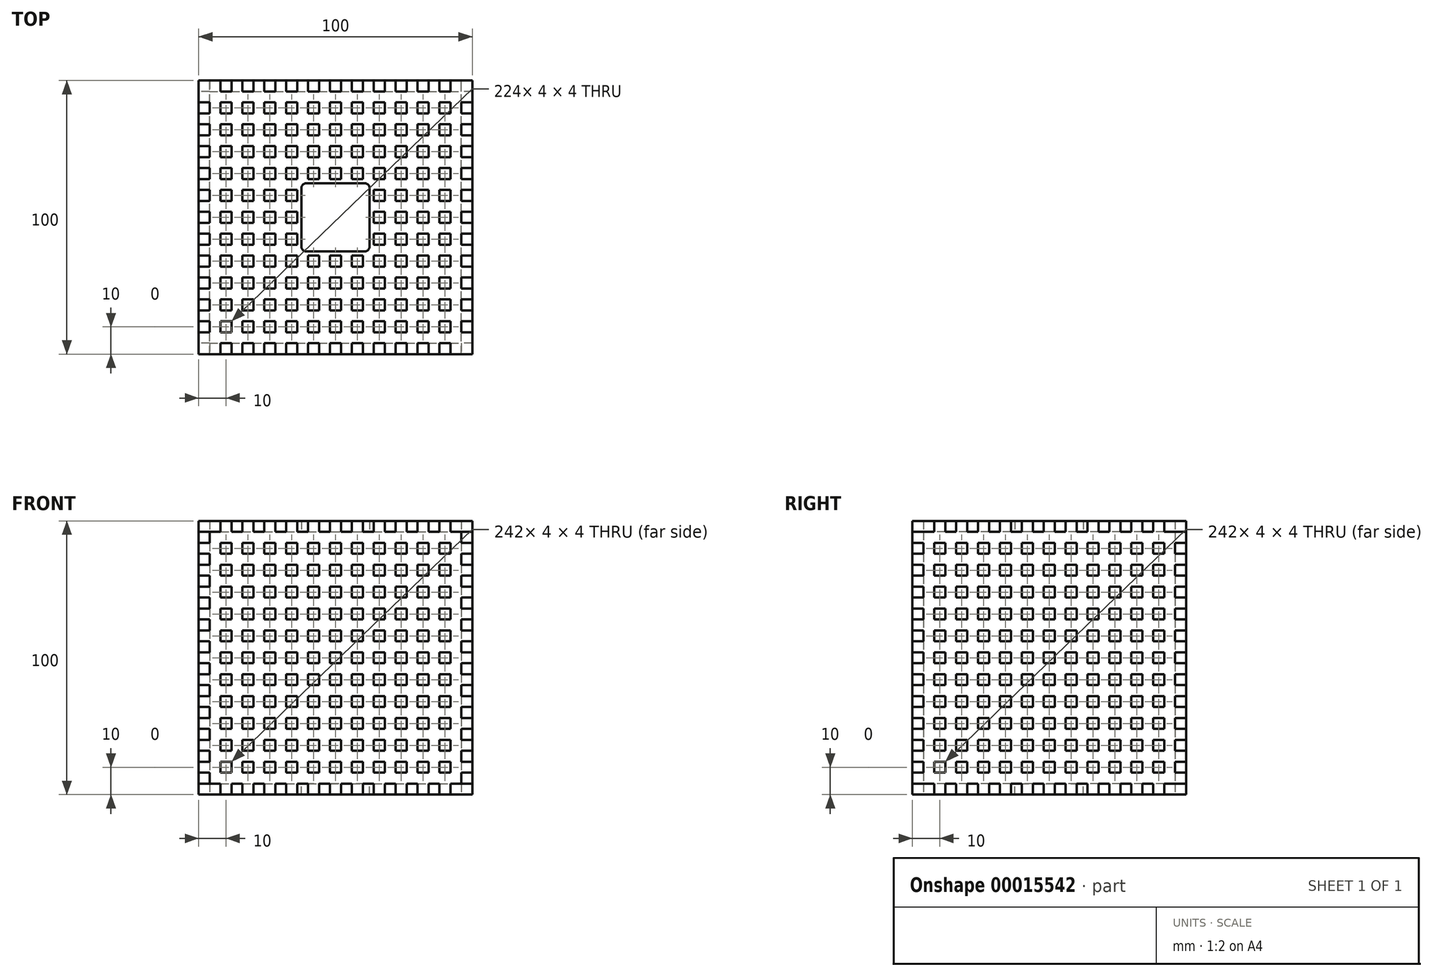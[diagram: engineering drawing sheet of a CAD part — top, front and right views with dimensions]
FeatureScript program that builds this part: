
annotation { "Feature Type Name" : "Feature", "Feature Type Description" : "" }
export const myFeature = defineFeature(function(context is Context, id is Id, definition is map)
    precondition{}
    {
        {
            var Q0;
            Q0=qCreatedBy(makeId("Top.planeOp"),FACE);
            var sketch = newSketch(context, id + "F0", { "sketchPlane" : qUnion([Q0])});
            skLineSegment(sketch, "E0.bottom", {"start": v(-50, 50) * mm, "end": v(-46, 50) * mm});
            skLineSegment(sketch, "E0.top", {"start": v(-50, 46) * mm, "end": v(-46, 46) * mm});
            skLineSegment(sketch, "E0.left", {"start": v(-50, 50) * mm, "end": v(-50, 46) * mm});
            skLineSegment(sketch, "E0.right", {"start": v(-46, 50) * mm, "end": v(-46, 46) * mm});
            skLineSegment(sketch, "E1.0.1.4", {"start": v(-46, 42) * mm, "end": v(-46, 38) * mm});
            skLineSegment(sketch, "E1.0.1.6", {"start": v(-50, 42) * mm, "end": v(-50, 38) * mm});
            skLineSegment(sketch, "E1.0.1.8", {"start": v(-50, 38) * mm, "end": v(-46, 38) * mm});
            skLineSegment(sketch, "E1.0.1.10", {"start": v(-50, 42) * mm, "end": v(-46, 42) * mm});
            skLineSegment(sketch, "E1.0.2.4", {"start": v(-46, 34) * mm, "end": v(-46, 30) * mm});
            skLineSegment(sketch, "E1.0.2.6", {"start": v(-50, 34) * mm, "end": v(-50, 30) * mm});
            skLineSegment(sketch, "E1.0.2.8", {"start": v(-50, 30) * mm, "end": v(-46, 30) * mm});
            skLineSegment(sketch, "E1.0.2.10", {"start": v(-50, 34) * mm, "end": v(-46, 34) * mm});
            skLineSegment(sketch, "E1.0.3.4", {"start": v(-46, 26) * mm, "end": v(-46, 22) * mm});
            skLineSegment(sketch, "E1.0.3.6", {"start": v(-50, 26) * mm, "end": v(-50, 22) * mm});
            skLineSegment(sketch, "E1.0.3.8", {"start": v(-50, 22) * mm, "end": v(-46, 22) * mm});
            skLineSegment(sketch, "E1.0.3.10", {"start": v(-50, 26) * mm, "end": v(-46, 26) * mm});
            skLineSegment(sketch, "E1.0.4.4", {"start": v(-46, 18) * mm, "end": v(-46, 14) * mm});
            skLineSegment(sketch, "E1.0.4.6", {"start": v(-50, 18) * mm, "end": v(-50, 14) * mm});
            skLineSegment(sketch, "E1.0.4.8", {"start": v(-50, 14) * mm, "end": v(-46, 14) * mm});
            skLineSegment(sketch, "E1.0.4.10", {"start": v(-50, 18) * mm, "end": v(-46, 18) * mm});
            skLineSegment(sketch, "E1.0.5.4", {"start": v(-46, 10) * mm, "end": v(-46, 6) * mm});
            skLineSegment(sketch, "E1.0.5.6", {"start": v(-50, 10) * mm, "end": v(-50, 6) * mm});
            skLineSegment(sketch, "E1.0.5.8", {"start": v(-50, 6) * mm, "end": v(-46, 6) * mm});
            skLineSegment(sketch, "E1.0.5.10", {"start": v(-50, 10) * mm, "end": v(-46, 10) * mm});
            skLineSegment(sketch, "E1.0.6.4", {"start": v(-46, 2) * mm, "end": v(-46, -2) * mm});
            skLineSegment(sketch, "E1.0.6.6", {"start": v(-50, 2) * mm, "end": v(-50, -2) * mm});
            skLineSegment(sketch, "E1.0.6.8", {"start": v(-50, -2) * mm, "end": v(-46, -2) * mm});
            skLineSegment(sketch, "E1.0.6.10", {"start": v(-50, 2) * mm, "end": v(-46, 2) * mm});
            skLineSegment(sketch, "E1.0.7.4", {"start": v(-46, -6) * mm, "end": v(-46, -10) * mm});
            skLineSegment(sketch, "E1.0.7.6", {"start": v(-50, -6) * mm, "end": v(-50, -10) * mm});
            skLineSegment(sketch, "E1.0.7.8", {"start": v(-50, -10) * mm, "end": v(-46, -10) * mm});
            skLineSegment(sketch, "E1.0.7.10", {"start": v(-50, -6) * mm, "end": v(-46, -6) * mm});
            skLineSegment(sketch, "E1.0.8.4", {"start": v(-46, -14) * mm, "end": v(-46, -18) * mm});
            skLineSegment(sketch, "E1.0.8.6", {"start": v(-50, -14) * mm, "end": v(-50, -18) * mm});
            skLineSegment(sketch, "E1.0.8.8", {"start": v(-50, -18) * mm, "end": v(-46, -18) * mm});
            skLineSegment(sketch, "E1.0.8.10", {"start": v(-50, -14) * mm, "end": v(-46, -14) * mm});
            skLineSegment(sketch, "E1.0.9.4", {"start": v(-46, -22) * mm, "end": v(-46, -26) * mm});
            skLineSegment(sketch, "E1.0.9.6", {"start": v(-50, -22) * mm, "end": v(-50, -26) * mm});
            skLineSegment(sketch, "E1.0.9.8", {"start": v(-50, -26) * mm, "end": v(-46, -26) * mm});
            skLineSegment(sketch, "E1.0.9.10", {"start": v(-50, -22) * mm, "end": v(-46, -22) * mm});
            skLineSegment(sketch, "E1.0.10.4", {"start": v(-46, -30) * mm, "end": v(-46, -34) * mm});
            skLineSegment(sketch, "E1.0.10.6", {"start": v(-50, -30) * mm, "end": v(-50, -34) * mm});
            skLineSegment(sketch, "E1.0.10.8", {"start": v(-50, -34) * mm, "end": v(-46, -34) * mm});
            skLineSegment(sketch, "E1.0.10.10", {"start": v(-50, -30) * mm, "end": v(-46, -30) * mm});
            skLineSegment(sketch, "E1.0.11.4", {"start": v(-46, -38) * mm, "end": v(-46, -42) * mm});
            skLineSegment(sketch, "E1.0.11.6", {"start": v(-50, -38) * mm, "end": v(-50, -42) * mm});
            skLineSegment(sketch, "E1.0.11.8", {"start": v(-50, -42) * mm, "end": v(-46, -42) * mm});
            skLineSegment(sketch, "E1.0.11.10", {"start": v(-50, -38) * mm, "end": v(-46, -38) * mm});
            skLineSegment(sketch, "E1.0.12.4", {"start": v(-46, -46) * mm, "end": v(-46, -50) * mm});
            skLineSegment(sketch, "E1.0.12.6", {"start": v(-50, -46) * mm, "end": v(-50, -50) * mm});
            skLineSegment(sketch, "E1.0.12.8", {"start": v(-50, -50) * mm, "end": v(-46, -50) * mm});
            skLineSegment(sketch, "E1.0.12.10", {"start": v(-50, -46) * mm, "end": v(-46, -46) * mm});
            skLineSegment(sketch, "E1.1.0.4", {"start": v(-38, 50) * mm, "end": v(-38, 46) * mm});
            skLineSegment(sketch, "E1.1.0.6", {"start": v(-42, 50) * mm, "end": v(-42, 46) * mm});
            skLineSegment(sketch, "E1.1.0.8", {"start": v(-42, 46) * mm, "end": v(-38, 46) * mm});
            skLineSegment(sketch, "E1.1.0.10", {"start": v(-42, 50) * mm, "end": v(-38, 50) * mm});
            skLineSegment(sketch, "E1.1.1.4", {"start": v(-38, 42) * mm, "end": v(-38, 38) * mm});
            skLineSegment(sketch, "E1.1.1.6", {"start": v(-42, 42) * mm, "end": v(-42, 38) * mm});
            skLineSegment(sketch, "E1.1.1.8", {"start": v(-42, 38) * mm, "end": v(-38, 38) * mm});
            skLineSegment(sketch, "E1.1.1.10", {"start": v(-42, 42) * mm, "end": v(-38, 42) * mm});
            skLineSegment(sketch, "E1.1.2.4", {"start": v(-38, 34) * mm, "end": v(-38, 30) * mm});
            skLineSegment(sketch, "E1.1.2.6", {"start": v(-42, 34) * mm, "end": v(-42, 30) * mm});
            skLineSegment(sketch, "E1.1.2.8", {"start": v(-42, 30) * mm, "end": v(-38, 30) * mm});
            skLineSegment(sketch, "E1.1.2.10", {"start": v(-42, 34) * mm, "end": v(-38, 34) * mm});
            skLineSegment(sketch, "E1.1.3.4", {"start": v(-38, 26) * mm, "end": v(-38, 22) * mm});
            skLineSegment(sketch, "E1.1.3.6", {"start": v(-42, 26) * mm, "end": v(-42, 22) * mm});
            skLineSegment(sketch, "E1.1.3.8", {"start": v(-42, 22) * mm, "end": v(-38, 22) * mm});
            skLineSegment(sketch, "E1.1.3.10", {"start": v(-42, 26) * mm, "end": v(-38, 26) * mm});
            skLineSegment(sketch, "E1.1.4.4", {"start": v(-38, 18) * mm, "end": v(-38, 14) * mm});
            skLineSegment(sketch, "E1.1.4.6", {"start": v(-42, 18) * mm, "end": v(-42, 14) * mm});
            skLineSegment(sketch, "E1.1.4.8", {"start": v(-42, 14) * mm, "end": v(-38, 14) * mm});
            skLineSegment(sketch, "E1.1.4.10", {"start": v(-42, 18) * mm, "end": v(-38, 18) * mm});
            skLineSegment(sketch, "E1.1.5.4", {"start": v(-38, 10) * mm, "end": v(-38, 6) * mm});
            skLineSegment(sketch, "E1.1.5.6", {"start": v(-42, 10) * mm, "end": v(-42, 6) * mm});
            skLineSegment(sketch, "E1.1.5.8", {"start": v(-42, 6) * mm, "end": v(-38, 6) * mm});
            skLineSegment(sketch, "E1.1.5.10", {"start": v(-42, 10) * mm, "end": v(-38, 10) * mm});
            skLineSegment(sketch, "E1.1.6.4", {"start": v(-38, 2) * mm, "end": v(-38, -2) * mm});
            skLineSegment(sketch, "E1.1.6.6", {"start": v(-42, 2) * mm, "end": v(-42, -2) * mm});
            skLineSegment(sketch, "E1.1.6.8", {"start": v(-42, -2) * mm, "end": v(-38, -2) * mm});
            skLineSegment(sketch, "E1.1.6.10", {"start": v(-42, 2) * mm, "end": v(-38, 2) * mm});
            skLineSegment(sketch, "E1.1.7.4", {"start": v(-38, -6) * mm, "end": v(-38, -10) * mm});
            skLineSegment(sketch, "E1.1.7.6", {"start": v(-42, -6) * mm, "end": v(-42, -10) * mm});
            skLineSegment(sketch, "E1.1.7.8", {"start": v(-42, -10) * mm, "end": v(-38, -10) * mm});
            skLineSegment(sketch, "E1.1.7.10", {"start": v(-42, -6) * mm, "end": v(-38, -6) * mm});
            skLineSegment(sketch, "E1.1.8.4", {"start": v(-38, -14) * mm, "end": v(-38, -18) * mm});
            skLineSegment(sketch, "E1.1.8.6", {"start": v(-42, -14) * mm, "end": v(-42, -18) * mm});
            skLineSegment(sketch, "E1.1.8.8", {"start": v(-42, -18) * mm, "end": v(-38, -18) * mm});
            skLineSegment(sketch, "E1.1.8.10", {"start": v(-42, -14) * mm, "end": v(-38, -14) * mm});
            skLineSegment(sketch, "E1.1.9.4", {"start": v(-38, -22) * mm, "end": v(-38, -26) * mm});
            skLineSegment(sketch, "E1.1.9.6", {"start": v(-42, -22) * mm, "end": v(-42, -26) * mm});
            skLineSegment(sketch, "E1.1.9.8", {"start": v(-42, -26) * mm, "end": v(-38, -26) * mm});
            skLineSegment(sketch, "E1.1.9.10", {"start": v(-42, -22) * mm, "end": v(-38, -22) * mm});
            skLineSegment(sketch, "E1.1.10.4", {"start": v(-38, -30) * mm, "end": v(-38, -34) * mm});
            skLineSegment(sketch, "E1.1.10.6", {"start": v(-42, -30) * mm, "end": v(-42, -34) * mm});
            skLineSegment(sketch, "E1.1.10.8", {"start": v(-42, -34) * mm, "end": v(-38, -34) * mm});
            skLineSegment(sketch, "E1.1.10.10", {"start": v(-42, -30) * mm, "end": v(-38, -30) * mm});
            skLineSegment(sketch, "E1.1.11.4", {"start": v(-38, -38) * mm, "end": v(-38, -42) * mm});
            skLineSegment(sketch, "E1.1.11.6", {"start": v(-42, -38) * mm, "end": v(-42, -42) * mm});
            skLineSegment(sketch, "E1.1.11.8", {"start": v(-42, -42) * mm, "end": v(-38, -42) * mm});
            skLineSegment(sketch, "E1.1.11.10", {"start": v(-42, -38) * mm, "end": v(-38, -38) * mm});
            skLineSegment(sketch, "E1.1.12.4", {"start": v(-38, -46) * mm, "end": v(-38, -50) * mm});
            skLineSegment(sketch, "E1.1.12.6", {"start": v(-42, -46) * mm, "end": v(-42, -50) * mm});
            skLineSegment(sketch, "E1.1.12.8", {"start": v(-42, -50) * mm, "end": v(-38, -50) * mm});
            skLineSegment(sketch, "E1.1.12.10", {"start": v(-42, -46) * mm, "end": v(-38, -46) * mm});
            skLineSegment(sketch, "E1.2.0.4", {"start": v(-30, 50) * mm, "end": v(-30, 46) * mm});
            skLineSegment(sketch, "E1.2.0.6", {"start": v(-34, 50) * mm, "end": v(-34, 46) * mm});
            skLineSegment(sketch, "E1.2.0.8", {"start": v(-34, 46) * mm, "end": v(-30, 46) * mm});
            skLineSegment(sketch, "E1.2.0.10", {"start": v(-34, 50) * mm, "end": v(-30, 50) * mm});
            skLineSegment(sketch, "E1.2.1.4", {"start": v(-30, 42) * mm, "end": v(-30, 38) * mm});
            skLineSegment(sketch, "E1.2.1.6", {"start": v(-34, 42) * mm, "end": v(-34, 38) * mm});
            skLineSegment(sketch, "E1.2.1.8", {"start": v(-34, 38) * mm, "end": v(-30, 38) * mm});
            skLineSegment(sketch, "E1.2.1.10", {"start": v(-34, 42) * mm, "end": v(-30, 42) * mm});
            skLineSegment(sketch, "E1.2.2.4", {"start": v(-30, 34) * mm, "end": v(-30, 30) * mm});
            skLineSegment(sketch, "E1.2.2.6", {"start": v(-34, 34) * mm, "end": v(-34, 30) * mm});
            skLineSegment(sketch, "E1.2.2.8", {"start": v(-34, 30) * mm, "end": v(-30, 30) * mm});
            skLineSegment(sketch, "E1.2.2.10", {"start": v(-34, 34) * mm, "end": v(-30, 34) * mm});
            skLineSegment(sketch, "E1.2.3.4", {"start": v(-30, 26) * mm, "end": v(-30, 22) * mm});
            skLineSegment(sketch, "E1.2.3.6", {"start": v(-34, 26) * mm, "end": v(-34, 22) * mm});
            skLineSegment(sketch, "E1.2.3.8", {"start": v(-34, 22) * mm, "end": v(-30, 22) * mm});
            skLineSegment(sketch, "E1.2.3.10", {"start": v(-34, 26) * mm, "end": v(-30, 26) * mm});
            skLineSegment(sketch, "E1.2.4.4", {"start": v(-30, 18) * mm, "end": v(-30, 14) * mm});
            skLineSegment(sketch, "E1.2.4.6", {"start": v(-34, 18) * mm, "end": v(-34, 14) * mm});
            skLineSegment(sketch, "E1.2.4.8", {"start": v(-34, 14) * mm, "end": v(-30, 14) * mm});
            skLineSegment(sketch, "E1.2.4.10", {"start": v(-34, 18) * mm, "end": v(-30, 18) * mm});
            skLineSegment(sketch, "E1.2.5.4", {"start": v(-30, 10) * mm, "end": v(-30, 6) * mm});
            skLineSegment(sketch, "E1.2.5.6", {"start": v(-34, 10) * mm, "end": v(-34, 6) * mm});
            skLineSegment(sketch, "E1.2.5.8", {"start": v(-34, 6) * mm, "end": v(-30, 6) * mm});
            skLineSegment(sketch, "E1.2.5.10", {"start": v(-34, 10) * mm, "end": v(-30, 10) * mm});
            skLineSegment(sketch, "E1.2.6.4", {"start": v(-30, 2) * mm, "end": v(-30, -2) * mm});
            skLineSegment(sketch, "E1.2.6.6", {"start": v(-34, 2) * mm, "end": v(-34, -2) * mm});
            skLineSegment(sketch, "E1.2.6.8", {"start": v(-34, -2) * mm, "end": v(-30, -2) * mm});
            skLineSegment(sketch, "E1.2.6.10", {"start": v(-34, 2) * mm, "end": v(-30, 2) * mm});
            skLineSegment(sketch, "E1.2.7.4", {"start": v(-30, -6) * mm, "end": v(-30, -10) * mm});
            skLineSegment(sketch, "E1.2.7.6", {"start": v(-34, -6) * mm, "end": v(-34, -10) * mm});
            skLineSegment(sketch, "E1.2.7.8", {"start": v(-34, -10) * mm, "end": v(-30, -10) * mm});
            skLineSegment(sketch, "E1.2.7.10", {"start": v(-34, -6) * mm, "end": v(-30, -6) * mm});
            skLineSegment(sketch, "E1.2.8.4", {"start": v(-30, -14) * mm, "end": v(-30, -18) * mm});
            skLineSegment(sketch, "E1.2.8.6", {"start": v(-34, -14) * mm, "end": v(-34, -18) * mm});
            skLineSegment(sketch, "E1.2.8.8", {"start": v(-34, -18) * mm, "end": v(-30, -18) * mm});
            skLineSegment(sketch, "E1.2.8.10", {"start": v(-34, -14) * mm, "end": v(-30, -14) * mm});
            skLineSegment(sketch, "E1.2.9.4", {"start": v(-30, -22) * mm, "end": v(-30, -26) * mm});
            skLineSegment(sketch, "E1.2.9.6", {"start": v(-34, -22) * mm, "end": v(-34, -26) * mm});
            skLineSegment(sketch, "E1.2.9.8", {"start": v(-34, -26) * mm, "end": v(-30, -26) * mm});
            skLineSegment(sketch, "E1.2.9.10", {"start": v(-34, -22) * mm, "end": v(-30, -22) * mm});
            skLineSegment(sketch, "E1.2.10.4", {"start": v(-30, -30) * mm, "end": v(-30, -34) * mm});
            skLineSegment(sketch, "E1.2.10.6", {"start": v(-34, -30) * mm, "end": v(-34, -34) * mm});
            skLineSegment(sketch, "E1.2.10.8", {"start": v(-34, -34) * mm, "end": v(-30, -34) * mm});
            skLineSegment(sketch, "E1.2.10.10", {"start": v(-34, -30) * mm, "end": v(-30, -30) * mm});
            skLineSegment(sketch, "E1.2.11.4", {"start": v(-30, -38) * mm, "end": v(-30, -42) * mm});
            skLineSegment(sketch, "E1.2.11.6", {"start": v(-34, -38) * mm, "end": v(-34, -42) * mm});
            skLineSegment(sketch, "E1.2.11.8", {"start": v(-34, -42) * mm, "end": v(-30, -42) * mm});
            skLineSegment(sketch, "E1.2.11.10", {"start": v(-34, -38) * mm, "end": v(-30, -38) * mm});
            skLineSegment(sketch, "E1.2.12.4", {"start": v(-30, -46) * mm, "end": v(-30, -50) * mm});
            skLineSegment(sketch, "E1.2.12.6", {"start": v(-34, -46) * mm, "end": v(-34, -50) * mm});
            skLineSegment(sketch, "E1.2.12.8", {"start": v(-34, -50) * mm, "end": v(-30, -50) * mm});
            skLineSegment(sketch, "E1.2.12.10", {"start": v(-34, -46) * mm, "end": v(-30, -46) * mm});
            skLineSegment(sketch, "E1.3.0.4", {"start": v(-22, 50) * mm, "end": v(-22, 46) * mm});
            skLineSegment(sketch, "E1.3.0.6", {"start": v(-26, 50) * mm, "end": v(-26, 46) * mm});
            skLineSegment(sketch, "E1.3.0.8", {"start": v(-26, 46) * mm, "end": v(-22, 46) * mm});
            skLineSegment(sketch, "E1.3.0.10", {"start": v(-26, 50) * mm, "end": v(-22, 50) * mm});
            skLineSegment(sketch, "E1.3.1.4", {"start": v(-22, 42) * mm, "end": v(-22, 38) * mm});
            skLineSegment(sketch, "E1.3.1.6", {"start": v(-26, 42) * mm, "end": v(-26, 38) * mm});
            skLineSegment(sketch, "E1.3.1.8", {"start": v(-26, 38) * mm, "end": v(-22, 38) * mm});
            skLineSegment(sketch, "E1.3.1.10", {"start": v(-26, 42) * mm, "end": v(-22, 42) * mm});
            skLineSegment(sketch, "E1.3.2.4", {"start": v(-22, 34) * mm, "end": v(-22, 30) * mm});
            skLineSegment(sketch, "E1.3.2.6", {"start": v(-26, 34) * mm, "end": v(-26, 30) * mm});
            skLineSegment(sketch, "E1.3.2.8", {"start": v(-26, 30) * mm, "end": v(-22, 30) * mm});
            skLineSegment(sketch, "E1.3.2.10", {"start": v(-26, 34) * mm, "end": v(-22, 34) * mm});
            skLineSegment(sketch, "E1.3.3.4", {"start": v(-22, 26) * mm, "end": v(-22, 22) * mm});
            skLineSegment(sketch, "E1.3.3.6", {"start": v(-26, 26) * mm, "end": v(-26, 22) * mm});
            skLineSegment(sketch, "E1.3.3.8", {"start": v(-26, 22) * mm, "end": v(-22, 22) * mm});
            skLineSegment(sketch, "E1.3.3.10", {"start": v(-26, 26) * mm, "end": v(-22, 26) * mm});
            skLineSegment(sketch, "E1.3.4.4", {"start": v(-22, 18) * mm, "end": v(-22, 14) * mm});
            skLineSegment(sketch, "E1.3.4.6", {"start": v(-26, 18) * mm, "end": v(-26, 14) * mm});
            skLineSegment(sketch, "E1.3.4.8", {"start": v(-26, 14) * mm, "end": v(-22, 14) * mm});
            skLineSegment(sketch, "E1.3.4.10", {"start": v(-26, 18) * mm, "end": v(-22, 18) * mm});
            skLineSegment(sketch, "E1.3.5.4", {"start": v(-22, 10) * mm, "end": v(-22, 6) * mm});
            skLineSegment(sketch, "E1.3.5.6", {"start": v(-26, 10) * mm, "end": v(-26, 6) * mm});
            skLineSegment(sketch, "E1.3.5.8", {"start": v(-26, 6) * mm, "end": v(-22, 6) * mm});
            skLineSegment(sketch, "E1.3.5.10", {"start": v(-26, 10) * mm, "end": v(-22, 10) * mm});
            skLineSegment(sketch, "E1.3.6.4", {"start": v(-22, 2) * mm, "end": v(-22, -2) * mm});
            skLineSegment(sketch, "E1.3.6.6", {"start": v(-26, 2) * mm, "end": v(-26, -2) * mm});
            skLineSegment(sketch, "E1.3.6.8", {"start": v(-26, -2) * mm, "end": v(-22, -2) * mm});
            skLineSegment(sketch, "E1.3.6.10", {"start": v(-26, 2) * mm, "end": v(-22, 2) * mm});
            skLineSegment(sketch, "E1.3.7.4", {"start": v(-22, -6) * mm, "end": v(-22, -10) * mm});
            skLineSegment(sketch, "E1.3.7.6", {"start": v(-26, -6) * mm, "end": v(-26, -10) * mm});
            skLineSegment(sketch, "E1.3.7.8", {"start": v(-26, -10) * mm, "end": v(-22, -10) * mm});
            skLineSegment(sketch, "E1.3.7.10", {"start": v(-26, -6) * mm, "end": v(-22, -6) * mm});
            skLineSegment(sketch, "E1.3.8.4", {"start": v(-22, -14) * mm, "end": v(-22, -18) * mm});
            skLineSegment(sketch, "E1.3.8.6", {"start": v(-26, -14) * mm, "end": v(-26, -18) * mm});
            skLineSegment(sketch, "E1.3.8.8", {"start": v(-26, -18) * mm, "end": v(-22, -18) * mm});
            skLineSegment(sketch, "E1.3.8.10", {"start": v(-26, -14) * mm, "end": v(-22, -14) * mm});
            skLineSegment(sketch, "E1.3.9.4", {"start": v(-22, -22) * mm, "end": v(-22, -26) * mm});
            skLineSegment(sketch, "E1.3.9.6", {"start": v(-26, -22) * mm, "end": v(-26, -26) * mm});
            skLineSegment(sketch, "E1.3.9.8", {"start": v(-26, -26) * mm, "end": v(-22, -26) * mm});
            skLineSegment(sketch, "E1.3.9.10", {"start": v(-26, -22) * mm, "end": v(-22, -22) * mm});
            skLineSegment(sketch, "E1.3.10.4", {"start": v(-22, -30) * mm, "end": v(-22, -34) * mm});
            skLineSegment(sketch, "E1.3.10.6", {"start": v(-26, -30) * mm, "end": v(-26, -34) * mm});
            skLineSegment(sketch, "E1.3.10.8", {"start": v(-26, -34) * mm, "end": v(-22, -34) * mm});
            skLineSegment(sketch, "E1.3.10.10", {"start": v(-26, -30) * mm, "end": v(-22, -30) * mm});
            skLineSegment(sketch, "E1.3.11.4", {"start": v(-22, -38) * mm, "end": v(-22, -42) * mm});
            skLineSegment(sketch, "E1.3.11.6", {"start": v(-26, -38) * mm, "end": v(-26, -42) * mm});
            skLineSegment(sketch, "E1.3.11.8", {"start": v(-26, -42) * mm, "end": v(-22, -42) * mm});
            skLineSegment(sketch, "E1.3.11.10", {"start": v(-26, -38) * mm, "end": v(-22, -38) * mm});
            skLineSegment(sketch, "E1.3.12.4", {"start": v(-22, -46) * mm, "end": v(-22, -50) * mm});
            skLineSegment(sketch, "E1.3.12.6", {"start": v(-26, -46) * mm, "end": v(-26, -50) * mm});
            skLineSegment(sketch, "E1.3.12.8", {"start": v(-26, -50) * mm, "end": v(-22, -50) * mm});
            skLineSegment(sketch, "E1.3.12.10", {"start": v(-26, -46) * mm, "end": v(-22, -46) * mm});
            skLineSegment(sketch, "E1.4.0.4", {"start": v(-14, 50) * mm, "end": v(-14, 46) * mm});
            skLineSegment(sketch, "E1.4.0.6", {"start": v(-18, 50) * mm, "end": v(-18, 46) * mm});
            skLineSegment(sketch, "E1.4.0.8", {"start": v(-18, 46) * mm, "end": v(-14, 46) * mm});
            skLineSegment(sketch, "E1.4.0.10", {"start": v(-18, 50) * mm, "end": v(-14, 50) * mm});
            skLineSegment(sketch, "E1.4.1.4", {"start": v(-14, 42) * mm, "end": v(-14, 38) * mm});
            skLineSegment(sketch, "E1.4.1.6", {"start": v(-18, 42) * mm, "end": v(-18, 38) * mm});
            skLineSegment(sketch, "E1.4.1.8", {"start": v(-18, 38) * mm, "end": v(-14, 38) * mm});
            skLineSegment(sketch, "E1.4.1.10", {"start": v(-18, 42) * mm, "end": v(-14, 42) * mm});
            skLineSegment(sketch, "E1.4.2.4", {"start": v(-14, 34) * mm, "end": v(-14, 30) * mm});
            skLineSegment(sketch, "E1.4.2.6", {"start": v(-18, 34) * mm, "end": v(-18, 30) * mm});
            skLineSegment(sketch, "E1.4.2.8", {"start": v(-18, 30) * mm, "end": v(-14, 30) * mm});
            skLineSegment(sketch, "E1.4.2.10", {"start": v(-18, 34) * mm, "end": v(-14, 34) * mm});
            skLineSegment(sketch, "E1.4.3.4", {"start": v(-14, 26) * mm, "end": v(-14, 22) * mm});
            skLineSegment(sketch, "E1.4.3.6", {"start": v(-18, 26) * mm, "end": v(-18, 22) * mm});
            skLineSegment(sketch, "E1.4.3.8", {"start": v(-18, 22) * mm, "end": v(-14, 22) * mm});
            skLineSegment(sketch, "E1.4.3.10", {"start": v(-18, 26) * mm, "end": v(-14, 26) * mm});
            skLineSegment(sketch, "E1.4.4.4", {"start": v(-14, 18) * mm, "end": v(-14, 14) * mm});
            skLineSegment(sketch, "E1.4.4.6", {"start": v(-18, 18) * mm, "end": v(-18, 14) * mm});
            skLineSegment(sketch, "E1.4.4.8", {"start": v(-18, 14) * mm, "end": v(-14, 14) * mm});
            skLineSegment(sketch, "E1.4.4.10", {"start": v(-18, 18) * mm, "end": v(-14, 18) * mm});
            skLineSegment(sketch, "E1.4.5.4", {"start": v(-14, 10) * mm, "end": v(-14, 6) * mm});
            skLineSegment(sketch, "E1.4.5.6", {"start": v(-18, 10) * mm, "end": v(-18, 6) * mm});
            skLineSegment(sketch, "E1.4.5.8", {"start": v(-18, 6) * mm, "end": v(-14, 6) * mm});
            skLineSegment(sketch, "E1.4.5.10", {"start": v(-18, 10) * mm, "end": v(-14, 10) * mm});
            skLineSegment(sketch, "E1.4.6.4", {"start": v(-14, 2) * mm, "end": v(-14, -2) * mm});
            skLineSegment(sketch, "E1.4.6.6", {"start": v(-18, 2) * mm, "end": v(-18, -2) * mm});
            skLineSegment(sketch, "E1.4.6.8", {"start": v(-18, -2) * mm, "end": v(-14, -2) * mm});
            skLineSegment(sketch, "E1.4.6.10", {"start": v(-18, 2) * mm, "end": v(-14, 2) * mm});
            skLineSegment(sketch, "E1.4.7.4", {"start": v(-14, -6) * mm, "end": v(-14, -10) * mm});
            skLineSegment(sketch, "E1.4.7.6", {"start": v(-18, -6) * mm, "end": v(-18, -10) * mm});
            skLineSegment(sketch, "E1.4.7.8", {"start": v(-18, -10) * mm, "end": v(-14, -10) * mm});
            skLineSegment(sketch, "E1.4.7.10", {"start": v(-18, -6) * mm, "end": v(-14, -6) * mm});
            skLineSegment(sketch, "E1.4.8.4", {"start": v(-14, -14) * mm, "end": v(-14, -18) * mm});
            skLineSegment(sketch, "E1.4.8.6", {"start": v(-18, -14) * mm, "end": v(-18, -18) * mm});
            skLineSegment(sketch, "E1.4.8.8", {"start": v(-18, -18) * mm, "end": v(-14, -18) * mm});
            skLineSegment(sketch, "E1.4.8.10", {"start": v(-18, -14) * mm, "end": v(-14, -14) * mm});
            skLineSegment(sketch, "E1.4.9.4", {"start": v(-14, -22) * mm, "end": v(-14, -26) * mm});
            skLineSegment(sketch, "E1.4.9.6", {"start": v(-18, -22) * mm, "end": v(-18, -26) * mm});
            skLineSegment(sketch, "E1.4.9.8", {"start": v(-18, -26) * mm, "end": v(-14, -26) * mm});
            skLineSegment(sketch, "E1.4.9.10", {"start": v(-18, -22) * mm, "end": v(-14, -22) * mm});
            skLineSegment(sketch, "E1.4.10.4", {"start": v(-14, -30) * mm, "end": v(-14, -34) * mm});
            skLineSegment(sketch, "E1.4.10.6", {"start": v(-18, -30) * mm, "end": v(-18, -34) * mm});
            skLineSegment(sketch, "E1.4.10.8", {"start": v(-18, -34) * mm, "end": v(-14, -34) * mm});
            skLineSegment(sketch, "E1.4.10.10", {"start": v(-18, -30) * mm, "end": v(-14, -30) * mm});
            skLineSegment(sketch, "E1.4.11.4", {"start": v(-14, -38) * mm, "end": v(-14, -42) * mm});
            skLineSegment(sketch, "E1.4.11.6", {"start": v(-18, -38) * mm, "end": v(-18, -42) * mm});
            skLineSegment(sketch, "E1.4.11.8", {"start": v(-18, -42) * mm, "end": v(-14, -42) * mm});
            skLineSegment(sketch, "E1.4.11.10", {"start": v(-18, -38) * mm, "end": v(-14, -38) * mm});
            skLineSegment(sketch, "E1.4.12.4", {"start": v(-14, -46) * mm, "end": v(-14, -50) * mm});
            skLineSegment(sketch, "E1.4.12.6", {"start": v(-18, -46) * mm, "end": v(-18, -50) * mm});
            skLineSegment(sketch, "E1.4.12.8", {"start": v(-18, -50) * mm, "end": v(-14, -50) * mm});
            skLineSegment(sketch, "E1.4.12.10", {"start": v(-18, -46) * mm, "end": v(-14, -46) * mm});
            skLineSegment(sketch, "E1.5.0.4", {"start": v(-6, 50) * mm, "end": v(-6, 46) * mm});
            skLineSegment(sketch, "E1.5.0.6", {"start": v(-10, 50) * mm, "end": v(-10, 46) * mm});
            skLineSegment(sketch, "E1.5.0.8", {"start": v(-10, 46) * mm, "end": v(-6, 46) * mm});
            skLineSegment(sketch, "E1.5.0.10", {"start": v(-10, 50) * mm, "end": v(-6, 50) * mm});
            skLineSegment(sketch, "E1.5.1.4", {"start": v(-6, 42) * mm, "end": v(-6, 38) * mm});
            skLineSegment(sketch, "E1.5.1.6", {"start": v(-10, 42) * mm, "end": v(-10, 38) * mm});
            skLineSegment(sketch, "E1.5.1.8", {"start": v(-10, 38) * mm, "end": v(-6, 38) * mm});
            skLineSegment(sketch, "E1.5.1.10", {"start": v(-10, 42) * mm, "end": v(-6, 42) * mm});
            skLineSegment(sketch, "E1.5.2.4", {"start": v(-6, 34) * mm, "end": v(-6, 30) * mm});
            skLineSegment(sketch, "E1.5.2.6", {"start": v(-10, 34) * mm, "end": v(-10, 30) * mm});
            skLineSegment(sketch, "E1.5.2.8", {"start": v(-10, 30) * mm, "end": v(-6, 30) * mm});
            skLineSegment(sketch, "E1.5.2.10", {"start": v(-10, 34) * mm, "end": v(-6, 34) * mm});
            skLineSegment(sketch, "E1.5.3.4", {"start": v(-6, 26) * mm, "end": v(-6, 22) * mm});
            skLineSegment(sketch, "E1.5.3.6", {"start": v(-10, 26) * mm, "end": v(-10, 22) * mm});
            skLineSegment(sketch, "E1.5.3.8", {"start": v(-10, 22) * mm, "end": v(-6, 22) * mm});
            skLineSegment(sketch, "E1.5.3.10", {"start": v(-10, 26) * mm, "end": v(-6, 26) * mm});
            skLineSegment(sketch, "E1.5.4.4", {"start": v(-6, 18) * mm, "end": v(-6, 14) * mm});
            skLineSegment(sketch, "E1.5.4.6", {"start": v(-10, 18) * mm, "end": v(-10, 14) * mm});
            skLineSegment(sketch, "E1.5.4.8", {"start": v(-10, 14) * mm, "end": v(-6, 14) * mm});
            skLineSegment(sketch, "E1.5.4.10", {"start": v(-10, 18) * mm, "end": v(-6, 18) * mm});
            skLineSegment(sketch, "E1.5.5.4", {"start": v(-6, 10) * mm, "end": v(-6, 6) * mm});
            skLineSegment(sketch, "E1.5.5.6", {"start": v(-10, 10) * mm, "end": v(-10, 6) * mm});
            skLineSegment(sketch, "E1.5.5.8", {"start": v(-10, 6) * mm, "end": v(-6, 6) * mm});
            skLineSegment(sketch, "E1.5.5.10", {"start": v(-10, 10) * mm, "end": v(-6, 10) * mm});
            skLineSegment(sketch, "E1.5.6.4", {"start": v(-6, 2) * mm, "end": v(-6, -2) * mm});
            skLineSegment(sketch, "E1.5.6.6", {"start": v(-10, 2) * mm, "end": v(-10, -2) * mm});
            skLineSegment(sketch, "E1.5.6.8", {"start": v(-10, -2) * mm, "end": v(-6, -2) * mm});
            skLineSegment(sketch, "E1.5.6.10", {"start": v(-10, 2) * mm, "end": v(-6, 2) * mm});
            skLineSegment(sketch, "E1.5.7.4", {"start": v(-6, -6) * mm, "end": v(-6, -10) * mm});
            skLineSegment(sketch, "E1.5.7.6", {"start": v(-10, -6) * mm, "end": v(-10, -10) * mm});
            skLineSegment(sketch, "E1.5.7.8", {"start": v(-10, -10) * mm, "end": v(-6, -10) * mm});
            skLineSegment(sketch, "E1.5.7.10", {"start": v(-10, -6) * mm, "end": v(-6, -6) * mm});
            skLineSegment(sketch, "E1.5.8.4", {"start": v(-6, -14) * mm, "end": v(-6, -18) * mm});
            skLineSegment(sketch, "E1.5.8.6", {"start": v(-10, -14) * mm, "end": v(-10, -18) * mm});
            skLineSegment(sketch, "E1.5.8.8", {"start": v(-10, -18) * mm, "end": v(-6, -18) * mm});
            skLineSegment(sketch, "E1.5.8.10", {"start": v(-10, -14) * mm, "end": v(-6, -14) * mm});
            skLineSegment(sketch, "E1.5.9.4", {"start": v(-6, -22) * mm, "end": v(-6, -26) * mm});
            skLineSegment(sketch, "E1.5.9.6", {"start": v(-10, -22) * mm, "end": v(-10, -26) * mm});
            skLineSegment(sketch, "E1.5.9.8", {"start": v(-10, -26) * mm, "end": v(-6, -26) * mm});
            skLineSegment(sketch, "E1.5.9.10", {"start": v(-10, -22) * mm, "end": v(-6, -22) * mm});
            skLineSegment(sketch, "E1.5.10.4", {"start": v(-6, -30) * mm, "end": v(-6, -34) * mm});
            skLineSegment(sketch, "E1.5.10.6", {"start": v(-10, -30) * mm, "end": v(-10, -34) * mm});
            skLineSegment(sketch, "E1.5.10.8", {"start": v(-10, -34) * mm, "end": v(-6, -34) * mm});
            skLineSegment(sketch, "E1.5.10.10", {"start": v(-10, -30) * mm, "end": v(-6, -30) * mm});
            skLineSegment(sketch, "E1.5.11.4", {"start": v(-6, -38) * mm, "end": v(-6, -42) * mm});
            skLineSegment(sketch, "E1.5.11.6", {"start": v(-10, -38) * mm, "end": v(-10, -42) * mm});
            skLineSegment(sketch, "E1.5.11.8", {"start": v(-10, -42) * mm, "end": v(-6, -42) * mm});
            skLineSegment(sketch, "E1.5.11.10", {"start": v(-10, -38) * mm, "end": v(-6, -38) * mm});
            skLineSegment(sketch, "E1.5.12.4", {"start": v(-6, -46) * mm, "end": v(-6, -50) * mm});
            skLineSegment(sketch, "E1.5.12.6", {"start": v(-10, -46) * mm, "end": v(-10, -50) * mm});
            skLineSegment(sketch, "E1.5.12.8", {"start": v(-10, -50) * mm, "end": v(-6, -50) * mm});
            skLineSegment(sketch, "E1.5.12.10", {"start": v(-10, -46) * mm, "end": v(-6, -46) * mm});
            skLineSegment(sketch, "E1.6.0.4", {"start": v(2, 50) * mm, "end": v(2, 46) * mm});
            skLineSegment(sketch, "E1.6.0.6", {"start": v(-2, 50) * mm, "end": v(-2, 46) * mm});
            skLineSegment(sketch, "E1.6.0.8", {"start": v(-2, 46) * mm, "end": v(2, 46) * mm});
            skLineSegment(sketch, "E1.6.0.10", {"start": v(-2, 50) * mm, "end": v(2, 50) * mm});
            skLineSegment(sketch, "E1.6.1.4", {"start": v(2, 42) * mm, "end": v(2, 38) * mm});
            skLineSegment(sketch, "E1.6.1.6", {"start": v(-2, 42) * mm, "end": v(-2, 38) * mm});
            skLineSegment(sketch, "E1.6.1.8", {"start": v(-2, 38) * mm, "end": v(2, 38) * mm});
            skLineSegment(sketch, "E1.6.1.10", {"start": v(-2, 42) * mm, "end": v(2, 42) * mm});
            skLineSegment(sketch, "E1.6.2.4", {"start": v(2, 34) * mm, "end": v(2, 30) * mm});
            skLineSegment(sketch, "E1.6.2.6", {"start": v(-2, 34) * mm, "end": v(-2, 30) * mm});
            skLineSegment(sketch, "E1.6.2.8", {"start": v(-2, 30) * mm, "end": v(2, 30) * mm});
            skLineSegment(sketch, "E1.6.2.10", {"start": v(-2, 34) * mm, "end": v(2, 34) * mm});
            skLineSegment(sketch, "E1.6.3.4", {"start": v(2, 26) * mm, "end": v(2, 22) * mm});
            skLineSegment(sketch, "E1.6.3.6", {"start": v(-2, 26) * mm, "end": v(-2, 22) * mm});
            skLineSegment(sketch, "E1.6.3.8", {"start": v(-2, 22) * mm, "end": v(2, 22) * mm});
            skLineSegment(sketch, "E1.6.3.10", {"start": v(-2, 26) * mm, "end": v(2, 26) * mm});
            skLineSegment(sketch, "E1.6.4.4", {"start": v(2, 18) * mm, "end": v(2, 14) * mm});
            skLineSegment(sketch, "E1.6.4.6", {"start": v(-2, 18) * mm, "end": v(-2, 14) * mm});
            skLineSegment(sketch, "E1.6.4.8", {"start": v(-2, 14) * mm, "end": v(2, 14) * mm});
            skLineSegment(sketch, "E1.6.4.10", {"start": v(-2, 18) * mm, "end": v(2, 18) * mm});
            skLineSegment(sketch, "E1.6.5.4", {"start": v(2, 10) * mm, "end": v(2, 6) * mm});
            skLineSegment(sketch, "E1.6.5.6", {"start": v(-2, 10) * mm, "end": v(-2, 6) * mm});
            skLineSegment(sketch, "E1.6.5.8", {"start": v(-2, 6) * mm, "end": v(2, 6) * mm});
            skLineSegment(sketch, "E1.6.5.10", {"start": v(-2, 10) * mm, "end": v(2, 10) * mm});
            skLineSegment(sketch, "E1.6.6.4", {"start": v(2, 2) * mm, "end": v(2, -2) * mm});
            skLineSegment(sketch, "E1.6.6.6", {"start": v(-2, 2) * mm, "end": v(-2, -2) * mm});
            skLineSegment(sketch, "E1.6.6.8", {"start": v(-2, -2) * mm, "end": v(2, -2) * mm});
            skLineSegment(sketch, "E1.6.6.10", {"start": v(-2, 2) * mm, "end": v(2, 2) * mm});
            skLineSegment(sketch, "E1.6.7.4", {"start": v(2, -6) * mm, "end": v(2, -10) * mm});
            skLineSegment(sketch, "E1.6.7.6", {"start": v(-2, -6) * mm, "end": v(-2, -10) * mm});
            skLineSegment(sketch, "E1.6.7.8", {"start": v(-2, -10) * mm, "end": v(2, -10) * mm});
            skLineSegment(sketch, "E1.6.7.10", {"start": v(-2, -6) * mm, "end": v(2, -6) * mm});
            skLineSegment(sketch, "E1.6.8.4", {"start": v(2, -14) * mm, "end": v(2, -18) * mm});
            skLineSegment(sketch, "E1.6.8.6", {"start": v(-2, -14) * mm, "end": v(-2, -18) * mm});
            skLineSegment(sketch, "E1.6.8.8", {"start": v(-2, -18) * mm, "end": v(2, -18) * mm});
            skLineSegment(sketch, "E1.6.8.10", {"start": v(-2, -14) * mm, "end": v(2, -14) * mm});
            skLineSegment(sketch, "E1.6.9.4", {"start": v(2, -22) * mm, "end": v(2, -26) * mm});
            skLineSegment(sketch, "E1.6.9.6", {"start": v(-2, -22) * mm, "end": v(-2, -26) * mm});
            skLineSegment(sketch, "E1.6.9.8", {"start": v(-2, -26) * mm, "end": v(2, -26) * mm});
            skLineSegment(sketch, "E1.6.9.10", {"start": v(-2, -22) * mm, "end": v(2, -22) * mm});
            skLineSegment(sketch, "E1.6.10.4", {"start": v(2, -30) * mm, "end": v(2, -34) * mm});
            skLineSegment(sketch, "E1.6.10.6", {"start": v(-2, -30) * mm, "end": v(-2, -34) * mm});
            skLineSegment(sketch, "E1.6.10.8", {"start": v(-2, -34) * mm, "end": v(2, -34) * mm});
            skLineSegment(sketch, "E1.6.10.10", {"start": v(-2, -30) * mm, "end": v(2, -30) * mm});
            skLineSegment(sketch, "E1.6.11.4", {"start": v(2, -38) * mm, "end": v(2, -42) * mm});
            skLineSegment(sketch, "E1.6.11.6", {"start": v(-2, -38) * mm, "end": v(-2, -42) * mm});
            skLineSegment(sketch, "E1.6.11.8", {"start": v(-2, -42) * mm, "end": v(2, -42) * mm});
            skLineSegment(sketch, "E1.6.11.10", {"start": v(-2, -38) * mm, "end": v(2, -38) * mm});
            skLineSegment(sketch, "E1.6.12.4", {"start": v(2, -46) * mm, "end": v(2, -50) * mm});
            skLineSegment(sketch, "E1.6.12.6", {"start": v(-2, -46) * mm, "end": v(-2, -50) * mm});
            skLineSegment(sketch, "E1.6.12.8", {"start": v(-2, -50) * mm, "end": v(2, -50) * mm});
            skLineSegment(sketch, "E1.6.12.10", {"start": v(-2, -46) * mm, "end": v(2, -46) * mm});
            skLineSegment(sketch, "E1.7.0.4", {"start": v(10, 50) * mm, "end": v(10, 46) * mm});
            skLineSegment(sketch, "E1.7.0.6", {"start": v(6, 50) * mm, "end": v(6, 46) * mm});
            skLineSegment(sketch, "E1.7.0.8", {"start": v(6, 46) * mm, "end": v(10, 46) * mm});
            skLineSegment(sketch, "E1.7.0.10", {"start": v(6, 50) * mm, "end": v(10, 50) * mm});
            skLineSegment(sketch, "E1.7.1.4", {"start": v(10, 42) * mm, "end": v(10, 38) * mm});
            skLineSegment(sketch, "E1.7.1.6", {"start": v(6, 42) * mm, "end": v(6, 38) * mm});
            skLineSegment(sketch, "E1.7.1.8", {"start": v(6, 38) * mm, "end": v(10, 38) * mm});
            skLineSegment(sketch, "E1.7.1.10", {"start": v(6, 42) * mm, "end": v(10, 42) * mm});
            skLineSegment(sketch, "E1.7.2.4", {"start": v(10, 34) * mm, "end": v(10, 30) * mm});
            skLineSegment(sketch, "E1.7.2.6", {"start": v(6, 34) * mm, "end": v(6, 30) * mm});
            skLineSegment(sketch, "E1.7.2.8", {"start": v(6, 30) * mm, "end": v(10, 30) * mm});
            skLineSegment(sketch, "E1.7.2.10", {"start": v(6, 34) * mm, "end": v(10, 34) * mm});
            skLineSegment(sketch, "E1.7.3.4", {"start": v(10, 26) * mm, "end": v(10, 22) * mm});
            skLineSegment(sketch, "E1.7.3.6", {"start": v(6, 26) * mm, "end": v(6, 22) * mm});
            skLineSegment(sketch, "E1.7.3.8", {"start": v(6, 22) * mm, "end": v(10, 22) * mm});
            skLineSegment(sketch, "E1.7.3.10", {"start": v(6, 26) * mm, "end": v(10, 26) * mm});
            skLineSegment(sketch, "E1.7.4.4", {"start": v(10, 18) * mm, "end": v(10, 14) * mm});
            skLineSegment(sketch, "E1.7.4.6", {"start": v(6, 18) * mm, "end": v(6, 14) * mm});
            skLineSegment(sketch, "E1.7.4.8", {"start": v(6, 14) * mm, "end": v(10, 14) * mm});
            skLineSegment(sketch, "E1.7.4.10", {"start": v(6, 18) * mm, "end": v(10, 18) * mm});
            skLineSegment(sketch, "E1.7.5.4", {"start": v(10, 10) * mm, "end": v(10, 6) * mm});
            skLineSegment(sketch, "E1.7.5.6", {"start": v(6, 10) * mm, "end": v(6, 6) * mm});
            skLineSegment(sketch, "E1.7.5.8", {"start": v(6, 6) * mm, "end": v(10, 6) * mm});
            skLineSegment(sketch, "E1.7.5.10", {"start": v(6, 10) * mm, "end": v(10, 10) * mm});
            skLineSegment(sketch, "E1.7.6.4", {"start": v(10, 2) * mm, "end": v(10, -2) * mm});
            skLineSegment(sketch, "E1.7.6.6", {"start": v(6, 2) * mm, "end": v(6, -2) * mm});
            skLineSegment(sketch, "E1.7.6.8", {"start": v(6, -2) * mm, "end": v(10, -2) * mm});
            skLineSegment(sketch, "E1.7.6.10", {"start": v(6, 2) * mm, "end": v(10, 2) * mm});
            skLineSegment(sketch, "E1.7.7.4", {"start": v(10, -6) * mm, "end": v(10, -10) * mm});
            skLineSegment(sketch, "E1.7.7.6", {"start": v(6, -6) * mm, "end": v(6, -10) * mm});
            skLineSegment(sketch, "E1.7.7.8", {"start": v(6, -10) * mm, "end": v(10, -10) * mm});
            skLineSegment(sketch, "E1.7.7.10", {"start": v(6, -6) * mm, "end": v(10, -6) * mm});
            skLineSegment(sketch, "E1.7.8.4", {"start": v(10, -14) * mm, "end": v(10, -18) * mm});
            skLineSegment(sketch, "E1.7.8.6", {"start": v(6, -14) * mm, "end": v(6, -18) * mm});
            skLineSegment(sketch, "E1.7.8.8", {"start": v(6, -18) * mm, "end": v(10, -18) * mm});
            skLineSegment(sketch, "E1.7.8.10", {"start": v(6, -14) * mm, "end": v(10, -14) * mm});
            skLineSegment(sketch, "E1.7.9.4", {"start": v(10, -22) * mm, "end": v(10, -26) * mm});
            skLineSegment(sketch, "E1.7.9.6", {"start": v(6, -22) * mm, "end": v(6, -26) * mm});
            skLineSegment(sketch, "E1.7.9.8", {"start": v(6, -26) * mm, "end": v(10, -26) * mm});
            skLineSegment(sketch, "E1.7.9.10", {"start": v(6, -22) * mm, "end": v(10, -22) * mm});
            skLineSegment(sketch, "E1.7.10.4", {"start": v(10, -30) * mm, "end": v(10, -34) * mm});
            skLineSegment(sketch, "E1.7.10.6", {"start": v(6, -30) * mm, "end": v(6, -34) * mm});
            skLineSegment(sketch, "E1.7.10.8", {"start": v(6, -34) * mm, "end": v(10, -34) * mm});
            skLineSegment(sketch, "E1.7.10.10", {"start": v(6, -30) * mm, "end": v(10, -30) * mm});
            skLineSegment(sketch, "E1.7.11.4", {"start": v(10, -38) * mm, "end": v(10, -42) * mm});
            skLineSegment(sketch, "E1.7.11.6", {"start": v(6, -38) * mm, "end": v(6, -42) * mm});
            skLineSegment(sketch, "E1.7.11.8", {"start": v(6, -42) * mm, "end": v(10, -42) * mm});
            skLineSegment(sketch, "E1.7.11.10", {"start": v(6, -38) * mm, "end": v(10, -38) * mm});
            skLineSegment(sketch, "E1.7.12.4", {"start": v(10, -46) * mm, "end": v(10, -50) * mm});
            skLineSegment(sketch, "E1.7.12.6", {"start": v(6, -46) * mm, "end": v(6, -50) * mm});
            skLineSegment(sketch, "E1.7.12.8", {"start": v(6, -50) * mm, "end": v(10, -50) * mm});
            skLineSegment(sketch, "E1.7.12.10", {"start": v(6, -46) * mm, "end": v(10, -46) * mm});
            skLineSegment(sketch, "E1.8.0.4", {"start": v(18, 50) * mm, "end": v(18, 46) * mm});
            skLineSegment(sketch, "E1.8.0.6", {"start": v(14, 50) * mm, "end": v(14, 46) * mm});
            skLineSegment(sketch, "E1.8.0.8", {"start": v(14, 46) * mm, "end": v(18, 46) * mm});
            skLineSegment(sketch, "E1.8.0.10", {"start": v(14, 50) * mm, "end": v(18, 50) * mm});
            skLineSegment(sketch, "E1.8.1.4", {"start": v(18, 42) * mm, "end": v(18, 38) * mm});
            skLineSegment(sketch, "E1.8.1.6", {"start": v(14, 42) * mm, "end": v(14, 38) * mm});
            skLineSegment(sketch, "E1.8.1.8", {"start": v(14, 38) * mm, "end": v(18, 38) * mm});
            skLineSegment(sketch, "E1.8.1.10", {"start": v(14, 42) * mm, "end": v(18, 42) * mm});
            skLineSegment(sketch, "E1.8.2.4", {"start": v(18, 34) * mm, "end": v(18, 30) * mm});
            skLineSegment(sketch, "E1.8.2.6", {"start": v(14, 34) * mm, "end": v(14, 30) * mm});
            skLineSegment(sketch, "E1.8.2.8", {"start": v(14, 30) * mm, "end": v(18, 30) * mm});
            skLineSegment(sketch, "E1.8.2.10", {"start": v(14, 34) * mm, "end": v(18, 34) * mm});
            skLineSegment(sketch, "E1.8.3.4", {"start": v(18, 26) * mm, "end": v(18, 22) * mm});
            skLineSegment(sketch, "E1.8.3.6", {"start": v(14, 26) * mm, "end": v(14, 22) * mm});
            skLineSegment(sketch, "E1.8.3.8", {"start": v(14, 22) * mm, "end": v(18, 22) * mm});
            skLineSegment(sketch, "E1.8.3.10", {"start": v(14, 26) * mm, "end": v(18, 26) * mm});
            skLineSegment(sketch, "E1.8.4.4", {"start": v(18, 18) * mm, "end": v(18, 14) * mm});
            skLineSegment(sketch, "E1.8.4.6", {"start": v(14, 18) * mm, "end": v(14, 14) * mm});
            skLineSegment(sketch, "E1.8.4.8", {"start": v(14, 14) * mm, "end": v(18, 14) * mm});
            skLineSegment(sketch, "E1.8.4.10", {"start": v(14, 18) * mm, "end": v(18, 18) * mm});
            skLineSegment(sketch, "E1.8.5.4", {"start": v(18, 10) * mm, "end": v(18, 6) * mm});
            skLineSegment(sketch, "E1.8.5.6", {"start": v(14, 10) * mm, "end": v(14, 6) * mm});
            skLineSegment(sketch, "E1.8.5.8", {"start": v(14, 6) * mm, "end": v(18, 6) * mm});
            skLineSegment(sketch, "E1.8.5.10", {"start": v(14, 10) * mm, "end": v(18, 10) * mm});
            skLineSegment(sketch, "E1.8.6.4", {"start": v(18, 2) * mm, "end": v(18, -2) * mm});
            skLineSegment(sketch, "E1.8.6.6", {"start": v(14, 2) * mm, "end": v(14, -2) * mm});
            skLineSegment(sketch, "E1.8.6.8", {"start": v(14, -2) * mm, "end": v(18, -2) * mm});
            skLineSegment(sketch, "E1.8.6.10", {"start": v(14, 2) * mm, "end": v(18, 2) * mm});
            skLineSegment(sketch, "E1.8.7.4", {"start": v(18, -6) * mm, "end": v(18, -10) * mm});
            skLineSegment(sketch, "E1.8.7.6", {"start": v(14, -6) * mm, "end": v(14, -10) * mm});
            skLineSegment(sketch, "E1.8.7.8", {"start": v(14, -10) * mm, "end": v(18, -10) * mm});
            skLineSegment(sketch, "E1.8.7.10", {"start": v(14, -6) * mm, "end": v(18, -6) * mm});
            skLineSegment(sketch, "E1.8.8.4", {"start": v(18, -14) * mm, "end": v(18, -18) * mm});
            skLineSegment(sketch, "E1.8.8.6", {"start": v(14, -14) * mm, "end": v(14, -18) * mm});
            skLineSegment(sketch, "E1.8.8.8", {"start": v(14, -18) * mm, "end": v(18, -18) * mm});
            skLineSegment(sketch, "E1.8.8.10", {"start": v(14, -14) * mm, "end": v(18, -14) * mm});
            skLineSegment(sketch, "E1.8.9.4", {"start": v(18, -22) * mm, "end": v(18, -26) * mm});
            skLineSegment(sketch, "E1.8.9.6", {"start": v(14, -22) * mm, "end": v(14, -26) * mm});
            skLineSegment(sketch, "E1.8.9.8", {"start": v(14, -26) * mm, "end": v(18, -26) * mm});
            skLineSegment(sketch, "E1.8.9.10", {"start": v(14, -22) * mm, "end": v(18, -22) * mm});
            skLineSegment(sketch, "E1.8.10.4", {"start": v(18, -30) * mm, "end": v(18, -34) * mm});
            skLineSegment(sketch, "E1.8.10.6", {"start": v(14, -30) * mm, "end": v(14, -34) * mm});
            skLineSegment(sketch, "E1.8.10.8", {"start": v(14, -34) * mm, "end": v(18, -34) * mm});
            skLineSegment(sketch, "E1.8.10.10", {"start": v(14, -30) * mm, "end": v(18, -30) * mm});
            skLineSegment(sketch, "E1.8.11.4", {"start": v(18, -38) * mm, "end": v(18, -42) * mm});
            skLineSegment(sketch, "E1.8.11.6", {"start": v(14, -38) * mm, "end": v(14, -42) * mm});
            skLineSegment(sketch, "E1.8.11.8", {"start": v(14, -42) * mm, "end": v(18, -42) * mm});
            skLineSegment(sketch, "E1.8.11.10", {"start": v(14, -38) * mm, "end": v(18, -38) * mm});
            skLineSegment(sketch, "E1.8.12.4", {"start": v(18, -46) * mm, "end": v(18, -50) * mm});
            skLineSegment(sketch, "E1.8.12.6", {"start": v(14, -46) * mm, "end": v(14, -50) * mm});
            skLineSegment(sketch, "E1.8.12.8", {"start": v(14, -50) * mm, "end": v(18, -50) * mm});
            skLineSegment(sketch, "E1.8.12.10", {"start": v(14, -46) * mm, "end": v(18, -46) * mm});
            skLineSegment(sketch, "E1.9.0.4", {"start": v(26, 50) * mm, "end": v(26, 46) * mm});
            skLineSegment(sketch, "E1.9.0.6", {"start": v(22, 50) * mm, "end": v(22, 46) * mm});
            skLineSegment(sketch, "E1.9.0.8", {"start": v(22, 46) * mm, "end": v(26, 46) * mm});
            skLineSegment(sketch, "E1.9.0.10", {"start": v(22, 50) * mm, "end": v(26, 50) * mm});
            skLineSegment(sketch, "E1.9.1.4", {"start": v(26, 42) * mm, "end": v(26, 38) * mm});
            skLineSegment(sketch, "E1.9.1.6", {"start": v(22, 42) * mm, "end": v(22, 38) * mm});
            skLineSegment(sketch, "E1.9.1.8", {"start": v(22, 38) * mm, "end": v(26, 38) * mm});
            skLineSegment(sketch, "E1.9.1.10", {"start": v(22, 42) * mm, "end": v(26, 42) * mm});
            skLineSegment(sketch, "E1.9.2.4", {"start": v(26, 34) * mm, "end": v(26, 30) * mm});
            skLineSegment(sketch, "E1.9.2.6", {"start": v(22, 34) * mm, "end": v(22, 30) * mm});
            skLineSegment(sketch, "E1.9.2.8", {"start": v(22, 30) * mm, "end": v(26, 30) * mm});
            skLineSegment(sketch, "E1.9.2.10", {"start": v(22, 34) * mm, "end": v(26, 34) * mm});
            skLineSegment(sketch, "E1.9.3.4", {"start": v(26, 26) * mm, "end": v(26, 22) * mm});
            skLineSegment(sketch, "E1.9.3.6", {"start": v(22, 26) * mm, "end": v(22, 22) * mm});
            skLineSegment(sketch, "E1.9.3.8", {"start": v(22, 22) * mm, "end": v(26, 22) * mm});
            skLineSegment(sketch, "E1.9.3.10", {"start": v(22, 26) * mm, "end": v(26, 26) * mm});
            skLineSegment(sketch, "E1.9.4.4", {"start": v(26, 18) * mm, "end": v(26, 14) * mm});
            skLineSegment(sketch, "E1.9.4.6", {"start": v(22, 18) * mm, "end": v(22, 14) * mm});
            skLineSegment(sketch, "E1.9.4.8", {"start": v(22, 14) * mm, "end": v(26, 14) * mm});
            skLineSegment(sketch, "E1.9.4.10", {"start": v(22, 18) * mm, "end": v(26, 18) * mm});
            skLineSegment(sketch, "E1.9.5.4", {"start": v(26, 10) * mm, "end": v(26, 6) * mm});
            skLineSegment(sketch, "E1.9.5.6", {"start": v(22, 10) * mm, "end": v(22, 6) * mm});
            skLineSegment(sketch, "E1.9.5.8", {"start": v(22, 6) * mm, "end": v(26, 6) * mm});
            skLineSegment(sketch, "E1.9.5.10", {"start": v(22, 10) * mm, "end": v(26, 10) * mm});
            skLineSegment(sketch, "E1.9.6.4", {"start": v(26, 2) * mm, "end": v(26, -2) * mm});
            skLineSegment(sketch, "E1.9.6.6", {"start": v(22, 2) * mm, "end": v(22, -2) * mm});
            skLineSegment(sketch, "E1.9.6.8", {"start": v(22, -2) * mm, "end": v(26, -2) * mm});
            skLineSegment(sketch, "E1.9.6.10", {"start": v(22, 2) * mm, "end": v(26, 2) * mm});
            skLineSegment(sketch, "E1.9.7.4", {"start": v(26, -6) * mm, "end": v(26, -10) * mm});
            skLineSegment(sketch, "E1.9.7.6", {"start": v(22, -6) * mm, "end": v(22, -10) * mm});
            skLineSegment(sketch, "E1.9.7.8", {"start": v(22, -10) * mm, "end": v(26, -10) * mm});
            skLineSegment(sketch, "E1.9.7.10", {"start": v(22, -6) * mm, "end": v(26, -6) * mm});
            skLineSegment(sketch, "E1.9.8.4", {"start": v(26, -14) * mm, "end": v(26, -18) * mm});
            skLineSegment(sketch, "E1.9.8.6", {"start": v(22, -14) * mm, "end": v(22, -18) * mm});
            skLineSegment(sketch, "E1.9.8.8", {"start": v(22, -18) * mm, "end": v(26, -18) * mm});
            skLineSegment(sketch, "E1.9.8.10", {"start": v(22, -14) * mm, "end": v(26, -14) * mm});
            skLineSegment(sketch, "E1.9.9.4", {"start": v(26, -22) * mm, "end": v(26, -26) * mm});
            skLineSegment(sketch, "E1.9.9.6", {"start": v(22, -22) * mm, "end": v(22, -26) * mm});
            skLineSegment(sketch, "E1.9.9.8", {"start": v(22, -26) * mm, "end": v(26, -26) * mm});
            skLineSegment(sketch, "E1.9.9.10", {"start": v(22, -22) * mm, "end": v(26, -22) * mm});
            skLineSegment(sketch, "E1.9.10.4", {"start": v(26, -30) * mm, "end": v(26, -34) * mm});
            skLineSegment(sketch, "E1.9.10.6", {"start": v(22, -30) * mm, "end": v(22, -34) * mm});
            skLineSegment(sketch, "E1.9.10.8", {"start": v(22, -34) * mm, "end": v(26, -34) * mm});
            skLineSegment(sketch, "E1.9.10.10", {"start": v(22, -30) * mm, "end": v(26, -30) * mm});
            skLineSegment(sketch, "E1.9.11.4", {"start": v(26, -38) * mm, "end": v(26, -42) * mm});
            skLineSegment(sketch, "E1.9.11.6", {"start": v(22, -38) * mm, "end": v(22, -42) * mm});
            skLineSegment(sketch, "E1.9.11.8", {"start": v(22, -42) * mm, "end": v(26, -42) * mm});
            skLineSegment(sketch, "E1.9.11.10", {"start": v(22, -38) * mm, "end": v(26, -38) * mm});
            skLineSegment(sketch, "E1.9.12.4", {"start": v(26, -46) * mm, "end": v(26, -50) * mm});
            skLineSegment(sketch, "E1.9.12.6", {"start": v(22, -46) * mm, "end": v(22, -50) * mm});
            skLineSegment(sketch, "E1.9.12.8", {"start": v(22, -50) * mm, "end": v(26, -50) * mm});
            skLineSegment(sketch, "E1.9.12.10", {"start": v(22, -46) * mm, "end": v(26, -46) * mm});
            skLineSegment(sketch, "E1.10.0.4", {"start": v(34, 50) * mm, "end": v(34, 46) * mm});
            skLineSegment(sketch, "E1.10.0.6", {"start": v(30, 50) * mm, "end": v(30, 46) * mm});
            skLineSegment(sketch, "E1.10.0.8", {"start": v(30, 46) * mm, "end": v(34, 46) * mm});
            skLineSegment(sketch, "E1.10.0.10", {"start": v(30, 50) * mm, "end": v(34, 50) * mm});
            skLineSegment(sketch, "E1.10.1.4", {"start": v(34, 42) * mm, "end": v(34, 38) * mm});
            skLineSegment(sketch, "E1.10.1.6", {"start": v(30, 42) * mm, "end": v(30, 38) * mm});
            skLineSegment(sketch, "E1.10.1.8", {"start": v(30, 38) * mm, "end": v(34, 38) * mm});
            skLineSegment(sketch, "E1.10.1.10", {"start": v(30, 42) * mm, "end": v(34, 42) * mm});
            skLineSegment(sketch, "E1.10.2.4", {"start": v(34, 34) * mm, "end": v(34, 30) * mm});
            skLineSegment(sketch, "E1.10.2.6", {"start": v(30, 34) * mm, "end": v(30, 30) * mm});
            skLineSegment(sketch, "E1.10.2.8", {"start": v(30, 30) * mm, "end": v(34, 30) * mm});
            skLineSegment(sketch, "E1.10.2.10", {"start": v(30, 34) * mm, "end": v(34, 34) * mm});
            skLineSegment(sketch, "E1.10.3.4", {"start": v(34, 26) * mm, "end": v(34, 22) * mm});
            skLineSegment(sketch, "E1.10.3.6", {"start": v(30, 26) * mm, "end": v(30, 22) * mm});
            skLineSegment(sketch, "E1.10.3.8", {"start": v(30, 22) * mm, "end": v(34, 22) * mm});
            skLineSegment(sketch, "E1.10.3.10", {"start": v(30, 26) * mm, "end": v(34, 26) * mm});
            skLineSegment(sketch, "E1.10.4.4", {"start": v(34, 18) * mm, "end": v(34, 14) * mm});
            skLineSegment(sketch, "E1.10.4.6", {"start": v(30, 18) * mm, "end": v(30, 14) * mm});
            skLineSegment(sketch, "E1.10.4.8", {"start": v(30, 14) * mm, "end": v(34, 14) * mm});
            skLineSegment(sketch, "E1.10.4.10", {"start": v(30, 18) * mm, "end": v(34, 18) * mm});
            skLineSegment(sketch, "E1.10.5.4", {"start": v(34, 10) * mm, "end": v(34, 6) * mm});
            skLineSegment(sketch, "E1.10.5.6", {"start": v(30, 10) * mm, "end": v(30, 6) * mm});
            skLineSegment(sketch, "E1.10.5.8", {"start": v(30, 6) * mm, "end": v(34, 6) * mm});
            skLineSegment(sketch, "E1.10.5.10", {"start": v(30, 10) * mm, "end": v(34, 10) * mm});
            skLineSegment(sketch, "E1.10.6.4", {"start": v(34, 2) * mm, "end": v(34, -2) * mm});
            skLineSegment(sketch, "E1.10.6.6", {"start": v(30, 2) * mm, "end": v(30, -2) * mm});
            skLineSegment(sketch, "E1.10.6.8", {"start": v(30, -2) * mm, "end": v(34, -2) * mm});
            skLineSegment(sketch, "E1.10.6.10", {"start": v(30, 2) * mm, "end": v(34, 2) * mm});
            skLineSegment(sketch, "E1.10.7.4", {"start": v(34, -6) * mm, "end": v(34, -10) * mm});
            skLineSegment(sketch, "E1.10.7.6", {"start": v(30, -6) * mm, "end": v(30, -10) * mm});
            skLineSegment(sketch, "E1.10.7.8", {"start": v(30, -10) * mm, "end": v(34, -10) * mm});
            skLineSegment(sketch, "E1.10.7.10", {"start": v(30, -6) * mm, "end": v(34, -6) * mm});
            skLineSegment(sketch, "E1.10.8.4", {"start": v(34, -14) * mm, "end": v(34, -18) * mm});
            skLineSegment(sketch, "E1.10.8.6", {"start": v(30, -14) * mm, "end": v(30, -18) * mm});
            skLineSegment(sketch, "E1.10.8.8", {"start": v(30, -18) * mm, "end": v(34, -18) * mm});
            skLineSegment(sketch, "E1.10.8.10", {"start": v(30, -14) * mm, "end": v(34, -14) * mm});
            skLineSegment(sketch, "E1.10.9.4", {"start": v(34, -22) * mm, "end": v(34, -26) * mm});
            skLineSegment(sketch, "E1.10.9.6", {"start": v(30, -22) * mm, "end": v(30, -26) * mm});
            skLineSegment(sketch, "E1.10.9.8", {"start": v(30, -26) * mm, "end": v(34, -26) * mm});
            skLineSegment(sketch, "E1.10.9.10", {"start": v(30, -22) * mm, "end": v(34, -22) * mm});
            skLineSegment(sketch, "E1.10.10.4", {"start": v(34, -30) * mm, "end": v(34, -34) * mm});
            skLineSegment(sketch, "E1.10.10.6", {"start": v(30, -30) * mm, "end": v(30, -34) * mm});
            skLineSegment(sketch, "E1.10.10.8", {"start": v(30, -34) * mm, "end": v(34, -34) * mm});
            skLineSegment(sketch, "E1.10.10.10", {"start": v(30, -30) * mm, "end": v(34, -30) * mm});
            skLineSegment(sketch, "E1.10.11.4", {"start": v(34, -38) * mm, "end": v(34, -42) * mm});
            skLineSegment(sketch, "E1.10.11.6", {"start": v(30, -38) * mm, "end": v(30, -42) * mm});
            skLineSegment(sketch, "E1.10.11.8", {"start": v(30, -42) * mm, "end": v(34, -42) * mm});
            skLineSegment(sketch, "E1.10.11.10", {"start": v(30, -38) * mm, "end": v(34, -38) * mm});
            skLineSegment(sketch, "E1.10.12.4", {"start": v(34, -46) * mm, "end": v(34, -50) * mm});
            skLineSegment(sketch, "E1.10.12.6", {"start": v(30, -46) * mm, "end": v(30, -50) * mm});
            skLineSegment(sketch, "E1.10.12.8", {"start": v(30, -50) * mm, "end": v(34, -50) * mm});
            skLineSegment(sketch, "E1.10.12.10", {"start": v(30, -46) * mm, "end": v(34, -46) * mm});
            skLineSegment(sketch, "E1.11.0.4", {"start": v(42, 50) * mm, "end": v(42, 46) * mm});
            skLineSegment(sketch, "E1.11.0.6", {"start": v(38, 50) * mm, "end": v(38, 46) * mm});
            skLineSegment(sketch, "E1.11.0.8", {"start": v(38, 46) * mm, "end": v(42, 46) * mm});
            skLineSegment(sketch, "E1.11.0.10", {"start": v(38, 50) * mm, "end": v(42, 50) * mm});
            skLineSegment(sketch, "E1.11.1.4", {"start": v(42, 42) * mm, "end": v(42, 38) * mm});
            skLineSegment(sketch, "E1.11.1.6", {"start": v(38, 42) * mm, "end": v(38, 38) * mm});
            skLineSegment(sketch, "E1.11.1.8", {"start": v(38, 38) * mm, "end": v(42, 38) * mm});
            skLineSegment(sketch, "E1.11.1.10", {"start": v(38, 42) * mm, "end": v(42, 42) * mm});
            skLineSegment(sketch, "E1.11.2.4", {"start": v(42, 34) * mm, "end": v(42, 30) * mm});
            skLineSegment(sketch, "E1.11.2.6", {"start": v(38, 34) * mm, "end": v(38, 30) * mm});
            skLineSegment(sketch, "E1.11.2.8", {"start": v(38, 30) * mm, "end": v(42, 30) * mm});
            skLineSegment(sketch, "E1.11.2.10", {"start": v(38, 34) * mm, "end": v(42, 34) * mm});
            skLineSegment(sketch, "E1.11.3.4", {"start": v(42, 26) * mm, "end": v(42, 22) * mm});
            skLineSegment(sketch, "E1.11.3.6", {"start": v(38, 26) * mm, "end": v(38, 22) * mm});
            skLineSegment(sketch, "E1.11.3.8", {"start": v(38, 22) * mm, "end": v(42, 22) * mm});
            skLineSegment(sketch, "E1.11.3.10", {"start": v(38, 26) * mm, "end": v(42, 26) * mm});
            skLineSegment(sketch, "E1.11.4.4", {"start": v(42, 18) * mm, "end": v(42, 14) * mm});
            skLineSegment(sketch, "E1.11.4.6", {"start": v(38, 18) * mm, "end": v(38, 14) * mm});
            skLineSegment(sketch, "E1.11.4.8", {"start": v(38, 14) * mm, "end": v(42, 14) * mm});
            skLineSegment(sketch, "E1.11.4.10", {"start": v(38, 18) * mm, "end": v(42, 18) * mm});
            skLineSegment(sketch, "E1.11.5.4", {"start": v(42, 10) * mm, "end": v(42, 6) * mm});
            skLineSegment(sketch, "E1.11.5.6", {"start": v(38, 10) * mm, "end": v(38, 6) * mm});
            skLineSegment(sketch, "E1.11.5.8", {"start": v(38, 6) * mm, "end": v(42, 6) * mm});
            skLineSegment(sketch, "E1.11.5.10", {"start": v(38, 10) * mm, "end": v(42, 10) * mm});
            skLineSegment(sketch, "E1.11.6.4", {"start": v(42, 2) * mm, "end": v(42, -2) * mm});
            skLineSegment(sketch, "E1.11.6.6", {"start": v(38, 2) * mm, "end": v(38, -2) * mm});
            skLineSegment(sketch, "E1.11.6.8", {"start": v(38, -2) * mm, "end": v(42, -2) * mm});
            skLineSegment(sketch, "E1.11.6.10", {"start": v(38, 2) * mm, "end": v(42, 2) * mm});
            skLineSegment(sketch, "E1.11.7.4", {"start": v(42, -6) * mm, "end": v(42, -10) * mm});
            skLineSegment(sketch, "E1.11.7.6", {"start": v(38, -6) * mm, "end": v(38, -10) * mm});
            skLineSegment(sketch, "E1.11.7.8", {"start": v(38, -10) * mm, "end": v(42, -10) * mm});
            skLineSegment(sketch, "E1.11.7.10", {"start": v(38, -6) * mm, "end": v(42, -6) * mm});
            skLineSegment(sketch, "E1.11.8.4", {"start": v(42, -14) * mm, "end": v(42, -18) * mm});
            skLineSegment(sketch, "E1.11.8.6", {"start": v(38, -14) * mm, "end": v(38, -18) * mm});
            skLineSegment(sketch, "E1.11.8.8", {"start": v(38, -18) * mm, "end": v(42, -18) * mm});
            skLineSegment(sketch, "E1.11.8.10", {"start": v(38, -14) * mm, "end": v(42, -14) * mm});
            skLineSegment(sketch, "E1.11.9.4", {"start": v(42, -22) * mm, "end": v(42, -26) * mm});
            skLineSegment(sketch, "E1.11.9.6", {"start": v(38, -22) * mm, "end": v(38, -26) * mm});
            skLineSegment(sketch, "E1.11.9.8", {"start": v(38, -26) * mm, "end": v(42, -26) * mm});
            skLineSegment(sketch, "E1.11.9.10", {"start": v(38, -22) * mm, "end": v(42, -22) * mm});
            skLineSegment(sketch, "E1.11.10.4", {"start": v(42, -30) * mm, "end": v(42, -34) * mm});
            skLineSegment(sketch, "E1.11.10.6", {"start": v(38, -30) * mm, "end": v(38, -34) * mm});
            skLineSegment(sketch, "E1.11.10.8", {"start": v(38, -34) * mm, "end": v(42, -34) * mm});
            skLineSegment(sketch, "E1.11.10.10", {"start": v(38, -30) * mm, "end": v(42, -30) * mm});
            skLineSegment(sketch, "E1.11.11.4", {"start": v(42, -38) * mm, "end": v(42, -42) * mm});
            skLineSegment(sketch, "E1.11.11.6", {"start": v(38, -38) * mm, "end": v(38, -42) * mm});
            skLineSegment(sketch, "E1.11.11.8", {"start": v(38, -42) * mm, "end": v(42, -42) * mm});
            skLineSegment(sketch, "E1.11.11.10", {"start": v(38, -38) * mm, "end": v(42, -38) * mm});
            skLineSegment(sketch, "E1.11.12.4", {"start": v(42, -46) * mm, "end": v(42, -50) * mm});
            skLineSegment(sketch, "E1.11.12.6", {"start": v(38, -46) * mm, "end": v(38, -50) * mm});
            skLineSegment(sketch, "E1.11.12.8", {"start": v(38, -50) * mm, "end": v(42, -50) * mm});
            skLineSegment(sketch, "E1.11.12.10", {"start": v(38, -46) * mm, "end": v(42, -46) * mm});
            skLineSegment(sketch, "E1.12.0.4", {"start": v(50, 50) * mm, "end": v(50, 46) * mm});
            skLineSegment(sketch, "E1.12.0.6", {"start": v(46, 50) * mm, "end": v(46, 46) * mm});
            skLineSegment(sketch, "E1.12.0.8", {"start": v(46, 46) * mm, "end": v(50, 46) * mm});
            skLineSegment(sketch, "E1.12.0.10", {"start": v(46, 50) * mm, "end": v(50, 50) * mm});
            skLineSegment(sketch, "E1.12.1.4", {"start": v(50, 42) * mm, "end": v(50, 38) * mm});
            skLineSegment(sketch, "E1.12.1.6", {"start": v(46, 42) * mm, "end": v(46, 38) * mm});
            skLineSegment(sketch, "E1.12.1.8", {"start": v(46, 38) * mm, "end": v(50, 38) * mm});
            skLineSegment(sketch, "E1.12.1.10", {"start": v(46, 42) * mm, "end": v(50, 42) * mm});
            skLineSegment(sketch, "E1.12.2.4", {"start": v(50, 34) * mm, "end": v(50, 30) * mm});
            skLineSegment(sketch, "E1.12.2.6", {"start": v(46, 34) * mm, "end": v(46, 30) * mm});
            skLineSegment(sketch, "E1.12.2.8", {"start": v(46, 30) * mm, "end": v(50, 30) * mm});
            skLineSegment(sketch, "E1.12.2.10", {"start": v(46, 34) * mm, "end": v(50, 34) * mm});
            skLineSegment(sketch, "E1.12.3.4", {"start": v(50, 26) * mm, "end": v(50, 22) * mm});
            skLineSegment(sketch, "E1.12.3.6", {"start": v(46, 26) * mm, "end": v(46, 22) * mm});
            skLineSegment(sketch, "E1.12.3.8", {"start": v(46, 22) * mm, "end": v(50, 22) * mm});
            skLineSegment(sketch, "E1.12.3.10", {"start": v(46, 26) * mm, "end": v(50, 26) * mm});
            skLineSegment(sketch, "E1.12.4.4", {"start": v(50, 18) * mm, "end": v(50, 14) * mm});
            skLineSegment(sketch, "E1.12.4.6", {"start": v(46, 18) * mm, "end": v(46, 14) * mm});
            skLineSegment(sketch, "E1.12.4.8", {"start": v(46, 14) * mm, "end": v(50, 14) * mm});
            skLineSegment(sketch, "E1.12.4.10", {"start": v(46, 18) * mm, "end": v(50, 18) * mm});
            skLineSegment(sketch, "E1.12.5.4", {"start": v(50, 10) * mm, "end": v(50, 6) * mm});
            skLineSegment(sketch, "E1.12.5.6", {"start": v(46, 10) * mm, "end": v(46, 6) * mm});
            skLineSegment(sketch, "E1.12.5.8", {"start": v(46, 6) * mm, "end": v(50, 6) * mm});
            skLineSegment(sketch, "E1.12.5.10", {"start": v(46, 10) * mm, "end": v(50, 10) * mm});
            skLineSegment(sketch, "E1.12.6.4", {"start": v(50, 2) * mm, "end": v(50, -2) * mm});
            skLineSegment(sketch, "E1.12.6.6", {"start": v(46, 2) * mm, "end": v(46, -2) * mm});
            skLineSegment(sketch, "E1.12.6.8", {"start": v(46, -2) * mm, "end": v(50, -2) * mm});
            skLineSegment(sketch, "E1.12.6.10", {"start": v(46, 2) * mm, "end": v(50, 2) * mm});
            skLineSegment(sketch, "E1.12.7.4", {"start": v(50, -6) * mm, "end": v(50, -10) * mm});
            skLineSegment(sketch, "E1.12.7.6", {"start": v(46, -6) * mm, "end": v(46, -10) * mm});
            skLineSegment(sketch, "E1.12.7.8", {"start": v(46, -10) * mm, "end": v(50, -10) * mm});
            skLineSegment(sketch, "E1.12.7.10", {"start": v(46, -6) * mm, "end": v(50, -6) * mm});
            skLineSegment(sketch, "E1.12.8.4", {"start": v(50, -14) * mm, "end": v(50, -18) * mm});
            skLineSegment(sketch, "E1.12.8.6", {"start": v(46, -14) * mm, "end": v(46, -18) * mm});
            skLineSegment(sketch, "E1.12.8.8", {"start": v(46, -18) * mm, "end": v(50, -18) * mm});
            skLineSegment(sketch, "E1.12.8.10", {"start": v(46, -14) * mm, "end": v(50, -14) * mm});
            skLineSegment(sketch, "E1.12.9.4", {"start": v(50, -22) * mm, "end": v(50, -26) * mm});
            skLineSegment(sketch, "E1.12.9.6", {"start": v(46, -22) * mm, "end": v(46, -26) * mm});
            skLineSegment(sketch, "E1.12.9.8", {"start": v(46, -26) * mm, "end": v(50, -26) * mm});
            skLineSegment(sketch, "E1.12.9.10", {"start": v(46, -22) * mm, "end": v(50, -22) * mm});
            skLineSegment(sketch, "E1.12.10.4", {"start": v(50, -30) * mm, "end": v(50, -34) * mm});
            skLineSegment(sketch, "E1.12.10.6", {"start": v(46, -30) * mm, "end": v(46, -34) * mm});
            skLineSegment(sketch, "E1.12.10.8", {"start": v(46, -34) * mm, "end": v(50, -34) * mm});
            skLineSegment(sketch, "E1.12.10.10", {"start": v(46, -30) * mm, "end": v(50, -30) * mm});
            skLineSegment(sketch, "E1.12.11.4", {"start": v(50, -38) * mm, "end": v(50, -42) * mm});
            skLineSegment(sketch, "E1.12.11.6", {"start": v(46, -38) * mm, "end": v(46, -42) * mm});
            skLineSegment(sketch, "E1.12.11.8", {"start": v(46, -42) * mm, "end": v(50, -42) * mm});
            skLineSegment(sketch, "E1.12.11.10", {"start": v(46, -38) * mm, "end": v(50, -38) * mm});
            skLineSegment(sketch, "E1.12.12.4", {"start": v(50, -46) * mm, "end": v(50, -50) * mm});
            skLineSegment(sketch, "E1.12.12.6", {"start": v(46, -46) * mm, "end": v(46, -50) * mm});
            skLineSegment(sketch, "E1.12.12.8", {"start": v(46, -50) * mm, "end": v(50, -50) * mm});
            skLineSegment(sketch, "E1.12.12.10", {"start": v(46, -46) * mm, "end": v(50, -46) * mm});
            skLineSegment(sketch, "E1.direction1", {"start": v(-46, 46) * mm, "end": v(-38, 46) * mm, "construction": true});
            skLineSegment(sketch, "E1.direction2", {"start": v(-46, 46) * mm, "end": v(-46, 38) * mm, "construction": true});
            skLineSegment(sketch, "E2.bottom", {"start": v(50, -50) * mm, "end": v(-50, -50) * mm});
            skLineSegment(sketch, "E2.top", {"start": v(50, 50) * mm, "end": v(-50, 50) * mm});
            skLineSegment(sketch, "E2.left", {"start": v(50, -50) * mm, "end": v(50, 50) * mm});
            skLineSegment(sketch, "E2.right", {"start": v(-50, -50) * mm, "end": v(-50, 50) * mm});
            skSolve(sketch);
        }
        {
            var Q0;
            {var subQ2=sQuery(id+"F0.wireOp",EDGE,"E0.top");Q0=makeQuery(id+"F0.imprint","IMPRINT",FACE,{"disambiguationData":[TD([[makeQuery(id+"F0.imprint","IMPRINT",EDGE,{"derivedFrom":subQ2}),-1.0]])]});}
            var Q1;
            {var subQ3=sQuery(id+"F0.wireOp",EDGE,"E0.top");Q1=makeQuery(id+"F0.imprint","IMPRINT",FACE,{"disambiguationData":[TD([[makeQuery(id+"F0.imprint","IMPRINT",EDGE,{"derivedFrom":subQ3}),1.0]])]});}
            var Q2;
            {var subQ4=sQuery(id+"F0.wireOp",EDGE,"E1.12.0.6");Q2=makeQuery(id+"F0.imprint","IMPRINT",FACE,{"disambiguationData":[TD([[makeQuery(id+"F0.imprint","IMPRINT",EDGE,{"derivedFrom":subQ4}),1.0]])]});}
            var Q3;
            {var subQ4=sQuery(id+"F0.wireOp",EDGE,"E1.12.12.6");Q3=makeQuery(id+"F0.imprint","IMPRINT",FACE,{"disambiguationData":[TD([[makeQuery(id+"F0.imprint","IMPRINT",EDGE,{"derivedFrom":subQ4}),1.0]])]});}
            var Q4;
            {var subQ4=sQuery(id+"F0.wireOp",EDGE,"E1.0.12.4");Q4=makeQuery(id+"F0.imprint","IMPRINT",FACE,{"disambiguationData":[TD([[makeQuery(id+"F0.imprint","IMPRINT",EDGE,{"derivedFrom":subQ4}),-1.0]])]});}
            extrude(context, id + "F1", {"entities" : qUnion([Q0, Q1, Q2, Q3, Q4]), "depth" : 4 * mm});
        }
        {
            var Q0;
            Q0=qCreatedBy(makeId("Front.planeOp"),FACE);
            var sketch = newSketch(context, id + "F2", { "sketchPlane" : qUnion([Q0])});
            skLineSegment(sketch, "E3.bottom", {"start": v(50, 100) * mm, "end": v(46, 100) * mm});
            skLineSegment(sketch, "E3.top", {"start": v(50, 96) * mm, "end": v(46, 96) * mm});
            skLineSegment(sketch, "E3.left", {"start": v(50, 100) * mm, "end": v(50, 96) * mm});
            skLineSegment(sketch, "E3.right", {"start": v(46, 100) * mm, "end": v(46, 96) * mm});
            skLineSegment(sketch, "E4.0.1.0", {"start": v(50, 92) * mm, "end": v(46, 92) * mm});
            skLineSegment(sketch, "E4.0.1.1", {"start": v(50, 88) * mm, "end": v(46, 88) * mm});
            skLineSegment(sketch, "E4.0.1.2", {"start": v(50, 92) * mm, "end": v(50, 88) * mm});
            skLineSegment(sketch, "E4.0.1.3", {"start": v(46, 92) * mm, "end": v(46, 88) * mm});
            skLineSegment(sketch, "E4.0.2.0", {"start": v(50, 84) * mm, "end": v(46, 84) * mm});
            skLineSegment(sketch, "E4.0.2.1", {"start": v(50, 80) * mm, "end": v(46, 80) * mm});
            skLineSegment(sketch, "E4.0.2.2", {"start": v(50, 84) * mm, "end": v(50, 80) * mm});
            skLineSegment(sketch, "E4.0.2.3", {"start": v(46, 84) * mm, "end": v(46, 80) * mm});
            skLineSegment(sketch, "E4.0.3.0", {"start": v(50, 76) * mm, "end": v(46, 76) * mm});
            skLineSegment(sketch, "E4.0.3.1", {"start": v(50, 72) * mm, "end": v(46, 72) * mm});
            skLineSegment(sketch, "E4.0.3.2", {"start": v(50, 76) * mm, "end": v(50, 72) * mm});
            skLineSegment(sketch, "E4.0.3.3", {"start": v(46, 76) * mm, "end": v(46, 72) * mm});
            skLineSegment(sketch, "E4.0.4.0", {"start": v(50, 68) * mm, "end": v(46, 68) * mm});
            skLineSegment(sketch, "E4.0.4.1", {"start": v(50, 64) * mm, "end": v(46, 64) * mm});
            skLineSegment(sketch, "E4.0.4.2", {"start": v(50, 68) * mm, "end": v(50, 64) * mm});
            skLineSegment(sketch, "E4.0.4.3", {"start": v(46, 68) * mm, "end": v(46, 64) * mm});
            skLineSegment(sketch, "E4.0.5.0", {"start": v(50, 60) * mm, "end": v(46, 60) * mm});
            skLineSegment(sketch, "E4.0.5.1", {"start": v(50, 56) * mm, "end": v(46, 56) * mm});
            skLineSegment(sketch, "E4.0.5.2", {"start": v(50, 60) * mm, "end": v(50, 56) * mm});
            skLineSegment(sketch, "E4.0.5.3", {"start": v(46, 60) * mm, "end": v(46, 56) * mm});
            skLineSegment(sketch, "E4.0.6.0", {"start": v(50, 52) * mm, "end": v(46, 52) * mm});
            skLineSegment(sketch, "E4.0.6.1", {"start": v(50, 48) * mm, "end": v(46, 48) * mm});
            skLineSegment(sketch, "E4.0.6.2", {"start": v(50, 52) * mm, "end": v(50, 48) * mm});
            skLineSegment(sketch, "E4.0.6.3", {"start": v(46, 52) * mm, "end": v(46, 48) * mm});
            skLineSegment(sketch, "E4.0.7.0", {"start": v(50, 44) * mm, "end": v(46, 44) * mm});
            skLineSegment(sketch, "E4.0.7.1", {"start": v(50, 40) * mm, "end": v(46, 40) * mm});
            skLineSegment(sketch, "E4.0.7.2", {"start": v(50, 44) * mm, "end": v(50, 40) * mm});
            skLineSegment(sketch, "E4.0.7.3", {"start": v(46, 44) * mm, "end": v(46, 40) * mm});
            skLineSegment(sketch, "E4.0.8.0", {"start": v(50, 36) * mm, "end": v(46, 36) * mm});
            skLineSegment(sketch, "E4.0.8.1", {"start": v(50, 32) * mm, "end": v(46, 32) * mm});
            skLineSegment(sketch, "E4.0.8.2", {"start": v(50, 36) * mm, "end": v(50, 32) * mm});
            skLineSegment(sketch, "E4.0.8.3", {"start": v(46, 36) * mm, "end": v(46, 32) * mm});
            skLineSegment(sketch, "E4.0.9.0", {"start": v(50, 28) * mm, "end": v(46, 28) * mm});
            skLineSegment(sketch, "E4.0.9.1", {"start": v(50, 24) * mm, "end": v(46, 24) * mm});
            skLineSegment(sketch, "E4.0.9.2", {"start": v(50, 28) * mm, "end": v(50, 24) * mm});
            skLineSegment(sketch, "E4.0.9.3", {"start": v(46, 28) * mm, "end": v(46, 24) * mm});
            skLineSegment(sketch, "E4.0.10.0", {"start": v(50, 20) * mm, "end": v(46, 20) * mm});
            skLineSegment(sketch, "E4.0.10.1", {"start": v(50, 16) * mm, "end": v(46, 16) * mm});
            skLineSegment(sketch, "E4.0.10.2", {"start": v(50, 20) * mm, "end": v(50, 16) * mm});
            skLineSegment(sketch, "E4.0.10.3", {"start": v(46, 20) * mm, "end": v(46, 16) * mm});
            skLineSegment(sketch, "E4.0.11.0", {"start": v(50, 12) * mm, "end": v(46, 12) * mm});
            skLineSegment(sketch, "E4.0.11.1", {"start": v(50, 8) * mm, "end": v(46, 8) * mm});
            skLineSegment(sketch, "E4.0.11.2", {"start": v(50, 12) * mm, "end": v(50, 8) * mm});
            skLineSegment(sketch, "E4.0.11.3", {"start": v(46, 12) * mm, "end": v(46, 8) * mm});
            skLineSegment(sketch, "E4.0.12.0", {"start": v(50, 4) * mm, "end": v(46, 4) * mm});
            skLineSegment(sketch, "E4.0.12.1", {"start": v(50, 0) * mm, "end": v(46, 0) * mm});
            skLineSegment(sketch, "E4.0.12.2", {"start": v(50, 4) * mm, "end": v(50, 0) * mm});
            skLineSegment(sketch, "E4.0.12.3", {"start": v(46, 4) * mm, "end": v(46, 0) * mm});
            skLineSegment(sketch, "E4.1.0.0", {"start": v(42, 100) * mm, "end": v(38, 100) * mm});
            skLineSegment(sketch, "E4.1.0.1", {"start": v(42, 96) * mm, "end": v(38, 96) * mm});
            skLineSegment(sketch, "E4.1.0.2", {"start": v(42, 100) * mm, "end": v(42, 96) * mm});
            skLineSegment(sketch, "E4.1.0.3", {"start": v(38, 100) * mm, "end": v(38, 96) * mm});
            skLineSegment(sketch, "E4.1.1.0", {"start": v(42, 92) * mm, "end": v(38, 92) * mm});
            skLineSegment(sketch, "E4.1.1.1", {"start": v(42, 88) * mm, "end": v(38, 88) * mm});
            skLineSegment(sketch, "E4.1.1.2", {"start": v(42, 92) * mm, "end": v(42, 88) * mm});
            skLineSegment(sketch, "E4.1.1.3", {"start": v(38, 92) * mm, "end": v(38, 88) * mm});
            skLineSegment(sketch, "E4.1.2.0", {"start": v(42, 84) * mm, "end": v(38, 84) * mm});
            skLineSegment(sketch, "E4.1.2.1", {"start": v(42, 80) * mm, "end": v(38, 80) * mm});
            skLineSegment(sketch, "E4.1.2.2", {"start": v(42, 84) * mm, "end": v(42, 80) * mm});
            skLineSegment(sketch, "E4.1.2.3", {"start": v(38, 84) * mm, "end": v(38, 80) * mm});
            skLineSegment(sketch, "E4.1.3.0", {"start": v(42, 76) * mm, "end": v(38, 76) * mm});
            skLineSegment(sketch, "E4.1.3.1", {"start": v(42, 72) * mm, "end": v(38, 72) * mm});
            skLineSegment(sketch, "E4.1.3.2", {"start": v(42, 76) * mm, "end": v(42, 72) * mm});
            skLineSegment(sketch, "E4.1.3.3", {"start": v(38, 76) * mm, "end": v(38, 72) * mm});
            skLineSegment(sketch, "E4.1.4.0", {"start": v(42, 68) * mm, "end": v(38, 68) * mm});
            skLineSegment(sketch, "E4.1.4.1", {"start": v(42, 64) * mm, "end": v(38, 64) * mm});
            skLineSegment(sketch, "E4.1.4.2", {"start": v(42, 68) * mm, "end": v(42, 64) * mm});
            skLineSegment(sketch, "E4.1.4.3", {"start": v(38, 68) * mm, "end": v(38, 64) * mm});
            skLineSegment(sketch, "E4.1.5.0", {"start": v(42, 60) * mm, "end": v(38, 60) * mm});
            skLineSegment(sketch, "E4.1.5.1", {"start": v(42, 56) * mm, "end": v(38, 56) * mm});
            skLineSegment(sketch, "E4.1.5.2", {"start": v(42, 60) * mm, "end": v(42, 56) * mm});
            skLineSegment(sketch, "E4.1.5.3", {"start": v(38, 60) * mm, "end": v(38, 56) * mm});
            skLineSegment(sketch, "E4.1.6.0", {"start": v(42, 52) * mm, "end": v(38, 52) * mm});
            skLineSegment(sketch, "E4.1.6.1", {"start": v(42, 48) * mm, "end": v(38, 48) * mm});
            skLineSegment(sketch, "E4.1.6.2", {"start": v(42, 52) * mm, "end": v(42, 48) * mm});
            skLineSegment(sketch, "E4.1.6.3", {"start": v(38, 52) * mm, "end": v(38, 48) * mm});
            skLineSegment(sketch, "E4.1.7.0", {"start": v(42, 44) * mm, "end": v(38, 44) * mm});
            skLineSegment(sketch, "E4.1.7.1", {"start": v(42, 40) * mm, "end": v(38, 40) * mm});
            skLineSegment(sketch, "E4.1.7.2", {"start": v(42, 44) * mm, "end": v(42, 40) * mm});
            skLineSegment(sketch, "E4.1.7.3", {"start": v(38, 44) * mm, "end": v(38, 40) * mm});
            skLineSegment(sketch, "E4.1.8.0", {"start": v(42, 36) * mm, "end": v(38, 36) * mm});
            skLineSegment(sketch, "E4.1.8.1", {"start": v(42, 32) * mm, "end": v(38, 32) * mm});
            skLineSegment(sketch, "E4.1.8.2", {"start": v(42, 36) * mm, "end": v(42, 32) * mm});
            skLineSegment(sketch, "E4.1.8.3", {"start": v(38, 36) * mm, "end": v(38, 32) * mm});
            skLineSegment(sketch, "E4.1.9.0", {"start": v(42, 28) * mm, "end": v(38, 28) * mm});
            skLineSegment(sketch, "E4.1.9.1", {"start": v(42, 24) * mm, "end": v(38, 24) * mm});
            skLineSegment(sketch, "E4.1.9.2", {"start": v(42, 28) * mm, "end": v(42, 24) * mm});
            skLineSegment(sketch, "E4.1.9.3", {"start": v(38, 28) * mm, "end": v(38, 24) * mm});
            skLineSegment(sketch, "E4.1.10.0", {"start": v(42, 20) * mm, "end": v(38, 20) * mm});
            skLineSegment(sketch, "E4.1.10.1", {"start": v(42, 16) * mm, "end": v(38, 16) * mm});
            skLineSegment(sketch, "E4.1.10.2", {"start": v(42, 20) * mm, "end": v(42, 16) * mm});
            skLineSegment(sketch, "E4.1.10.3", {"start": v(38, 20) * mm, "end": v(38, 16) * mm});
            skLineSegment(sketch, "E4.1.11.0", {"start": v(42, 12) * mm, "end": v(38, 12) * mm});
            skLineSegment(sketch, "E4.1.11.1", {"start": v(42, 8) * mm, "end": v(38, 8) * mm});
            skLineSegment(sketch, "E4.1.11.2", {"start": v(42, 12) * mm, "end": v(42, 8) * mm});
            skLineSegment(sketch, "E4.1.11.3", {"start": v(38, 12) * mm, "end": v(38, 8) * mm});
            skLineSegment(sketch, "E4.1.12.0", {"start": v(42, 4) * mm, "end": v(38, 4) * mm});
            skLineSegment(sketch, "E4.1.12.1", {"start": v(42, 0) * mm, "end": v(38, 0) * mm});
            skLineSegment(sketch, "E4.1.12.2", {"start": v(42, 4) * mm, "end": v(42, 0) * mm});
            skLineSegment(sketch, "E4.1.12.3", {"start": v(38, 4) * mm, "end": v(38, 0) * mm});
            skLineSegment(sketch, "E4.2.0.0", {"start": v(34, 100) * mm, "end": v(30, 100) * mm});
            skLineSegment(sketch, "E4.2.0.1", {"start": v(34, 96) * mm, "end": v(30, 96) * mm});
            skLineSegment(sketch, "E4.2.0.2", {"start": v(34, 100) * mm, "end": v(34, 96) * mm});
            skLineSegment(sketch, "E4.2.0.3", {"start": v(30, 100) * mm, "end": v(30, 96) * mm});
            skLineSegment(sketch, "E4.2.1.0", {"start": v(34, 92) * mm, "end": v(30, 92) * mm});
            skLineSegment(sketch, "E4.2.1.1", {"start": v(34, 88) * mm, "end": v(30, 88) * mm});
            skLineSegment(sketch, "E4.2.1.2", {"start": v(34, 92) * mm, "end": v(34, 88) * mm});
            skLineSegment(sketch, "E4.2.1.3", {"start": v(30, 92) * mm, "end": v(30, 88) * mm});
            skLineSegment(sketch, "E4.2.2.0", {"start": v(34, 84) * mm, "end": v(30, 84) * mm});
            skLineSegment(sketch, "E4.2.2.1", {"start": v(34, 80) * mm, "end": v(30, 80) * mm});
            skLineSegment(sketch, "E4.2.2.2", {"start": v(34, 84) * mm, "end": v(34, 80) * mm});
            skLineSegment(sketch, "E4.2.2.3", {"start": v(30, 84) * mm, "end": v(30, 80) * mm});
            skLineSegment(sketch, "E4.2.3.0", {"start": v(34, 76) * mm, "end": v(30, 76) * mm});
            skLineSegment(sketch, "E4.2.3.1", {"start": v(34, 72) * mm, "end": v(30, 72) * mm});
            skLineSegment(sketch, "E4.2.3.2", {"start": v(34, 76) * mm, "end": v(34, 72) * mm});
            skLineSegment(sketch, "E4.2.3.3", {"start": v(30, 76) * mm, "end": v(30, 72) * mm});
            skLineSegment(sketch, "E4.2.4.0", {"start": v(34, 68) * mm, "end": v(30, 68) * mm});
            skLineSegment(sketch, "E4.2.4.1", {"start": v(34, 64) * mm, "end": v(30, 64) * mm});
            skLineSegment(sketch, "E4.2.4.2", {"start": v(34, 68) * mm, "end": v(34, 64) * mm});
            skLineSegment(sketch, "E4.2.4.3", {"start": v(30, 68) * mm, "end": v(30, 64) * mm});
            skLineSegment(sketch, "E4.2.5.0", {"start": v(34, 60) * mm, "end": v(30, 60) * mm});
            skLineSegment(sketch, "E4.2.5.1", {"start": v(34, 56) * mm, "end": v(30, 56) * mm});
            skLineSegment(sketch, "E4.2.5.2", {"start": v(34, 60) * mm, "end": v(34, 56) * mm});
            skLineSegment(sketch, "E4.2.5.3", {"start": v(30, 60) * mm, "end": v(30, 56) * mm});
            skLineSegment(sketch, "E4.2.6.0", {"start": v(34, 52) * mm, "end": v(30, 52) * mm});
            skLineSegment(sketch, "E4.2.6.1", {"start": v(34, 48) * mm, "end": v(30, 48) * mm});
            skLineSegment(sketch, "E4.2.6.2", {"start": v(34, 52) * mm, "end": v(34, 48) * mm});
            skLineSegment(sketch, "E4.2.6.3", {"start": v(30, 52) * mm, "end": v(30, 48) * mm});
            skLineSegment(sketch, "E4.2.7.0", {"start": v(34, 44) * mm, "end": v(30, 44) * mm});
            skLineSegment(sketch, "E4.2.7.1", {"start": v(34, 40) * mm, "end": v(30, 40) * mm});
            skLineSegment(sketch, "E4.2.7.2", {"start": v(34, 44) * mm, "end": v(34, 40) * mm});
            skLineSegment(sketch, "E4.2.7.3", {"start": v(30, 44) * mm, "end": v(30, 40) * mm});
            skLineSegment(sketch, "E4.2.8.0", {"start": v(34, 36) * mm, "end": v(30, 36) * mm});
            skLineSegment(sketch, "E4.2.8.1", {"start": v(34, 32) * mm, "end": v(30, 32) * mm});
            skLineSegment(sketch, "E4.2.8.2", {"start": v(34, 36) * mm, "end": v(34, 32) * mm});
            skLineSegment(sketch, "E4.2.8.3", {"start": v(30, 36) * mm, "end": v(30, 32) * mm});
            skLineSegment(sketch, "E4.2.9.0", {"start": v(34, 28) * mm, "end": v(30, 28) * mm});
            skLineSegment(sketch, "E4.2.9.1", {"start": v(34, 24) * mm, "end": v(30, 24) * mm});
            skLineSegment(sketch, "E4.2.9.2", {"start": v(34, 28) * mm, "end": v(34, 24) * mm});
            skLineSegment(sketch, "E4.2.9.3", {"start": v(30, 28) * mm, "end": v(30, 24) * mm});
            skLineSegment(sketch, "E4.2.10.0", {"start": v(34, 20) * mm, "end": v(30, 20) * mm});
            skLineSegment(sketch, "E4.2.10.1", {"start": v(34, 16) * mm, "end": v(30, 16) * mm});
            skLineSegment(sketch, "E4.2.10.2", {"start": v(34, 20) * mm, "end": v(34, 16) * mm});
            skLineSegment(sketch, "E4.2.10.3", {"start": v(30, 20) * mm, "end": v(30, 16) * mm});
            skLineSegment(sketch, "E4.2.11.0", {"start": v(34, 12) * mm, "end": v(30, 12) * mm});
            skLineSegment(sketch, "E4.2.11.1", {"start": v(34, 8) * mm, "end": v(30, 8) * mm});
            skLineSegment(sketch, "E4.2.11.2", {"start": v(34, 12) * mm, "end": v(34, 8) * mm});
            skLineSegment(sketch, "E4.2.11.3", {"start": v(30, 12) * mm, "end": v(30, 8) * mm});
            skLineSegment(sketch, "E4.2.12.0", {"start": v(34, 4) * mm, "end": v(30, 4) * mm});
            skLineSegment(sketch, "E4.2.12.1", {"start": v(34, 0) * mm, "end": v(30, 0) * mm});
            skLineSegment(sketch, "E4.2.12.2", {"start": v(34, 4) * mm, "end": v(34, 0) * mm});
            skLineSegment(sketch, "E4.2.12.3", {"start": v(30, 4) * mm, "end": v(30, 0) * mm});
            skLineSegment(sketch, "E4.3.0.0", {"start": v(26, 100) * mm, "end": v(22, 100) * mm});
            skLineSegment(sketch, "E4.3.0.1", {"start": v(26, 96) * mm, "end": v(22, 96) * mm});
            skLineSegment(sketch, "E4.3.0.2", {"start": v(26, 100) * mm, "end": v(26, 96) * mm});
            skLineSegment(sketch, "E4.3.0.3", {"start": v(22, 100) * mm, "end": v(22, 96) * mm});
            skLineSegment(sketch, "E4.3.1.0", {"start": v(26, 92) * mm, "end": v(22, 92) * mm});
            skLineSegment(sketch, "E4.3.1.1", {"start": v(26, 88) * mm, "end": v(22, 88) * mm});
            skLineSegment(sketch, "E4.3.1.2", {"start": v(26, 92) * mm, "end": v(26, 88) * mm});
            skLineSegment(sketch, "E4.3.1.3", {"start": v(22, 92) * mm, "end": v(22, 88) * mm});
            skLineSegment(sketch, "E4.3.2.0", {"start": v(26, 84) * mm, "end": v(22, 84) * mm});
            skLineSegment(sketch, "E4.3.2.1", {"start": v(26, 80) * mm, "end": v(22, 80) * mm});
            skLineSegment(sketch, "E4.3.2.2", {"start": v(26, 84) * mm, "end": v(26, 80) * mm});
            skLineSegment(sketch, "E4.3.2.3", {"start": v(22, 84) * mm, "end": v(22, 80) * mm});
            skLineSegment(sketch, "E4.3.3.0", {"start": v(26, 76) * mm, "end": v(22, 76) * mm});
            skLineSegment(sketch, "E4.3.3.1", {"start": v(26, 72) * mm, "end": v(22, 72) * mm});
            skLineSegment(sketch, "E4.3.3.2", {"start": v(26, 76) * mm, "end": v(26, 72) * mm});
            skLineSegment(sketch, "E4.3.3.3", {"start": v(22, 76) * mm, "end": v(22, 72) * mm});
            skLineSegment(sketch, "E4.3.4.0", {"start": v(26, 68) * mm, "end": v(22, 68) * mm});
            skLineSegment(sketch, "E4.3.4.1", {"start": v(26, 64) * mm, "end": v(22, 64) * mm});
            skLineSegment(sketch, "E4.3.4.2", {"start": v(26, 68) * mm, "end": v(26, 64) * mm});
            skLineSegment(sketch, "E4.3.4.3", {"start": v(22, 68) * mm, "end": v(22, 64) * mm});
            skLineSegment(sketch, "E4.3.5.0", {"start": v(26, 60) * mm, "end": v(22, 60) * mm});
            skLineSegment(sketch, "E4.3.5.1", {"start": v(26, 56) * mm, "end": v(22, 56) * mm});
            skLineSegment(sketch, "E4.3.5.2", {"start": v(26, 60) * mm, "end": v(26, 56) * mm});
            skLineSegment(sketch, "E4.3.5.3", {"start": v(22, 60) * mm, "end": v(22, 56) * mm});
            skLineSegment(sketch, "E4.3.6.0", {"start": v(26, 52) * mm, "end": v(22, 52) * mm});
            skLineSegment(sketch, "E4.3.6.1", {"start": v(26, 48) * mm, "end": v(22, 48) * mm});
            skLineSegment(sketch, "E4.3.6.2", {"start": v(26, 52) * mm, "end": v(26, 48) * mm});
            skLineSegment(sketch, "E4.3.6.3", {"start": v(22, 52) * mm, "end": v(22, 48) * mm});
            skLineSegment(sketch, "E4.3.7.0", {"start": v(26, 44) * mm, "end": v(22, 44) * mm});
            skLineSegment(sketch, "E4.3.7.1", {"start": v(26, 40) * mm, "end": v(22, 40) * mm});
            skLineSegment(sketch, "E4.3.7.2", {"start": v(26, 44) * mm, "end": v(26, 40) * mm});
            skLineSegment(sketch, "E4.3.7.3", {"start": v(22, 44) * mm, "end": v(22, 40) * mm});
            skLineSegment(sketch, "E4.3.8.0", {"start": v(26, 36) * mm, "end": v(22, 36) * mm});
            skLineSegment(sketch, "E4.3.8.1", {"start": v(26, 32) * mm, "end": v(22, 32) * mm});
            skLineSegment(sketch, "E4.3.8.2", {"start": v(26, 36) * mm, "end": v(26, 32) * mm});
            skLineSegment(sketch, "E4.3.8.3", {"start": v(22, 36) * mm, "end": v(22, 32) * mm});
            skLineSegment(sketch, "E4.3.9.0", {"start": v(26, 28) * mm, "end": v(22, 28) * mm});
            skLineSegment(sketch, "E4.3.9.1", {"start": v(26, 24) * mm, "end": v(22, 24) * mm});
            skLineSegment(sketch, "E4.3.9.2", {"start": v(26, 28) * mm, "end": v(26, 24) * mm});
            skLineSegment(sketch, "E4.3.9.3", {"start": v(22, 28) * mm, "end": v(22, 24) * mm});
            skLineSegment(sketch, "E4.3.10.0", {"start": v(26, 20) * mm, "end": v(22, 20) * mm});
            skLineSegment(sketch, "E4.3.10.1", {"start": v(26, 16) * mm, "end": v(22, 16) * mm});
            skLineSegment(sketch, "E4.3.10.2", {"start": v(26, 20) * mm, "end": v(26, 16) * mm});
            skLineSegment(sketch, "E4.3.10.3", {"start": v(22, 20) * mm, "end": v(22, 16) * mm});
            skLineSegment(sketch, "E4.3.11.0", {"start": v(26, 12) * mm, "end": v(22, 12) * mm});
            skLineSegment(sketch, "E4.3.11.1", {"start": v(26, 8) * mm, "end": v(22, 8) * mm});
            skLineSegment(sketch, "E4.3.11.2", {"start": v(26, 12) * mm, "end": v(26, 8) * mm});
            skLineSegment(sketch, "E4.3.11.3", {"start": v(22, 12) * mm, "end": v(22, 8) * mm});
            skLineSegment(sketch, "E4.3.12.0", {"start": v(26, 4) * mm, "end": v(22, 4) * mm});
            skLineSegment(sketch, "E4.3.12.1", {"start": v(26, 0) * mm, "end": v(22, 0) * mm});
            skLineSegment(sketch, "E4.3.12.2", {"start": v(26, 4) * mm, "end": v(26, 0) * mm});
            skLineSegment(sketch, "E4.3.12.3", {"start": v(22, 4) * mm, "end": v(22, 0) * mm});
            skLineSegment(sketch, "E4.4.0.0", {"start": v(18, 100) * mm, "end": v(14, 100) * mm});
            skLineSegment(sketch, "E4.4.0.1", {"start": v(18, 96) * mm, "end": v(14, 96) * mm});
            skLineSegment(sketch, "E4.4.0.2", {"start": v(18, 100) * mm, "end": v(18, 96) * mm});
            skLineSegment(sketch, "E4.4.0.3", {"start": v(14, 100) * mm, "end": v(14, 96) * mm});
            skLineSegment(sketch, "E4.4.1.0", {"start": v(18, 92) * mm, "end": v(14, 92) * mm});
            skLineSegment(sketch, "E4.4.1.1", {"start": v(18, 88) * mm, "end": v(14, 88) * mm});
            skLineSegment(sketch, "E4.4.1.2", {"start": v(18, 92) * mm, "end": v(18, 88) * mm});
            skLineSegment(sketch, "E4.4.1.3", {"start": v(14, 92) * mm, "end": v(14, 88) * mm});
            skLineSegment(sketch, "E4.4.2.0", {"start": v(18, 84) * mm, "end": v(14, 84) * mm});
            skLineSegment(sketch, "E4.4.2.1", {"start": v(18, 80) * mm, "end": v(14, 80) * mm});
            skLineSegment(sketch, "E4.4.2.2", {"start": v(18, 84) * mm, "end": v(18, 80) * mm});
            skLineSegment(sketch, "E4.4.2.3", {"start": v(14, 84) * mm, "end": v(14, 80) * mm});
            skLineSegment(sketch, "E4.4.3.0", {"start": v(18, 76) * mm, "end": v(14, 76) * mm});
            skLineSegment(sketch, "E4.4.3.1", {"start": v(18, 72) * mm, "end": v(14, 72) * mm});
            skLineSegment(sketch, "E4.4.3.2", {"start": v(18, 76) * mm, "end": v(18, 72) * mm});
            skLineSegment(sketch, "E4.4.3.3", {"start": v(14, 76) * mm, "end": v(14, 72) * mm});
            skLineSegment(sketch, "E4.4.4.0", {"start": v(18, 68) * mm, "end": v(14, 68) * mm});
            skLineSegment(sketch, "E4.4.4.1", {"start": v(18, 64) * mm, "end": v(14, 64) * mm});
            skLineSegment(sketch, "E4.4.4.2", {"start": v(18, 68) * mm, "end": v(18, 64) * mm});
            skLineSegment(sketch, "E4.4.4.3", {"start": v(14, 68) * mm, "end": v(14, 64) * mm});
            skLineSegment(sketch, "E4.4.5.0", {"start": v(18, 60) * mm, "end": v(14, 60) * mm});
            skLineSegment(sketch, "E4.4.5.1", {"start": v(18, 56) * mm, "end": v(14, 56) * mm});
            skLineSegment(sketch, "E4.4.5.2", {"start": v(18, 60) * mm, "end": v(18, 56) * mm});
            skLineSegment(sketch, "E4.4.5.3", {"start": v(14, 60) * mm, "end": v(14, 56) * mm});
            skLineSegment(sketch, "E4.4.6.0", {"start": v(18, 52) * mm, "end": v(14, 52) * mm});
            skLineSegment(sketch, "E4.4.6.1", {"start": v(18, 48) * mm, "end": v(14, 48) * mm});
            skLineSegment(sketch, "E4.4.6.2", {"start": v(18, 52) * mm, "end": v(18, 48) * mm});
            skLineSegment(sketch, "E4.4.6.3", {"start": v(14, 52) * mm, "end": v(14, 48) * mm});
            skLineSegment(sketch, "E4.4.7.0", {"start": v(18, 44) * mm, "end": v(14, 44) * mm});
            skLineSegment(sketch, "E4.4.7.1", {"start": v(18, 40) * mm, "end": v(14, 40) * mm});
            skLineSegment(sketch, "E4.4.7.2", {"start": v(18, 44) * mm, "end": v(18, 40) * mm});
            skLineSegment(sketch, "E4.4.7.3", {"start": v(14, 44) * mm, "end": v(14, 40) * mm});
            skLineSegment(sketch, "E4.4.8.0", {"start": v(18, 36) * mm, "end": v(14, 36) * mm});
            skLineSegment(sketch, "E4.4.8.1", {"start": v(18, 32) * mm, "end": v(14, 32) * mm});
            skLineSegment(sketch, "E4.4.8.2", {"start": v(18, 36) * mm, "end": v(18, 32) * mm});
            skLineSegment(sketch, "E4.4.8.3", {"start": v(14, 36) * mm, "end": v(14, 32) * mm});
            skLineSegment(sketch, "E4.4.9.0", {"start": v(18, 28) * mm, "end": v(14, 28) * mm});
            skLineSegment(sketch, "E4.4.9.1", {"start": v(18, 24) * mm, "end": v(14, 24) * mm});
            skLineSegment(sketch, "E4.4.9.2", {"start": v(18, 28) * mm, "end": v(18, 24) * mm});
            skLineSegment(sketch, "E4.4.9.3", {"start": v(14, 28) * mm, "end": v(14, 24) * mm});
            skLineSegment(sketch, "E4.4.10.0", {"start": v(18, 20) * mm, "end": v(14, 20) * mm});
            skLineSegment(sketch, "E4.4.10.1", {"start": v(18, 16) * mm, "end": v(14, 16) * mm});
            skLineSegment(sketch, "E4.4.10.2", {"start": v(18, 20) * mm, "end": v(18, 16) * mm});
            skLineSegment(sketch, "E4.4.10.3", {"start": v(14, 20) * mm, "end": v(14, 16) * mm});
            skLineSegment(sketch, "E4.4.11.0", {"start": v(18, 12) * mm, "end": v(14, 12) * mm});
            skLineSegment(sketch, "E4.4.11.1", {"start": v(18, 8) * mm, "end": v(14, 8) * mm});
            skLineSegment(sketch, "E4.4.11.2", {"start": v(18, 12) * mm, "end": v(18, 8) * mm});
            skLineSegment(sketch, "E4.4.11.3", {"start": v(14, 12) * mm, "end": v(14, 8) * mm});
            skLineSegment(sketch, "E4.4.12.0", {"start": v(18, 4) * mm, "end": v(14, 4) * mm});
            skLineSegment(sketch, "E4.4.12.1", {"start": v(18, 0) * mm, "end": v(14, 0) * mm});
            skLineSegment(sketch, "E4.4.12.2", {"start": v(18, 4) * mm, "end": v(18, 0) * mm});
            skLineSegment(sketch, "E4.4.12.3", {"start": v(14, 4) * mm, "end": v(14, 0) * mm});
            skLineSegment(sketch, "E4.5.0.0", {"start": v(10, 100) * mm, "end": v(6, 100) * mm});
            skLineSegment(sketch, "E4.5.0.1", {"start": v(10, 96) * mm, "end": v(6, 96) * mm});
            skLineSegment(sketch, "E4.5.0.2", {"start": v(10, 100) * mm, "end": v(10, 96) * mm});
            skLineSegment(sketch, "E4.5.0.3", {"start": v(6, 100) * mm, "end": v(6, 96) * mm});
            skLineSegment(sketch, "E4.5.1.0", {"start": v(10, 92) * mm, "end": v(6, 92) * mm});
            skLineSegment(sketch, "E4.5.1.1", {"start": v(10, 88) * mm, "end": v(6, 88) * mm});
            skLineSegment(sketch, "E4.5.1.2", {"start": v(10, 92) * mm, "end": v(10, 88) * mm});
            skLineSegment(sketch, "E4.5.1.3", {"start": v(6, 92) * mm, "end": v(6, 88) * mm});
            skLineSegment(sketch, "E4.5.2.0", {"start": v(10, 84) * mm, "end": v(6, 84) * mm});
            skLineSegment(sketch, "E4.5.2.1", {"start": v(10, 80) * mm, "end": v(6, 80) * mm});
            skLineSegment(sketch, "E4.5.2.2", {"start": v(10, 84) * mm, "end": v(10, 80) * mm});
            skLineSegment(sketch, "E4.5.2.3", {"start": v(6, 84) * mm, "end": v(6, 80) * mm});
            skLineSegment(sketch, "E4.5.3.0", {"start": v(10, 76) * mm, "end": v(6, 76) * mm});
            skLineSegment(sketch, "E4.5.3.1", {"start": v(10, 72) * mm, "end": v(6, 72) * mm});
            skLineSegment(sketch, "E4.5.3.2", {"start": v(10, 76) * mm, "end": v(10, 72) * mm});
            skLineSegment(sketch, "E4.5.3.3", {"start": v(6, 76) * mm, "end": v(6, 72) * mm});
            skLineSegment(sketch, "E4.5.4.0", {"start": v(10, 68) * mm, "end": v(6, 68) * mm});
            skLineSegment(sketch, "E4.5.4.1", {"start": v(10, 64) * mm, "end": v(6, 64) * mm});
            skLineSegment(sketch, "E4.5.4.2", {"start": v(10, 68) * mm, "end": v(10, 64) * mm});
            skLineSegment(sketch, "E4.5.4.3", {"start": v(6, 68) * mm, "end": v(6, 64) * mm});
            skLineSegment(sketch, "E4.5.5.0", {"start": v(10, 60) * mm, "end": v(6, 60) * mm});
            skLineSegment(sketch, "E4.5.5.1", {"start": v(10, 56) * mm, "end": v(6, 56) * mm});
            skLineSegment(sketch, "E4.5.5.2", {"start": v(10, 60) * mm, "end": v(10, 56) * mm});
            skLineSegment(sketch, "E4.5.5.3", {"start": v(6, 60) * mm, "end": v(6, 56) * mm});
            skLineSegment(sketch, "E4.5.6.0", {"start": v(10, 52) * mm, "end": v(6, 52) * mm});
            skLineSegment(sketch, "E4.5.6.1", {"start": v(10, 48) * mm, "end": v(6, 48) * mm});
            skLineSegment(sketch, "E4.5.6.2", {"start": v(10, 52) * mm, "end": v(10, 48) * mm});
            skLineSegment(sketch, "E4.5.6.3", {"start": v(6, 52) * mm, "end": v(6, 48) * mm});
            skLineSegment(sketch, "E4.5.7.0", {"start": v(10, 44) * mm, "end": v(6, 44) * mm});
            skLineSegment(sketch, "E4.5.7.1", {"start": v(10, 40) * mm, "end": v(6, 40) * mm});
            skLineSegment(sketch, "E4.5.7.2", {"start": v(10, 44) * mm, "end": v(10, 40) * mm});
            skLineSegment(sketch, "E4.5.7.3", {"start": v(6, 44) * mm, "end": v(6, 40) * mm});
            skLineSegment(sketch, "E4.5.8.0", {"start": v(10, 36) * mm, "end": v(6, 36) * mm});
            skLineSegment(sketch, "E4.5.8.1", {"start": v(10, 32) * mm, "end": v(6, 32) * mm});
            skLineSegment(sketch, "E4.5.8.2", {"start": v(10, 36) * mm, "end": v(10, 32) * mm});
            skLineSegment(sketch, "E4.5.8.3", {"start": v(6, 36) * mm, "end": v(6, 32) * mm});
            skLineSegment(sketch, "E4.5.9.0", {"start": v(10, 28) * mm, "end": v(6, 28) * mm});
            skLineSegment(sketch, "E4.5.9.1", {"start": v(10, 24) * mm, "end": v(6, 24) * mm});
            skLineSegment(sketch, "E4.5.9.2", {"start": v(10, 28) * mm, "end": v(10, 24) * mm});
            skLineSegment(sketch, "E4.5.9.3", {"start": v(6, 28) * mm, "end": v(6, 24) * mm});
            skLineSegment(sketch, "E4.5.10.0", {"start": v(10, 20) * mm, "end": v(6, 20) * mm});
            skLineSegment(sketch, "E4.5.10.1", {"start": v(10, 16) * mm, "end": v(6, 16) * mm});
            skLineSegment(sketch, "E4.5.10.2", {"start": v(10, 20) * mm, "end": v(10, 16) * mm});
            skLineSegment(sketch, "E4.5.10.3", {"start": v(6, 20) * mm, "end": v(6, 16) * mm});
            skLineSegment(sketch, "E4.5.11.0", {"start": v(10, 12) * mm, "end": v(6, 12) * mm});
            skLineSegment(sketch, "E4.5.11.1", {"start": v(10, 8) * mm, "end": v(6, 8) * mm});
            skLineSegment(sketch, "E4.5.11.2", {"start": v(10, 12) * mm, "end": v(10, 8) * mm});
            skLineSegment(sketch, "E4.5.11.3", {"start": v(6, 12) * mm, "end": v(6, 8) * mm});
            skLineSegment(sketch, "E4.5.12.0", {"start": v(10, 4) * mm, "end": v(6, 4) * mm});
            skLineSegment(sketch, "E4.5.12.1", {"start": v(10, 0) * mm, "end": v(6, 0) * mm});
            skLineSegment(sketch, "E4.5.12.2", {"start": v(10, 4) * mm, "end": v(10, 0) * mm});
            skLineSegment(sketch, "E4.5.12.3", {"start": v(6, 4) * mm, "end": v(6, 0) * mm});
            skLineSegment(sketch, "E4.6.0.0", {"start": v(2, 100) * mm, "end": v(-2, 100) * mm});
            skLineSegment(sketch, "E4.6.0.1", {"start": v(2, 96) * mm, "end": v(-2, 96) * mm});
            skLineSegment(sketch, "E4.6.0.2", {"start": v(2, 100) * mm, "end": v(2, 96) * mm});
            skLineSegment(sketch, "E4.6.0.3", {"start": v(-2, 100) * mm, "end": v(-2, 96) * mm});
            skLineSegment(sketch, "E4.6.1.0", {"start": v(2, 92) * mm, "end": v(-2, 92) * mm});
            skLineSegment(sketch, "E4.6.1.1", {"start": v(2, 88) * mm, "end": v(-2, 88) * mm});
            skLineSegment(sketch, "E4.6.1.2", {"start": v(2, 92) * mm, "end": v(2, 88) * mm});
            skLineSegment(sketch, "E4.6.1.3", {"start": v(-2, 92) * mm, "end": v(-2, 88) * mm});
            skLineSegment(sketch, "E4.6.2.0", {"start": v(2, 84) * mm, "end": v(-2, 84) * mm});
            skLineSegment(sketch, "E4.6.2.1", {"start": v(2, 80) * mm, "end": v(-2, 80) * mm});
            skLineSegment(sketch, "E4.6.2.2", {"start": v(2, 84) * mm, "end": v(2, 80) * mm});
            skLineSegment(sketch, "E4.6.2.3", {"start": v(-2, 84) * mm, "end": v(-2, 80) * mm});
            skLineSegment(sketch, "E4.6.3.0", {"start": v(2, 76) * mm, "end": v(-2, 76) * mm});
            skLineSegment(sketch, "E4.6.3.1", {"start": v(2, 72) * mm, "end": v(-2, 72) * mm});
            skLineSegment(sketch, "E4.6.3.2", {"start": v(2, 76) * mm, "end": v(2, 72) * mm});
            skLineSegment(sketch, "E4.6.3.3", {"start": v(-2, 76) * mm, "end": v(-2, 72) * mm});
            skLineSegment(sketch, "E4.6.4.0", {"start": v(2, 68) * mm, "end": v(-2, 68) * mm});
            skLineSegment(sketch, "E4.6.4.1", {"start": v(2, 64) * mm, "end": v(-2, 64) * mm});
            skLineSegment(sketch, "E4.6.4.2", {"start": v(2, 68) * mm, "end": v(2, 64) * mm});
            skLineSegment(sketch, "E4.6.4.3", {"start": v(-2, 68) * mm, "end": v(-2, 64) * mm});
            skLineSegment(sketch, "E4.6.5.0", {"start": v(2, 60) * mm, "end": v(-2, 60) * mm});
            skLineSegment(sketch, "E4.6.5.1", {"start": v(2, 56) * mm, "end": v(-2, 56) * mm});
            skLineSegment(sketch, "E4.6.5.2", {"start": v(2, 60) * mm, "end": v(2, 56) * mm});
            skLineSegment(sketch, "E4.6.5.3", {"start": v(-2, 60) * mm, "end": v(-2, 56) * mm});
            skLineSegment(sketch, "E4.6.6.0", {"start": v(2, 52) * mm, "end": v(-2, 52) * mm});
            skLineSegment(sketch, "E4.6.6.1", {"start": v(2, 48) * mm, "end": v(-2, 48) * mm});
            skLineSegment(sketch, "E4.6.6.2", {"start": v(2, 52) * mm, "end": v(2, 48) * mm});
            skLineSegment(sketch, "E4.6.6.3", {"start": v(-2, 52) * mm, "end": v(-2, 48) * mm});
            skLineSegment(sketch, "E4.6.7.0", {"start": v(2, 44) * mm, "end": v(-2, 44) * mm});
            skLineSegment(sketch, "E4.6.7.1", {"start": v(2, 40) * mm, "end": v(-2, 40) * mm});
            skLineSegment(sketch, "E4.6.7.2", {"start": v(2, 44) * mm, "end": v(2, 40) * mm});
            skLineSegment(sketch, "E4.6.7.3", {"start": v(-2, 44) * mm, "end": v(-2, 40) * mm});
            skLineSegment(sketch, "E4.6.8.0", {"start": v(2, 36) * mm, "end": v(-2, 36) * mm});
            skLineSegment(sketch, "E4.6.8.1", {"start": v(2, 32) * mm, "end": v(-2, 32) * mm});
            skLineSegment(sketch, "E4.6.8.2", {"start": v(2, 36) * mm, "end": v(2, 32) * mm});
            skLineSegment(sketch, "E4.6.8.3", {"start": v(-2, 36) * mm, "end": v(-2, 32) * mm});
            skLineSegment(sketch, "E4.6.9.0", {"start": v(2, 28) * mm, "end": v(-2, 28) * mm});
            skLineSegment(sketch, "E4.6.9.1", {"start": v(2, 24) * mm, "end": v(-2, 24) * mm});
            skLineSegment(sketch, "E4.6.9.2", {"start": v(2, 28) * mm, "end": v(2, 24) * mm});
            skLineSegment(sketch, "E4.6.9.3", {"start": v(-2, 28) * mm, "end": v(-2, 24) * mm});
            skLineSegment(sketch, "E4.6.10.0", {"start": v(2, 20) * mm, "end": v(-2, 20) * mm});
            skLineSegment(sketch, "E4.6.10.1", {"start": v(2, 16) * mm, "end": v(-2, 16) * mm});
            skLineSegment(sketch, "E4.6.10.2", {"start": v(2, 20) * mm, "end": v(2, 16) * mm});
            skLineSegment(sketch, "E4.6.10.3", {"start": v(-2, 20) * mm, "end": v(-2, 16) * mm});
            skLineSegment(sketch, "E4.6.11.0", {"start": v(2, 12) * mm, "end": v(-2, 12) * mm});
            skLineSegment(sketch, "E4.6.11.1", {"start": v(2, 8) * mm, "end": v(-2, 8) * mm});
            skLineSegment(sketch, "E4.6.11.2", {"start": v(2, 12) * mm, "end": v(2, 8) * mm});
            skLineSegment(sketch, "E4.6.11.3", {"start": v(-2, 12) * mm, "end": v(-2, 8) * mm});
            skLineSegment(sketch, "E4.6.12.0", {"start": v(2, 4) * mm, "end": v(-2, 4) * mm});
            skLineSegment(sketch, "E4.6.12.1", {"start": v(2, 0) * mm, "end": v(-2, 0) * mm});
            skLineSegment(sketch, "E4.6.12.2", {"start": v(2, 4) * mm, "end": v(2, 0) * mm});
            skLineSegment(sketch, "E4.6.12.3", {"start": v(-2, 4) * mm, "end": v(-2, 0) * mm});
            skLineSegment(sketch, "E4.7.0.0", {"start": v(-6, 100) * mm, "end": v(-10, 100) * mm});
            skLineSegment(sketch, "E4.7.0.1", {"start": v(-6, 96) * mm, "end": v(-10, 96) * mm});
            skLineSegment(sketch, "E4.7.0.2", {"start": v(-6, 100) * mm, "end": v(-6, 96) * mm});
            skLineSegment(sketch, "E4.7.0.3", {"start": v(-10, 100) * mm, "end": v(-10, 96) * mm});
            skLineSegment(sketch, "E4.7.1.0", {"start": v(-6, 92) * mm, "end": v(-10, 92) * mm});
            skLineSegment(sketch, "E4.7.1.1", {"start": v(-6, 88) * mm, "end": v(-10, 88) * mm});
            skLineSegment(sketch, "E4.7.1.2", {"start": v(-6, 92) * mm, "end": v(-6, 88) * mm});
            skLineSegment(sketch, "E4.7.1.3", {"start": v(-10, 92) * mm, "end": v(-10, 88) * mm});
            skLineSegment(sketch, "E4.7.2.0", {"start": v(-6, 84) * mm, "end": v(-10, 84) * mm});
            skLineSegment(sketch, "E4.7.2.1", {"start": v(-6, 80) * mm, "end": v(-10, 80) * mm});
            skLineSegment(sketch, "E4.7.2.2", {"start": v(-6, 84) * mm, "end": v(-6, 80) * mm});
            skLineSegment(sketch, "E4.7.2.3", {"start": v(-10, 84) * mm, "end": v(-10, 80) * mm});
            skLineSegment(sketch, "E4.7.3.0", {"start": v(-6, 76) * mm, "end": v(-10, 76) * mm});
            skLineSegment(sketch, "E4.7.3.1", {"start": v(-6, 72) * mm, "end": v(-10, 72) * mm});
            skLineSegment(sketch, "E4.7.3.2", {"start": v(-6, 76) * mm, "end": v(-6, 72) * mm});
            skLineSegment(sketch, "E4.7.3.3", {"start": v(-10, 76) * mm, "end": v(-10, 72) * mm});
            skLineSegment(sketch, "E4.7.4.0", {"start": v(-6, 68) * mm, "end": v(-10, 68) * mm});
            skLineSegment(sketch, "E4.7.4.1", {"start": v(-6, 64) * mm, "end": v(-10, 64) * mm});
            skLineSegment(sketch, "E4.7.4.2", {"start": v(-6, 68) * mm, "end": v(-6, 64) * mm});
            skLineSegment(sketch, "E4.7.4.3", {"start": v(-10, 68) * mm, "end": v(-10, 64) * mm});
            skLineSegment(sketch, "E4.7.5.0", {"start": v(-6, 60) * mm, "end": v(-10, 60) * mm});
            skLineSegment(sketch, "E4.7.5.1", {"start": v(-6, 56) * mm, "end": v(-10, 56) * mm});
            skLineSegment(sketch, "E4.7.5.2", {"start": v(-6, 60) * mm, "end": v(-6, 56) * mm});
            skLineSegment(sketch, "E4.7.5.3", {"start": v(-10, 60) * mm, "end": v(-10, 56) * mm});
            skLineSegment(sketch, "E4.7.6.0", {"start": v(-6, 52) * mm, "end": v(-10, 52) * mm});
            skLineSegment(sketch, "E4.7.6.1", {"start": v(-6, 48) * mm, "end": v(-10, 48) * mm});
            skLineSegment(sketch, "E4.7.6.2", {"start": v(-6, 52) * mm, "end": v(-6, 48) * mm});
            skLineSegment(sketch, "E4.7.6.3", {"start": v(-10, 52) * mm, "end": v(-10, 48) * mm});
            skLineSegment(sketch, "E4.7.7.0", {"start": v(-6, 44) * mm, "end": v(-10, 44) * mm});
            skLineSegment(sketch, "E4.7.7.1", {"start": v(-6, 40) * mm, "end": v(-10, 40) * mm});
            skLineSegment(sketch, "E4.7.7.2", {"start": v(-6, 44) * mm, "end": v(-6, 40) * mm});
            skLineSegment(sketch, "E4.7.7.3", {"start": v(-10, 44) * mm, "end": v(-10, 40) * mm});
            skLineSegment(sketch, "E4.7.8.0", {"start": v(-6, 36) * mm, "end": v(-10, 36) * mm});
            skLineSegment(sketch, "E4.7.8.1", {"start": v(-6, 32) * mm, "end": v(-10, 32) * mm});
            skLineSegment(sketch, "E4.7.8.2", {"start": v(-6, 36) * mm, "end": v(-6, 32) * mm});
            skLineSegment(sketch, "E4.7.8.3", {"start": v(-10, 36) * mm, "end": v(-10, 32) * mm});
            skLineSegment(sketch, "E4.7.9.0", {"start": v(-6, 28) * mm, "end": v(-10, 28) * mm});
            skLineSegment(sketch, "E4.7.9.1", {"start": v(-6, 24) * mm, "end": v(-10, 24) * mm});
            skLineSegment(sketch, "E4.7.9.2", {"start": v(-6, 28) * mm, "end": v(-6, 24) * mm});
            skLineSegment(sketch, "E4.7.9.3", {"start": v(-10, 28) * mm, "end": v(-10, 24) * mm});
            skLineSegment(sketch, "E4.7.10.0", {"start": v(-6, 20) * mm, "end": v(-10, 20) * mm});
            skLineSegment(sketch, "E4.7.10.1", {"start": v(-6, 16) * mm, "end": v(-10, 16) * mm});
            skLineSegment(sketch, "E4.7.10.2", {"start": v(-6, 20) * mm, "end": v(-6, 16) * mm});
            skLineSegment(sketch, "E4.7.10.3", {"start": v(-10, 20) * mm, "end": v(-10, 16) * mm});
            skLineSegment(sketch, "E4.7.11.0", {"start": v(-6, 12) * mm, "end": v(-10, 12) * mm});
            skLineSegment(sketch, "E4.7.11.1", {"start": v(-6, 8) * mm, "end": v(-10, 8) * mm});
            skLineSegment(sketch, "E4.7.11.2", {"start": v(-6, 12) * mm, "end": v(-6, 8) * mm});
            skLineSegment(sketch, "E4.7.11.3", {"start": v(-10, 12) * mm, "end": v(-10, 8) * mm});
            skLineSegment(sketch, "E4.7.12.0", {"start": v(-6, 4) * mm, "end": v(-10, 4) * mm});
            skLineSegment(sketch, "E4.7.12.1", {"start": v(-6, 0) * mm, "end": v(-10, 0) * mm});
            skLineSegment(sketch, "E4.7.12.2", {"start": v(-6, 4) * mm, "end": v(-6, 0) * mm});
            skLineSegment(sketch, "E4.7.12.3", {"start": v(-10, 4) * mm, "end": v(-10, 0) * mm});
            skLineSegment(sketch, "E4.8.0.0", {"start": v(-14, 100) * mm, "end": v(-18, 100) * mm});
            skLineSegment(sketch, "E4.8.0.1", {"start": v(-14, 96) * mm, "end": v(-18, 96) * mm});
            skLineSegment(sketch, "E4.8.0.2", {"start": v(-14, 100) * mm, "end": v(-14, 96) * mm});
            skLineSegment(sketch, "E4.8.0.3", {"start": v(-18, 100) * mm, "end": v(-18, 96) * mm});
            skLineSegment(sketch, "E4.8.1.0", {"start": v(-14, 92) * mm, "end": v(-18, 92) * mm});
            skLineSegment(sketch, "E4.8.1.1", {"start": v(-14, 88) * mm, "end": v(-18, 88) * mm});
            skLineSegment(sketch, "E4.8.1.2", {"start": v(-14, 92) * mm, "end": v(-14, 88) * mm});
            skLineSegment(sketch, "E4.8.1.3", {"start": v(-18, 92) * mm, "end": v(-18, 88) * mm});
            skLineSegment(sketch, "E4.8.2.0", {"start": v(-14, 84) * mm, "end": v(-18, 84) * mm});
            skLineSegment(sketch, "E4.8.2.1", {"start": v(-14, 80) * mm, "end": v(-18, 80) * mm});
            skLineSegment(sketch, "E4.8.2.2", {"start": v(-14, 84) * mm, "end": v(-14, 80) * mm});
            skLineSegment(sketch, "E4.8.2.3", {"start": v(-18, 84) * mm, "end": v(-18, 80) * mm});
            skLineSegment(sketch, "E4.8.3.0", {"start": v(-14, 76) * mm, "end": v(-18, 76) * mm});
            skLineSegment(sketch, "E4.8.3.1", {"start": v(-14, 72) * mm, "end": v(-18, 72) * mm});
            skLineSegment(sketch, "E4.8.3.2", {"start": v(-14, 76) * mm, "end": v(-14, 72) * mm});
            skLineSegment(sketch, "E4.8.3.3", {"start": v(-18, 76) * mm, "end": v(-18, 72) * mm});
            skLineSegment(sketch, "E4.8.4.0", {"start": v(-14, 68) * mm, "end": v(-18, 68) * mm});
            skLineSegment(sketch, "E4.8.4.1", {"start": v(-14, 64) * mm, "end": v(-18, 64) * mm});
            skLineSegment(sketch, "E4.8.4.2", {"start": v(-14, 68) * mm, "end": v(-14, 64) * mm});
            skLineSegment(sketch, "E4.8.4.3", {"start": v(-18, 68) * mm, "end": v(-18, 64) * mm});
            skLineSegment(sketch, "E4.8.5.0", {"start": v(-14, 60) * mm, "end": v(-18, 60) * mm});
            skLineSegment(sketch, "E4.8.5.1", {"start": v(-14, 56) * mm, "end": v(-18, 56) * mm});
            skLineSegment(sketch, "E4.8.5.2", {"start": v(-14, 60) * mm, "end": v(-14, 56) * mm});
            skLineSegment(sketch, "E4.8.5.3", {"start": v(-18, 60) * mm, "end": v(-18, 56) * mm});
            skLineSegment(sketch, "E4.8.6.0", {"start": v(-14, 52) * mm, "end": v(-18, 52) * mm});
            skLineSegment(sketch, "E4.8.6.1", {"start": v(-14, 48) * mm, "end": v(-18, 48) * mm});
            skLineSegment(sketch, "E4.8.6.2", {"start": v(-14, 52) * mm, "end": v(-14, 48) * mm});
            skLineSegment(sketch, "E4.8.6.3", {"start": v(-18, 52) * mm, "end": v(-18, 48) * mm});
            skLineSegment(sketch, "E4.8.7.0", {"start": v(-14, 44) * mm, "end": v(-18, 44) * mm});
            skLineSegment(sketch, "E4.8.7.1", {"start": v(-14, 40) * mm, "end": v(-18, 40) * mm});
            skLineSegment(sketch, "E4.8.7.2", {"start": v(-14, 44) * mm, "end": v(-14, 40) * mm});
            skLineSegment(sketch, "E4.8.7.3", {"start": v(-18, 44) * mm, "end": v(-18, 40) * mm});
            skLineSegment(sketch, "E4.8.8.0", {"start": v(-14, 36) * mm, "end": v(-18, 36) * mm});
            skLineSegment(sketch, "E4.8.8.1", {"start": v(-14, 32) * mm, "end": v(-18, 32) * mm});
            skLineSegment(sketch, "E4.8.8.2", {"start": v(-14, 36) * mm, "end": v(-14, 32) * mm});
            skLineSegment(sketch, "E4.8.8.3", {"start": v(-18, 36) * mm, "end": v(-18, 32) * mm});
            skLineSegment(sketch, "E4.8.9.0", {"start": v(-14, 28) * mm, "end": v(-18, 28) * mm});
            skLineSegment(sketch, "E4.8.9.1", {"start": v(-14, 24) * mm, "end": v(-18, 24) * mm});
            skLineSegment(sketch, "E4.8.9.2", {"start": v(-14, 28) * mm, "end": v(-14, 24) * mm});
            skLineSegment(sketch, "E4.8.9.3", {"start": v(-18, 28) * mm, "end": v(-18, 24) * mm});
            skLineSegment(sketch, "E4.8.10.0", {"start": v(-14, 20) * mm, "end": v(-18, 20) * mm});
            skLineSegment(sketch, "E4.8.10.1", {"start": v(-14, 16) * mm, "end": v(-18, 16) * mm});
            skLineSegment(sketch, "E4.8.10.2", {"start": v(-14, 20) * mm, "end": v(-14, 16) * mm});
            skLineSegment(sketch, "E4.8.10.3", {"start": v(-18, 20) * mm, "end": v(-18, 16) * mm});
            skLineSegment(sketch, "E4.8.11.0", {"start": v(-14, 12) * mm, "end": v(-18, 12) * mm});
            skLineSegment(sketch, "E4.8.11.1", {"start": v(-14, 8) * mm, "end": v(-18, 8) * mm});
            skLineSegment(sketch, "E4.8.11.2", {"start": v(-14, 12) * mm, "end": v(-14, 8) * mm});
            skLineSegment(sketch, "E4.8.11.3", {"start": v(-18, 12) * mm, "end": v(-18, 8) * mm});
            skLineSegment(sketch, "E4.8.12.0", {"start": v(-14, 4) * mm, "end": v(-18, 4) * mm});
            skLineSegment(sketch, "E4.8.12.1", {"start": v(-14, 0) * mm, "end": v(-18, 0) * mm});
            skLineSegment(sketch, "E4.8.12.2", {"start": v(-14, 4) * mm, "end": v(-14, 0) * mm});
            skLineSegment(sketch, "E4.8.12.3", {"start": v(-18, 4) * mm, "end": v(-18, 0) * mm});
            skLineSegment(sketch, "E4.9.0.0", {"start": v(-22, 100) * mm, "end": v(-26, 100) * mm});
            skLineSegment(sketch, "E4.9.0.1", {"start": v(-22, 96) * mm, "end": v(-26, 96) * mm});
            skLineSegment(sketch, "E4.9.0.2", {"start": v(-22, 100) * mm, "end": v(-22, 96) * mm});
            skLineSegment(sketch, "E4.9.0.3", {"start": v(-26, 100) * mm, "end": v(-26, 96) * mm});
            skLineSegment(sketch, "E4.9.1.0", {"start": v(-22, 92) * mm, "end": v(-26, 92) * mm});
            skLineSegment(sketch, "E4.9.1.1", {"start": v(-22, 88) * mm, "end": v(-26, 88) * mm});
            skLineSegment(sketch, "E4.9.1.2", {"start": v(-22, 92) * mm, "end": v(-22, 88) * mm});
            skLineSegment(sketch, "E4.9.1.3", {"start": v(-26, 92) * mm, "end": v(-26, 88) * mm});
            skLineSegment(sketch, "E4.9.2.0", {"start": v(-22, 84) * mm, "end": v(-26, 84) * mm});
            skLineSegment(sketch, "E4.9.2.1", {"start": v(-22, 80) * mm, "end": v(-26, 80) * mm});
            skLineSegment(sketch, "E4.9.2.2", {"start": v(-22, 84) * mm, "end": v(-22, 80) * mm});
            skLineSegment(sketch, "E4.9.2.3", {"start": v(-26, 84) * mm, "end": v(-26, 80) * mm});
            skLineSegment(sketch, "E4.9.3.0", {"start": v(-22, 76) * mm, "end": v(-26, 76) * mm});
            skLineSegment(sketch, "E4.9.3.1", {"start": v(-22, 72) * mm, "end": v(-26, 72) * mm});
            skLineSegment(sketch, "E4.9.3.2", {"start": v(-22, 76) * mm, "end": v(-22, 72) * mm});
            skLineSegment(sketch, "E4.9.3.3", {"start": v(-26, 76) * mm, "end": v(-26, 72) * mm});
            skLineSegment(sketch, "E4.9.4.0", {"start": v(-22, 68) * mm, "end": v(-26, 68) * mm});
            skLineSegment(sketch, "E4.9.4.1", {"start": v(-22, 64) * mm, "end": v(-26, 64) * mm});
            skLineSegment(sketch, "E4.9.4.2", {"start": v(-22, 68) * mm, "end": v(-22, 64) * mm});
            skLineSegment(sketch, "E4.9.4.3", {"start": v(-26, 68) * mm, "end": v(-26, 64) * mm});
            skLineSegment(sketch, "E4.9.5.0", {"start": v(-22, 60) * mm, "end": v(-26, 60) * mm});
            skLineSegment(sketch, "E4.9.5.1", {"start": v(-22, 56) * mm, "end": v(-26, 56) * mm});
            skLineSegment(sketch, "E4.9.5.2", {"start": v(-22, 60) * mm, "end": v(-22, 56) * mm});
            skLineSegment(sketch, "E4.9.5.3", {"start": v(-26, 60) * mm, "end": v(-26, 56) * mm});
            skLineSegment(sketch, "E4.9.6.0", {"start": v(-22, 52) * mm, "end": v(-26, 52) * mm});
            skLineSegment(sketch, "E4.9.6.1", {"start": v(-22, 48) * mm, "end": v(-26, 48) * mm});
            skLineSegment(sketch, "E4.9.6.2", {"start": v(-22, 52) * mm, "end": v(-22, 48) * mm});
            skLineSegment(sketch, "E4.9.6.3", {"start": v(-26, 52) * mm, "end": v(-26, 48) * mm});
            skLineSegment(sketch, "E4.9.7.0", {"start": v(-22, 44) * mm, "end": v(-26, 44) * mm});
            skLineSegment(sketch, "E4.9.7.1", {"start": v(-22, 40) * mm, "end": v(-26, 40) * mm});
            skLineSegment(sketch, "E4.9.7.2", {"start": v(-22, 44) * mm, "end": v(-22, 40) * mm});
            skLineSegment(sketch, "E4.9.7.3", {"start": v(-26, 44) * mm, "end": v(-26, 40) * mm});
            skLineSegment(sketch, "E4.9.8.0", {"start": v(-22, 36) * mm, "end": v(-26, 36) * mm});
            skLineSegment(sketch, "E4.9.8.1", {"start": v(-22, 32) * mm, "end": v(-26, 32) * mm});
            skLineSegment(sketch, "E4.9.8.2", {"start": v(-22, 36) * mm, "end": v(-22, 32) * mm});
            skLineSegment(sketch, "E4.9.8.3", {"start": v(-26, 36) * mm, "end": v(-26, 32) * mm});
            skLineSegment(sketch, "E4.9.9.0", {"start": v(-22, 28) * mm, "end": v(-26, 28) * mm});
            skLineSegment(sketch, "E4.9.9.1", {"start": v(-22, 24) * mm, "end": v(-26, 24) * mm});
            skLineSegment(sketch, "E4.9.9.2", {"start": v(-22, 28) * mm, "end": v(-22, 24) * mm});
            skLineSegment(sketch, "E4.9.9.3", {"start": v(-26, 28) * mm, "end": v(-26, 24) * mm});
            skLineSegment(sketch, "E4.9.10.0", {"start": v(-22, 20) * mm, "end": v(-26, 20) * mm});
            skLineSegment(sketch, "E4.9.10.1", {"start": v(-22, 16) * mm, "end": v(-26, 16) * mm});
            skLineSegment(sketch, "E4.9.10.2", {"start": v(-22, 20) * mm, "end": v(-22, 16) * mm});
            skLineSegment(sketch, "E4.9.10.3", {"start": v(-26, 20) * mm, "end": v(-26, 16) * mm});
            skLineSegment(sketch, "E4.9.11.0", {"start": v(-22, 12) * mm, "end": v(-26, 12) * mm});
            skLineSegment(sketch, "E4.9.11.1", {"start": v(-22, 8) * mm, "end": v(-26, 8) * mm});
            skLineSegment(sketch, "E4.9.11.2", {"start": v(-22, 12) * mm, "end": v(-22, 8) * mm});
            skLineSegment(sketch, "E4.9.11.3", {"start": v(-26, 12) * mm, "end": v(-26, 8) * mm});
            skLineSegment(sketch, "E4.9.12.0", {"start": v(-22, 4) * mm, "end": v(-26, 4) * mm});
            skLineSegment(sketch, "E4.9.12.1", {"start": v(-22, 0) * mm, "end": v(-26, 0) * mm});
            skLineSegment(sketch, "E4.9.12.2", {"start": v(-22, 4) * mm, "end": v(-22, 0) * mm});
            skLineSegment(sketch, "E4.9.12.3", {"start": v(-26, 4) * mm, "end": v(-26, 0) * mm});
            skLineSegment(sketch, "E4.10.0.0", {"start": v(-30, 100) * mm, "end": v(-34, 100) * mm});
            skLineSegment(sketch, "E4.10.0.1", {"start": v(-30, 96) * mm, "end": v(-34, 96) * mm});
            skLineSegment(sketch, "E4.10.0.2", {"start": v(-30, 100) * mm, "end": v(-30, 96) * mm});
            skLineSegment(sketch, "E4.10.0.3", {"start": v(-34, 100) * mm, "end": v(-34, 96) * mm});
            skLineSegment(sketch, "E4.10.1.0", {"start": v(-30, 92) * mm, "end": v(-34, 92) * mm});
            skLineSegment(sketch, "E4.10.1.1", {"start": v(-30, 88) * mm, "end": v(-34, 88) * mm});
            skLineSegment(sketch, "E4.10.1.2", {"start": v(-30, 92) * mm, "end": v(-30, 88) * mm});
            skLineSegment(sketch, "E4.10.1.3", {"start": v(-34, 92) * mm, "end": v(-34, 88) * mm});
            skLineSegment(sketch, "E4.10.2.0", {"start": v(-30, 84) * mm, "end": v(-34, 84) * mm});
            skLineSegment(sketch, "E4.10.2.1", {"start": v(-30, 80) * mm, "end": v(-34, 80) * mm});
            skLineSegment(sketch, "E4.10.2.2", {"start": v(-30, 84) * mm, "end": v(-30, 80) * mm});
            skLineSegment(sketch, "E4.10.2.3", {"start": v(-34, 84) * mm, "end": v(-34, 80) * mm});
            skLineSegment(sketch, "E4.10.3.0", {"start": v(-30, 76) * mm, "end": v(-34, 76) * mm});
            skLineSegment(sketch, "E4.10.3.1", {"start": v(-30, 72) * mm, "end": v(-34, 72) * mm});
            skLineSegment(sketch, "E4.10.3.2", {"start": v(-30, 76) * mm, "end": v(-30, 72) * mm});
            skLineSegment(sketch, "E4.10.3.3", {"start": v(-34, 76) * mm, "end": v(-34, 72) * mm});
            skLineSegment(sketch, "E4.10.4.0", {"start": v(-30, 68) * mm, "end": v(-34, 68) * mm});
            skLineSegment(sketch, "E4.10.4.1", {"start": v(-30, 64) * mm, "end": v(-34, 64) * mm});
            skLineSegment(sketch, "E4.10.4.2", {"start": v(-30, 68) * mm, "end": v(-30, 64) * mm});
            skLineSegment(sketch, "E4.10.4.3", {"start": v(-34, 68) * mm, "end": v(-34, 64) * mm});
            skLineSegment(sketch, "E4.10.5.0", {"start": v(-30, 60) * mm, "end": v(-34, 60) * mm});
            skLineSegment(sketch, "E4.10.5.1", {"start": v(-30, 56) * mm, "end": v(-34, 56) * mm});
            skLineSegment(sketch, "E4.10.5.2", {"start": v(-30, 60) * mm, "end": v(-30, 56) * mm});
            skLineSegment(sketch, "E4.10.5.3", {"start": v(-34, 60) * mm, "end": v(-34, 56) * mm});
            skLineSegment(sketch, "E4.10.6.0", {"start": v(-30, 52) * mm, "end": v(-34, 52) * mm});
            skLineSegment(sketch, "E4.10.6.1", {"start": v(-30, 48) * mm, "end": v(-34, 48) * mm});
            skLineSegment(sketch, "E4.10.6.2", {"start": v(-30, 52) * mm, "end": v(-30, 48) * mm});
            skLineSegment(sketch, "E4.10.6.3", {"start": v(-34, 52) * mm, "end": v(-34, 48) * mm});
            skLineSegment(sketch, "E4.10.7.0", {"start": v(-30, 44) * mm, "end": v(-34, 44) * mm});
            skLineSegment(sketch, "E4.10.7.1", {"start": v(-30, 40) * mm, "end": v(-34, 40) * mm});
            skLineSegment(sketch, "E4.10.7.2", {"start": v(-30, 44) * mm, "end": v(-30, 40) * mm});
            skLineSegment(sketch, "E4.10.7.3", {"start": v(-34, 44) * mm, "end": v(-34, 40) * mm});
            skLineSegment(sketch, "E4.10.8.0", {"start": v(-30, 36) * mm, "end": v(-34, 36) * mm});
            skLineSegment(sketch, "E4.10.8.1", {"start": v(-30, 32) * mm, "end": v(-34, 32) * mm});
            skLineSegment(sketch, "E4.10.8.2", {"start": v(-30, 36) * mm, "end": v(-30, 32) * mm});
            skLineSegment(sketch, "E4.10.8.3", {"start": v(-34, 36) * mm, "end": v(-34, 32) * mm});
            skLineSegment(sketch, "E4.10.9.0", {"start": v(-30, 28) * mm, "end": v(-34, 28) * mm});
            skLineSegment(sketch, "E4.10.9.1", {"start": v(-30, 24) * mm, "end": v(-34, 24) * mm});
            skLineSegment(sketch, "E4.10.9.2", {"start": v(-30, 28) * mm, "end": v(-30, 24) * mm});
            skLineSegment(sketch, "E4.10.9.3", {"start": v(-34, 28) * mm, "end": v(-34, 24) * mm});
            skLineSegment(sketch, "E4.10.10.0", {"start": v(-30, 20) * mm, "end": v(-34, 20) * mm});
            skLineSegment(sketch, "E4.10.10.1", {"start": v(-30, 16) * mm, "end": v(-34, 16) * mm});
            skLineSegment(sketch, "E4.10.10.2", {"start": v(-30, 20) * mm, "end": v(-30, 16) * mm});
            skLineSegment(sketch, "E4.10.10.3", {"start": v(-34, 20) * mm, "end": v(-34, 16) * mm});
            skLineSegment(sketch, "E4.10.11.0", {"start": v(-30, 12) * mm, "end": v(-34, 12) * mm});
            skLineSegment(sketch, "E4.10.11.1", {"start": v(-30, 8) * mm, "end": v(-34, 8) * mm});
            skLineSegment(sketch, "E4.10.11.2", {"start": v(-30, 12) * mm, "end": v(-30, 8) * mm});
            skLineSegment(sketch, "E4.10.11.3", {"start": v(-34, 12) * mm, "end": v(-34, 8) * mm});
            skLineSegment(sketch, "E4.10.12.0", {"start": v(-30, 4) * mm, "end": v(-34, 4) * mm});
            skLineSegment(sketch, "E4.10.12.1", {"start": v(-30, 0) * mm, "end": v(-34, 0) * mm});
            skLineSegment(sketch, "E4.10.12.2", {"start": v(-30, 4) * mm, "end": v(-30, 0) * mm});
            skLineSegment(sketch, "E4.10.12.3", {"start": v(-34, 4) * mm, "end": v(-34, 0) * mm});
            skLineSegment(sketch, "E4.11.0.0", {"start": v(-38, 100) * mm, "end": v(-42, 100) * mm});
            skLineSegment(sketch, "E4.11.0.1", {"start": v(-38, 96) * mm, "end": v(-42, 96) * mm});
            skLineSegment(sketch, "E4.11.0.2", {"start": v(-38, 100) * mm, "end": v(-38, 96) * mm});
            skLineSegment(sketch, "E4.11.0.3", {"start": v(-42, 100) * mm, "end": v(-42, 96) * mm});
            skLineSegment(sketch, "E4.11.1.0", {"start": v(-38, 92) * mm, "end": v(-42, 92) * mm});
            skLineSegment(sketch, "E4.11.1.1", {"start": v(-38, 88) * mm, "end": v(-42, 88) * mm});
            skLineSegment(sketch, "E4.11.1.2", {"start": v(-38, 92) * mm, "end": v(-38, 88) * mm});
            skLineSegment(sketch, "E4.11.1.3", {"start": v(-42, 92) * mm, "end": v(-42, 88) * mm});
            skLineSegment(sketch, "E4.11.2.0", {"start": v(-38, 84) * mm, "end": v(-42, 84) * mm});
            skLineSegment(sketch, "E4.11.2.1", {"start": v(-38, 80) * mm, "end": v(-42, 80) * mm});
            skLineSegment(sketch, "E4.11.2.2", {"start": v(-38, 84) * mm, "end": v(-38, 80) * mm});
            skLineSegment(sketch, "E4.11.2.3", {"start": v(-42, 84) * mm, "end": v(-42, 80) * mm});
            skLineSegment(sketch, "E4.11.3.0", {"start": v(-38, 76) * mm, "end": v(-42, 76) * mm});
            skLineSegment(sketch, "E4.11.3.1", {"start": v(-38, 72) * mm, "end": v(-42, 72) * mm});
            skLineSegment(sketch, "E4.11.3.2", {"start": v(-38, 76) * mm, "end": v(-38, 72) * mm});
            skLineSegment(sketch, "E4.11.3.3", {"start": v(-42, 76) * mm, "end": v(-42, 72) * mm});
            skLineSegment(sketch, "E4.11.4.0", {"start": v(-38, 68) * mm, "end": v(-42, 68) * mm});
            skLineSegment(sketch, "E4.11.4.1", {"start": v(-38, 64) * mm, "end": v(-42, 64) * mm});
            skLineSegment(sketch, "E4.11.4.2", {"start": v(-38, 68) * mm, "end": v(-38, 64) * mm});
            skLineSegment(sketch, "E4.11.4.3", {"start": v(-42, 68) * mm, "end": v(-42, 64) * mm});
            skLineSegment(sketch, "E4.11.5.0", {"start": v(-38, 60) * mm, "end": v(-42, 60) * mm});
            skLineSegment(sketch, "E4.11.5.1", {"start": v(-38, 56) * mm, "end": v(-42, 56) * mm});
            skLineSegment(sketch, "E4.11.5.2", {"start": v(-38, 60) * mm, "end": v(-38, 56) * mm});
            skLineSegment(sketch, "E4.11.5.3", {"start": v(-42, 60) * mm, "end": v(-42, 56) * mm});
            skLineSegment(sketch, "E4.11.6.0", {"start": v(-38, 52) * mm, "end": v(-42, 52) * mm});
            skLineSegment(sketch, "E4.11.6.1", {"start": v(-38, 48) * mm, "end": v(-42, 48) * mm});
            skLineSegment(sketch, "E4.11.6.2", {"start": v(-38, 52) * mm, "end": v(-38, 48) * mm});
            skLineSegment(sketch, "E4.11.6.3", {"start": v(-42, 52) * mm, "end": v(-42, 48) * mm});
            skLineSegment(sketch, "E4.11.7.0", {"start": v(-38, 44) * mm, "end": v(-42, 44) * mm});
            skLineSegment(sketch, "E4.11.7.1", {"start": v(-38, 40) * mm, "end": v(-42, 40) * mm});
            skLineSegment(sketch, "E4.11.7.2", {"start": v(-38, 44) * mm, "end": v(-38, 40) * mm});
            skLineSegment(sketch, "E4.11.7.3", {"start": v(-42, 44) * mm, "end": v(-42, 40) * mm});
            skLineSegment(sketch, "E4.11.8.0", {"start": v(-38, 36) * mm, "end": v(-42, 36) * mm});
            skLineSegment(sketch, "E4.11.8.1", {"start": v(-38, 32) * mm, "end": v(-42, 32) * mm});
            skLineSegment(sketch, "E4.11.8.2", {"start": v(-38, 36) * mm, "end": v(-38, 32) * mm});
            skLineSegment(sketch, "E4.11.8.3", {"start": v(-42, 36) * mm, "end": v(-42, 32) * mm});
            skLineSegment(sketch, "E4.11.9.0", {"start": v(-38, 28) * mm, "end": v(-42, 28) * mm});
            skLineSegment(sketch, "E4.11.9.1", {"start": v(-38, 24) * mm, "end": v(-42, 24) * mm});
            skLineSegment(sketch, "E4.11.9.2", {"start": v(-38, 28) * mm, "end": v(-38, 24) * mm});
            skLineSegment(sketch, "E4.11.9.3", {"start": v(-42, 28) * mm, "end": v(-42, 24) * mm});
            skLineSegment(sketch, "E4.11.10.0", {"start": v(-38, 20) * mm, "end": v(-42, 20) * mm});
            skLineSegment(sketch, "E4.11.10.1", {"start": v(-38, 16) * mm, "end": v(-42, 16) * mm});
            skLineSegment(sketch, "E4.11.10.2", {"start": v(-38, 20) * mm, "end": v(-38, 16) * mm});
            skLineSegment(sketch, "E4.11.10.3", {"start": v(-42, 20) * mm, "end": v(-42, 16) * mm});
            skLineSegment(sketch, "E4.11.11.0", {"start": v(-38, 12) * mm, "end": v(-42, 12) * mm});
            skLineSegment(sketch, "E4.11.11.1", {"start": v(-38, 8) * mm, "end": v(-42, 8) * mm});
            skLineSegment(sketch, "E4.11.11.2", {"start": v(-38, 12) * mm, "end": v(-38, 8) * mm});
            skLineSegment(sketch, "E4.11.11.3", {"start": v(-42, 12) * mm, "end": v(-42, 8) * mm});
            skLineSegment(sketch, "E4.11.12.0", {"start": v(-38, 4) * mm, "end": v(-42, 4) * mm});
            skLineSegment(sketch, "E4.11.12.1", {"start": v(-38, 0) * mm, "end": v(-42, 0) * mm});
            skLineSegment(sketch, "E4.11.12.2", {"start": v(-38, 4) * mm, "end": v(-38, 0) * mm});
            skLineSegment(sketch, "E4.11.12.3", {"start": v(-42, 4) * mm, "end": v(-42, 0) * mm});
            skLineSegment(sketch, "E4.12.0.0", {"start": v(-46, 100) * mm, "end": v(-50, 100) * mm});
            skLineSegment(sketch, "E4.12.0.1", {"start": v(-46, 96) * mm, "end": v(-50, 96) * mm});
            skLineSegment(sketch, "E4.12.0.2", {"start": v(-46, 100) * mm, "end": v(-46, 96) * mm});
            skLineSegment(sketch, "E4.12.0.3", {"start": v(-50, 100) * mm, "end": v(-50, 96) * mm});
            skLineSegment(sketch, "E4.12.1.0", {"start": v(-46, 92) * mm, "end": v(-50, 92) * mm});
            skLineSegment(sketch, "E4.12.1.1", {"start": v(-46, 88) * mm, "end": v(-50, 88) * mm});
            skLineSegment(sketch, "E4.12.1.2", {"start": v(-46, 92) * mm, "end": v(-46, 88) * mm});
            skLineSegment(sketch, "E4.12.1.3", {"start": v(-50, 92) * mm, "end": v(-50, 88) * mm});
            skLineSegment(sketch, "E4.12.2.0", {"start": v(-46, 84) * mm, "end": v(-50, 84) * mm});
            skLineSegment(sketch, "E4.12.2.1", {"start": v(-46, 80) * mm, "end": v(-50, 80) * mm});
            skLineSegment(sketch, "E4.12.2.2", {"start": v(-46, 84) * mm, "end": v(-46, 80) * mm});
            skLineSegment(sketch, "E4.12.2.3", {"start": v(-50, 84) * mm, "end": v(-50, 80) * mm});
            skLineSegment(sketch, "E4.12.3.0", {"start": v(-46, 76) * mm, "end": v(-50, 76) * mm});
            skLineSegment(sketch, "E4.12.3.1", {"start": v(-46, 72) * mm, "end": v(-50, 72) * mm});
            skLineSegment(sketch, "E4.12.3.2", {"start": v(-46, 76) * mm, "end": v(-46, 72) * mm});
            skLineSegment(sketch, "E4.12.3.3", {"start": v(-50, 76) * mm, "end": v(-50, 72) * mm});
            skLineSegment(sketch, "E4.12.4.0", {"start": v(-46, 68) * mm, "end": v(-50, 68) * mm});
            skLineSegment(sketch, "E4.12.4.1", {"start": v(-46, 64) * mm, "end": v(-50, 64) * mm});
            skLineSegment(sketch, "E4.12.4.2", {"start": v(-46, 68) * mm, "end": v(-46, 64) * mm});
            skLineSegment(sketch, "E4.12.4.3", {"start": v(-50, 68) * mm, "end": v(-50, 64) * mm});
            skLineSegment(sketch, "E4.12.5.0", {"start": v(-46, 60) * mm, "end": v(-50, 60) * mm});
            skLineSegment(sketch, "E4.12.5.1", {"start": v(-46, 56) * mm, "end": v(-50, 56) * mm});
            skLineSegment(sketch, "E4.12.5.2", {"start": v(-46, 60) * mm, "end": v(-46, 56) * mm});
            skLineSegment(sketch, "E4.12.5.3", {"start": v(-50, 60) * mm, "end": v(-50, 56) * mm});
            skLineSegment(sketch, "E4.12.6.0", {"start": v(-46, 52) * mm, "end": v(-50, 52) * mm});
            skLineSegment(sketch, "E4.12.6.1", {"start": v(-46, 48) * mm, "end": v(-50, 48) * mm});
            skLineSegment(sketch, "E4.12.6.2", {"start": v(-46, 52) * mm, "end": v(-46, 48) * mm});
            skLineSegment(sketch, "E4.12.6.3", {"start": v(-50, 52) * mm, "end": v(-50, 48) * mm});
            skLineSegment(sketch, "E4.12.7.0", {"start": v(-46, 44) * mm, "end": v(-50, 44) * mm});
            skLineSegment(sketch, "E4.12.7.1", {"start": v(-46, 40) * mm, "end": v(-50, 40) * mm});
            skLineSegment(sketch, "E4.12.7.2", {"start": v(-46, 44) * mm, "end": v(-46, 40) * mm});
            skLineSegment(sketch, "E4.12.7.3", {"start": v(-50, 44) * mm, "end": v(-50, 40) * mm});
            skLineSegment(sketch, "E4.12.8.0", {"start": v(-46, 36) * mm, "end": v(-50, 36) * mm});
            skLineSegment(sketch, "E4.12.8.1", {"start": v(-46, 32) * mm, "end": v(-50, 32) * mm});
            skLineSegment(sketch, "E4.12.8.2", {"start": v(-46, 36) * mm, "end": v(-46, 32) * mm});
            skLineSegment(sketch, "E4.12.8.3", {"start": v(-50, 36) * mm, "end": v(-50, 32) * mm});
            skLineSegment(sketch, "E4.12.9.0", {"start": v(-46, 28) * mm, "end": v(-50, 28) * mm});
            skLineSegment(sketch, "E4.12.9.1", {"start": v(-46, 24) * mm, "end": v(-50, 24) * mm});
            skLineSegment(sketch, "E4.12.9.2", {"start": v(-46, 28) * mm, "end": v(-46, 24) * mm});
            skLineSegment(sketch, "E4.12.9.3", {"start": v(-50, 28) * mm, "end": v(-50, 24) * mm});
            skLineSegment(sketch, "E4.12.10.0", {"start": v(-46, 20) * mm, "end": v(-50, 20) * mm});
            skLineSegment(sketch, "E4.12.10.1", {"start": v(-46, 16) * mm, "end": v(-50, 16) * mm});
            skLineSegment(sketch, "E4.12.10.2", {"start": v(-46, 20) * mm, "end": v(-46, 16) * mm});
            skLineSegment(sketch, "E4.12.10.3", {"start": v(-50, 20) * mm, "end": v(-50, 16) * mm});
            skLineSegment(sketch, "E4.12.11.0", {"start": v(-46, 12) * mm, "end": v(-50, 12) * mm});
            skLineSegment(sketch, "E4.12.11.1", {"start": v(-46, 8) * mm, "end": v(-50, 8) * mm});
            skLineSegment(sketch, "E4.12.11.2", {"start": v(-46, 12) * mm, "end": v(-46, 8) * mm});
            skLineSegment(sketch, "E4.12.11.3", {"start": v(-50, 12) * mm, "end": v(-50, 8) * mm});
            skLineSegment(sketch, "E4.12.12.0", {"start": v(-46, 4) * mm, "end": v(-50, 4) * mm});
            skLineSegment(sketch, "E4.12.12.1", {"start": v(-46, 0) * mm, "end": v(-50, 0) * mm});
            skLineSegment(sketch, "E4.12.12.2", {"start": v(-46, 4) * mm, "end": v(-46, 0) * mm});
            skLineSegment(sketch, "E4.12.12.3", {"start": v(-50, 4) * mm, "end": v(-50, 0) * mm});
            skLineSegment(sketch, "E4.direction1", {"start": v(46, 100) * mm, "end": v(38, 100) * mm, "construction": true});
            skLineSegment(sketch, "E4.direction2", {"start": v(46, 100) * mm, "end": v(46, 92) * mm, "construction": true});
            skLineSegment(sketch, "E5.bottom", {"start": v(-50, 100) * mm, "end": v(50, 100) * mm});
            skLineSegment(sketch, "E5.top", {"start": v(-50, 0) * mm, "end": v(50, 0) * mm});
            skLineSegment(sketch, "E5.left", {"start": v(-50, 100) * mm, "end": v(-50, 0) * mm});
            skLineSegment(sketch, "E5.right", {"start": v(50, 100) * mm, "end": v(50, 0) * mm});
            skLineSegment(sketch, "E6.bottom", {"start": v(-46, 96) * mm, "end": v(46, 96) * mm});
            skLineSegment(sketch, "E6.top", {"start": v(-46, 4) * mm, "end": v(46, 4) * mm});
            skLineSegment(sketch, "E6.left", {"start": v(-46, 96) * mm, "end": v(-46, 4) * mm});
            skLineSegment(sketch, "E6.right", {"start": v(46, 96) * mm, "end": v(46, 4) * mm});
            skSolve(sketch);
        }
        {
            var Q0;
            Q0=makeQuery(id+"F2.imprint","IMPRINT",FACE,{"disambiguationData":[TD([[makeQuery(id+"F2.imprint","IMPRINT",EDGE,{"derivedFrom":sQuery(id+"F2.wireOp",EDGE,"E4.1.1.0")}),-1.0]])]});
            var Q1;
            {var subQ2=sQuery(id+"F2.wireOp",EDGE,"E4.11.0.2");Q1=makeQuery(id+"F2.imprint","IMPRINT",FACE,{"disambiguationData":[TD([[makeQuery(id+"F2.imprint","IMPRINT",EDGE,{"derivedFrom":subQ2}),-1.0]])]});}
            var Q2;
            {var subQ2=sQuery(id+"F2.wireOp",EDGE,"E4.10.0.2");Q2=makeQuery(id+"F2.imprint","IMPRINT",FACE,{"disambiguationData":[TD([[makeQuery(id+"F2.imprint","IMPRINT",EDGE,{"derivedFrom":subQ2}),-1.0]])]});}
            var Q3;
            {var subQ2=sQuery(id+"F2.wireOp",EDGE,"E4.9.0.2");Q3=makeQuery(id+"F2.imprint","IMPRINT",FACE,{"disambiguationData":[TD([[makeQuery(id+"F2.imprint","IMPRINT",EDGE,{"derivedFrom":subQ2}),-1.0]])]});}
            var Q4;
            {var subQ2=sQuery(id+"F2.wireOp",EDGE,"E4.8.0.2");Q4=makeQuery(id+"F2.imprint","IMPRINT",FACE,{"disambiguationData":[TD([[makeQuery(id+"F2.imprint","IMPRINT",EDGE,{"derivedFrom":subQ2}),-1.0]])]});}
            var Q5;
            {var subQ2=sQuery(id+"F2.wireOp",EDGE,"E4.7.0.2");Q5=makeQuery(id+"F2.imprint","IMPRINT",FACE,{"disambiguationData":[TD([[makeQuery(id+"F2.imprint","IMPRINT",EDGE,{"derivedFrom":subQ2}),-1.0]])]});}
            var Q6;
            {var subQ2=sQuery(id+"F2.wireOp",EDGE,"E4.6.0.2");Q6=makeQuery(id+"F2.imprint","IMPRINT",FACE,{"disambiguationData":[TD([[makeQuery(id+"F2.imprint","IMPRINT",EDGE,{"derivedFrom":subQ2}),-1.0]])]});}
            var Q7;
            {var subQ2=sQuery(id+"F2.wireOp",EDGE,"E4.5.0.2");Q7=makeQuery(id+"F2.imprint","IMPRINT",FACE,{"disambiguationData":[TD([[makeQuery(id+"F2.imprint","IMPRINT",EDGE,{"derivedFrom":subQ2}),-1.0]])]});}
            var Q8;
            {var subQ2=sQuery(id+"F2.wireOp",EDGE,"E4.4.0.2");Q8=makeQuery(id+"F2.imprint","IMPRINT",FACE,{"disambiguationData":[TD([[makeQuery(id+"F2.imprint","IMPRINT",EDGE,{"derivedFrom":subQ2}),-1.0]])]});}
            var Q9;
            {var subQ2=sQuery(id+"F2.wireOp",EDGE,"E4.3.0.2");Q9=makeQuery(id+"F2.imprint","IMPRINT",FACE,{"disambiguationData":[TD([[makeQuery(id+"F2.imprint","IMPRINT",EDGE,{"derivedFrom":subQ2}),-1.0]])]});}
            var Q10;
            {var subQ2=sQuery(id+"F2.wireOp",EDGE,"E4.2.0.2");Q10=makeQuery(id+"F2.imprint","IMPRINT",FACE,{"disambiguationData":[TD([[makeQuery(id+"F2.imprint","IMPRINT",EDGE,{"derivedFrom":subQ2}),-1.0]])]});}
            var Q11;
            {var subQ2=sQuery(id+"F2.wireOp",EDGE,"E4.1.0.2");Q11=makeQuery(id+"F2.imprint","IMPRINT",FACE,{"disambiguationData":[TD([[makeQuery(id+"F2.imprint","IMPRINT",EDGE,{"derivedFrom":subQ2}),-1.0]])]});}
            var Q12;
            {var subQ2=sQuery(id+"F2.wireOp",EDGE,"E4.0.1.0");Q12=makeQuery(id+"F2.imprint","IMPRINT",FACE,{"disambiguationData":[TD([[makeQuery(id+"F2.imprint","IMPRINT",EDGE,{"derivedFrom":subQ2}),1.0]])]});}
            var Q13;
            {var subQ2=sQuery(id+"F2.wireOp",EDGE,"E4.0.2.0");Q13=makeQuery(id+"F2.imprint","IMPRINT",FACE,{"disambiguationData":[TD([[makeQuery(id+"F2.imprint","IMPRINT",EDGE,{"derivedFrom":subQ2}),1.0]])]});}
            var Q14;
            {var subQ2=sQuery(id+"F2.wireOp",EDGE,"E4.0.3.0");Q14=makeQuery(id+"F2.imprint","IMPRINT",FACE,{"disambiguationData":[TD([[makeQuery(id+"F2.imprint","IMPRINT",EDGE,{"derivedFrom":subQ2}),1.0]])]});}
            var Q15;
            {var subQ2=sQuery(id+"F2.wireOp",EDGE,"E4.0.4.0");Q15=makeQuery(id+"F2.imprint","IMPRINT",FACE,{"disambiguationData":[TD([[makeQuery(id+"F2.imprint","IMPRINT",EDGE,{"derivedFrom":subQ2}),1.0]])]});}
            var Q16;
            {var subQ2=sQuery(id+"F2.wireOp",EDGE,"E4.0.5.0");Q16=makeQuery(id+"F2.imprint","IMPRINT",FACE,{"disambiguationData":[TD([[makeQuery(id+"F2.imprint","IMPRINT",EDGE,{"derivedFrom":subQ2}),1.0]])]});}
            var Q17;
            {var subQ2=sQuery(id+"F2.wireOp",EDGE,"E4.0.6.0");Q17=makeQuery(id+"F2.imprint","IMPRINT",FACE,{"disambiguationData":[TD([[makeQuery(id+"F2.imprint","IMPRINT",EDGE,{"derivedFrom":subQ2}),1.0]])]});}
            var Q18;
            {var subQ2=sQuery(id+"F2.wireOp",EDGE,"E4.0.7.0");Q18=makeQuery(id+"F2.imprint","IMPRINT",FACE,{"disambiguationData":[TD([[makeQuery(id+"F2.imprint","IMPRINT",EDGE,{"derivedFrom":subQ2}),1.0]])]});}
            var Q19;
            {var subQ2=sQuery(id+"F2.wireOp",EDGE,"E4.0.8.0");Q19=makeQuery(id+"F2.imprint","IMPRINT",FACE,{"disambiguationData":[TD([[makeQuery(id+"F2.imprint","IMPRINT",EDGE,{"derivedFrom":subQ2}),1.0]])]});}
            var Q20;
            {var subQ2=sQuery(id+"F2.wireOp",EDGE,"E4.0.9.0");Q20=makeQuery(id+"F2.imprint","IMPRINT",FACE,{"disambiguationData":[TD([[makeQuery(id+"F2.imprint","IMPRINT",EDGE,{"derivedFrom":subQ2}),1.0]])]});}
            var Q21;
            {var subQ2=sQuery(id+"F2.wireOp",EDGE,"E4.0.10.0");Q21=makeQuery(id+"F2.imprint","IMPRINT",FACE,{"disambiguationData":[TD([[makeQuery(id+"F2.imprint","IMPRINT",EDGE,{"derivedFrom":subQ2}),1.0]])]});}
            var Q22;
            {var subQ2=sQuery(id+"F2.wireOp",EDGE,"E4.0.11.0");Q22=makeQuery(id+"F2.imprint","IMPRINT",FACE,{"disambiguationData":[TD([[makeQuery(id+"F2.imprint","IMPRINT",EDGE,{"derivedFrom":subQ2}),1.0]])]});}
            var Q23;
            {var subQ2=sQuery(id+"F2.wireOp",EDGE,"E4.1.12.2");Q23=makeQuery(id+"F2.imprint","IMPRINT",FACE,{"disambiguationData":[TD([[makeQuery(id+"F2.imprint","IMPRINT",EDGE,{"derivedFrom":subQ2}),-1.0]])]});}
            var Q24;
            {var subQ2=sQuery(id+"F2.wireOp",EDGE,"E4.2.12.2");Q24=makeQuery(id+"F2.imprint","IMPRINT",FACE,{"disambiguationData":[TD([[makeQuery(id+"F2.imprint","IMPRINT",EDGE,{"derivedFrom":subQ2}),-1.0]])]});}
            var Q25;
            {var subQ2=sQuery(id+"F2.wireOp",EDGE,"E4.3.12.2");Q25=makeQuery(id+"F2.imprint","IMPRINT",FACE,{"disambiguationData":[TD([[makeQuery(id+"F2.imprint","IMPRINT",EDGE,{"derivedFrom":subQ2}),-1.0]])]});}
            var Q26;
            {var subQ2=sQuery(id+"F2.wireOp",EDGE,"E4.4.12.2");Q26=makeQuery(id+"F2.imprint","IMPRINT",FACE,{"disambiguationData":[TD([[makeQuery(id+"F2.imprint","IMPRINT",EDGE,{"derivedFrom":subQ2}),-1.0]])]});}
            var Q27;
            {var subQ2=sQuery(id+"F2.wireOp",EDGE,"E4.5.12.2");Q27=makeQuery(id+"F2.imprint","IMPRINT",FACE,{"disambiguationData":[TD([[makeQuery(id+"F2.imprint","IMPRINT",EDGE,{"derivedFrom":subQ2}),-1.0]])]});}
            var Q28;
            {var subQ2=sQuery(id+"F2.wireOp",EDGE,"E4.6.12.2");Q28=makeQuery(id+"F2.imprint","IMPRINT",FACE,{"disambiguationData":[TD([[makeQuery(id+"F2.imprint","IMPRINT",EDGE,{"derivedFrom":subQ2}),-1.0]])]});}
            var Q29;
            {var subQ2=sQuery(id+"F2.wireOp",EDGE,"E4.7.12.2");Q29=makeQuery(id+"F2.imprint","IMPRINT",FACE,{"disambiguationData":[TD([[makeQuery(id+"F2.imprint","IMPRINT",EDGE,{"derivedFrom":subQ2}),-1.0]])]});}
            var Q30;
            {var subQ2=sQuery(id+"F2.wireOp",EDGE,"E4.8.12.2");Q30=makeQuery(id+"F2.imprint","IMPRINT",FACE,{"disambiguationData":[TD([[makeQuery(id+"F2.imprint","IMPRINT",EDGE,{"derivedFrom":subQ2}),-1.0]])]});}
            var Q31;
            {var subQ2=sQuery(id+"F2.wireOp",EDGE,"E4.9.12.2");Q31=makeQuery(id+"F2.imprint","IMPRINT",FACE,{"disambiguationData":[TD([[makeQuery(id+"F2.imprint","IMPRINT",EDGE,{"derivedFrom":subQ2}),-1.0]])]});}
            var Q32;
            {var subQ2=sQuery(id+"F2.wireOp",EDGE,"E4.10.12.2");Q32=makeQuery(id+"F2.imprint","IMPRINT",FACE,{"disambiguationData":[TD([[makeQuery(id+"F2.imprint","IMPRINT",EDGE,{"derivedFrom":subQ2}),-1.0]])]});}
            var Q33;
            {var subQ2=sQuery(id+"F2.wireOp",EDGE,"E4.11.12.2");Q33=makeQuery(id+"F2.imprint","IMPRINT",FACE,{"disambiguationData":[TD([[makeQuery(id+"F2.imprint","IMPRINT",EDGE,{"derivedFrom":subQ2}),-1.0]])]});}
            var Q34;
            {var subQ2=sQuery(id+"F2.wireOp",EDGE,"E4.12.11.0");Q34=makeQuery(id+"F2.imprint","IMPRINT",FACE,{"disambiguationData":[TD([[makeQuery(id+"F2.imprint","IMPRINT",EDGE,{"derivedFrom":subQ2}),1.0]])]});}
            var Q35;
            {var subQ2=sQuery(id+"F2.wireOp",EDGE,"E4.12.10.0");Q35=makeQuery(id+"F2.imprint","IMPRINT",FACE,{"disambiguationData":[TD([[makeQuery(id+"F2.imprint","IMPRINT",EDGE,{"derivedFrom":subQ2}),1.0]])]});}
            var Q36;
            {var subQ2=sQuery(id+"F2.wireOp",EDGE,"E4.12.9.0");Q36=makeQuery(id+"F2.imprint","IMPRINT",FACE,{"disambiguationData":[TD([[makeQuery(id+"F2.imprint","IMPRINT",EDGE,{"derivedFrom":subQ2}),1.0]])]});}
            var Q37;
            {var subQ2=sQuery(id+"F2.wireOp",EDGE,"E4.12.8.0");Q37=makeQuery(id+"F2.imprint","IMPRINT",FACE,{"disambiguationData":[TD([[makeQuery(id+"F2.imprint","IMPRINT",EDGE,{"derivedFrom":subQ2}),1.0]])]});}
            var Q38;
            {var subQ2=sQuery(id+"F2.wireOp",EDGE,"E4.12.7.0");Q38=makeQuery(id+"F2.imprint","IMPRINT",FACE,{"disambiguationData":[TD([[makeQuery(id+"F2.imprint","IMPRINT",EDGE,{"derivedFrom":subQ2}),1.0]])]});}
            var Q39;
            {var subQ2=sQuery(id+"F2.wireOp",EDGE,"E4.12.6.0");Q39=makeQuery(id+"F2.imprint","IMPRINT",FACE,{"disambiguationData":[TD([[makeQuery(id+"F2.imprint","IMPRINT",EDGE,{"derivedFrom":subQ2}),1.0]])]});}
            var Q40;
            {var subQ2=sQuery(id+"F2.wireOp",EDGE,"E4.12.5.0");Q40=makeQuery(id+"F2.imprint","IMPRINT",FACE,{"disambiguationData":[TD([[makeQuery(id+"F2.imprint","IMPRINT",EDGE,{"derivedFrom":subQ2}),1.0]])]});}
            var Q41;
            {var subQ2=sQuery(id+"F2.wireOp",EDGE,"E4.12.4.0");Q41=makeQuery(id+"F2.imprint","IMPRINT",FACE,{"disambiguationData":[TD([[makeQuery(id+"F2.imprint","IMPRINT",EDGE,{"derivedFrom":subQ2}),1.0]])]});}
            var Q42;
            {var subQ2=sQuery(id+"F2.wireOp",EDGE,"E4.12.3.0");Q42=makeQuery(id+"F2.imprint","IMPRINT",FACE,{"disambiguationData":[TD([[makeQuery(id+"F2.imprint","IMPRINT",EDGE,{"derivedFrom":subQ2}),1.0]])]});}
            var Q43;
            {var subQ2=sQuery(id+"F2.wireOp",EDGE,"E4.12.2.0");Q43=makeQuery(id+"F2.imprint","IMPRINT",FACE,{"disambiguationData":[TD([[makeQuery(id+"F2.imprint","IMPRINT",EDGE,{"derivedFrom":subQ2}),1.0]])]});}
            var Q44;
            {var subQ2=sQuery(id+"F2.wireOp",EDGE,"E4.12.1.0");Q44=makeQuery(id+"F2.imprint","IMPRINT",FACE,{"disambiguationData":[TD([[makeQuery(id+"F2.imprint","IMPRINT",EDGE,{"derivedFrom":subQ2}),1.0]])]});}
            extrude(context, id + "F3", {"entities" : qUnion([Q0, Q1, Q2, Q3, Q4, Q5, Q6, Q7, Q8, Q9, Q10, Q11, Q12, Q13, Q14, Q15, Q16, Q17, Q18, Q19, Q20, Q21, Q22, Q23, Q24, Q25, Q26, Q27, Q28, Q29, Q30, Q31, Q32, Q33, Q34, Q35, Q36, Q37, Q38, Q39, Q40, Q41, Q42, Q43, Q44]), "depth" : 4 * mm});
        }
        {
            var Q0;
            Q0=qCreatedBy(makeId("Right.planeOp"),FACE);
            var sketch = newSketch(context, id + "F4", { "sketchPlane" : qUnion([Q0])});
            skLineSegment(sketch, "E7.bottom", {"start": v(50, 100) * mm, "end": v(46, 100) * mm});
            skLineSegment(sketch, "E7.top", {"start": v(50, 96) * mm, "end": v(46, 96) * mm});
            skLineSegment(sketch, "E7.left", {"start": v(50, 100) * mm, "end": v(50, 96) * mm});
            skLineSegment(sketch, "E7.right", {"start": v(46, 100) * mm, "end": v(46, 96) * mm});
            skLineSegment(sketch, "E8.0.1.0", {"start": v(50, 92) * mm, "end": v(46, 92) * mm});
            skLineSegment(sketch, "E8.0.1.1", {"start": v(50, 88) * mm, "end": v(46, 88) * mm});
            skLineSegment(sketch, "E8.0.1.2", {"start": v(50, 92) * mm, "end": v(50, 88) * mm});
            skLineSegment(sketch, "E8.0.1.3", {"start": v(46, 92) * mm, "end": v(46, 88) * mm});
            skLineSegment(sketch, "E8.0.2.0", {"start": v(50, 84) * mm, "end": v(46, 84) * mm});
            skLineSegment(sketch, "E8.0.2.1", {"start": v(50, 80) * mm, "end": v(46, 80) * mm});
            skLineSegment(sketch, "E8.0.2.2", {"start": v(50, 84) * mm, "end": v(50, 80) * mm});
            skLineSegment(sketch, "E8.0.2.3", {"start": v(46, 84) * mm, "end": v(46, 80) * mm});
            skLineSegment(sketch, "E8.0.3.0", {"start": v(50, 76) * mm, "end": v(46, 76) * mm});
            skLineSegment(sketch, "E8.0.3.1", {"start": v(50, 72) * mm, "end": v(46, 72) * mm});
            skLineSegment(sketch, "E8.0.3.2", {"start": v(50, 76) * mm, "end": v(50, 72) * mm});
            skLineSegment(sketch, "E8.0.3.3", {"start": v(46, 76) * mm, "end": v(46, 72) * mm});
            skLineSegment(sketch, "E8.0.4.0", {"start": v(50, 68) * mm, "end": v(46, 68) * mm});
            skLineSegment(sketch, "E8.0.4.1", {"start": v(50, 64) * mm, "end": v(46, 64) * mm});
            skLineSegment(sketch, "E8.0.4.2", {"start": v(50, 68) * mm, "end": v(50, 64) * mm});
            skLineSegment(sketch, "E8.0.4.3", {"start": v(46, 68) * mm, "end": v(46, 64) * mm});
            skLineSegment(sketch, "E8.0.5.0", {"start": v(50, 60) * mm, "end": v(46, 60) * mm});
            skLineSegment(sketch, "E8.0.5.1", {"start": v(50, 56) * mm, "end": v(46, 56) * mm});
            skLineSegment(sketch, "E8.0.5.2", {"start": v(50, 60) * mm, "end": v(50, 56) * mm});
            skLineSegment(sketch, "E8.0.5.3", {"start": v(46, 60) * mm, "end": v(46, 56) * mm});
            skLineSegment(sketch, "E8.0.6.0", {"start": v(50, 52) * mm, "end": v(46, 52) * mm});
            skLineSegment(sketch, "E8.0.6.1", {"start": v(50, 48) * mm, "end": v(46, 48) * mm});
            skLineSegment(sketch, "E8.0.6.2", {"start": v(50, 52) * mm, "end": v(50, 48) * mm});
            skLineSegment(sketch, "E8.0.6.3", {"start": v(46, 52) * mm, "end": v(46, 48) * mm});
            skLineSegment(sketch, "E8.0.7.0", {"start": v(50, 44) * mm, "end": v(46, 44) * mm});
            skLineSegment(sketch, "E8.0.7.1", {"start": v(50, 40) * mm, "end": v(46, 40) * mm});
            skLineSegment(sketch, "E8.0.7.2", {"start": v(50, 44) * mm, "end": v(50, 40) * mm});
            skLineSegment(sketch, "E8.0.7.3", {"start": v(46, 44) * mm, "end": v(46, 40) * mm});
            skLineSegment(sketch, "E8.0.8.0", {"start": v(50, 36) * mm, "end": v(46, 36) * mm});
            skLineSegment(sketch, "E8.0.8.1", {"start": v(50, 32) * mm, "end": v(46, 32) * mm});
            skLineSegment(sketch, "E8.0.8.2", {"start": v(50, 36) * mm, "end": v(50, 32) * mm});
            skLineSegment(sketch, "E8.0.8.3", {"start": v(46, 36) * mm, "end": v(46, 32) * mm});
            skLineSegment(sketch, "E8.0.9.0", {"start": v(50, 28) * mm, "end": v(46, 28) * mm});
            skLineSegment(sketch, "E8.0.9.1", {"start": v(50, 24) * mm, "end": v(46, 24) * mm});
            skLineSegment(sketch, "E8.0.9.2", {"start": v(50, 28) * mm, "end": v(50, 24) * mm});
            skLineSegment(sketch, "E8.0.9.3", {"start": v(46, 28) * mm, "end": v(46, 24) * mm});
            skLineSegment(sketch, "E8.0.10.0", {"start": v(50, 20) * mm, "end": v(46, 20) * mm});
            skLineSegment(sketch, "E8.0.10.1", {"start": v(50, 16) * mm, "end": v(46, 16) * mm});
            skLineSegment(sketch, "E8.0.10.2", {"start": v(50, 20) * mm, "end": v(50, 16) * mm});
            skLineSegment(sketch, "E8.0.10.3", {"start": v(46, 20) * mm, "end": v(46, 16) * mm});
            skLineSegment(sketch, "E8.0.11.0", {"start": v(50, 12) * mm, "end": v(46, 12) * mm});
            skLineSegment(sketch, "E8.0.11.1", {"start": v(50, 8) * mm, "end": v(46, 8) * mm});
            skLineSegment(sketch, "E8.0.11.2", {"start": v(50, 12) * mm, "end": v(50, 8) * mm});
            skLineSegment(sketch, "E8.0.11.3", {"start": v(46, 12) * mm, "end": v(46, 8) * mm});
            skLineSegment(sketch, "E8.0.12.0", {"start": v(50, 4) * mm, "end": v(46, 4) * mm});
            skLineSegment(sketch, "E8.0.12.1", {"start": v(50, 0) * mm, "end": v(46, 0) * mm});
            skLineSegment(sketch, "E8.0.12.2", {"start": v(50, 4) * mm, "end": v(50, 0) * mm});
            skLineSegment(sketch, "E8.0.12.3", {"start": v(46, 4) * mm, "end": v(46, 0) * mm});
            skLineSegment(sketch, "E8.1.0.0", {"start": v(42, 100) * mm, "end": v(38, 100) * mm});
            skLineSegment(sketch, "E8.1.0.1", {"start": v(42, 96) * mm, "end": v(38, 96) * mm});
            skLineSegment(sketch, "E8.1.0.2", {"start": v(42, 100) * mm, "end": v(42, 96) * mm});
            skLineSegment(sketch, "E8.1.0.3", {"start": v(38, 100) * mm, "end": v(38, 96) * mm});
            skLineSegment(sketch, "E8.1.1.0", {"start": v(42, 92) * mm, "end": v(38, 92) * mm});
            skLineSegment(sketch, "E8.1.1.1", {"start": v(42, 88) * mm, "end": v(38, 88) * mm});
            skLineSegment(sketch, "E8.1.1.2", {"start": v(42, 92) * mm, "end": v(42, 88) * mm});
            skLineSegment(sketch, "E8.1.1.3", {"start": v(38, 92) * mm, "end": v(38, 88) * mm});
            skLineSegment(sketch, "E8.1.2.0", {"start": v(42, 84) * mm, "end": v(38, 84) * mm});
            skLineSegment(sketch, "E8.1.2.1", {"start": v(42, 80) * mm, "end": v(38, 80) * mm});
            skLineSegment(sketch, "E8.1.2.2", {"start": v(42, 84) * mm, "end": v(42, 80) * mm});
            skLineSegment(sketch, "E8.1.2.3", {"start": v(38, 84) * mm, "end": v(38, 80) * mm});
            skLineSegment(sketch, "E8.1.3.0", {"start": v(42, 76) * mm, "end": v(38, 76) * mm});
            skLineSegment(sketch, "E8.1.3.1", {"start": v(42, 72) * mm, "end": v(38, 72) * mm});
            skLineSegment(sketch, "E8.1.3.2", {"start": v(42, 76) * mm, "end": v(42, 72) * mm});
            skLineSegment(sketch, "E8.1.3.3", {"start": v(38, 76) * mm, "end": v(38, 72) * mm});
            skLineSegment(sketch, "E8.1.4.0", {"start": v(42, 68) * mm, "end": v(38, 68) * mm});
            skLineSegment(sketch, "E8.1.4.1", {"start": v(42, 64) * mm, "end": v(38, 64) * mm});
            skLineSegment(sketch, "E8.1.4.2", {"start": v(42, 68) * mm, "end": v(42, 64) * mm});
            skLineSegment(sketch, "E8.1.4.3", {"start": v(38, 68) * mm, "end": v(38, 64) * mm});
            skLineSegment(sketch, "E8.1.5.0", {"start": v(42, 60) * mm, "end": v(38, 60) * mm});
            skLineSegment(sketch, "E8.1.5.1", {"start": v(42, 56) * mm, "end": v(38, 56) * mm});
            skLineSegment(sketch, "E8.1.5.2", {"start": v(42, 60) * mm, "end": v(42, 56) * mm});
            skLineSegment(sketch, "E8.1.5.3", {"start": v(38, 60) * mm, "end": v(38, 56) * mm});
            skLineSegment(sketch, "E8.1.6.0", {"start": v(42, 52) * mm, "end": v(38, 52) * mm});
            skLineSegment(sketch, "E8.1.6.1", {"start": v(42, 48) * mm, "end": v(38, 48) * mm});
            skLineSegment(sketch, "E8.1.6.2", {"start": v(42, 52) * mm, "end": v(42, 48) * mm});
            skLineSegment(sketch, "E8.1.6.3", {"start": v(38, 52) * mm, "end": v(38, 48) * mm});
            skLineSegment(sketch, "E8.1.7.0", {"start": v(42, 44) * mm, "end": v(38, 44) * mm});
            skLineSegment(sketch, "E8.1.7.1", {"start": v(42, 40) * mm, "end": v(38, 40) * mm});
            skLineSegment(sketch, "E8.1.7.2", {"start": v(42, 44) * mm, "end": v(42, 40) * mm});
            skLineSegment(sketch, "E8.1.7.3", {"start": v(38, 44) * mm, "end": v(38, 40) * mm});
            skLineSegment(sketch, "E8.1.8.0", {"start": v(42, 36) * mm, "end": v(38, 36) * mm});
            skLineSegment(sketch, "E8.1.8.1", {"start": v(42, 32) * mm, "end": v(38, 32) * mm});
            skLineSegment(sketch, "E8.1.8.2", {"start": v(42, 36) * mm, "end": v(42, 32) * mm});
            skLineSegment(sketch, "E8.1.8.3", {"start": v(38, 36) * mm, "end": v(38, 32) * mm});
            skLineSegment(sketch, "E8.1.9.0", {"start": v(42, 28) * mm, "end": v(38, 28) * mm});
            skLineSegment(sketch, "E8.1.9.1", {"start": v(42, 24) * mm, "end": v(38, 24) * mm});
            skLineSegment(sketch, "E8.1.9.2", {"start": v(42, 28) * mm, "end": v(42, 24) * mm});
            skLineSegment(sketch, "E8.1.9.3", {"start": v(38, 28) * mm, "end": v(38, 24) * mm});
            skLineSegment(sketch, "E8.1.10.0", {"start": v(42, 20) * mm, "end": v(38, 20) * mm});
            skLineSegment(sketch, "E8.1.10.1", {"start": v(42, 16) * mm, "end": v(38, 16) * mm});
            skLineSegment(sketch, "E8.1.10.2", {"start": v(42, 20) * mm, "end": v(42, 16) * mm});
            skLineSegment(sketch, "E8.1.10.3", {"start": v(38, 20) * mm, "end": v(38, 16) * mm});
            skLineSegment(sketch, "E8.1.11.0", {"start": v(42, 12) * mm, "end": v(38, 12) * mm});
            skLineSegment(sketch, "E8.1.11.1", {"start": v(42, 8) * mm, "end": v(38, 8) * mm});
            skLineSegment(sketch, "E8.1.11.2", {"start": v(42, 12) * mm, "end": v(42, 8) * mm});
            skLineSegment(sketch, "E8.1.11.3", {"start": v(38, 12) * mm, "end": v(38, 8) * mm});
            skLineSegment(sketch, "E8.1.12.0", {"start": v(42, 4) * mm, "end": v(38, 4) * mm});
            skLineSegment(sketch, "E8.1.12.1", {"start": v(42, 0) * mm, "end": v(38, 0) * mm});
            skLineSegment(sketch, "E8.1.12.2", {"start": v(42, 4) * mm, "end": v(42, 0) * mm});
            skLineSegment(sketch, "E8.1.12.3", {"start": v(38, 4) * mm, "end": v(38, 0) * mm});
            skLineSegment(sketch, "E8.2.0.0", {"start": v(34, 100) * mm, "end": v(30, 100) * mm});
            skLineSegment(sketch, "E8.2.0.1", {"start": v(34, 96) * mm, "end": v(30, 96) * mm});
            skLineSegment(sketch, "E8.2.0.2", {"start": v(34, 100) * mm, "end": v(34, 96) * mm});
            skLineSegment(sketch, "E8.2.0.3", {"start": v(30, 100) * mm, "end": v(30, 96) * mm});
            skLineSegment(sketch, "E8.2.1.0", {"start": v(34, 92) * mm, "end": v(30, 92) * mm});
            skLineSegment(sketch, "E8.2.1.1", {"start": v(34, 88) * mm, "end": v(30, 88) * mm});
            skLineSegment(sketch, "E8.2.1.2", {"start": v(34, 92) * mm, "end": v(34, 88) * mm});
            skLineSegment(sketch, "E8.2.1.3", {"start": v(30, 92) * mm, "end": v(30, 88) * mm});
            skLineSegment(sketch, "E8.2.2.0", {"start": v(34, 84) * mm, "end": v(30, 84) * mm});
            skLineSegment(sketch, "E8.2.2.1", {"start": v(34, 80) * mm, "end": v(30, 80) * mm});
            skLineSegment(sketch, "E8.2.2.2", {"start": v(34, 84) * mm, "end": v(34, 80) * mm});
            skLineSegment(sketch, "E8.2.2.3", {"start": v(30, 84) * mm, "end": v(30, 80) * mm});
            skLineSegment(sketch, "E8.2.3.0", {"start": v(34, 76) * mm, "end": v(30, 76) * mm});
            skLineSegment(sketch, "E8.2.3.1", {"start": v(34, 72) * mm, "end": v(30, 72) * mm});
            skLineSegment(sketch, "E8.2.3.2", {"start": v(34, 76) * mm, "end": v(34, 72) * mm});
            skLineSegment(sketch, "E8.2.3.3", {"start": v(30, 76) * mm, "end": v(30, 72) * mm});
            skLineSegment(sketch, "E8.2.4.0", {"start": v(34, 68) * mm, "end": v(30, 68) * mm});
            skLineSegment(sketch, "E8.2.4.1", {"start": v(34, 64) * mm, "end": v(30, 64) * mm});
            skLineSegment(sketch, "E8.2.4.2", {"start": v(34, 68) * mm, "end": v(34, 64) * mm});
            skLineSegment(sketch, "E8.2.4.3", {"start": v(30, 68) * mm, "end": v(30, 64) * mm});
            skLineSegment(sketch, "E8.2.5.0", {"start": v(34, 60) * mm, "end": v(30, 60) * mm});
            skLineSegment(sketch, "E8.2.5.1", {"start": v(34, 56) * mm, "end": v(30, 56) * mm});
            skLineSegment(sketch, "E8.2.5.2", {"start": v(34, 60) * mm, "end": v(34, 56) * mm});
            skLineSegment(sketch, "E8.2.5.3", {"start": v(30, 60) * mm, "end": v(30, 56) * mm});
            skLineSegment(sketch, "E8.2.6.0", {"start": v(34, 52) * mm, "end": v(30, 52) * mm});
            skLineSegment(sketch, "E8.2.6.1", {"start": v(34, 48) * mm, "end": v(30, 48) * mm});
            skLineSegment(sketch, "E8.2.6.2", {"start": v(34, 52) * mm, "end": v(34, 48) * mm});
            skLineSegment(sketch, "E8.2.6.3", {"start": v(30, 52) * mm, "end": v(30, 48) * mm});
            skLineSegment(sketch, "E8.2.7.0", {"start": v(34, 44) * mm, "end": v(30, 44) * mm});
            skLineSegment(sketch, "E8.2.7.1", {"start": v(34, 40) * mm, "end": v(30, 40) * mm});
            skLineSegment(sketch, "E8.2.7.2", {"start": v(34, 44) * mm, "end": v(34, 40) * mm});
            skLineSegment(sketch, "E8.2.7.3", {"start": v(30, 44) * mm, "end": v(30, 40) * mm});
            skLineSegment(sketch, "E8.2.8.0", {"start": v(34, 36) * mm, "end": v(30, 36) * mm});
            skLineSegment(sketch, "E8.2.8.1", {"start": v(34, 32) * mm, "end": v(30, 32) * mm});
            skLineSegment(sketch, "E8.2.8.2", {"start": v(34, 36) * mm, "end": v(34, 32) * mm});
            skLineSegment(sketch, "E8.2.8.3", {"start": v(30, 36) * mm, "end": v(30, 32) * mm});
            skLineSegment(sketch, "E8.2.9.0", {"start": v(34, 28) * mm, "end": v(30, 28) * mm});
            skLineSegment(sketch, "E8.2.9.1", {"start": v(34, 24) * mm, "end": v(30, 24) * mm});
            skLineSegment(sketch, "E8.2.9.2", {"start": v(34, 28) * mm, "end": v(34, 24) * mm});
            skLineSegment(sketch, "E8.2.9.3", {"start": v(30, 28) * mm, "end": v(30, 24) * mm});
            skLineSegment(sketch, "E8.2.10.0", {"start": v(34, 20) * mm, "end": v(30, 20) * mm});
            skLineSegment(sketch, "E8.2.10.1", {"start": v(34, 16) * mm, "end": v(30, 16) * mm});
            skLineSegment(sketch, "E8.2.10.2", {"start": v(34, 20) * mm, "end": v(34, 16) * mm});
            skLineSegment(sketch, "E8.2.10.3", {"start": v(30, 20) * mm, "end": v(30, 16) * mm});
            skLineSegment(sketch, "E8.2.11.0", {"start": v(34, 12) * mm, "end": v(30, 12) * mm});
            skLineSegment(sketch, "E8.2.11.1", {"start": v(34, 8) * mm, "end": v(30, 8) * mm});
            skLineSegment(sketch, "E8.2.11.2", {"start": v(34, 12) * mm, "end": v(34, 8) * mm});
            skLineSegment(sketch, "E8.2.11.3", {"start": v(30, 12) * mm, "end": v(30, 8) * mm});
            skLineSegment(sketch, "E8.2.12.0", {"start": v(34, 4) * mm, "end": v(30, 4) * mm});
            skLineSegment(sketch, "E8.2.12.1", {"start": v(34, 0) * mm, "end": v(30, 0) * mm});
            skLineSegment(sketch, "E8.2.12.2", {"start": v(34, 4) * mm, "end": v(34, 0) * mm});
            skLineSegment(sketch, "E8.2.12.3", {"start": v(30, 4) * mm, "end": v(30, 0) * mm});
            skLineSegment(sketch, "E8.3.0.0", {"start": v(26, 100) * mm, "end": v(22, 100) * mm});
            skLineSegment(sketch, "E8.3.0.1", {"start": v(26, 96) * mm, "end": v(22, 96) * mm});
            skLineSegment(sketch, "E8.3.0.2", {"start": v(26, 100) * mm, "end": v(26, 96) * mm});
            skLineSegment(sketch, "E8.3.0.3", {"start": v(22, 100) * mm, "end": v(22, 96) * mm});
            skLineSegment(sketch, "E8.3.1.0", {"start": v(26, 92) * mm, "end": v(22, 92) * mm});
            skLineSegment(sketch, "E8.3.1.1", {"start": v(26, 88) * mm, "end": v(22, 88) * mm});
            skLineSegment(sketch, "E8.3.1.2", {"start": v(26, 92) * mm, "end": v(26, 88) * mm});
            skLineSegment(sketch, "E8.3.1.3", {"start": v(22, 92) * mm, "end": v(22, 88) * mm});
            skLineSegment(sketch, "E8.3.2.0", {"start": v(26, 84) * mm, "end": v(22, 84) * mm});
            skLineSegment(sketch, "E8.3.2.1", {"start": v(26, 80) * mm, "end": v(22, 80) * mm});
            skLineSegment(sketch, "E8.3.2.2", {"start": v(26, 84) * mm, "end": v(26, 80) * mm});
            skLineSegment(sketch, "E8.3.2.3", {"start": v(22, 84) * mm, "end": v(22, 80) * mm});
            skLineSegment(sketch, "E8.3.3.0", {"start": v(26, 76) * mm, "end": v(22, 76) * mm});
            skLineSegment(sketch, "E8.3.3.1", {"start": v(26, 72) * mm, "end": v(22, 72) * mm});
            skLineSegment(sketch, "E8.3.3.2", {"start": v(26, 76) * mm, "end": v(26, 72) * mm});
            skLineSegment(sketch, "E8.3.3.3", {"start": v(22, 76) * mm, "end": v(22, 72) * mm});
            skLineSegment(sketch, "E8.3.4.0", {"start": v(26, 68) * mm, "end": v(22, 68) * mm});
            skLineSegment(sketch, "E8.3.4.1", {"start": v(26, 64) * mm, "end": v(22, 64) * mm});
            skLineSegment(sketch, "E8.3.4.2", {"start": v(26, 68) * mm, "end": v(26, 64) * mm});
            skLineSegment(sketch, "E8.3.4.3", {"start": v(22, 68) * mm, "end": v(22, 64) * mm});
            skLineSegment(sketch, "E8.3.5.0", {"start": v(26, 60) * mm, "end": v(22, 60) * mm});
            skLineSegment(sketch, "E8.3.5.1", {"start": v(26, 56) * mm, "end": v(22, 56) * mm});
            skLineSegment(sketch, "E8.3.5.2", {"start": v(26, 60) * mm, "end": v(26, 56) * mm});
            skLineSegment(sketch, "E8.3.5.3", {"start": v(22, 60) * mm, "end": v(22, 56) * mm});
            skLineSegment(sketch, "E8.3.6.0", {"start": v(26, 52) * mm, "end": v(22, 52) * mm});
            skLineSegment(sketch, "E8.3.6.1", {"start": v(26, 48) * mm, "end": v(22, 48) * mm});
            skLineSegment(sketch, "E8.3.6.2", {"start": v(26, 52) * mm, "end": v(26, 48) * mm});
            skLineSegment(sketch, "E8.3.6.3", {"start": v(22, 52) * mm, "end": v(22, 48) * mm});
            skLineSegment(sketch, "E8.3.7.0", {"start": v(26, 44) * mm, "end": v(22, 44) * mm});
            skLineSegment(sketch, "E8.3.7.1", {"start": v(26, 40) * mm, "end": v(22, 40) * mm});
            skLineSegment(sketch, "E8.3.7.2", {"start": v(26, 44) * mm, "end": v(26, 40) * mm});
            skLineSegment(sketch, "E8.3.7.3", {"start": v(22, 44) * mm, "end": v(22, 40) * mm});
            skLineSegment(sketch, "E8.3.8.0", {"start": v(26, 36) * mm, "end": v(22, 36) * mm});
            skLineSegment(sketch, "E8.3.8.1", {"start": v(26, 32) * mm, "end": v(22, 32) * mm});
            skLineSegment(sketch, "E8.3.8.2", {"start": v(26, 36) * mm, "end": v(26, 32) * mm});
            skLineSegment(sketch, "E8.3.8.3", {"start": v(22, 36) * mm, "end": v(22, 32) * mm});
            skLineSegment(sketch, "E8.3.9.0", {"start": v(26, 28) * mm, "end": v(22, 28) * mm});
            skLineSegment(sketch, "E8.3.9.1", {"start": v(26, 24) * mm, "end": v(22, 24) * mm});
            skLineSegment(sketch, "E8.3.9.2", {"start": v(26, 28) * mm, "end": v(26, 24) * mm});
            skLineSegment(sketch, "E8.3.9.3", {"start": v(22, 28) * mm, "end": v(22, 24) * mm});
            skLineSegment(sketch, "E8.3.10.0", {"start": v(26, 20) * mm, "end": v(22, 20) * mm});
            skLineSegment(sketch, "E8.3.10.1", {"start": v(26, 16) * mm, "end": v(22, 16) * mm});
            skLineSegment(sketch, "E8.3.10.2", {"start": v(26, 20) * mm, "end": v(26, 16) * mm});
            skLineSegment(sketch, "E8.3.10.3", {"start": v(22, 20) * mm, "end": v(22, 16) * mm});
            skLineSegment(sketch, "E8.3.11.0", {"start": v(26, 12) * mm, "end": v(22, 12) * mm});
            skLineSegment(sketch, "E8.3.11.1", {"start": v(26, 8) * mm, "end": v(22, 8) * mm});
            skLineSegment(sketch, "E8.3.11.2", {"start": v(26, 12) * mm, "end": v(26, 8) * mm});
            skLineSegment(sketch, "E8.3.11.3", {"start": v(22, 12) * mm, "end": v(22, 8) * mm});
            skLineSegment(sketch, "E8.3.12.0", {"start": v(26, 4) * mm, "end": v(22, 4) * mm});
            skLineSegment(sketch, "E8.3.12.1", {"start": v(26, 0) * mm, "end": v(22, 0) * mm});
            skLineSegment(sketch, "E8.3.12.2", {"start": v(26, 4) * mm, "end": v(26, 0) * mm});
            skLineSegment(sketch, "E8.3.12.3", {"start": v(22, 4) * mm, "end": v(22, 0) * mm});
            skLineSegment(sketch, "E8.4.0.0", {"start": v(18, 100) * mm, "end": v(14, 100) * mm});
            skLineSegment(sketch, "E8.4.0.1", {"start": v(18, 96) * mm, "end": v(14, 96) * mm});
            skLineSegment(sketch, "E8.4.0.2", {"start": v(18, 100) * mm, "end": v(18, 96) * mm});
            skLineSegment(sketch, "E8.4.0.3", {"start": v(14, 100) * mm, "end": v(14, 96) * mm});
            skLineSegment(sketch, "E8.4.1.0", {"start": v(18, 92) * mm, "end": v(14, 92) * mm});
            skLineSegment(sketch, "E8.4.1.1", {"start": v(18, 88) * mm, "end": v(14, 88) * mm});
            skLineSegment(sketch, "E8.4.1.2", {"start": v(18, 92) * mm, "end": v(18, 88) * mm});
            skLineSegment(sketch, "E8.4.1.3", {"start": v(14, 92) * mm, "end": v(14, 88) * mm});
            skLineSegment(sketch, "E8.4.2.0", {"start": v(18, 84) * mm, "end": v(14, 84) * mm});
            skLineSegment(sketch, "E8.4.2.1", {"start": v(18, 80) * mm, "end": v(14, 80) * mm});
            skLineSegment(sketch, "E8.4.2.2", {"start": v(18, 84) * mm, "end": v(18, 80) * mm});
            skLineSegment(sketch, "E8.4.2.3", {"start": v(14, 84) * mm, "end": v(14, 80) * mm});
            skLineSegment(sketch, "E8.4.3.0", {"start": v(18, 76) * mm, "end": v(14, 76) * mm});
            skLineSegment(sketch, "E8.4.3.1", {"start": v(18, 72) * mm, "end": v(14, 72) * mm});
            skLineSegment(sketch, "E8.4.3.2", {"start": v(18, 76) * mm, "end": v(18, 72) * mm});
            skLineSegment(sketch, "E8.4.3.3", {"start": v(14, 76) * mm, "end": v(14, 72) * mm});
            skLineSegment(sketch, "E8.4.4.0", {"start": v(18, 68) * mm, "end": v(14, 68) * mm});
            skLineSegment(sketch, "E8.4.4.1", {"start": v(18, 64) * mm, "end": v(14, 64) * mm});
            skLineSegment(sketch, "E8.4.4.2", {"start": v(18, 68) * mm, "end": v(18, 64) * mm});
            skLineSegment(sketch, "E8.4.4.3", {"start": v(14, 68) * mm, "end": v(14, 64) * mm});
            skLineSegment(sketch, "E8.4.5.0", {"start": v(18, 60) * mm, "end": v(14, 60) * mm});
            skLineSegment(sketch, "E8.4.5.1", {"start": v(18, 56) * mm, "end": v(14, 56) * mm});
            skLineSegment(sketch, "E8.4.5.2", {"start": v(18, 60) * mm, "end": v(18, 56) * mm});
            skLineSegment(sketch, "E8.4.5.3", {"start": v(14, 60) * mm, "end": v(14, 56) * mm});
            skLineSegment(sketch, "E8.4.6.0", {"start": v(18, 52) * mm, "end": v(14, 52) * mm});
            skLineSegment(sketch, "E8.4.6.1", {"start": v(18, 48) * mm, "end": v(14, 48) * mm});
            skLineSegment(sketch, "E8.4.6.2", {"start": v(18, 52) * mm, "end": v(18, 48) * mm});
            skLineSegment(sketch, "E8.4.6.3", {"start": v(14, 52) * mm, "end": v(14, 48) * mm});
            skLineSegment(sketch, "E8.4.7.0", {"start": v(18, 44) * mm, "end": v(14, 44) * mm});
            skLineSegment(sketch, "E8.4.7.1", {"start": v(18, 40) * mm, "end": v(14, 40) * mm});
            skLineSegment(sketch, "E8.4.7.2", {"start": v(18, 44) * mm, "end": v(18, 40) * mm});
            skLineSegment(sketch, "E8.4.7.3", {"start": v(14, 44) * mm, "end": v(14, 40) * mm});
            skLineSegment(sketch, "E8.4.8.0", {"start": v(18, 36) * mm, "end": v(14, 36) * mm});
            skLineSegment(sketch, "E8.4.8.1", {"start": v(18, 32) * mm, "end": v(14, 32) * mm});
            skLineSegment(sketch, "E8.4.8.2", {"start": v(18, 36) * mm, "end": v(18, 32) * mm});
            skLineSegment(sketch, "E8.4.8.3", {"start": v(14, 36) * mm, "end": v(14, 32) * mm});
            skLineSegment(sketch, "E8.4.9.0", {"start": v(18, 28) * mm, "end": v(14, 28) * mm});
            skLineSegment(sketch, "E8.4.9.1", {"start": v(18, 24) * mm, "end": v(14, 24) * mm});
            skLineSegment(sketch, "E8.4.9.2", {"start": v(18, 28) * mm, "end": v(18, 24) * mm});
            skLineSegment(sketch, "E8.4.9.3", {"start": v(14, 28) * mm, "end": v(14, 24) * mm});
            skLineSegment(sketch, "E8.4.10.0", {"start": v(18, 20) * mm, "end": v(14, 20) * mm});
            skLineSegment(sketch, "E8.4.10.1", {"start": v(18, 16) * mm, "end": v(14, 16) * mm});
            skLineSegment(sketch, "E8.4.10.2", {"start": v(18, 20) * mm, "end": v(18, 16) * mm});
            skLineSegment(sketch, "E8.4.10.3", {"start": v(14, 20) * mm, "end": v(14, 16) * mm});
            skLineSegment(sketch, "E8.4.11.0", {"start": v(18, 12) * mm, "end": v(14, 12) * mm});
            skLineSegment(sketch, "E8.4.11.1", {"start": v(18, 8) * mm, "end": v(14, 8) * mm});
            skLineSegment(sketch, "E8.4.11.2", {"start": v(18, 12) * mm, "end": v(18, 8) * mm});
            skLineSegment(sketch, "E8.4.11.3", {"start": v(14, 12) * mm, "end": v(14, 8) * mm});
            skLineSegment(sketch, "E8.4.12.0", {"start": v(18, 4) * mm, "end": v(14, 4) * mm});
            skLineSegment(sketch, "E8.4.12.1", {"start": v(18, 0) * mm, "end": v(14, 0) * mm});
            skLineSegment(sketch, "E8.4.12.2", {"start": v(18, 4) * mm, "end": v(18, 0) * mm});
            skLineSegment(sketch, "E8.4.12.3", {"start": v(14, 4) * mm, "end": v(14, 0) * mm});
            skLineSegment(sketch, "E8.5.0.0", {"start": v(10, 100) * mm, "end": v(6, 100) * mm});
            skLineSegment(sketch, "E8.5.0.1", {"start": v(10, 96) * mm, "end": v(6, 96) * mm});
            skLineSegment(sketch, "E8.5.0.2", {"start": v(10, 100) * mm, "end": v(10, 96) * mm});
            skLineSegment(sketch, "E8.5.0.3", {"start": v(6, 100) * mm, "end": v(6, 96) * mm});
            skLineSegment(sketch, "E8.5.1.0", {"start": v(10, 92) * mm, "end": v(6, 92) * mm});
            skLineSegment(sketch, "E8.5.1.1", {"start": v(10, 88) * mm, "end": v(6, 88) * mm});
            skLineSegment(sketch, "E8.5.1.2", {"start": v(10, 92) * mm, "end": v(10, 88) * mm});
            skLineSegment(sketch, "E8.5.1.3", {"start": v(6, 92) * mm, "end": v(6, 88) * mm});
            skLineSegment(sketch, "E8.5.2.0", {"start": v(10, 84) * mm, "end": v(6, 84) * mm});
            skLineSegment(sketch, "E8.5.2.1", {"start": v(10, 80) * mm, "end": v(6, 80) * mm});
            skLineSegment(sketch, "E8.5.2.2", {"start": v(10, 84) * mm, "end": v(10, 80) * mm});
            skLineSegment(sketch, "E8.5.2.3", {"start": v(6, 84) * mm, "end": v(6, 80) * mm});
            skLineSegment(sketch, "E8.5.3.0", {"start": v(10, 76) * mm, "end": v(6, 76) * mm});
            skLineSegment(sketch, "E8.5.3.1", {"start": v(10, 72) * mm, "end": v(6, 72) * mm});
            skLineSegment(sketch, "E8.5.3.2", {"start": v(10, 76) * mm, "end": v(10, 72) * mm});
            skLineSegment(sketch, "E8.5.3.3", {"start": v(6, 76) * mm, "end": v(6, 72) * mm});
            skLineSegment(sketch, "E8.5.4.0", {"start": v(10, 68) * mm, "end": v(6, 68) * mm});
            skLineSegment(sketch, "E8.5.4.1", {"start": v(10, 64) * mm, "end": v(6, 64) * mm});
            skLineSegment(sketch, "E8.5.4.2", {"start": v(10, 68) * mm, "end": v(10, 64) * mm});
            skLineSegment(sketch, "E8.5.4.3", {"start": v(6, 68) * mm, "end": v(6, 64) * mm});
            skLineSegment(sketch, "E8.5.5.0", {"start": v(10, 60) * mm, "end": v(6, 60) * mm});
            skLineSegment(sketch, "E8.5.5.1", {"start": v(10, 56) * mm, "end": v(6, 56) * mm});
            skLineSegment(sketch, "E8.5.5.2", {"start": v(10, 60) * mm, "end": v(10, 56) * mm});
            skLineSegment(sketch, "E8.5.5.3", {"start": v(6, 60) * mm, "end": v(6, 56) * mm});
            skLineSegment(sketch, "E8.5.6.0", {"start": v(10, 52) * mm, "end": v(6, 52) * mm});
            skLineSegment(sketch, "E8.5.6.1", {"start": v(10, 48) * mm, "end": v(6, 48) * mm});
            skLineSegment(sketch, "E8.5.6.2", {"start": v(10, 52) * mm, "end": v(10, 48) * mm});
            skLineSegment(sketch, "E8.5.6.3", {"start": v(6, 52) * mm, "end": v(6, 48) * mm});
            skLineSegment(sketch, "E8.5.7.0", {"start": v(10, 44) * mm, "end": v(6, 44) * mm});
            skLineSegment(sketch, "E8.5.7.1", {"start": v(10, 40) * mm, "end": v(6, 40) * mm});
            skLineSegment(sketch, "E8.5.7.2", {"start": v(10, 44) * mm, "end": v(10, 40) * mm});
            skLineSegment(sketch, "E8.5.7.3", {"start": v(6, 44) * mm, "end": v(6, 40) * mm});
            skLineSegment(sketch, "E8.5.8.0", {"start": v(10, 36) * mm, "end": v(6, 36) * mm});
            skLineSegment(sketch, "E8.5.8.1", {"start": v(10, 32) * mm, "end": v(6, 32) * mm});
            skLineSegment(sketch, "E8.5.8.2", {"start": v(10, 36) * mm, "end": v(10, 32) * mm});
            skLineSegment(sketch, "E8.5.8.3", {"start": v(6, 36) * mm, "end": v(6, 32) * mm});
            skLineSegment(sketch, "E8.5.9.0", {"start": v(10, 28) * mm, "end": v(6, 28) * mm});
            skLineSegment(sketch, "E8.5.9.1", {"start": v(10, 24) * mm, "end": v(6, 24) * mm});
            skLineSegment(sketch, "E8.5.9.2", {"start": v(10, 28) * mm, "end": v(10, 24) * mm});
            skLineSegment(sketch, "E8.5.9.3", {"start": v(6, 28) * mm, "end": v(6, 24) * mm});
            skLineSegment(sketch, "E8.5.10.0", {"start": v(10, 20) * mm, "end": v(6, 20) * mm});
            skLineSegment(sketch, "E8.5.10.1", {"start": v(10, 16) * mm, "end": v(6, 16) * mm});
            skLineSegment(sketch, "E8.5.10.2", {"start": v(10, 20) * mm, "end": v(10, 16) * mm});
            skLineSegment(sketch, "E8.5.10.3", {"start": v(6, 20) * mm, "end": v(6, 16) * mm});
            skLineSegment(sketch, "E8.5.11.0", {"start": v(10, 12) * mm, "end": v(6, 12) * mm});
            skLineSegment(sketch, "E8.5.11.1", {"start": v(10, 8) * mm, "end": v(6, 8) * mm});
            skLineSegment(sketch, "E8.5.11.2", {"start": v(10, 12) * mm, "end": v(10, 8) * mm});
            skLineSegment(sketch, "E8.5.11.3", {"start": v(6, 12) * mm, "end": v(6, 8) * mm});
            skLineSegment(sketch, "E8.5.12.0", {"start": v(10, 4) * mm, "end": v(6, 4) * mm});
            skLineSegment(sketch, "E8.5.12.1", {"start": v(10, 0) * mm, "end": v(6, 0) * mm});
            skLineSegment(sketch, "E8.5.12.2", {"start": v(10, 4) * mm, "end": v(10, 0) * mm});
            skLineSegment(sketch, "E8.5.12.3", {"start": v(6, 4) * mm, "end": v(6, 0) * mm});
            skLineSegment(sketch, "E8.6.0.0", {"start": v(2, 100) * mm, "end": v(-2, 100) * mm});
            skLineSegment(sketch, "E8.6.0.1", {"start": v(2, 96) * mm, "end": v(-2, 96) * mm});
            skLineSegment(sketch, "E8.6.0.2", {"start": v(2, 100) * mm, "end": v(2, 96) * mm});
            skLineSegment(sketch, "E8.6.0.3", {"start": v(-2, 100) * mm, "end": v(-2, 96) * mm});
            skLineSegment(sketch, "E8.6.1.0", {"start": v(2, 92) * mm, "end": v(-2, 92) * mm});
            skLineSegment(sketch, "E8.6.1.1", {"start": v(2, 88) * mm, "end": v(-2, 88) * mm});
            skLineSegment(sketch, "E8.6.1.2", {"start": v(2, 92) * mm, "end": v(2, 88) * mm});
            skLineSegment(sketch, "E8.6.1.3", {"start": v(-2, 92) * mm, "end": v(-2, 88) * mm});
            skLineSegment(sketch, "E8.6.2.0", {"start": v(2, 84) * mm, "end": v(-2, 84) * mm});
            skLineSegment(sketch, "E8.6.2.1", {"start": v(2, 80) * mm, "end": v(-2, 80) * mm});
            skLineSegment(sketch, "E8.6.2.2", {"start": v(2, 84) * mm, "end": v(2, 80) * mm});
            skLineSegment(sketch, "E8.6.2.3", {"start": v(-2, 84) * mm, "end": v(-2, 80) * mm});
            skLineSegment(sketch, "E8.6.3.0", {"start": v(2, 76) * mm, "end": v(-2, 76) * mm});
            skLineSegment(sketch, "E8.6.3.1", {"start": v(2, 72) * mm, "end": v(-2, 72) * mm});
            skLineSegment(sketch, "E8.6.3.2", {"start": v(2, 76) * mm, "end": v(2, 72) * mm});
            skLineSegment(sketch, "E8.6.3.3", {"start": v(-2, 76) * mm, "end": v(-2, 72) * mm});
            skLineSegment(sketch, "E8.6.4.0", {"start": v(2, 68) * mm, "end": v(-2, 68) * mm});
            skLineSegment(sketch, "E8.6.4.1", {"start": v(2, 64) * mm, "end": v(-2, 64) * mm});
            skLineSegment(sketch, "E8.6.4.2", {"start": v(2, 68) * mm, "end": v(2, 64) * mm});
            skLineSegment(sketch, "E8.6.4.3", {"start": v(-2, 68) * mm, "end": v(-2, 64) * mm});
            skLineSegment(sketch, "E8.6.5.0", {"start": v(2, 60) * mm, "end": v(-2, 60) * mm});
            skLineSegment(sketch, "E8.6.5.1", {"start": v(2, 56) * mm, "end": v(-2, 56) * mm});
            skLineSegment(sketch, "E8.6.5.2", {"start": v(2, 60) * mm, "end": v(2, 56) * mm});
            skLineSegment(sketch, "E8.6.5.3", {"start": v(-2, 60) * mm, "end": v(-2, 56) * mm});
            skLineSegment(sketch, "E8.6.6.0", {"start": v(2, 52) * mm, "end": v(-2, 52) * mm});
            skLineSegment(sketch, "E8.6.6.1", {"start": v(2, 48) * mm, "end": v(-2, 48) * mm});
            skLineSegment(sketch, "E8.6.6.2", {"start": v(2, 52) * mm, "end": v(2, 48) * mm});
            skLineSegment(sketch, "E8.6.6.3", {"start": v(-2, 52) * mm, "end": v(-2, 48) * mm});
            skLineSegment(sketch, "E8.6.7.0", {"start": v(2, 44) * mm, "end": v(-2, 44) * mm});
            skLineSegment(sketch, "E8.6.7.1", {"start": v(2, 40) * mm, "end": v(-2, 40) * mm});
            skLineSegment(sketch, "E8.6.7.2", {"start": v(2, 44) * mm, "end": v(2, 40) * mm});
            skLineSegment(sketch, "E8.6.7.3", {"start": v(-2, 44) * mm, "end": v(-2, 40) * mm});
            skLineSegment(sketch, "E8.6.8.0", {"start": v(2, 36) * mm, "end": v(-2, 36) * mm});
            skLineSegment(sketch, "E8.6.8.1", {"start": v(2, 32) * mm, "end": v(-2, 32) * mm});
            skLineSegment(sketch, "E8.6.8.2", {"start": v(2, 36) * mm, "end": v(2, 32) * mm});
            skLineSegment(sketch, "E8.6.8.3", {"start": v(-2, 36) * mm, "end": v(-2, 32) * mm});
            skLineSegment(sketch, "E8.6.9.0", {"start": v(2, 28) * mm, "end": v(-2, 28) * mm});
            skLineSegment(sketch, "E8.6.9.1", {"start": v(2, 24) * mm, "end": v(-2, 24) * mm});
            skLineSegment(sketch, "E8.6.9.2", {"start": v(2, 28) * mm, "end": v(2, 24) * mm});
            skLineSegment(sketch, "E8.6.9.3", {"start": v(-2, 28) * mm, "end": v(-2, 24) * mm});
            skLineSegment(sketch, "E8.6.10.0", {"start": v(2, 20) * mm, "end": v(-2, 20) * mm});
            skLineSegment(sketch, "E8.6.10.1", {"start": v(2, 16) * mm, "end": v(-2, 16) * mm});
            skLineSegment(sketch, "E8.6.10.2", {"start": v(2, 20) * mm, "end": v(2, 16) * mm});
            skLineSegment(sketch, "E8.6.10.3", {"start": v(-2, 20) * mm, "end": v(-2, 16) * mm});
            skLineSegment(sketch, "E8.6.11.0", {"start": v(2, 12) * mm, "end": v(-2, 12) * mm});
            skLineSegment(sketch, "E8.6.11.1", {"start": v(2, 8) * mm, "end": v(-2, 8) * mm});
            skLineSegment(sketch, "E8.6.11.2", {"start": v(2, 12) * mm, "end": v(2, 8) * mm});
            skLineSegment(sketch, "E8.6.11.3", {"start": v(-2, 12) * mm, "end": v(-2, 8) * mm});
            skLineSegment(sketch, "E8.6.12.0", {"start": v(2, 4) * mm, "end": v(-2, 4) * mm});
            skLineSegment(sketch, "E8.6.12.1", {"start": v(2, 0) * mm, "end": v(-2, 0) * mm});
            skLineSegment(sketch, "E8.6.12.2", {"start": v(2, 4) * mm, "end": v(2, 0) * mm});
            skLineSegment(sketch, "E8.6.12.3", {"start": v(-2, 4) * mm, "end": v(-2, 0) * mm});
            skLineSegment(sketch, "E8.7.0.0", {"start": v(-6, 100) * mm, "end": v(-10, 100) * mm});
            skLineSegment(sketch, "E8.7.0.1", {"start": v(-6, 96) * mm, "end": v(-10, 96) * mm});
            skLineSegment(sketch, "E8.7.0.2", {"start": v(-6, 100) * mm, "end": v(-6, 96) * mm});
            skLineSegment(sketch, "E8.7.0.3", {"start": v(-10, 100) * mm, "end": v(-10, 96) * mm});
            skLineSegment(sketch, "E8.7.1.0", {"start": v(-6, 92) * mm, "end": v(-10, 92) * mm});
            skLineSegment(sketch, "E8.7.1.1", {"start": v(-6, 88) * mm, "end": v(-10, 88) * mm});
            skLineSegment(sketch, "E8.7.1.2", {"start": v(-6, 92) * mm, "end": v(-6, 88) * mm});
            skLineSegment(sketch, "E8.7.1.3", {"start": v(-10, 92) * mm, "end": v(-10, 88) * mm});
            skLineSegment(sketch, "E8.7.2.0", {"start": v(-6, 84) * mm, "end": v(-10, 84) * mm});
            skLineSegment(sketch, "E8.7.2.1", {"start": v(-6, 80) * mm, "end": v(-10, 80) * mm});
            skLineSegment(sketch, "E8.7.2.2", {"start": v(-6, 84) * mm, "end": v(-6, 80) * mm});
            skLineSegment(sketch, "E8.7.2.3", {"start": v(-10, 84) * mm, "end": v(-10, 80) * mm});
            skLineSegment(sketch, "E8.7.3.0", {"start": v(-6, 76) * mm, "end": v(-10, 76) * mm});
            skLineSegment(sketch, "E8.7.3.1", {"start": v(-6, 72) * mm, "end": v(-10, 72) * mm});
            skLineSegment(sketch, "E8.7.3.2", {"start": v(-6, 76) * mm, "end": v(-6, 72) * mm});
            skLineSegment(sketch, "E8.7.3.3", {"start": v(-10, 76) * mm, "end": v(-10, 72) * mm});
            skLineSegment(sketch, "E8.7.4.0", {"start": v(-6, 68) * mm, "end": v(-10, 68) * mm});
            skLineSegment(sketch, "E8.7.4.1", {"start": v(-6, 64) * mm, "end": v(-10, 64) * mm});
            skLineSegment(sketch, "E8.7.4.2", {"start": v(-6, 68) * mm, "end": v(-6, 64) * mm});
            skLineSegment(sketch, "E8.7.4.3", {"start": v(-10, 68) * mm, "end": v(-10, 64) * mm});
            skLineSegment(sketch, "E8.7.5.0", {"start": v(-6, 60) * mm, "end": v(-10, 60) * mm});
            skLineSegment(sketch, "E8.7.5.1", {"start": v(-6, 56) * mm, "end": v(-10, 56) * mm});
            skLineSegment(sketch, "E8.7.5.2", {"start": v(-6, 60) * mm, "end": v(-6, 56) * mm});
            skLineSegment(sketch, "E8.7.5.3", {"start": v(-10, 60) * mm, "end": v(-10, 56) * mm});
            skLineSegment(sketch, "E8.7.6.0", {"start": v(-6, 52) * mm, "end": v(-10, 52) * mm});
            skLineSegment(sketch, "E8.7.6.1", {"start": v(-6, 48) * mm, "end": v(-10, 48) * mm});
            skLineSegment(sketch, "E8.7.6.2", {"start": v(-6, 52) * mm, "end": v(-6, 48) * mm});
            skLineSegment(sketch, "E8.7.6.3", {"start": v(-10, 52) * mm, "end": v(-10, 48) * mm});
            skLineSegment(sketch, "E8.7.7.0", {"start": v(-6, 44) * mm, "end": v(-10, 44) * mm});
            skLineSegment(sketch, "E8.7.7.1", {"start": v(-6, 40) * mm, "end": v(-10, 40) * mm});
            skLineSegment(sketch, "E8.7.7.2", {"start": v(-6, 44) * mm, "end": v(-6, 40) * mm});
            skLineSegment(sketch, "E8.7.7.3", {"start": v(-10, 44) * mm, "end": v(-10, 40) * mm});
            skLineSegment(sketch, "E8.7.8.0", {"start": v(-6, 36) * mm, "end": v(-10, 36) * mm});
            skLineSegment(sketch, "E8.7.8.1", {"start": v(-6, 32) * mm, "end": v(-10, 32) * mm});
            skLineSegment(sketch, "E8.7.8.2", {"start": v(-6, 36) * mm, "end": v(-6, 32) * mm});
            skLineSegment(sketch, "E8.7.8.3", {"start": v(-10, 36) * mm, "end": v(-10, 32) * mm});
            skLineSegment(sketch, "E8.7.9.0", {"start": v(-6, 28) * mm, "end": v(-10, 28) * mm});
            skLineSegment(sketch, "E8.7.9.1", {"start": v(-6, 24) * mm, "end": v(-10, 24) * mm});
            skLineSegment(sketch, "E8.7.9.2", {"start": v(-6, 28) * mm, "end": v(-6, 24) * mm});
            skLineSegment(sketch, "E8.7.9.3", {"start": v(-10, 28) * mm, "end": v(-10, 24) * mm});
            skLineSegment(sketch, "E8.7.10.0", {"start": v(-6, 20) * mm, "end": v(-10, 20) * mm});
            skLineSegment(sketch, "E8.7.10.1", {"start": v(-6, 16) * mm, "end": v(-10, 16) * mm});
            skLineSegment(sketch, "E8.7.10.2", {"start": v(-6, 20) * mm, "end": v(-6, 16) * mm});
            skLineSegment(sketch, "E8.7.10.3", {"start": v(-10, 20) * mm, "end": v(-10, 16) * mm});
            skLineSegment(sketch, "E8.7.11.0", {"start": v(-6, 12) * mm, "end": v(-10, 12) * mm});
            skLineSegment(sketch, "E8.7.11.1", {"start": v(-6, 8) * mm, "end": v(-10, 8) * mm});
            skLineSegment(sketch, "E8.7.11.2", {"start": v(-6, 12) * mm, "end": v(-6, 8) * mm});
            skLineSegment(sketch, "E8.7.11.3", {"start": v(-10, 12) * mm, "end": v(-10, 8) * mm});
            skLineSegment(sketch, "E8.7.12.0", {"start": v(-6, 4) * mm, "end": v(-10, 4) * mm});
            skLineSegment(sketch, "E8.7.12.1", {"start": v(-6, 0) * mm, "end": v(-10, 0) * mm});
            skLineSegment(sketch, "E8.7.12.2", {"start": v(-6, 4) * mm, "end": v(-6, 0) * mm});
            skLineSegment(sketch, "E8.7.12.3", {"start": v(-10, 4) * mm, "end": v(-10, 0) * mm});
            skLineSegment(sketch, "E8.8.0.0", {"start": v(-14, 100) * mm, "end": v(-18, 100) * mm});
            skLineSegment(sketch, "E8.8.0.1", {"start": v(-14, 96) * mm, "end": v(-18, 96) * mm});
            skLineSegment(sketch, "E8.8.0.2", {"start": v(-14, 100) * mm, "end": v(-14, 96) * mm});
            skLineSegment(sketch, "E8.8.0.3", {"start": v(-18, 100) * mm, "end": v(-18, 96) * mm});
            skLineSegment(sketch, "E8.8.1.0", {"start": v(-14, 92) * mm, "end": v(-18, 92) * mm});
            skLineSegment(sketch, "E8.8.1.1", {"start": v(-14, 88) * mm, "end": v(-18, 88) * mm});
            skLineSegment(sketch, "E8.8.1.2", {"start": v(-14, 92) * mm, "end": v(-14, 88) * mm});
            skLineSegment(sketch, "E8.8.1.3", {"start": v(-18, 92) * mm, "end": v(-18, 88) * mm});
            skLineSegment(sketch, "E8.8.2.0", {"start": v(-14, 84) * mm, "end": v(-18, 84) * mm});
            skLineSegment(sketch, "E8.8.2.1", {"start": v(-14, 80) * mm, "end": v(-18, 80) * mm});
            skLineSegment(sketch, "E8.8.2.2", {"start": v(-14, 84) * mm, "end": v(-14, 80) * mm});
            skLineSegment(sketch, "E8.8.2.3", {"start": v(-18, 84) * mm, "end": v(-18, 80) * mm});
            skLineSegment(sketch, "E8.8.3.0", {"start": v(-14, 76) * mm, "end": v(-18, 76) * mm});
            skLineSegment(sketch, "E8.8.3.1", {"start": v(-14, 72) * mm, "end": v(-18, 72) * mm});
            skLineSegment(sketch, "E8.8.3.2", {"start": v(-14, 76) * mm, "end": v(-14, 72) * mm});
            skLineSegment(sketch, "E8.8.3.3", {"start": v(-18, 76) * mm, "end": v(-18, 72) * mm});
            skLineSegment(sketch, "E8.8.4.0", {"start": v(-14, 68) * mm, "end": v(-18, 68) * mm});
            skLineSegment(sketch, "E8.8.4.1", {"start": v(-14, 64) * mm, "end": v(-18, 64) * mm});
            skLineSegment(sketch, "E8.8.4.2", {"start": v(-14, 68) * mm, "end": v(-14, 64) * mm});
            skLineSegment(sketch, "E8.8.4.3", {"start": v(-18, 68) * mm, "end": v(-18, 64) * mm});
            skLineSegment(sketch, "E8.8.5.0", {"start": v(-14, 60) * mm, "end": v(-18, 60) * mm});
            skLineSegment(sketch, "E8.8.5.1", {"start": v(-14, 56) * mm, "end": v(-18, 56) * mm});
            skLineSegment(sketch, "E8.8.5.2", {"start": v(-14, 60) * mm, "end": v(-14, 56) * mm});
            skLineSegment(sketch, "E8.8.5.3", {"start": v(-18, 60) * mm, "end": v(-18, 56) * mm});
            skLineSegment(sketch, "E8.8.6.0", {"start": v(-14, 52) * mm, "end": v(-18, 52) * mm});
            skLineSegment(sketch, "E8.8.6.1", {"start": v(-14, 48) * mm, "end": v(-18, 48) * mm});
            skLineSegment(sketch, "E8.8.6.2", {"start": v(-14, 52) * mm, "end": v(-14, 48) * mm});
            skLineSegment(sketch, "E8.8.6.3", {"start": v(-18, 52) * mm, "end": v(-18, 48) * mm});
            skLineSegment(sketch, "E8.8.7.0", {"start": v(-14, 44) * mm, "end": v(-18, 44) * mm});
            skLineSegment(sketch, "E8.8.7.1", {"start": v(-14, 40) * mm, "end": v(-18, 40) * mm});
            skLineSegment(sketch, "E8.8.7.2", {"start": v(-14, 44) * mm, "end": v(-14, 40) * mm});
            skLineSegment(sketch, "E8.8.7.3", {"start": v(-18, 44) * mm, "end": v(-18, 40) * mm});
            skLineSegment(sketch, "E8.8.8.0", {"start": v(-14, 36) * mm, "end": v(-18, 36) * mm});
            skLineSegment(sketch, "E8.8.8.1", {"start": v(-14, 32) * mm, "end": v(-18, 32) * mm});
            skLineSegment(sketch, "E8.8.8.2", {"start": v(-14, 36) * mm, "end": v(-14, 32) * mm});
            skLineSegment(sketch, "E8.8.8.3", {"start": v(-18, 36) * mm, "end": v(-18, 32) * mm});
            skLineSegment(sketch, "E8.8.9.0", {"start": v(-14, 28) * mm, "end": v(-18, 28) * mm});
            skLineSegment(sketch, "E8.8.9.1", {"start": v(-14, 24) * mm, "end": v(-18, 24) * mm});
            skLineSegment(sketch, "E8.8.9.2", {"start": v(-14, 28) * mm, "end": v(-14, 24) * mm});
            skLineSegment(sketch, "E8.8.9.3", {"start": v(-18, 28) * mm, "end": v(-18, 24) * mm});
            skLineSegment(sketch, "E8.8.10.0", {"start": v(-14, 20) * mm, "end": v(-18, 20) * mm});
            skLineSegment(sketch, "E8.8.10.1", {"start": v(-14, 16) * mm, "end": v(-18, 16) * mm});
            skLineSegment(sketch, "E8.8.10.2", {"start": v(-14, 20) * mm, "end": v(-14, 16) * mm});
            skLineSegment(sketch, "E8.8.10.3", {"start": v(-18, 20) * mm, "end": v(-18, 16) * mm});
            skLineSegment(sketch, "E8.8.11.0", {"start": v(-14, 12) * mm, "end": v(-18, 12) * mm});
            skLineSegment(sketch, "E8.8.11.1", {"start": v(-14, 8) * mm, "end": v(-18, 8) * mm});
            skLineSegment(sketch, "E8.8.11.2", {"start": v(-14, 12) * mm, "end": v(-14, 8) * mm});
            skLineSegment(sketch, "E8.8.11.3", {"start": v(-18, 12) * mm, "end": v(-18, 8) * mm});
            skLineSegment(sketch, "E8.8.12.0", {"start": v(-14, 4) * mm, "end": v(-18, 4) * mm});
            skLineSegment(sketch, "E8.8.12.1", {"start": v(-14, 0) * mm, "end": v(-18, 0) * mm});
            skLineSegment(sketch, "E8.8.12.2", {"start": v(-14, 4) * mm, "end": v(-14, 0) * mm});
            skLineSegment(sketch, "E8.8.12.3", {"start": v(-18, 4) * mm, "end": v(-18, 0) * mm});
            skLineSegment(sketch, "E8.9.0.0", {"start": v(-22, 100) * mm, "end": v(-26, 100) * mm});
            skLineSegment(sketch, "E8.9.0.1", {"start": v(-22, 96) * mm, "end": v(-26, 96) * mm});
            skLineSegment(sketch, "E8.9.0.2", {"start": v(-22, 100) * mm, "end": v(-22, 96) * mm});
            skLineSegment(sketch, "E8.9.0.3", {"start": v(-26, 100) * mm, "end": v(-26, 96) * mm});
            skLineSegment(sketch, "E8.9.1.0", {"start": v(-22, 92) * mm, "end": v(-26, 92) * mm});
            skLineSegment(sketch, "E8.9.1.1", {"start": v(-22, 88) * mm, "end": v(-26, 88) * mm});
            skLineSegment(sketch, "E8.9.1.2", {"start": v(-22, 92) * mm, "end": v(-22, 88) * mm});
            skLineSegment(sketch, "E8.9.1.3", {"start": v(-26, 92) * mm, "end": v(-26, 88) * mm});
            skLineSegment(sketch, "E8.9.2.0", {"start": v(-22, 84) * mm, "end": v(-26, 84) * mm});
            skLineSegment(sketch, "E8.9.2.1", {"start": v(-22, 80) * mm, "end": v(-26, 80) * mm});
            skLineSegment(sketch, "E8.9.2.2", {"start": v(-22, 84) * mm, "end": v(-22, 80) * mm});
            skLineSegment(sketch, "E8.9.2.3", {"start": v(-26, 84) * mm, "end": v(-26, 80) * mm});
            skLineSegment(sketch, "E8.9.3.0", {"start": v(-22, 76) * mm, "end": v(-26, 76) * mm});
            skLineSegment(sketch, "E8.9.3.1", {"start": v(-22, 72) * mm, "end": v(-26, 72) * mm});
            skLineSegment(sketch, "E8.9.3.2", {"start": v(-22, 76) * mm, "end": v(-22, 72) * mm});
            skLineSegment(sketch, "E8.9.3.3", {"start": v(-26, 76) * mm, "end": v(-26, 72) * mm});
            skLineSegment(sketch, "E8.9.4.0", {"start": v(-22, 68) * mm, "end": v(-26, 68) * mm});
            skLineSegment(sketch, "E8.9.4.1", {"start": v(-22, 64) * mm, "end": v(-26, 64) * mm});
            skLineSegment(sketch, "E8.9.4.2", {"start": v(-22, 68) * mm, "end": v(-22, 64) * mm});
            skLineSegment(sketch, "E8.9.4.3", {"start": v(-26, 68) * mm, "end": v(-26, 64) * mm});
            skLineSegment(sketch, "E8.9.5.0", {"start": v(-22, 60) * mm, "end": v(-26, 60) * mm});
            skLineSegment(sketch, "E8.9.5.1", {"start": v(-22, 56) * mm, "end": v(-26, 56) * mm});
            skLineSegment(sketch, "E8.9.5.2", {"start": v(-22, 60) * mm, "end": v(-22, 56) * mm});
            skLineSegment(sketch, "E8.9.5.3", {"start": v(-26, 60) * mm, "end": v(-26, 56) * mm});
            skLineSegment(sketch, "E8.9.6.0", {"start": v(-22, 52) * mm, "end": v(-26, 52) * mm});
            skLineSegment(sketch, "E8.9.6.1", {"start": v(-22, 48) * mm, "end": v(-26, 48) * mm});
            skLineSegment(sketch, "E8.9.6.2", {"start": v(-22, 52) * mm, "end": v(-22, 48) * mm});
            skLineSegment(sketch, "E8.9.6.3", {"start": v(-26, 52) * mm, "end": v(-26, 48) * mm});
            skLineSegment(sketch, "E8.9.7.0", {"start": v(-22, 44) * mm, "end": v(-26, 44) * mm});
            skLineSegment(sketch, "E8.9.7.1", {"start": v(-22, 40) * mm, "end": v(-26, 40) * mm});
            skLineSegment(sketch, "E8.9.7.2", {"start": v(-22, 44) * mm, "end": v(-22, 40) * mm});
            skLineSegment(sketch, "E8.9.7.3", {"start": v(-26, 44) * mm, "end": v(-26, 40) * mm});
            skLineSegment(sketch, "E8.9.8.0", {"start": v(-22, 36) * mm, "end": v(-26, 36) * mm});
            skLineSegment(sketch, "E8.9.8.1", {"start": v(-22, 32) * mm, "end": v(-26, 32) * mm});
            skLineSegment(sketch, "E8.9.8.2", {"start": v(-22, 36) * mm, "end": v(-22, 32) * mm});
            skLineSegment(sketch, "E8.9.8.3", {"start": v(-26, 36) * mm, "end": v(-26, 32) * mm});
            skLineSegment(sketch, "E8.9.9.0", {"start": v(-22, 28) * mm, "end": v(-26, 28) * mm});
            skLineSegment(sketch, "E8.9.9.1", {"start": v(-22, 24) * mm, "end": v(-26, 24) * mm});
            skLineSegment(sketch, "E8.9.9.2", {"start": v(-22, 28) * mm, "end": v(-22, 24) * mm});
            skLineSegment(sketch, "E8.9.9.3", {"start": v(-26, 28) * mm, "end": v(-26, 24) * mm});
            skLineSegment(sketch, "E8.9.10.0", {"start": v(-22, 20) * mm, "end": v(-26, 20) * mm});
            skLineSegment(sketch, "E8.9.10.1", {"start": v(-22, 16) * mm, "end": v(-26, 16) * mm});
            skLineSegment(sketch, "E8.9.10.2", {"start": v(-22, 20) * mm, "end": v(-22, 16) * mm});
            skLineSegment(sketch, "E8.9.10.3", {"start": v(-26, 20) * mm, "end": v(-26, 16) * mm});
            skLineSegment(sketch, "E8.9.11.0", {"start": v(-22, 12) * mm, "end": v(-26, 12) * mm});
            skLineSegment(sketch, "E8.9.11.1", {"start": v(-22, 8) * mm, "end": v(-26, 8) * mm});
            skLineSegment(sketch, "E8.9.11.2", {"start": v(-22, 12) * mm, "end": v(-22, 8) * mm});
            skLineSegment(sketch, "E8.9.11.3", {"start": v(-26, 12) * mm, "end": v(-26, 8) * mm});
            skLineSegment(sketch, "E8.9.12.0", {"start": v(-22, 4) * mm, "end": v(-26, 4) * mm});
            skLineSegment(sketch, "E8.9.12.1", {"start": v(-22, 0) * mm, "end": v(-26, 0) * mm});
            skLineSegment(sketch, "E8.9.12.2", {"start": v(-22, 4) * mm, "end": v(-22, 0) * mm});
            skLineSegment(sketch, "E8.9.12.3", {"start": v(-26, 4) * mm, "end": v(-26, 0) * mm});
            skLineSegment(sketch, "E8.10.0.0", {"start": v(-30, 100) * mm, "end": v(-34, 100) * mm});
            skLineSegment(sketch, "E8.10.0.1", {"start": v(-30, 96) * mm, "end": v(-34, 96) * mm});
            skLineSegment(sketch, "E8.10.0.2", {"start": v(-30, 100) * mm, "end": v(-30, 96) * mm});
            skLineSegment(sketch, "E8.10.0.3", {"start": v(-34, 100) * mm, "end": v(-34, 96) * mm});
            skLineSegment(sketch, "E8.10.1.0", {"start": v(-30, 92) * mm, "end": v(-34, 92) * mm});
            skLineSegment(sketch, "E8.10.1.1", {"start": v(-30, 88) * mm, "end": v(-34, 88) * mm});
            skLineSegment(sketch, "E8.10.1.2", {"start": v(-30, 92) * mm, "end": v(-30, 88) * mm});
            skLineSegment(sketch, "E8.10.1.3", {"start": v(-34, 92) * mm, "end": v(-34, 88) * mm});
            skLineSegment(sketch, "E8.10.2.0", {"start": v(-30, 84) * mm, "end": v(-34, 84) * mm});
            skLineSegment(sketch, "E8.10.2.1", {"start": v(-30, 80) * mm, "end": v(-34, 80) * mm});
            skLineSegment(sketch, "E8.10.2.2", {"start": v(-30, 84) * mm, "end": v(-30, 80) * mm});
            skLineSegment(sketch, "E8.10.2.3", {"start": v(-34, 84) * mm, "end": v(-34, 80) * mm});
            skLineSegment(sketch, "E8.10.3.0", {"start": v(-30, 76) * mm, "end": v(-34, 76) * mm});
            skLineSegment(sketch, "E8.10.3.1", {"start": v(-30, 72) * mm, "end": v(-34, 72) * mm});
            skLineSegment(sketch, "E8.10.3.2", {"start": v(-30, 76) * mm, "end": v(-30, 72) * mm});
            skLineSegment(sketch, "E8.10.3.3", {"start": v(-34, 76) * mm, "end": v(-34, 72) * mm});
            skLineSegment(sketch, "E8.10.4.0", {"start": v(-30, 68) * mm, "end": v(-34, 68) * mm});
            skLineSegment(sketch, "E8.10.4.1", {"start": v(-30, 64) * mm, "end": v(-34, 64) * mm});
            skLineSegment(sketch, "E8.10.4.2", {"start": v(-30, 68) * mm, "end": v(-30, 64) * mm});
            skLineSegment(sketch, "E8.10.4.3", {"start": v(-34, 68) * mm, "end": v(-34, 64) * mm});
            skLineSegment(sketch, "E8.10.5.0", {"start": v(-30, 60) * mm, "end": v(-34, 60) * mm});
            skLineSegment(sketch, "E8.10.5.1", {"start": v(-30, 56) * mm, "end": v(-34, 56) * mm});
            skLineSegment(sketch, "E8.10.5.2", {"start": v(-30, 60) * mm, "end": v(-30, 56) * mm});
            skLineSegment(sketch, "E8.10.5.3", {"start": v(-34, 60) * mm, "end": v(-34, 56) * mm});
            skLineSegment(sketch, "E8.10.6.0", {"start": v(-30, 52) * mm, "end": v(-34, 52) * mm});
            skLineSegment(sketch, "E8.10.6.1", {"start": v(-30, 48) * mm, "end": v(-34, 48) * mm});
            skLineSegment(sketch, "E8.10.6.2", {"start": v(-30, 52) * mm, "end": v(-30, 48) * mm});
            skLineSegment(sketch, "E8.10.6.3", {"start": v(-34, 52) * mm, "end": v(-34, 48) * mm});
            skLineSegment(sketch, "E8.10.7.0", {"start": v(-30, 44) * mm, "end": v(-34, 44) * mm});
            skLineSegment(sketch, "E8.10.7.1", {"start": v(-30, 40) * mm, "end": v(-34, 40) * mm});
            skLineSegment(sketch, "E8.10.7.2", {"start": v(-30, 44) * mm, "end": v(-30, 40) * mm});
            skLineSegment(sketch, "E8.10.7.3", {"start": v(-34, 44) * mm, "end": v(-34, 40) * mm});
            skLineSegment(sketch, "E8.10.8.0", {"start": v(-30, 36) * mm, "end": v(-34, 36) * mm});
            skLineSegment(sketch, "E8.10.8.1", {"start": v(-30, 32) * mm, "end": v(-34, 32) * mm});
            skLineSegment(sketch, "E8.10.8.2", {"start": v(-30, 36) * mm, "end": v(-30, 32) * mm});
            skLineSegment(sketch, "E8.10.8.3", {"start": v(-34, 36) * mm, "end": v(-34, 32) * mm});
            skLineSegment(sketch, "E8.10.9.0", {"start": v(-30, 28) * mm, "end": v(-34, 28) * mm});
            skLineSegment(sketch, "E8.10.9.1", {"start": v(-30, 24) * mm, "end": v(-34, 24) * mm});
            skLineSegment(sketch, "E8.10.9.2", {"start": v(-30, 28) * mm, "end": v(-30, 24) * mm});
            skLineSegment(sketch, "E8.10.9.3", {"start": v(-34, 28) * mm, "end": v(-34, 24) * mm});
            skLineSegment(sketch, "E8.10.10.0", {"start": v(-30, 20) * mm, "end": v(-34, 20) * mm});
            skLineSegment(sketch, "E8.10.10.1", {"start": v(-30, 16) * mm, "end": v(-34, 16) * mm});
            skLineSegment(sketch, "E8.10.10.2", {"start": v(-30, 20) * mm, "end": v(-30, 16) * mm});
            skLineSegment(sketch, "E8.10.10.3", {"start": v(-34, 20) * mm, "end": v(-34, 16) * mm});
            skLineSegment(sketch, "E8.10.11.0", {"start": v(-30, 12) * mm, "end": v(-34, 12) * mm});
            skLineSegment(sketch, "E8.10.11.1", {"start": v(-30, 8) * mm, "end": v(-34, 8) * mm});
            skLineSegment(sketch, "E8.10.11.2", {"start": v(-30, 12) * mm, "end": v(-30, 8) * mm});
            skLineSegment(sketch, "E8.10.11.3", {"start": v(-34, 12) * mm, "end": v(-34, 8) * mm});
            skLineSegment(sketch, "E8.10.12.0", {"start": v(-30, 4) * mm, "end": v(-34, 4) * mm});
            skLineSegment(sketch, "E8.10.12.1", {"start": v(-30, 0) * mm, "end": v(-34, 0) * mm});
            skLineSegment(sketch, "E8.10.12.2", {"start": v(-30, 4) * mm, "end": v(-30, 0) * mm});
            skLineSegment(sketch, "E8.10.12.3", {"start": v(-34, 4) * mm, "end": v(-34, 0) * mm});
            skLineSegment(sketch, "E8.11.0.0", {"start": v(-38, 100) * mm, "end": v(-42, 100) * mm});
            skLineSegment(sketch, "E8.11.0.1", {"start": v(-38, 96) * mm, "end": v(-42, 96) * mm});
            skLineSegment(sketch, "E8.11.0.2", {"start": v(-38, 100) * mm, "end": v(-38, 96) * mm});
            skLineSegment(sketch, "E8.11.0.3", {"start": v(-42, 100) * mm, "end": v(-42, 96) * mm});
            skLineSegment(sketch, "E8.11.1.0", {"start": v(-38, 92) * mm, "end": v(-42, 92) * mm});
            skLineSegment(sketch, "E8.11.1.1", {"start": v(-38, 88) * mm, "end": v(-42, 88) * mm});
            skLineSegment(sketch, "E8.11.1.2", {"start": v(-38, 92) * mm, "end": v(-38, 88) * mm});
            skLineSegment(sketch, "E8.11.1.3", {"start": v(-42, 92) * mm, "end": v(-42, 88) * mm});
            skLineSegment(sketch, "E8.11.2.0", {"start": v(-38, 84) * mm, "end": v(-42, 84) * mm});
            skLineSegment(sketch, "E8.11.2.1", {"start": v(-38, 80) * mm, "end": v(-42, 80) * mm});
            skLineSegment(sketch, "E8.11.2.2", {"start": v(-38, 84) * mm, "end": v(-38, 80) * mm});
            skLineSegment(sketch, "E8.11.2.3", {"start": v(-42, 84) * mm, "end": v(-42, 80) * mm});
            skLineSegment(sketch, "E8.11.3.0", {"start": v(-38, 76) * mm, "end": v(-42, 76) * mm});
            skLineSegment(sketch, "E8.11.3.1", {"start": v(-38, 72) * mm, "end": v(-42, 72) * mm});
            skLineSegment(sketch, "E8.11.3.2", {"start": v(-38, 76) * mm, "end": v(-38, 72) * mm});
            skLineSegment(sketch, "E8.11.3.3", {"start": v(-42, 76) * mm, "end": v(-42, 72) * mm});
            skLineSegment(sketch, "E8.11.4.0", {"start": v(-38, 68) * mm, "end": v(-42, 68) * mm});
            skLineSegment(sketch, "E8.11.4.1", {"start": v(-38, 64) * mm, "end": v(-42, 64) * mm});
            skLineSegment(sketch, "E8.11.4.2", {"start": v(-38, 68) * mm, "end": v(-38, 64) * mm});
            skLineSegment(sketch, "E8.11.4.3", {"start": v(-42, 68) * mm, "end": v(-42, 64) * mm});
            skLineSegment(sketch, "E8.11.5.0", {"start": v(-38, 60) * mm, "end": v(-42, 60) * mm});
            skLineSegment(sketch, "E8.11.5.1", {"start": v(-38, 56) * mm, "end": v(-42, 56) * mm});
            skLineSegment(sketch, "E8.11.5.2", {"start": v(-38, 60) * mm, "end": v(-38, 56) * mm});
            skLineSegment(sketch, "E8.11.5.3", {"start": v(-42, 60) * mm, "end": v(-42, 56) * mm});
            skLineSegment(sketch, "E8.11.6.0", {"start": v(-38, 52) * mm, "end": v(-42, 52) * mm});
            skLineSegment(sketch, "E8.11.6.1", {"start": v(-38, 48) * mm, "end": v(-42, 48) * mm});
            skLineSegment(sketch, "E8.11.6.2", {"start": v(-38, 52) * mm, "end": v(-38, 48) * mm});
            skLineSegment(sketch, "E8.11.6.3", {"start": v(-42, 52) * mm, "end": v(-42, 48) * mm});
            skLineSegment(sketch, "E8.11.7.0", {"start": v(-38, 44) * mm, "end": v(-42, 44) * mm});
            skLineSegment(sketch, "E8.11.7.1", {"start": v(-38, 40) * mm, "end": v(-42, 40) * mm});
            skLineSegment(sketch, "E8.11.7.2", {"start": v(-38, 44) * mm, "end": v(-38, 40) * mm});
            skLineSegment(sketch, "E8.11.7.3", {"start": v(-42, 44) * mm, "end": v(-42, 40) * mm});
            skLineSegment(sketch, "E8.11.8.0", {"start": v(-38, 36) * mm, "end": v(-42, 36) * mm});
            skLineSegment(sketch, "E8.11.8.1", {"start": v(-38, 32) * mm, "end": v(-42, 32) * mm});
            skLineSegment(sketch, "E8.11.8.2", {"start": v(-38, 36) * mm, "end": v(-38, 32) * mm});
            skLineSegment(sketch, "E8.11.8.3", {"start": v(-42, 36) * mm, "end": v(-42, 32) * mm});
            skLineSegment(sketch, "E8.11.9.0", {"start": v(-38, 28) * mm, "end": v(-42, 28) * mm});
            skLineSegment(sketch, "E8.11.9.1", {"start": v(-38, 24) * mm, "end": v(-42, 24) * mm});
            skLineSegment(sketch, "E8.11.9.2", {"start": v(-38, 28) * mm, "end": v(-38, 24) * mm});
            skLineSegment(sketch, "E8.11.9.3", {"start": v(-42, 28) * mm, "end": v(-42, 24) * mm});
            skLineSegment(sketch, "E8.11.10.0", {"start": v(-38, 20) * mm, "end": v(-42, 20) * mm});
            skLineSegment(sketch, "E8.11.10.1", {"start": v(-38, 16) * mm, "end": v(-42, 16) * mm});
            skLineSegment(sketch, "E8.11.10.2", {"start": v(-38, 20) * mm, "end": v(-38, 16) * mm});
            skLineSegment(sketch, "E8.11.10.3", {"start": v(-42, 20) * mm, "end": v(-42, 16) * mm});
            skLineSegment(sketch, "E8.11.11.0", {"start": v(-38, 12) * mm, "end": v(-42, 12) * mm});
            skLineSegment(sketch, "E8.11.11.1", {"start": v(-38, 8) * mm, "end": v(-42, 8) * mm});
            skLineSegment(sketch, "E8.11.11.2", {"start": v(-38, 12) * mm, "end": v(-38, 8) * mm});
            skLineSegment(sketch, "E8.11.11.3", {"start": v(-42, 12) * mm, "end": v(-42, 8) * mm});
            skLineSegment(sketch, "E8.11.12.0", {"start": v(-38, 4) * mm, "end": v(-42, 4) * mm});
            skLineSegment(sketch, "E8.11.12.1", {"start": v(-38, 0) * mm, "end": v(-42, 0) * mm});
            skLineSegment(sketch, "E8.11.12.2", {"start": v(-38, 4) * mm, "end": v(-38, 0) * mm});
            skLineSegment(sketch, "E8.11.12.3", {"start": v(-42, 4) * mm, "end": v(-42, 0) * mm});
            skLineSegment(sketch, "E8.12.0.0", {"start": v(-46, 100) * mm, "end": v(-50, 100) * mm});
            skLineSegment(sketch, "E8.12.0.1", {"start": v(-46, 96) * mm, "end": v(-50, 96) * mm});
            skLineSegment(sketch, "E8.12.0.2", {"start": v(-46, 100) * mm, "end": v(-46, 96) * mm});
            skLineSegment(sketch, "E8.12.0.3", {"start": v(-50, 100) * mm, "end": v(-50, 96) * mm});
            skLineSegment(sketch, "E8.12.1.0", {"start": v(-46, 92) * mm, "end": v(-50, 92) * mm});
            skLineSegment(sketch, "E8.12.1.1", {"start": v(-46, 88) * mm, "end": v(-50, 88) * mm});
            skLineSegment(sketch, "E8.12.1.2", {"start": v(-46, 92) * mm, "end": v(-46, 88) * mm});
            skLineSegment(sketch, "E8.12.1.3", {"start": v(-50, 92) * mm, "end": v(-50, 88) * mm});
            skLineSegment(sketch, "E8.12.2.0", {"start": v(-46, 84) * mm, "end": v(-50, 84) * mm});
            skLineSegment(sketch, "E8.12.2.1", {"start": v(-46, 80) * mm, "end": v(-50, 80) * mm});
            skLineSegment(sketch, "E8.12.2.2", {"start": v(-46, 84) * mm, "end": v(-46, 80) * mm});
            skLineSegment(sketch, "E8.12.2.3", {"start": v(-50, 84) * mm, "end": v(-50, 80) * mm});
            skLineSegment(sketch, "E8.12.3.0", {"start": v(-46, 76) * mm, "end": v(-50, 76) * mm});
            skLineSegment(sketch, "E8.12.3.1", {"start": v(-46, 72) * mm, "end": v(-50, 72) * mm});
            skLineSegment(sketch, "E8.12.3.2", {"start": v(-46, 76) * mm, "end": v(-46, 72) * mm});
            skLineSegment(sketch, "E8.12.3.3", {"start": v(-50, 76) * mm, "end": v(-50, 72) * mm});
            skLineSegment(sketch, "E8.12.4.0", {"start": v(-46, 68) * mm, "end": v(-50, 68) * mm});
            skLineSegment(sketch, "E8.12.4.1", {"start": v(-46, 64) * mm, "end": v(-50, 64) * mm});
            skLineSegment(sketch, "E8.12.4.2", {"start": v(-46, 68) * mm, "end": v(-46, 64) * mm});
            skLineSegment(sketch, "E8.12.4.3", {"start": v(-50, 68) * mm, "end": v(-50, 64) * mm});
            skLineSegment(sketch, "E8.12.5.0", {"start": v(-46, 60) * mm, "end": v(-50, 60) * mm});
            skLineSegment(sketch, "E8.12.5.1", {"start": v(-46, 56) * mm, "end": v(-50, 56) * mm});
            skLineSegment(sketch, "E8.12.5.2", {"start": v(-46, 60) * mm, "end": v(-46, 56) * mm});
            skLineSegment(sketch, "E8.12.5.3", {"start": v(-50, 60) * mm, "end": v(-50, 56) * mm});
            skLineSegment(sketch, "E8.12.6.0", {"start": v(-46, 52) * mm, "end": v(-50, 52) * mm});
            skLineSegment(sketch, "E8.12.6.1", {"start": v(-46, 48) * mm, "end": v(-50, 48) * mm});
            skLineSegment(sketch, "E8.12.6.2", {"start": v(-46, 52) * mm, "end": v(-46, 48) * mm});
            skLineSegment(sketch, "E8.12.6.3", {"start": v(-50, 52) * mm, "end": v(-50, 48) * mm});
            skLineSegment(sketch, "E8.12.7.0", {"start": v(-46, 44) * mm, "end": v(-50, 44) * mm});
            skLineSegment(sketch, "E8.12.7.1", {"start": v(-46, 40) * mm, "end": v(-50, 40) * mm});
            skLineSegment(sketch, "E8.12.7.2", {"start": v(-46, 44) * mm, "end": v(-46, 40) * mm});
            skLineSegment(sketch, "E8.12.7.3", {"start": v(-50, 44) * mm, "end": v(-50, 40) * mm});
            skLineSegment(sketch, "E8.12.8.0", {"start": v(-46, 36) * mm, "end": v(-50, 36) * mm});
            skLineSegment(sketch, "E8.12.8.1", {"start": v(-46, 32) * mm, "end": v(-50, 32) * mm});
            skLineSegment(sketch, "E8.12.8.2", {"start": v(-46, 36) * mm, "end": v(-46, 32) * mm});
            skLineSegment(sketch, "E8.12.8.3", {"start": v(-50, 36) * mm, "end": v(-50, 32) * mm});
            skLineSegment(sketch, "E8.12.9.0", {"start": v(-46, 28) * mm, "end": v(-50, 28) * mm});
            skLineSegment(sketch, "E8.12.9.1", {"start": v(-46, 24) * mm, "end": v(-50, 24) * mm});
            skLineSegment(sketch, "E8.12.9.2", {"start": v(-46, 28) * mm, "end": v(-46, 24) * mm});
            skLineSegment(sketch, "E8.12.9.3", {"start": v(-50, 28) * mm, "end": v(-50, 24) * mm});
            skLineSegment(sketch, "E8.12.10.0", {"start": v(-46, 20) * mm, "end": v(-50, 20) * mm});
            skLineSegment(sketch, "E8.12.10.1", {"start": v(-46, 16) * mm, "end": v(-50, 16) * mm});
            skLineSegment(sketch, "E8.12.10.2", {"start": v(-46, 20) * mm, "end": v(-46, 16) * mm});
            skLineSegment(sketch, "E8.12.10.3", {"start": v(-50, 20) * mm, "end": v(-50, 16) * mm});
            skLineSegment(sketch, "E8.12.11.0", {"start": v(-46, 12) * mm, "end": v(-50, 12) * mm});
            skLineSegment(sketch, "E8.12.11.1", {"start": v(-46, 8) * mm, "end": v(-50, 8) * mm});
            skLineSegment(sketch, "E8.12.11.2", {"start": v(-46, 12) * mm, "end": v(-46, 8) * mm});
            skLineSegment(sketch, "E8.12.11.3", {"start": v(-50, 12) * mm, "end": v(-50, 8) * mm});
            skLineSegment(sketch, "E8.12.12.0", {"start": v(-46, 4) * mm, "end": v(-50, 4) * mm});
            skLineSegment(sketch, "E8.12.12.1", {"start": v(-46, 0) * mm, "end": v(-50, 0) * mm});
            skLineSegment(sketch, "E8.12.12.2", {"start": v(-46, 4) * mm, "end": v(-46, 0) * mm});
            skLineSegment(sketch, "E8.12.12.3", {"start": v(-50, 4) * mm, "end": v(-50, 0) * mm});
            skLineSegment(sketch, "E8.direction1", {"start": v(46, 100) * mm, "end": v(38, 100) * mm, "construction": true});
            skLineSegment(sketch, "E8.direction2", {"start": v(46, 100) * mm, "end": v(46, 92) * mm, "construction": true});
            skLineSegment(sketch, "E9.bottom", {"start": v(-50, 100) * mm, "end": v(50, 100) * mm});
            skLineSegment(sketch, "E9.top", {"start": v(-50, 0) * mm, "end": v(50, 0) * mm});
            skLineSegment(sketch, "E9.left", {"start": v(-50, 100) * mm, "end": v(-50, 0) * mm});
            skLineSegment(sketch, "E9.right", {"start": v(50, 100) * mm, "end": v(50, 0) * mm});
            skLineSegment(sketch, "E10.bottom", {"start": v(-46, 96) * mm, "end": v(46, 96) * mm});
            skLineSegment(sketch, "E10.top", {"start": v(-46, 4) * mm, "end": v(46, 4) * mm});
            skLineSegment(sketch, "E10.left", {"start": v(-46, 96) * mm, "end": v(-46, 4) * mm});
            skLineSegment(sketch, "E10.right", {"start": v(46, 96) * mm, "end": v(46, 4) * mm});
            skSolve(sketch);
        }
        {
            var Q0;
            Q0=makeQuery(id+"F4.imprint","IMPRINT",FACE,{"disambiguationData":[TD([[makeQuery(id+"F4.imprint","IMPRINT",EDGE,{"derivedFrom":sQuery(id+"F4.wireOp",EDGE,"E8.1.1.0")}),-1.0]])]});
            var Q1;
            {var subQ2=sQuery(id+"F4.wireOp",EDGE,"E8.11.0.2");Q1=makeQuery(id+"F4.imprint","IMPRINT",FACE,{"disambiguationData":[TD([[makeQuery(id+"F4.imprint","IMPRINT",EDGE,{"derivedFrom":subQ2}),-1.0]])]});}
            var Q2;
            {var subQ2=sQuery(id+"F4.wireOp",EDGE,"E8.10.0.2");Q2=makeQuery(id+"F4.imprint","IMPRINT",FACE,{"disambiguationData":[TD([[makeQuery(id+"F4.imprint","IMPRINT",EDGE,{"derivedFrom":subQ2}),-1.0]])]});}
            var Q3;
            {var subQ2=sQuery(id+"F4.wireOp",EDGE,"E8.9.0.2");Q3=makeQuery(id+"F4.imprint","IMPRINT",FACE,{"disambiguationData":[TD([[makeQuery(id+"F4.imprint","IMPRINT",EDGE,{"derivedFrom":subQ2}),-1.0]])]});}
            var Q4;
            {var subQ2=sQuery(id+"F4.wireOp",EDGE,"E8.8.0.2");Q4=makeQuery(id+"F4.imprint","IMPRINT",FACE,{"disambiguationData":[TD([[makeQuery(id+"F4.imprint","IMPRINT",EDGE,{"derivedFrom":subQ2}),-1.0]])]});}
            var Q5;
            {var subQ2=sQuery(id+"F4.wireOp",EDGE,"E8.7.0.2");Q5=makeQuery(id+"F4.imprint","IMPRINT",FACE,{"disambiguationData":[TD([[makeQuery(id+"F4.imprint","IMPRINT",EDGE,{"derivedFrom":subQ2}),-1.0]])]});}
            var Q6;
            {var subQ2=sQuery(id+"F4.wireOp",EDGE,"E8.6.0.2");Q6=makeQuery(id+"F4.imprint","IMPRINT",FACE,{"disambiguationData":[TD([[makeQuery(id+"F4.imprint","IMPRINT",EDGE,{"derivedFrom":subQ2}),-1.0]])]});}
            var Q7;
            {var subQ2=sQuery(id+"F4.wireOp",EDGE,"E8.5.0.2");Q7=makeQuery(id+"F4.imprint","IMPRINT",FACE,{"disambiguationData":[TD([[makeQuery(id+"F4.imprint","IMPRINT",EDGE,{"derivedFrom":subQ2}),-1.0]])]});}
            var Q8;
            {var subQ2=sQuery(id+"F4.wireOp",EDGE,"E8.4.0.2");Q8=makeQuery(id+"F4.imprint","IMPRINT",FACE,{"disambiguationData":[TD([[makeQuery(id+"F4.imprint","IMPRINT",EDGE,{"derivedFrom":subQ2}),-1.0]])]});}
            var Q9;
            {var subQ2=sQuery(id+"F4.wireOp",EDGE,"E8.3.0.2");Q9=makeQuery(id+"F4.imprint","IMPRINT",FACE,{"disambiguationData":[TD([[makeQuery(id+"F4.imprint","IMPRINT",EDGE,{"derivedFrom":subQ2}),-1.0]])]});}
            var Q10;
            {var subQ2=sQuery(id+"F4.wireOp",EDGE,"E8.2.0.2");Q10=makeQuery(id+"F4.imprint","IMPRINT",FACE,{"disambiguationData":[TD([[makeQuery(id+"F4.imprint","IMPRINT",EDGE,{"derivedFrom":subQ2}),-1.0]])]});}
            var Q11;
            {var subQ2=sQuery(id+"F4.wireOp",EDGE,"E8.1.0.2");Q11=makeQuery(id+"F4.imprint","IMPRINT",FACE,{"disambiguationData":[TD([[makeQuery(id+"F4.imprint","IMPRINT",EDGE,{"derivedFrom":subQ2}),-1.0]])]});}
            var Q12;
            {var subQ2=sQuery(id+"F4.wireOp",EDGE,"E7.top");Q12=makeQuery(id+"F4.imprint","IMPRINT",FACE,{"disambiguationData":[TD([[makeQuery(id+"F4.imprint","IMPRINT",EDGE,{"derivedFrom":subQ2}),1.0]])]});}
            var Q13;
            {var subQ2=sQuery(id+"F4.wireOp",EDGE,"E8.0.1.1");Q13=makeQuery(id+"F4.imprint","IMPRINT",FACE,{"disambiguationData":[TD([[makeQuery(id+"F4.imprint","IMPRINT",EDGE,{"derivedFrom":subQ2}),1.0]])]});}
            var Q14;
            {var subQ2=sQuery(id+"F4.wireOp",EDGE,"E8.0.2.1");Q14=makeQuery(id+"F4.imprint","IMPRINT",FACE,{"disambiguationData":[TD([[makeQuery(id+"F4.imprint","IMPRINT",EDGE,{"derivedFrom":subQ2}),1.0]])]});}
            var Q15;
            {var subQ2=sQuery(id+"F4.wireOp",EDGE,"E8.0.3.1");Q15=makeQuery(id+"F4.imprint","IMPRINT",FACE,{"disambiguationData":[TD([[makeQuery(id+"F4.imprint","IMPRINT",EDGE,{"derivedFrom":subQ2}),1.0]])]});}
            var Q16;
            {var subQ2=sQuery(id+"F4.wireOp",EDGE,"E8.0.4.1");Q16=makeQuery(id+"F4.imprint","IMPRINT",FACE,{"disambiguationData":[TD([[makeQuery(id+"F4.imprint","IMPRINT",EDGE,{"derivedFrom":subQ2}),1.0]])]});}
            var Q17;
            {var subQ2=sQuery(id+"F4.wireOp",EDGE,"E8.0.5.1");Q17=makeQuery(id+"F4.imprint","IMPRINT",FACE,{"disambiguationData":[TD([[makeQuery(id+"F4.imprint","IMPRINT",EDGE,{"derivedFrom":subQ2}),1.0]])]});}
            var Q18;
            {var subQ2=sQuery(id+"F4.wireOp",EDGE,"E8.0.6.1");Q18=makeQuery(id+"F4.imprint","IMPRINT",FACE,{"disambiguationData":[TD([[makeQuery(id+"F4.imprint","IMPRINT",EDGE,{"derivedFrom":subQ2}),1.0]])]});}
            var Q19;
            {var subQ2=sQuery(id+"F4.wireOp",EDGE,"E8.0.7.1");Q19=makeQuery(id+"F4.imprint","IMPRINT",FACE,{"disambiguationData":[TD([[makeQuery(id+"F4.imprint","IMPRINT",EDGE,{"derivedFrom":subQ2}),1.0]])]});}
            var Q20;
            {var subQ2=sQuery(id+"F4.wireOp",EDGE,"E8.0.8.1");Q20=makeQuery(id+"F4.imprint","IMPRINT",FACE,{"disambiguationData":[TD([[makeQuery(id+"F4.imprint","IMPRINT",EDGE,{"derivedFrom":subQ2}),1.0]])]});}
            var Q21;
            {var subQ2=sQuery(id+"F4.wireOp",EDGE,"E8.0.9.1");Q21=makeQuery(id+"F4.imprint","IMPRINT",FACE,{"disambiguationData":[TD([[makeQuery(id+"F4.imprint","IMPRINT",EDGE,{"derivedFrom":subQ2}),1.0]])]});}
            var Q22;
            {var subQ2=sQuery(id+"F4.wireOp",EDGE,"E8.0.10.1");Q22=makeQuery(id+"F4.imprint","IMPRINT",FACE,{"disambiguationData":[TD([[makeQuery(id+"F4.imprint","IMPRINT",EDGE,{"derivedFrom":subQ2}),1.0]])]});}
            var Q23;
            {var subQ2=sQuery(id+"F4.wireOp",EDGE,"E8.0.11.1");Q23=makeQuery(id+"F4.imprint","IMPRINT",FACE,{"disambiguationData":[TD([[makeQuery(id+"F4.imprint","IMPRINT",EDGE,{"derivedFrom":subQ2}),1.0]])]});}
            var Q24;
            {var subQ2=sQuery(id+"F4.wireOp",EDGE,"E8.1.12.2");Q24=makeQuery(id+"F4.imprint","IMPRINT",FACE,{"disambiguationData":[TD([[makeQuery(id+"F4.imprint","IMPRINT",EDGE,{"derivedFrom":subQ2}),-1.0]])]});}
            var Q25;
            {var subQ2=sQuery(id+"F4.wireOp",EDGE,"E8.2.12.2");Q25=makeQuery(id+"F4.imprint","IMPRINT",FACE,{"disambiguationData":[TD([[makeQuery(id+"F4.imprint","IMPRINT",EDGE,{"derivedFrom":subQ2}),-1.0]])]});}
            var Q26;
            {var subQ2=sQuery(id+"F4.wireOp",EDGE,"E8.3.12.2");Q26=makeQuery(id+"F4.imprint","IMPRINT",FACE,{"disambiguationData":[TD([[makeQuery(id+"F4.imprint","IMPRINT",EDGE,{"derivedFrom":subQ2}),-1.0]])]});}
            var Q27;
            {var subQ2=sQuery(id+"F4.wireOp",EDGE,"E8.4.12.2");Q27=makeQuery(id+"F4.imprint","IMPRINT",FACE,{"disambiguationData":[TD([[makeQuery(id+"F4.imprint","IMPRINT",EDGE,{"derivedFrom":subQ2}),-1.0]])]});}
            var Q28;
            {var subQ2=sQuery(id+"F4.wireOp",EDGE,"E8.5.12.2");Q28=makeQuery(id+"F4.imprint","IMPRINT",FACE,{"disambiguationData":[TD([[makeQuery(id+"F4.imprint","IMPRINT",EDGE,{"derivedFrom":subQ2}),-1.0]])]});}
            var Q29;
            {var subQ2=sQuery(id+"F4.wireOp",EDGE,"E8.6.12.2");Q29=makeQuery(id+"F4.imprint","IMPRINT",FACE,{"disambiguationData":[TD([[makeQuery(id+"F4.imprint","IMPRINT",EDGE,{"derivedFrom":subQ2}),-1.0]])]});}
            var Q30;
            {var subQ2=sQuery(id+"F4.wireOp",EDGE,"E8.7.12.2");Q30=makeQuery(id+"F4.imprint","IMPRINT",FACE,{"disambiguationData":[TD([[makeQuery(id+"F4.imprint","IMPRINT",EDGE,{"derivedFrom":subQ2}),-1.0]])]});}
            var Q31;
            {var subQ2=sQuery(id+"F4.wireOp",EDGE,"E8.8.12.2");Q31=makeQuery(id+"F4.imprint","IMPRINT",FACE,{"disambiguationData":[TD([[makeQuery(id+"F4.imprint","IMPRINT",EDGE,{"derivedFrom":subQ2}),-1.0]])]});}
            var Q32;
            {var subQ2=sQuery(id+"F4.wireOp",EDGE,"E8.9.12.2");Q32=makeQuery(id+"F4.imprint","IMPRINT",FACE,{"disambiguationData":[TD([[makeQuery(id+"F4.imprint","IMPRINT",EDGE,{"derivedFrom":subQ2}),-1.0]])]});}
            var Q33;
            {var subQ2=sQuery(id+"F4.wireOp",EDGE,"E8.10.12.2");Q33=makeQuery(id+"F4.imprint","IMPRINT",FACE,{"disambiguationData":[TD([[makeQuery(id+"F4.imprint","IMPRINT",EDGE,{"derivedFrom":subQ2}),-1.0]])]});}
            var Q34;
            {var subQ2=sQuery(id+"F4.wireOp",EDGE,"E8.11.12.2");Q34=makeQuery(id+"F4.imprint","IMPRINT",FACE,{"disambiguationData":[TD([[makeQuery(id+"F4.imprint","IMPRINT",EDGE,{"derivedFrom":subQ2}),-1.0]])]});}
            var Q35;
            {var subQ2=sQuery(id+"F4.wireOp",EDGE,"E8.12.11.1");Q35=makeQuery(id+"F4.imprint","IMPRINT",FACE,{"disambiguationData":[TD([[makeQuery(id+"F4.imprint","IMPRINT",EDGE,{"derivedFrom":subQ2}),1.0]])]});}
            var Q36;
            {var subQ2=sQuery(id+"F4.wireOp",EDGE,"E8.12.10.1");Q36=makeQuery(id+"F4.imprint","IMPRINT",FACE,{"disambiguationData":[TD([[makeQuery(id+"F4.imprint","IMPRINT",EDGE,{"derivedFrom":subQ2}),1.0]])]});}
            var Q37;
            {var subQ2=sQuery(id+"F4.wireOp",EDGE,"E8.12.9.1");Q37=makeQuery(id+"F4.imprint","IMPRINT",FACE,{"disambiguationData":[TD([[makeQuery(id+"F4.imprint","IMPRINT",EDGE,{"derivedFrom":subQ2}),1.0]])]});}
            var Q38;
            {var subQ2=sQuery(id+"F4.wireOp",EDGE,"E8.12.8.1");Q38=makeQuery(id+"F4.imprint","IMPRINT",FACE,{"disambiguationData":[TD([[makeQuery(id+"F4.imprint","IMPRINT",EDGE,{"derivedFrom":subQ2}),1.0]])]});}
            var Q39;
            {var subQ2=sQuery(id+"F4.wireOp",EDGE,"E8.12.7.1");Q39=makeQuery(id+"F4.imprint","IMPRINT",FACE,{"disambiguationData":[TD([[makeQuery(id+"F4.imprint","IMPRINT",EDGE,{"derivedFrom":subQ2}),1.0]])]});}
            var Q40;
            {var subQ2=sQuery(id+"F4.wireOp",EDGE,"E8.12.6.1");Q40=makeQuery(id+"F4.imprint","IMPRINT",FACE,{"disambiguationData":[TD([[makeQuery(id+"F4.imprint","IMPRINT",EDGE,{"derivedFrom":subQ2}),1.0]])]});}
            var Q41;
            {var subQ2=sQuery(id+"F4.wireOp",EDGE,"E8.12.5.1");Q41=makeQuery(id+"F4.imprint","IMPRINT",FACE,{"disambiguationData":[TD([[makeQuery(id+"F4.imprint","IMPRINT",EDGE,{"derivedFrom":subQ2}),1.0]])]});}
            var Q42;
            {var subQ2=sQuery(id+"F4.wireOp",EDGE,"E8.12.4.1");Q42=makeQuery(id+"F4.imprint","IMPRINT",FACE,{"disambiguationData":[TD([[makeQuery(id+"F4.imprint","IMPRINT",EDGE,{"derivedFrom":subQ2}),1.0]])]});}
            var Q43;
            {var subQ2=sQuery(id+"F4.wireOp",EDGE,"E8.12.3.1");Q43=makeQuery(id+"F4.imprint","IMPRINT",FACE,{"disambiguationData":[TD([[makeQuery(id+"F4.imprint","IMPRINT",EDGE,{"derivedFrom":subQ2}),1.0]])]});}
            var Q44;
            {var subQ2=sQuery(id+"F4.wireOp",EDGE,"E8.12.2.1");Q44=makeQuery(id+"F4.imprint","IMPRINT",FACE,{"disambiguationData":[TD([[makeQuery(id+"F4.imprint","IMPRINT",EDGE,{"derivedFrom":subQ2}),1.0]])]});}
            var Q45;
            {var subQ2=sQuery(id+"F4.wireOp",EDGE,"E8.12.1.1");Q45=makeQuery(id+"F4.imprint","IMPRINT",FACE,{"disambiguationData":[TD([[makeQuery(id+"F4.imprint","IMPRINT",EDGE,{"derivedFrom":subQ2}),1.0]])]});}
            var Q46;
            {var subQ2=sQuery(id+"F4.wireOp",EDGE,"E8.12.0.1");Q46=makeQuery(id+"F4.imprint","IMPRINT",FACE,{"disambiguationData":[TD([[makeQuery(id+"F4.imprint","IMPRINT",EDGE,{"derivedFrom":subQ2}),1.0]])]});}
            extrude(context, id + "F5", {"entities" : qUnion([Q0, Q1, Q2, Q3, Q4, Q5, Q6, Q7, Q8, Q9, Q10, Q11, Q12, Q13, Q14, Q15, Q16, Q17, Q18, Q19, Q20, Q21, Q22, Q23, Q24, Q25, Q26, Q27, Q28, Q29, Q30, Q31, Q32, Q33, Q34, Q35, Q36, Q37, Q38, Q39, Q40, Q41, Q42, Q43, Q44, Q45, Q46]), "depth" : 4 * mm});
        }
        {
            var Q0;
            Q0=makeQuery(id+"F3.opExtrude","SWEPT_BODY",BODY,{"disambiguationData":[OSD([sQuery(id+"F2.wireOp",EDGE,"E3.top"),sQuery(id+"F2.wireOp",EDGE,"E3.right"),sQuery(id+"F2.wireOp",EDGE,"E4.0.1.0"),sQuery(id+"F2.wireOp",EDGE,"E4.0.1.1"),sQuery(id+"F2.wireOp",EDGE,"E4.0.1.3"),sQuery(id+"F2.wireOp",EDGE,"E4.0.2.0"),sQuery(id+"F2.wireOp",EDGE,"E4.0.2.1"),sQuery(id+"F2.wireOp",EDGE,"E4.0.2.3"),sQuery(id+"F2.wireOp",EDGE,"E4.0.3.0"),sQuery(id+"F2.wireOp",EDGE,"E4.0.3.1"),sQuery(id+"F2.wireOp",EDGE,"E4.0.3.3"),sQuery(id+"F2.wireOp",EDGE,"E4.0.4.0"),sQuery(id+"F2.wireOp",EDGE,"E4.0.4.1"),sQuery(id+"F2.wireOp",EDGE,"E4.0.4.3"),sQuery(id+"F2.wireOp",EDGE,"E4.0.5.0"),sQuery(id+"F2.wireOp",EDGE,"E4.0.5.1"),sQuery(id+"F2.wireOp",EDGE,"E4.0.5.3"),sQuery(id+"F2.wireOp",EDGE,"E4.0.6.0"),sQuery(id+"F2.wireOp",EDGE,"E4.0.6.1"),sQuery(id+"F2.wireOp",EDGE,"E4.0.6.3"),sQuery(id+"F2.wireOp",EDGE,"E4.0.7.0"),sQuery(id+"F2.wireOp",EDGE,"E4.0.7.1"),sQuery(id+"F2.wireOp",EDGE,"E4.0.7.3"),sQuery(id+"F2.wireOp",EDGE,"E4.0.8.0"),sQuery(id+"F2.wireOp",EDGE,"E4.0.8.1"),sQuery(id+"F2.wireOp",EDGE,"E4.0.8.3"),sQuery(id+"F2.wireOp",EDGE,"E4.0.9.0"),sQuery(id+"F2.wireOp",EDGE,"E4.0.9.1"),sQuery(id+"F2.wireOp",EDGE,"E4.0.9.3"),sQuery(id+"F2.wireOp",EDGE,"E4.0.10.0"),sQuery(id+"F2.wireOp",EDGE,"E4.0.10.1"),sQuery(id+"F2.wireOp",EDGE,"E4.0.10.3"),sQuery(id+"F2.wireOp",EDGE,"E4.0.11.0"),sQuery(id+"F2.wireOp",EDGE,"E4.0.11.1"),sQuery(id+"F2.wireOp",EDGE,"E4.0.11.3"),sQuery(id+"F2.wireOp",EDGE,"E4.0.12.0"),sQuery(id+"F2.wireOp",EDGE,"E4.0.12.3"),sQuery(id+"F2.wireOp",EDGE,"E4.1.0.1"),sQuery(id+"F2.wireOp",EDGE,"E4.1.0.2"),sQuery(id+"F2.wireOp",EDGE,"E4.1.0.3"),sQuery(id+"F2.wireOp",EDGE,"E4.1.1.0"),sQuery(id+"F2.wireOp",EDGE,"E4.1.1.1"),sQuery(id+"F2.wireOp",EDGE,"E4.1.1.2"),sQuery(id+"F2.wireOp",EDGE,"E4.1.1.3"),sQuery(id+"F2.wireOp",EDGE,"E4.1.2.0"),sQuery(id+"F2.wireOp",EDGE,"E4.1.2.1"),sQuery(id+"F2.wireOp",EDGE,"E4.1.2.2"),sQuery(id+"F2.wireOp",EDGE,"E4.1.2.3"),sQuery(id+"F2.wireOp",EDGE,"E4.1.3.0"),sQuery(id+"F2.wireOp",EDGE,"E4.1.3.1"),sQuery(id+"F2.wireOp",EDGE,"E4.1.3.2"),sQuery(id+"F2.wireOp",EDGE,"E4.1.3.3"),sQuery(id+"F2.wireOp",EDGE,"E4.1.4.0"),sQuery(id+"F2.wireOp",EDGE,"E4.1.4.1"),sQuery(id+"F2.wireOp",EDGE,"E4.1.4.2"),sQuery(id+"F2.wireOp",EDGE,"E4.1.4.3"),sQuery(id+"F2.wireOp",EDGE,"E4.1.5.0"),sQuery(id+"F2.wireOp",EDGE,"E4.1.5.1"),sQuery(id+"F2.wireOp",EDGE,"E4.1.5.2"),sQuery(id+"F2.wireOp",EDGE,"E4.1.5.3"),sQuery(id+"F2.wireOp",EDGE,"E4.1.6.0"),sQuery(id+"F2.wireOp",EDGE,"E4.1.6.1"),sQuery(id+"F2.wireOp",EDGE,"E4.1.6.2"),sQuery(id+"F2.wireOp",EDGE,"E4.1.6.3"),sQuery(id+"F2.wireOp",EDGE,"E4.1.7.0"),sQuery(id+"F2.wireOp",EDGE,"E4.1.7.1"),sQuery(id+"F2.wireOp",EDGE,"E4.1.7.2"),sQuery(id+"F2.wireOp",EDGE,"E4.1.7.3"),sQuery(id+"F2.wireOp",EDGE,"E4.1.8.0"),sQuery(id+"F2.wireOp",EDGE,"E4.1.8.1"),sQuery(id+"F2.wireOp",EDGE,"E4.1.8.2"),sQuery(id+"F2.wireOp",EDGE,"E4.1.8.3"),sQuery(id+"F2.wireOp",EDGE,"E4.1.9.0"),sQuery(id+"F2.wireOp",EDGE,"E4.1.9.1"),sQuery(id+"F2.wireOp",EDGE,"E4.1.9.2"),sQuery(id+"F2.wireOp",EDGE,"E4.1.9.3"),sQuery(id+"F2.wireOp",EDGE,"E4.1.10.0"),sQuery(id+"F2.wireOp",EDGE,"E4.1.10.1"),sQuery(id+"F2.wireOp",EDGE,"E4.1.10.2"),sQuery(id+"F2.wireOp",EDGE,"E4.1.10.3"),sQuery(id+"F2.wireOp",EDGE,"E4.1.11.0"),sQuery(id+"F2.wireOp",EDGE,"E4.1.11.1"),sQuery(id+"F2.wireOp",EDGE,"E4.1.11.2"),sQuery(id+"F2.wireOp",EDGE,"E4.1.11.3"),sQuery(id+"F2.wireOp",EDGE,"E4.1.12.0"),sQuery(id+"F2.wireOp",EDGE,"E4.1.12.2"),sQuery(id+"F2.wireOp",EDGE,"E4.1.12.3"),sQuery(id+"F2.wireOp",EDGE,"E4.2.0.1"),sQuery(id+"F2.wireOp",EDGE,"E4.2.0.2"),sQuery(id+"F2.wireOp",EDGE,"E4.2.0.3"),sQuery(id+"F2.wireOp",EDGE,"E4.2.1.0"),sQuery(id+"F2.wireOp",EDGE,"E4.2.1.1"),sQuery(id+"F2.wireOp",EDGE,"E4.2.1.2"),sQuery(id+"F2.wireOp",EDGE,"E4.2.1.3"),sQuery(id+"F2.wireOp",EDGE,"E4.2.2.0"),sQuery(id+"F2.wireOp",EDGE,"E4.2.2.1"),sQuery(id+"F2.wireOp",EDGE,"E4.2.2.2"),sQuery(id+"F2.wireOp",EDGE,"E4.2.2.3"),sQuery(id+"F2.wireOp",EDGE,"E4.2.3.0"),sQuery(id+"F2.wireOp",EDGE,"E4.2.3.1"),sQuery(id+"F2.wireOp",EDGE,"E4.2.3.2"),sQuery(id+"F2.wireOp",EDGE,"E4.2.3.3"),sQuery(id+"F2.wireOp",EDGE,"E4.2.4.0"),sQuery(id+"F2.wireOp",EDGE,"E4.2.4.1"),sQuery(id+"F2.wireOp",EDGE,"E4.2.4.2"),sQuery(id+"F2.wireOp",EDGE,"E4.2.4.3"),sQuery(id+"F2.wireOp",EDGE,"E4.2.5.0"),sQuery(id+"F2.wireOp",EDGE,"E4.2.5.1"),sQuery(id+"F2.wireOp",EDGE,"E4.2.5.2"),sQuery(id+"F2.wireOp",EDGE,"E4.2.5.3"),sQuery(id+"F2.wireOp",EDGE,"E4.2.6.0"),sQuery(id+"F2.wireOp",EDGE,"E4.2.6.1"),sQuery(id+"F2.wireOp",EDGE,"E4.2.6.2"),sQuery(id+"F2.wireOp",EDGE,"E4.2.6.3"),sQuery(id+"F2.wireOp",EDGE,"E4.2.7.0"),sQuery(id+"F2.wireOp",EDGE,"E4.2.7.1"),sQuery(id+"F2.wireOp",EDGE,"E4.2.7.2"),sQuery(id+"F2.wireOp",EDGE,"E4.2.7.3"),sQuery(id+"F2.wireOp",EDGE,"E4.2.8.0"),sQuery(id+"F2.wireOp",EDGE,"E4.2.8.1"),sQuery(id+"F2.wireOp",EDGE,"E4.2.8.2"),sQuery(id+"F2.wireOp",EDGE,"E4.2.8.3"),sQuery(id+"F2.wireOp",EDGE,"E4.2.9.0"),sQuery(id+"F2.wireOp",EDGE,"E4.2.9.1"),sQuery(id+"F2.wireOp",EDGE,"E4.2.9.2"),sQuery(id+"F2.wireOp",EDGE,"E4.2.9.3"),sQuery(id+"F2.wireOp",EDGE,"E4.2.10.0"),sQuery(id+"F2.wireOp",EDGE,"E4.2.10.1"),sQuery(id+"F2.wireOp",EDGE,"E4.2.10.2"),sQuery(id+"F2.wireOp",EDGE,"E4.2.10.3"),sQuery(id+"F2.wireOp",EDGE,"E4.2.11.0"),sQuery(id+"F2.wireOp",EDGE,"E4.2.11.1"),sQuery(id+"F2.wireOp",EDGE,"E4.2.11.2"),sQuery(id+"F2.wireOp",EDGE,"E4.2.11.3"),sQuery(id+"F2.wireOp",EDGE,"E4.2.12.0"),sQuery(id+"F2.wireOp",EDGE,"E4.2.12.2"),sQuery(id+"F2.wireOp",EDGE,"E4.2.12.3"),sQuery(id+"F2.wireOp",EDGE,"E4.3.0.1"),sQuery(id+"F2.wireOp",EDGE,"E4.3.0.2"),sQuery(id+"F2.wireOp",EDGE,"E4.3.0.3"),sQuery(id+"F2.wireOp",EDGE,"E4.3.1.0"),sQuery(id+"F2.wireOp",EDGE,"E4.3.1.1"),sQuery(id+"F2.wireOp",EDGE,"E4.3.1.2"),sQuery(id+"F2.wireOp",EDGE,"E4.3.1.3"),sQuery(id+"F2.wireOp",EDGE,"E4.3.2.0"),sQuery(id+"F2.wireOp",EDGE,"E4.3.2.1"),sQuery(id+"F2.wireOp",EDGE,"E4.3.2.2"),sQuery(id+"F2.wireOp",EDGE,"E4.3.2.3"),sQuery(id+"F2.wireOp",EDGE,"E4.3.3.0"),sQuery(id+"F2.wireOp",EDGE,"E4.3.3.1"),sQuery(id+"F2.wireOp",EDGE,"E4.3.3.2"),sQuery(id+"F2.wireOp",EDGE,"E4.3.3.3"),sQuery(id+"F2.wireOp",EDGE,"E4.3.4.0"),sQuery(id+"F2.wireOp",EDGE,"E4.3.4.1"),sQuery(id+"F2.wireOp",EDGE,"E4.3.4.2"),sQuery(id+"F2.wireOp",EDGE,"E4.3.4.3"),sQuery(id+"F2.wireOp",EDGE,"E4.3.5.0"),sQuery(id+"F2.wireOp",EDGE,"E4.3.5.1"),sQuery(id+"F2.wireOp",EDGE,"E4.3.5.2"),sQuery(id+"F2.wireOp",EDGE,"E4.3.5.3"),sQuery(id+"F2.wireOp",EDGE,"E4.3.6.0"),sQuery(id+"F2.wireOp",EDGE,"E4.3.6.1"),sQuery(id+"F2.wireOp",EDGE,"E4.3.6.2"),sQuery(id+"F2.wireOp",EDGE,"E4.3.6.3"),sQuery(id+"F2.wireOp",EDGE,"E4.3.7.0"),sQuery(id+"F2.wireOp",EDGE,"E4.3.7.1"),sQuery(id+"F2.wireOp",EDGE,"E4.3.7.2"),sQuery(id+"F2.wireOp",EDGE,"E4.3.7.3"),sQuery(id+"F2.wireOp",EDGE,"E4.3.8.0"),sQuery(id+"F2.wireOp",EDGE,"E4.3.8.1"),sQuery(id+"F2.wireOp",EDGE,"E4.3.8.2"),sQuery(id+"F2.wireOp",EDGE,"E4.3.8.3"),sQuery(id+"F2.wireOp",EDGE,"E4.3.9.0"),sQuery(id+"F2.wireOp",EDGE,"E4.3.9.1"),sQuery(id+"F2.wireOp",EDGE,"E4.3.9.2"),sQuery(id+"F2.wireOp",EDGE,"E4.3.9.3"),sQuery(id+"F2.wireOp",EDGE,"E4.3.10.0"),sQuery(id+"F2.wireOp",EDGE,"E4.3.10.1"),sQuery(id+"F2.wireOp",EDGE,"E4.3.10.2"),sQuery(id+"F2.wireOp",EDGE,"E4.3.10.3"),sQuery(id+"F2.wireOp",EDGE,"E4.3.11.0"),sQuery(id+"F2.wireOp",EDGE,"E4.3.11.1"),sQuery(id+"F2.wireOp",EDGE,"E4.3.11.2"),sQuery(id+"F2.wireOp",EDGE,"E4.3.11.3"),sQuery(id+"F2.wireOp",EDGE,"E4.3.12.0"),sQuery(id+"F2.wireOp",EDGE,"E4.3.12.2"),sQuery(id+"F2.wireOp",EDGE,"E4.3.12.3"),sQuery(id+"F2.wireOp",EDGE,"E4.4.0.1"),sQuery(id+"F2.wireOp",EDGE,"E4.4.0.2"),sQuery(id+"F2.wireOp",EDGE,"E4.4.0.3"),sQuery(id+"F2.wireOp",EDGE,"E4.4.1.0"),sQuery(id+"F2.wireOp",EDGE,"E4.4.1.1"),sQuery(id+"F2.wireOp",EDGE,"E4.4.1.2"),sQuery(id+"F2.wireOp",EDGE,"E4.4.1.3"),sQuery(id+"F2.wireOp",EDGE,"E4.4.2.0"),sQuery(id+"F2.wireOp",EDGE,"E4.4.2.1"),sQuery(id+"F2.wireOp",EDGE,"E4.4.2.2"),sQuery(id+"F2.wireOp",EDGE,"E4.4.2.3"),sQuery(id+"F2.wireOp",EDGE,"E4.4.3.0"),sQuery(id+"F2.wireOp",EDGE,"E4.4.3.1"),sQuery(id+"F2.wireOp",EDGE,"E4.4.3.2"),sQuery(id+"F2.wireOp",EDGE,"E4.4.3.3"),sQuery(id+"F2.wireOp",EDGE,"E4.4.4.0"),sQuery(id+"F2.wireOp",EDGE,"E4.4.4.1"),sQuery(id+"F2.wireOp",EDGE,"E4.4.4.2"),sQuery(id+"F2.wireOp",EDGE,"E4.4.4.3"),sQuery(id+"F2.wireOp",EDGE,"E4.4.5.0"),sQuery(id+"F2.wireOp",EDGE,"E4.4.5.1"),sQuery(id+"F2.wireOp",EDGE,"E4.4.5.2"),sQuery(id+"F2.wireOp",EDGE,"E4.4.5.3"),sQuery(id+"F2.wireOp",EDGE,"E4.4.6.0"),sQuery(id+"F2.wireOp",EDGE,"E4.4.6.1"),sQuery(id+"F2.wireOp",EDGE,"E4.4.6.2"),sQuery(id+"F2.wireOp",EDGE,"E4.4.6.3"),sQuery(id+"F2.wireOp",EDGE,"E4.4.7.0"),sQuery(id+"F2.wireOp",EDGE,"E4.4.7.1"),sQuery(id+"F2.wireOp",EDGE,"E4.4.7.2"),sQuery(id+"F2.wireOp",EDGE,"E4.4.7.3"),sQuery(id+"F2.wireOp",EDGE,"E4.4.8.0"),sQuery(id+"F2.wireOp",EDGE,"E4.4.8.1"),sQuery(id+"F2.wireOp",EDGE,"E4.4.8.2"),sQuery(id+"F2.wireOp",EDGE,"E4.4.8.3"),sQuery(id+"F2.wireOp",EDGE,"E4.4.9.0"),sQuery(id+"F2.wireOp",EDGE,"E4.4.9.1"),sQuery(id+"F2.wireOp",EDGE,"E4.4.9.2"),sQuery(id+"F2.wireOp",EDGE,"E4.4.9.3"),sQuery(id+"F2.wireOp",EDGE,"E4.4.10.0"),sQuery(id+"F2.wireOp",EDGE,"E4.4.10.1"),sQuery(id+"F2.wireOp",EDGE,"E4.4.10.2"),sQuery(id+"F2.wireOp",EDGE,"E4.4.10.3"),sQuery(id+"F2.wireOp",EDGE,"E4.4.11.0"),sQuery(id+"F2.wireOp",EDGE,"E4.4.11.1"),sQuery(id+"F2.wireOp",EDGE,"E4.4.11.2"),sQuery(id+"F2.wireOp",EDGE,"E4.4.11.3"),sQuery(id+"F2.wireOp",EDGE,"E4.4.12.0"),sQuery(id+"F2.wireOp",EDGE,"E4.4.12.2"),sQuery(id+"F2.wireOp",EDGE,"E4.4.12.3"),sQuery(id+"F2.wireOp",EDGE,"E4.5.0.1"),sQuery(id+"F2.wireOp",EDGE,"E4.5.0.2"),sQuery(id+"F2.wireOp",EDGE,"E4.5.0.3"),sQuery(id+"F2.wireOp",EDGE,"E4.5.1.0"),sQuery(id+"F2.wireOp",EDGE,"E4.5.1.1"),sQuery(id+"F2.wireOp",EDGE,"E4.5.1.2"),sQuery(id+"F2.wireOp",EDGE,"E4.5.1.3"),sQuery(id+"F2.wireOp",EDGE,"E4.5.2.0"),sQuery(id+"F2.wireOp",EDGE,"E4.5.2.1"),sQuery(id+"F2.wireOp",EDGE,"E4.5.2.2"),sQuery(id+"F2.wireOp",EDGE,"E4.5.2.3"),sQuery(id+"F2.wireOp",EDGE,"E4.5.3.0"),sQuery(id+"F2.wireOp",EDGE,"E4.5.3.1"),sQuery(id+"F2.wireOp",EDGE,"E4.5.3.2"),sQuery(id+"F2.wireOp",EDGE,"E4.5.3.3"),sQuery(id+"F2.wireOp",EDGE,"E4.5.4.0"),sQuery(id+"F2.wireOp",EDGE,"E4.5.4.1"),sQuery(id+"F2.wireOp",EDGE,"E4.5.4.2"),sQuery(id+"F2.wireOp",EDGE,"E4.5.4.3"),sQuery(id+"F2.wireOp",EDGE,"E4.5.5.0"),sQuery(id+"F2.wireOp",EDGE,"E4.5.5.1"),sQuery(id+"F2.wireOp",EDGE,"E4.5.5.2"),sQuery(id+"F2.wireOp",EDGE,"E4.5.5.3"),sQuery(id+"F2.wireOp",EDGE,"E4.5.6.0"),sQuery(id+"F2.wireOp",EDGE,"E4.5.6.1"),sQuery(id+"F2.wireOp",EDGE,"E4.5.6.2"),sQuery(id+"F2.wireOp",EDGE,"E4.5.6.3"),sQuery(id+"F2.wireOp",EDGE,"E4.5.7.0"),sQuery(id+"F2.wireOp",EDGE,"E4.5.7.1"),sQuery(id+"F2.wireOp",EDGE,"E4.5.7.2"),sQuery(id+"F2.wireOp",EDGE,"E4.5.7.3"),sQuery(id+"F2.wireOp",EDGE,"E4.5.8.0"),sQuery(id+"F2.wireOp",EDGE,"E4.5.8.1"),sQuery(id+"F2.wireOp",EDGE,"E4.5.8.2"),sQuery(id+"F2.wireOp",EDGE,"E4.5.8.3"),sQuery(id+"F2.wireOp",EDGE,"E4.5.9.0"),sQuery(id+"F2.wireOp",EDGE,"E4.5.9.1"),sQuery(id+"F2.wireOp",EDGE,"E4.5.9.2"),sQuery(id+"F2.wireOp",EDGE,"E4.5.9.3"),sQuery(id+"F2.wireOp",EDGE,"E4.5.10.0"),sQuery(id+"F2.wireOp",EDGE,"E4.5.10.1"),sQuery(id+"F2.wireOp",EDGE,"E4.5.10.2"),sQuery(id+"F2.wireOp",EDGE,"E4.5.10.3"),sQuery(id+"F2.wireOp",EDGE,"E4.5.11.0"),sQuery(id+"F2.wireOp",EDGE,"E4.5.11.1"),sQuery(id+"F2.wireOp",EDGE,"E4.5.11.2"),sQuery(id+"F2.wireOp",EDGE,"E4.5.11.3"),sQuery(id+"F2.wireOp",EDGE,"E4.5.12.0"),sQuery(id+"F2.wireOp",EDGE,"E4.5.12.2"),sQuery(id+"F2.wireOp",EDGE,"E4.5.12.3"),sQuery(id+"F2.wireOp",EDGE,"E4.6.0.1"),sQuery(id+"F2.wireOp",EDGE,"E4.6.0.2"),sQuery(id+"F2.wireOp",EDGE,"E4.6.0.3"),sQuery(id+"F2.wireOp",EDGE,"E4.6.1.0"),sQuery(id+"F2.wireOp",EDGE,"E4.6.1.1"),sQuery(id+"F2.wireOp",EDGE,"E4.6.1.2"),sQuery(id+"F2.wireOp",EDGE,"E4.6.1.3"),sQuery(id+"F2.wireOp",EDGE,"E4.6.2.0"),sQuery(id+"F2.wireOp",EDGE,"E4.6.2.1"),sQuery(id+"F2.wireOp",EDGE,"E4.6.2.2"),sQuery(id+"F2.wireOp",EDGE,"E4.6.2.3"),sQuery(id+"F2.wireOp",EDGE,"E4.6.3.0"),sQuery(id+"F2.wireOp",EDGE,"E4.6.3.1"),sQuery(id+"F2.wireOp",EDGE,"E4.6.3.2"),sQuery(id+"F2.wireOp",EDGE,"E4.6.3.3"),sQuery(id+"F2.wireOp",EDGE,"E4.6.4.0"),sQuery(id+"F2.wireOp",EDGE,"E4.6.4.1"),sQuery(id+"F2.wireOp",EDGE,"E4.6.4.2"),sQuery(id+"F2.wireOp",EDGE,"E4.6.4.3"),sQuery(id+"F2.wireOp",EDGE,"E4.6.5.0"),sQuery(id+"F2.wireOp",EDGE,"E4.6.5.1"),sQuery(id+"F2.wireOp",EDGE,"E4.6.5.2"),sQuery(id+"F2.wireOp",EDGE,"E4.6.5.3"),sQuery(id+"F2.wireOp",EDGE,"E4.6.6.0"),sQuery(id+"F2.wireOp",EDGE,"E4.6.6.1"),sQuery(id+"F2.wireOp",EDGE,"E4.6.6.2"),sQuery(id+"F2.wireOp",EDGE,"E4.6.6.3"),sQuery(id+"F2.wireOp",EDGE,"E4.6.7.0"),sQuery(id+"F2.wireOp",EDGE,"E4.6.7.1"),sQuery(id+"F2.wireOp",EDGE,"E4.6.7.2"),sQuery(id+"F2.wireOp",EDGE,"E4.6.7.3"),sQuery(id+"F2.wireOp",EDGE,"E4.6.8.0"),sQuery(id+"F2.wireOp",EDGE,"E4.6.8.1"),sQuery(id+"F2.wireOp",EDGE,"E4.6.8.2"),sQuery(id+"F2.wireOp",EDGE,"E4.6.8.3"),sQuery(id+"F2.wireOp",EDGE,"E4.6.9.0"),sQuery(id+"F2.wireOp",EDGE,"E4.6.9.1"),sQuery(id+"F2.wireOp",EDGE,"E4.6.9.2"),sQuery(id+"F2.wireOp",EDGE,"E4.6.9.3"),sQuery(id+"F2.wireOp",EDGE,"E4.6.10.0"),sQuery(id+"F2.wireOp",EDGE,"E4.6.10.1"),sQuery(id+"F2.wireOp",EDGE,"E4.6.10.2"),sQuery(id+"F2.wireOp",EDGE,"E4.6.10.3"),sQuery(id+"F2.wireOp",EDGE,"E4.6.11.0"),sQuery(id+"F2.wireOp",EDGE,"E4.6.11.1"),sQuery(id+"F2.wireOp",EDGE,"E4.6.11.2"),sQuery(id+"F2.wireOp",EDGE,"E4.6.11.3"),sQuery(id+"F2.wireOp",EDGE,"E4.6.12.0"),sQuery(id+"F2.wireOp",EDGE,"E4.6.12.2"),sQuery(id+"F2.wireOp",EDGE,"E4.6.12.3"),sQuery(id+"F2.wireOp",EDGE,"E4.7.0.1"),sQuery(id+"F2.wireOp",EDGE,"E4.7.0.2"),sQuery(id+"F2.wireOp",EDGE,"E4.7.0.3"),sQuery(id+"F2.wireOp",EDGE,"E4.7.1.0"),sQuery(id+"F2.wireOp",EDGE,"E4.7.1.1"),sQuery(id+"F2.wireOp",EDGE,"E4.7.1.2"),sQuery(id+"F2.wireOp",EDGE,"E4.7.1.3"),sQuery(id+"F2.wireOp",EDGE,"E4.7.2.0"),sQuery(id+"F2.wireOp",EDGE,"E4.7.2.1"),sQuery(id+"F2.wireOp",EDGE,"E4.7.2.2"),sQuery(id+"F2.wireOp",EDGE,"E4.7.2.3"),sQuery(id+"F2.wireOp",EDGE,"E4.7.3.0"),sQuery(id+"F2.wireOp",EDGE,"E4.7.3.1"),sQuery(id+"F2.wireOp",EDGE,"E4.7.3.2"),sQuery(id+"F2.wireOp",EDGE,"E4.7.3.3"),sQuery(id+"F2.wireOp",EDGE,"E4.7.4.0"),sQuery(id+"F2.wireOp",EDGE,"E4.7.4.1"),sQuery(id+"F2.wireOp",EDGE,"E4.7.4.2"),sQuery(id+"F2.wireOp",EDGE,"E4.7.4.3"),sQuery(id+"F2.wireOp",EDGE,"E4.7.5.0"),sQuery(id+"F2.wireOp",EDGE,"E4.7.5.1"),sQuery(id+"F2.wireOp",EDGE,"E4.7.5.2"),sQuery(id+"F2.wireOp",EDGE,"E4.7.5.3"),sQuery(id+"F2.wireOp",EDGE,"E4.7.6.0"),sQuery(id+"F2.wireOp",EDGE,"E4.7.6.1"),sQuery(id+"F2.wireOp",EDGE,"E4.7.6.2"),sQuery(id+"F2.wireOp",EDGE,"E4.7.6.3"),sQuery(id+"F2.wireOp",EDGE,"E4.7.7.0"),sQuery(id+"F2.wireOp",EDGE,"E4.7.7.1"),sQuery(id+"F2.wireOp",EDGE,"E4.7.7.2"),sQuery(id+"F2.wireOp",EDGE,"E4.7.7.3"),sQuery(id+"F2.wireOp",EDGE,"E4.7.8.0"),sQuery(id+"F2.wireOp",EDGE,"E4.7.8.1"),sQuery(id+"F2.wireOp",EDGE,"E4.7.8.2"),sQuery(id+"F2.wireOp",EDGE,"E4.7.8.3"),sQuery(id+"F2.wireOp",EDGE,"E4.7.9.0"),sQuery(id+"F2.wireOp",EDGE,"E4.7.9.1"),sQuery(id+"F2.wireOp",EDGE,"E4.7.9.2"),sQuery(id+"F2.wireOp",EDGE,"E4.7.9.3"),sQuery(id+"F2.wireOp",EDGE,"E4.7.10.0"),sQuery(id+"F2.wireOp",EDGE,"E4.7.10.1"),sQuery(id+"F2.wireOp",EDGE,"E4.7.10.2"),sQuery(id+"F2.wireOp",EDGE,"E4.7.10.3"),sQuery(id+"F2.wireOp",EDGE,"E4.7.11.0"),sQuery(id+"F2.wireOp",EDGE,"E4.7.11.1"),sQuery(id+"F2.wireOp",EDGE,"E4.7.11.2"),sQuery(id+"F2.wireOp",EDGE,"E4.7.11.3"),sQuery(id+"F2.wireOp",EDGE,"E4.7.12.0"),sQuery(id+"F2.wireOp",EDGE,"E4.7.12.2"),sQuery(id+"F2.wireOp",EDGE,"E4.7.12.3"),sQuery(id+"F2.wireOp",EDGE,"E4.8.0.1"),sQuery(id+"F2.wireOp",EDGE,"E4.8.0.2"),sQuery(id+"F2.wireOp",EDGE,"E4.8.0.3"),sQuery(id+"F2.wireOp",EDGE,"E4.8.1.0"),sQuery(id+"F2.wireOp",EDGE,"E4.8.1.1"),sQuery(id+"F2.wireOp",EDGE,"E4.8.1.2"),sQuery(id+"F2.wireOp",EDGE,"E4.8.1.3"),sQuery(id+"F2.wireOp",EDGE,"E4.8.2.0"),sQuery(id+"F2.wireOp",EDGE,"E4.8.2.1"),sQuery(id+"F2.wireOp",EDGE,"E4.8.2.2"),sQuery(id+"F2.wireOp",EDGE,"E4.8.2.3"),sQuery(id+"F2.wireOp",EDGE,"E4.8.3.0"),sQuery(id+"F2.wireOp",EDGE,"E4.8.3.1"),sQuery(id+"F2.wireOp",EDGE,"E4.8.3.2"),sQuery(id+"F2.wireOp",EDGE,"E4.8.3.3"),sQuery(id+"F2.wireOp",EDGE,"E4.8.4.0"),sQuery(id+"F2.wireOp",EDGE,"E4.8.4.1"),sQuery(id+"F2.wireOp",EDGE,"E4.8.4.2"),sQuery(id+"F2.wireOp",EDGE,"E4.8.4.3"),sQuery(id+"F2.wireOp",EDGE,"E4.8.5.0"),sQuery(id+"F2.wireOp",EDGE,"E4.8.5.1"),sQuery(id+"F2.wireOp",EDGE,"E4.8.5.2"),sQuery(id+"F2.wireOp",EDGE,"E4.8.5.3"),sQuery(id+"F2.wireOp",EDGE,"E4.8.6.0"),sQuery(id+"F2.wireOp",EDGE,"E4.8.6.1"),sQuery(id+"F2.wireOp",EDGE,"E4.8.6.2"),sQuery(id+"F2.wireOp",EDGE,"E4.8.6.3"),sQuery(id+"F2.wireOp",EDGE,"E4.8.7.0"),sQuery(id+"F2.wireOp",EDGE,"E4.8.7.1"),sQuery(id+"F2.wireOp",EDGE,"E4.8.7.2"),sQuery(id+"F2.wireOp",EDGE,"E4.8.7.3"),sQuery(id+"F2.wireOp",EDGE,"E4.8.8.0"),sQuery(id+"F2.wireOp",EDGE,"E4.8.8.1"),sQuery(id+"F2.wireOp",EDGE,"E4.8.8.2"),sQuery(id+"F2.wireOp",EDGE,"E4.8.8.3"),sQuery(id+"F2.wireOp",EDGE,"E4.8.9.0"),sQuery(id+"F2.wireOp",EDGE,"E4.8.9.1"),sQuery(id+"F2.wireOp",EDGE,"E4.8.9.2"),sQuery(id+"F2.wireOp",EDGE,"E4.8.9.3"),sQuery(id+"F2.wireOp",EDGE,"E4.8.10.0"),sQuery(id+"F2.wireOp",EDGE,"E4.8.10.1"),sQuery(id+"F2.wireOp",EDGE,"E4.8.10.2"),sQuery(id+"F2.wireOp",EDGE,"E4.8.10.3"),sQuery(id+"F2.wireOp",EDGE,"E4.8.11.0"),sQuery(id+"F2.wireOp",EDGE,"E4.8.11.1"),sQuery(id+"F2.wireOp",EDGE,"E4.8.11.2"),sQuery(id+"F2.wireOp",EDGE,"E4.8.11.3"),sQuery(id+"F2.wireOp",EDGE,"E4.8.12.0"),sQuery(id+"F2.wireOp",EDGE,"E4.8.12.2"),sQuery(id+"F2.wireOp",EDGE,"E4.8.12.3"),sQuery(id+"F2.wireOp",EDGE,"E4.9.0.1"),sQuery(id+"F2.wireOp",EDGE,"E4.9.0.2"),sQuery(id+"F2.wireOp",EDGE,"E4.9.0.3"),sQuery(id+"F2.wireOp",EDGE,"E4.9.1.0"),sQuery(id+"F2.wireOp",EDGE,"E4.9.1.1"),sQuery(id+"F2.wireOp",EDGE,"E4.9.1.2"),sQuery(id+"F2.wireOp",EDGE,"E4.9.1.3"),sQuery(id+"F2.wireOp",EDGE,"E4.9.2.0"),sQuery(id+"F2.wireOp",EDGE,"E4.9.2.1"),sQuery(id+"F2.wireOp",EDGE,"E4.9.2.2"),sQuery(id+"F2.wireOp",EDGE,"E4.9.2.3"),sQuery(id+"F2.wireOp",EDGE,"E4.9.3.0"),sQuery(id+"F2.wireOp",EDGE,"E4.9.3.1"),sQuery(id+"F2.wireOp",EDGE,"E4.9.3.2"),sQuery(id+"F2.wireOp",EDGE,"E4.9.3.3"),sQuery(id+"F2.wireOp",EDGE,"E4.9.4.0"),sQuery(id+"F2.wireOp",EDGE,"E4.9.4.1"),sQuery(id+"F2.wireOp",EDGE,"E4.9.4.2"),sQuery(id+"F2.wireOp",EDGE,"E4.9.4.3"),sQuery(id+"F2.wireOp",EDGE,"E4.9.5.0"),sQuery(id+"F2.wireOp",EDGE,"E4.9.5.1"),sQuery(id+"F2.wireOp",EDGE,"E4.9.5.2"),sQuery(id+"F2.wireOp",EDGE,"E4.9.5.3"),sQuery(id+"F2.wireOp",EDGE,"E4.9.6.0"),sQuery(id+"F2.wireOp",EDGE,"E4.9.6.1"),sQuery(id+"F2.wireOp",EDGE,"E4.9.6.2"),sQuery(id+"F2.wireOp",EDGE,"E4.9.6.3"),sQuery(id+"F2.wireOp",EDGE,"E4.9.7.0"),sQuery(id+"F2.wireOp",EDGE,"E4.9.7.1"),sQuery(id+"F2.wireOp",EDGE,"E4.9.7.2"),sQuery(id+"F2.wireOp",EDGE,"E4.9.7.3"),sQuery(id+"F2.wireOp",EDGE,"E4.9.8.0"),sQuery(id+"F2.wireOp",EDGE,"E4.9.8.1"),sQuery(id+"F2.wireOp",EDGE,"E4.9.8.2"),sQuery(id+"F2.wireOp",EDGE,"E4.9.8.3"),sQuery(id+"F2.wireOp",EDGE,"E4.9.9.0"),sQuery(id+"F2.wireOp",EDGE,"E4.9.9.1"),sQuery(id+"F2.wireOp",EDGE,"E4.9.9.2"),sQuery(id+"F2.wireOp",EDGE,"E4.9.9.3"),sQuery(id+"F2.wireOp",EDGE,"E4.9.10.0"),sQuery(id+"F2.wireOp",EDGE,"E4.9.10.1"),sQuery(id+"F2.wireOp",EDGE,"E4.9.10.2"),sQuery(id+"F2.wireOp",EDGE,"E4.9.10.3"),sQuery(id+"F2.wireOp",EDGE,"E4.9.11.0"),sQuery(id+"F2.wireOp",EDGE,"E4.9.11.1"),sQuery(id+"F2.wireOp",EDGE,"E4.9.11.2"),sQuery(id+"F2.wireOp",EDGE,"E4.9.11.3"),sQuery(id+"F2.wireOp",EDGE,"E4.9.12.0"),sQuery(id+"F2.wireOp",EDGE,"E4.9.12.2"),sQuery(id+"F2.wireOp",EDGE,"E4.9.12.3"),sQuery(id+"F2.wireOp",EDGE,"E4.10.0.1"),sQuery(id+"F2.wireOp",EDGE,"E4.10.0.2"),sQuery(id+"F2.wireOp",EDGE,"E4.10.0.3"),sQuery(id+"F2.wireOp",EDGE,"E4.10.1.0"),sQuery(id+"F2.wireOp",EDGE,"E4.10.1.1"),sQuery(id+"F2.wireOp",EDGE,"E4.10.1.2"),sQuery(id+"F2.wireOp",EDGE,"E4.10.1.3"),sQuery(id+"F2.wireOp",EDGE,"E4.10.2.0"),sQuery(id+"F2.wireOp",EDGE,"E4.10.2.1"),sQuery(id+"F2.wireOp",EDGE,"E4.10.2.2"),sQuery(id+"F2.wireOp",EDGE,"E4.10.2.3"),sQuery(id+"F2.wireOp",EDGE,"E4.10.3.0"),sQuery(id+"F2.wireOp",EDGE,"E4.10.3.1"),sQuery(id+"F2.wireOp",EDGE,"E4.10.3.2"),sQuery(id+"F2.wireOp",EDGE,"E4.10.3.3"),sQuery(id+"F2.wireOp",EDGE,"E4.10.4.0"),sQuery(id+"F2.wireOp",EDGE,"E4.10.4.1"),sQuery(id+"F2.wireOp",EDGE,"E4.10.4.2"),sQuery(id+"F2.wireOp",EDGE,"E4.10.4.3"),sQuery(id+"F2.wireOp",EDGE,"E4.10.5.0"),sQuery(id+"F2.wireOp",EDGE,"E4.10.5.1"),sQuery(id+"F2.wireOp",EDGE,"E4.10.5.2"),sQuery(id+"F2.wireOp",EDGE,"E4.10.5.3"),sQuery(id+"F2.wireOp",EDGE,"E4.10.6.0"),sQuery(id+"F2.wireOp",EDGE,"E4.10.6.1"),sQuery(id+"F2.wireOp",EDGE,"E4.10.6.2"),sQuery(id+"F2.wireOp",EDGE,"E4.10.6.3"),sQuery(id+"F2.wireOp",EDGE,"E4.10.7.0"),sQuery(id+"F2.wireOp",EDGE,"E4.10.7.1"),sQuery(id+"F2.wireOp",EDGE,"E4.10.7.2"),sQuery(id+"F2.wireOp",EDGE,"E4.10.7.3"),sQuery(id+"F2.wireOp",EDGE,"E4.10.8.0"),sQuery(id+"F2.wireOp",EDGE,"E4.10.8.1"),sQuery(id+"F2.wireOp",EDGE,"E4.10.8.2"),sQuery(id+"F2.wireOp",EDGE,"E4.10.8.3"),sQuery(id+"F2.wireOp",EDGE,"E4.10.9.0"),sQuery(id+"F2.wireOp",EDGE,"E4.10.9.1"),sQuery(id+"F2.wireOp",EDGE,"E4.10.9.2"),sQuery(id+"F2.wireOp",EDGE,"E4.10.9.3"),sQuery(id+"F2.wireOp",EDGE,"E4.10.10.0"),sQuery(id+"F2.wireOp",EDGE,"E4.10.10.1"),sQuery(id+"F2.wireOp",EDGE,"E4.10.10.2"),sQuery(id+"F2.wireOp",EDGE,"E4.10.10.3"),sQuery(id+"F2.wireOp",EDGE,"E4.10.11.0"),sQuery(id+"F2.wireOp",EDGE,"E4.10.11.1"),sQuery(id+"F2.wireOp",EDGE,"E4.10.11.2"),sQuery(id+"F2.wireOp",EDGE,"E4.10.11.3"),sQuery(id+"F2.wireOp",EDGE,"E4.10.12.0"),sQuery(id+"F2.wireOp",EDGE,"E4.10.12.2"),sQuery(id+"F2.wireOp",EDGE,"E4.10.12.3"),sQuery(id+"F2.wireOp",EDGE,"E4.11.0.1"),sQuery(id+"F2.wireOp",EDGE,"E4.11.0.2"),sQuery(id+"F2.wireOp",EDGE,"E4.11.0.3"),sQuery(id+"F2.wireOp",EDGE,"E4.11.1.0"),sQuery(id+"F2.wireOp",EDGE,"E4.11.1.1"),sQuery(id+"F2.wireOp",EDGE,"E4.11.1.2"),sQuery(id+"F2.wireOp",EDGE,"E4.11.1.3"),sQuery(id+"F2.wireOp",EDGE,"E4.11.2.0"),sQuery(id+"F2.wireOp",EDGE,"E4.11.2.1"),sQuery(id+"F2.wireOp",EDGE,"E4.11.2.2"),sQuery(id+"F2.wireOp",EDGE,"E4.11.2.3"),sQuery(id+"F2.wireOp",EDGE,"E4.11.3.0"),sQuery(id+"F2.wireOp",EDGE,"E4.11.3.1"),sQuery(id+"F2.wireOp",EDGE,"E4.11.3.2"),sQuery(id+"F2.wireOp",EDGE,"E4.11.3.3"),sQuery(id+"F2.wireOp",EDGE,"E4.11.4.0"),sQuery(id+"F2.wireOp",EDGE,"E4.11.4.1"),sQuery(id+"F2.wireOp",EDGE,"E4.11.4.2"),sQuery(id+"F2.wireOp",EDGE,"E4.11.4.3"),sQuery(id+"F2.wireOp",EDGE,"E4.11.5.0"),sQuery(id+"F2.wireOp",EDGE,"E4.11.5.1"),sQuery(id+"F2.wireOp",EDGE,"E4.11.5.2"),sQuery(id+"F2.wireOp",EDGE,"E4.11.5.3"),sQuery(id+"F2.wireOp",EDGE,"E4.11.6.0"),sQuery(id+"F2.wireOp",EDGE,"E4.11.6.1"),sQuery(id+"F2.wireOp",EDGE,"E4.11.6.2"),sQuery(id+"F2.wireOp",EDGE,"E4.11.6.3"),sQuery(id+"F2.wireOp",EDGE,"E4.11.7.0"),sQuery(id+"F2.wireOp",EDGE,"E4.11.7.1"),sQuery(id+"F2.wireOp",EDGE,"E4.11.7.2"),sQuery(id+"F2.wireOp",EDGE,"E4.11.7.3"),sQuery(id+"F2.wireOp",EDGE,"E4.11.8.0"),sQuery(id+"F2.wireOp",EDGE,"E4.11.8.1"),sQuery(id+"F2.wireOp",EDGE,"E4.11.8.2"),sQuery(id+"F2.wireOp",EDGE,"E4.11.8.3"),sQuery(id+"F2.wireOp",EDGE,"E4.11.9.0"),sQuery(id+"F2.wireOp",EDGE,"E4.11.9.1"),sQuery(id+"F2.wireOp",EDGE,"E4.11.9.2"),sQuery(id+"F2.wireOp",EDGE,"E4.11.9.3"),sQuery(id+"F2.wireOp",EDGE,"E4.11.10.0"),sQuery(id+"F2.wireOp",EDGE,"E4.11.10.1"),sQuery(id+"F2.wireOp",EDGE,"E4.11.10.2"),sQuery(id+"F2.wireOp",EDGE,"E4.11.10.3"),sQuery(id+"F2.wireOp",EDGE,"E4.11.11.0"),sQuery(id+"F2.wireOp",EDGE,"E4.11.11.1"),sQuery(id+"F2.wireOp",EDGE,"E4.11.11.2"),sQuery(id+"F2.wireOp",EDGE,"E4.11.11.3"),sQuery(id+"F2.wireOp",EDGE,"E4.11.12.0"),sQuery(id+"F2.wireOp",EDGE,"E4.11.12.2"),sQuery(id+"F2.wireOp",EDGE,"E4.11.12.3"),sQuery(id+"F2.wireOp",EDGE,"E4.12.0.1"),sQuery(id+"F2.wireOp",EDGE,"E4.12.0.2"),sQuery(id+"F2.wireOp",EDGE,"E4.12.1.0"),sQuery(id+"F2.wireOp",EDGE,"E4.12.1.1"),sQuery(id+"F2.wireOp",EDGE,"E4.12.1.2"),sQuery(id+"F2.wireOp",EDGE,"E4.12.2.0"),sQuery(id+"F2.wireOp",EDGE,"E4.12.2.1"),sQuery(id+"F2.wireOp",EDGE,"E4.12.2.2"),sQuery(id+"F2.wireOp",EDGE,"E4.12.3.0"),sQuery(id+"F2.wireOp",EDGE,"E4.12.3.1"),sQuery(id+"F2.wireOp",EDGE,"E4.12.3.2"),sQuery(id+"F2.wireOp",EDGE,"E4.12.4.0"),sQuery(id+"F2.wireOp",EDGE,"E4.12.4.1"),sQuery(id+"F2.wireOp",EDGE,"E4.12.4.2"),sQuery(id+"F2.wireOp",EDGE,"E4.12.5.0"),sQuery(id+"F2.wireOp",EDGE,"E4.12.5.1"),sQuery(id+"F2.wireOp",EDGE,"E4.12.5.2"),sQuery(id+"F2.wireOp",EDGE,"E4.12.6.0"),sQuery(id+"F2.wireOp",EDGE,"E4.12.6.1"),sQuery(id+"F2.wireOp",EDGE,"E4.12.6.2"),sQuery(id+"F2.wireOp",EDGE,"E4.12.7.0"),sQuery(id+"F2.wireOp",EDGE,"E4.12.7.1"),sQuery(id+"F2.wireOp",EDGE,"E4.12.7.2"),sQuery(id+"F2.wireOp",EDGE,"E4.12.8.0"),sQuery(id+"F2.wireOp",EDGE,"E4.12.8.1"),sQuery(id+"F2.wireOp",EDGE,"E4.12.8.2"),sQuery(id+"F2.wireOp",EDGE,"E4.12.9.0"),sQuery(id+"F2.wireOp",EDGE,"E4.12.9.1"),sQuery(id+"F2.wireOp",EDGE,"E4.12.9.2"),sQuery(id+"F2.wireOp",EDGE,"E4.12.10.0"),sQuery(id+"F2.wireOp",EDGE,"E4.12.10.1"),sQuery(id+"F2.wireOp",EDGE,"E4.12.10.2"),sQuery(id+"F2.wireOp",EDGE,"E4.12.11.0"),sQuery(id+"F2.wireOp",EDGE,"E4.12.11.1"),sQuery(id+"F2.wireOp",EDGE,"E4.12.11.2"),sQuery(id+"F2.wireOp",EDGE,"E4.12.12.0"),sQuery(id+"F2.wireOp",EDGE,"E4.12.12.2"),sQuery(id+"F2.wireOp",EDGE,"E5.bottom"),sQuery(id+"F2.wireOp",EDGE,"E5.top"),sQuery(id+"F2.wireOp",EDGE,"E5.left"),sQuery(id+"F2.wireOp",EDGE,"E5.right")])]});
            transform(context, id + "F6", {"entities" : qUnion([Q0]), "transformType" : TransformType.TRANSLATION_3D, "dx" : 0 * mm, "dy" : 50 * mm, "dz" : -50 * mm, "makeCopy" : false});
        }
        {
            var Q0;
            Q0=makeQuery(id+"F3.opExtrude","SWEPT_BODY",BODY,{"disambiguationData":[OSD([sQuery(id+"F2.wireOp",EDGE,"E4.0.1.0"),sQuery(id+"F2.wireOp",EDGE,"E4.0.1.1"),sQuery(id+"F2.wireOp",EDGE,"E4.0.2.0"),sQuery(id+"F2.wireOp",EDGE,"E4.0.2.1"),sQuery(id+"F2.wireOp",EDGE,"E4.0.3.0"),sQuery(id+"F2.wireOp",EDGE,"E4.0.3.1"),sQuery(id+"F2.wireOp",EDGE,"E4.0.4.0"),sQuery(id+"F2.wireOp",EDGE,"E4.0.4.1"),sQuery(id+"F2.wireOp",EDGE,"E4.0.5.0"),sQuery(id+"F2.wireOp",EDGE,"E4.0.5.1"),sQuery(id+"F2.wireOp",EDGE,"E4.0.6.0"),sQuery(id+"F2.wireOp",EDGE,"E4.0.6.1"),sQuery(id+"F2.wireOp",EDGE,"E4.0.7.0"),sQuery(id+"F2.wireOp",EDGE,"E4.0.7.1"),sQuery(id+"F2.wireOp",EDGE,"E4.0.8.0"),sQuery(id+"F2.wireOp",EDGE,"E4.0.8.1"),sQuery(id+"F2.wireOp",EDGE,"E4.0.9.0"),sQuery(id+"F2.wireOp",EDGE,"E4.0.9.1"),sQuery(id+"F2.wireOp",EDGE,"E4.0.10.0"),sQuery(id+"F2.wireOp",EDGE,"E4.0.10.1"),sQuery(id+"F2.wireOp",EDGE,"E4.0.11.0"),sQuery(id+"F2.wireOp",EDGE,"E4.0.11.1"),sQuery(id+"F2.wireOp",EDGE,"E4.1.0.2"),sQuery(id+"F2.wireOp",EDGE,"E4.1.0.3"),sQuery(id+"F2.wireOp",EDGE,"E4.1.1.0"),sQuery(id+"F2.wireOp",EDGE,"E4.1.1.1"),sQuery(id+"F2.wireOp",EDGE,"E4.1.1.2"),sQuery(id+"F2.wireOp",EDGE,"E4.1.1.3"),sQuery(id+"F2.wireOp",EDGE,"E4.1.2.0"),sQuery(id+"F2.wireOp",EDGE,"E4.1.2.1"),sQuery(id+"F2.wireOp",EDGE,"E4.1.2.2"),sQuery(id+"F2.wireOp",EDGE,"E4.1.2.3"),sQuery(id+"F2.wireOp",EDGE,"E4.1.3.0"),sQuery(id+"F2.wireOp",EDGE,"E4.1.3.1"),sQuery(id+"F2.wireOp",EDGE,"E4.1.3.2"),sQuery(id+"F2.wireOp",EDGE,"E4.1.3.3"),sQuery(id+"F2.wireOp",EDGE,"E4.1.4.0"),sQuery(id+"F2.wireOp",EDGE,"E4.1.4.1"),sQuery(id+"F2.wireOp",EDGE,"E4.1.4.2"),sQuery(id+"F2.wireOp",EDGE,"E4.1.4.3"),sQuery(id+"F2.wireOp",EDGE,"E4.1.5.0"),sQuery(id+"F2.wireOp",EDGE,"E4.1.5.1"),sQuery(id+"F2.wireOp",EDGE,"E4.1.5.2"),sQuery(id+"F2.wireOp",EDGE,"E4.1.5.3"),sQuery(id+"F2.wireOp",EDGE,"E4.1.6.0"),sQuery(id+"F2.wireOp",EDGE,"E4.1.6.1"),sQuery(id+"F2.wireOp",EDGE,"E4.1.6.2"),sQuery(id+"F2.wireOp",EDGE,"E4.1.6.3"),sQuery(id+"F2.wireOp",EDGE,"E4.1.7.0"),sQuery(id+"F2.wireOp",EDGE,"E4.1.7.1"),sQuery(id+"F2.wireOp",EDGE,"E4.1.7.2"),sQuery(id+"F2.wireOp",EDGE,"E4.1.7.3"),sQuery(id+"F2.wireOp",EDGE,"E4.1.8.0"),sQuery(id+"F2.wireOp",EDGE,"E4.1.8.1"),sQuery(id+"F2.wireOp",EDGE,"E4.1.8.2"),sQuery(id+"F2.wireOp",EDGE,"E4.1.8.3"),sQuery(id+"F2.wireOp",EDGE,"E4.1.9.0"),sQuery(id+"F2.wireOp",EDGE,"E4.1.9.1"),sQuery(id+"F2.wireOp",EDGE,"E4.1.9.2"),sQuery(id+"F2.wireOp",EDGE,"E4.1.9.3"),sQuery(id+"F2.wireOp",EDGE,"E4.1.10.0"),sQuery(id+"F2.wireOp",EDGE,"E4.1.10.1"),sQuery(id+"F2.wireOp",EDGE,"E4.1.10.2"),sQuery(id+"F2.wireOp",EDGE,"E4.1.10.3"),sQuery(id+"F2.wireOp",EDGE,"E4.1.11.0"),sQuery(id+"F2.wireOp",EDGE,"E4.1.11.1"),sQuery(id+"F2.wireOp",EDGE,"E4.1.11.2"),sQuery(id+"F2.wireOp",EDGE,"E4.1.11.3"),sQuery(id+"F2.wireOp",EDGE,"E4.1.12.2"),sQuery(id+"F2.wireOp",EDGE,"E4.1.12.3"),sQuery(id+"F2.wireOp",EDGE,"E4.2.0.2"),sQuery(id+"F2.wireOp",EDGE,"E4.2.0.3"),sQuery(id+"F2.wireOp",EDGE,"E4.2.1.0"),sQuery(id+"F2.wireOp",EDGE,"E4.2.1.1"),sQuery(id+"F2.wireOp",EDGE,"E4.2.1.2"),sQuery(id+"F2.wireOp",EDGE,"E4.2.1.3"),sQuery(id+"F2.wireOp",EDGE,"E4.2.2.0"),sQuery(id+"F2.wireOp",EDGE,"E4.2.2.1"),sQuery(id+"F2.wireOp",EDGE,"E4.2.2.2"),sQuery(id+"F2.wireOp",EDGE,"E4.2.2.3"),sQuery(id+"F2.wireOp",EDGE,"E4.2.3.0"),sQuery(id+"F2.wireOp",EDGE,"E4.2.3.1"),sQuery(id+"F2.wireOp",EDGE,"E4.2.3.2"),sQuery(id+"F2.wireOp",EDGE,"E4.2.3.3"),sQuery(id+"F2.wireOp",EDGE,"E4.2.4.0"),sQuery(id+"F2.wireOp",EDGE,"E4.2.4.1"),sQuery(id+"F2.wireOp",EDGE,"E4.2.4.2"),sQuery(id+"F2.wireOp",EDGE,"E4.2.4.3"),sQuery(id+"F2.wireOp",EDGE,"E4.2.5.0"),sQuery(id+"F2.wireOp",EDGE,"E4.2.5.1"),sQuery(id+"F2.wireOp",EDGE,"E4.2.5.2"),sQuery(id+"F2.wireOp",EDGE,"E4.2.5.3"),sQuery(id+"F2.wireOp",EDGE,"E4.2.6.0"),sQuery(id+"F2.wireOp",EDGE,"E4.2.6.1"),sQuery(id+"F2.wireOp",EDGE,"E4.2.6.2"),sQuery(id+"F2.wireOp",EDGE,"E4.2.6.3"),sQuery(id+"F2.wireOp",EDGE,"E4.2.7.0"),sQuery(id+"F2.wireOp",EDGE,"E4.2.7.1"),sQuery(id+"F2.wireOp",EDGE,"E4.2.7.2"),sQuery(id+"F2.wireOp",EDGE,"E4.2.7.3"),sQuery(id+"F2.wireOp",EDGE,"E4.2.8.0"),sQuery(id+"F2.wireOp",EDGE,"E4.2.8.1"),sQuery(id+"F2.wireOp",EDGE,"E4.2.8.2"),sQuery(id+"F2.wireOp",EDGE,"E4.2.8.3"),sQuery(id+"F2.wireOp",EDGE,"E4.2.9.0"),sQuery(id+"F2.wireOp",EDGE,"E4.2.9.1"),sQuery(id+"F2.wireOp",EDGE,"E4.2.9.2"),sQuery(id+"F2.wireOp",EDGE,"E4.2.9.3"),sQuery(id+"F2.wireOp",EDGE,"E4.2.10.0"),sQuery(id+"F2.wireOp",EDGE,"E4.2.10.1"),sQuery(id+"F2.wireOp",EDGE,"E4.2.10.2"),sQuery(id+"F2.wireOp",EDGE,"E4.2.10.3"),sQuery(id+"F2.wireOp",EDGE,"E4.2.11.0"),sQuery(id+"F2.wireOp",EDGE,"E4.2.11.1"),sQuery(id+"F2.wireOp",EDGE,"E4.2.11.2"),sQuery(id+"F2.wireOp",EDGE,"E4.2.11.3"),sQuery(id+"F2.wireOp",EDGE,"E4.2.12.2"),sQuery(id+"F2.wireOp",EDGE,"E4.2.12.3"),sQuery(id+"F2.wireOp",EDGE,"E4.3.0.2"),sQuery(id+"F2.wireOp",EDGE,"E4.3.0.3"),sQuery(id+"F2.wireOp",EDGE,"E4.3.1.0"),sQuery(id+"F2.wireOp",EDGE,"E4.3.1.1"),sQuery(id+"F2.wireOp",EDGE,"E4.3.1.2"),sQuery(id+"F2.wireOp",EDGE,"E4.3.1.3"),sQuery(id+"F2.wireOp",EDGE,"E4.3.2.0"),sQuery(id+"F2.wireOp",EDGE,"E4.3.2.1"),sQuery(id+"F2.wireOp",EDGE,"E4.3.2.2"),sQuery(id+"F2.wireOp",EDGE,"E4.3.2.3"),sQuery(id+"F2.wireOp",EDGE,"E4.3.3.0"),sQuery(id+"F2.wireOp",EDGE,"E4.3.3.1"),sQuery(id+"F2.wireOp",EDGE,"E4.3.3.2"),sQuery(id+"F2.wireOp",EDGE,"E4.3.3.3"),sQuery(id+"F2.wireOp",EDGE,"E4.3.4.0"),sQuery(id+"F2.wireOp",EDGE,"E4.3.4.1"),sQuery(id+"F2.wireOp",EDGE,"E4.3.4.2"),sQuery(id+"F2.wireOp",EDGE,"E4.3.4.3"),sQuery(id+"F2.wireOp",EDGE,"E4.3.5.0"),sQuery(id+"F2.wireOp",EDGE,"E4.3.5.1"),sQuery(id+"F2.wireOp",EDGE,"E4.3.5.2"),sQuery(id+"F2.wireOp",EDGE,"E4.3.5.3"),sQuery(id+"F2.wireOp",EDGE,"E4.3.6.0"),sQuery(id+"F2.wireOp",EDGE,"E4.3.6.1"),sQuery(id+"F2.wireOp",EDGE,"E4.3.6.2"),sQuery(id+"F2.wireOp",EDGE,"E4.3.6.3"),sQuery(id+"F2.wireOp",EDGE,"E4.3.7.0"),sQuery(id+"F2.wireOp",EDGE,"E4.3.7.1"),sQuery(id+"F2.wireOp",EDGE,"E4.3.7.2"),sQuery(id+"F2.wireOp",EDGE,"E4.3.7.3"),sQuery(id+"F2.wireOp",EDGE,"E4.3.8.0"),sQuery(id+"F2.wireOp",EDGE,"E4.3.8.1"),sQuery(id+"F2.wireOp",EDGE,"E4.3.8.2"),sQuery(id+"F2.wireOp",EDGE,"E4.3.8.3"),sQuery(id+"F2.wireOp",EDGE,"E4.3.9.0"),sQuery(id+"F2.wireOp",EDGE,"E4.3.9.1"),sQuery(id+"F2.wireOp",EDGE,"E4.3.9.2"),sQuery(id+"F2.wireOp",EDGE,"E4.3.9.3"),sQuery(id+"F2.wireOp",EDGE,"E4.3.10.0"),sQuery(id+"F2.wireOp",EDGE,"E4.3.10.1"),sQuery(id+"F2.wireOp",EDGE,"E4.3.10.2"),sQuery(id+"F2.wireOp",EDGE,"E4.3.10.3"),sQuery(id+"F2.wireOp",EDGE,"E4.3.11.0"),sQuery(id+"F2.wireOp",EDGE,"E4.3.11.1"),sQuery(id+"F2.wireOp",EDGE,"E4.3.11.2"),sQuery(id+"F2.wireOp",EDGE,"E4.3.11.3"),sQuery(id+"F2.wireOp",EDGE,"E4.3.12.2"),sQuery(id+"F2.wireOp",EDGE,"E4.3.12.3"),sQuery(id+"F2.wireOp",EDGE,"E4.4.0.2"),sQuery(id+"F2.wireOp",EDGE,"E4.4.0.3"),sQuery(id+"F2.wireOp",EDGE,"E4.4.1.0"),sQuery(id+"F2.wireOp",EDGE,"E4.4.1.1"),sQuery(id+"F2.wireOp",EDGE,"E4.4.1.2"),sQuery(id+"F2.wireOp",EDGE,"E4.4.1.3"),sQuery(id+"F2.wireOp",EDGE,"E4.4.2.0"),sQuery(id+"F2.wireOp",EDGE,"E4.4.2.1"),sQuery(id+"F2.wireOp",EDGE,"E4.4.2.2"),sQuery(id+"F2.wireOp",EDGE,"E4.4.2.3"),sQuery(id+"F2.wireOp",EDGE,"E4.4.3.0"),sQuery(id+"F2.wireOp",EDGE,"E4.4.3.1"),sQuery(id+"F2.wireOp",EDGE,"E4.4.3.2"),sQuery(id+"F2.wireOp",EDGE,"E4.4.3.3"),sQuery(id+"F2.wireOp",EDGE,"E4.4.4.0"),sQuery(id+"F2.wireOp",EDGE,"E4.4.4.1"),sQuery(id+"F2.wireOp",EDGE,"E4.4.4.2"),sQuery(id+"F2.wireOp",EDGE,"E4.4.4.3"),sQuery(id+"F2.wireOp",EDGE,"E4.4.5.0"),sQuery(id+"F2.wireOp",EDGE,"E4.4.5.1"),sQuery(id+"F2.wireOp",EDGE,"E4.4.5.2"),sQuery(id+"F2.wireOp",EDGE,"E4.4.5.3"),sQuery(id+"F2.wireOp",EDGE,"E4.4.6.0"),sQuery(id+"F2.wireOp",EDGE,"E4.4.6.1"),sQuery(id+"F2.wireOp",EDGE,"E4.4.6.2"),sQuery(id+"F2.wireOp",EDGE,"E4.4.6.3"),sQuery(id+"F2.wireOp",EDGE,"E4.4.7.0"),sQuery(id+"F2.wireOp",EDGE,"E4.4.7.1"),sQuery(id+"F2.wireOp",EDGE,"E4.4.7.2"),sQuery(id+"F2.wireOp",EDGE,"E4.4.7.3"),sQuery(id+"F2.wireOp",EDGE,"E4.4.8.0"),sQuery(id+"F2.wireOp",EDGE,"E4.4.8.1"),sQuery(id+"F2.wireOp",EDGE,"E4.4.8.2"),sQuery(id+"F2.wireOp",EDGE,"E4.4.8.3"),sQuery(id+"F2.wireOp",EDGE,"E4.4.9.0"),sQuery(id+"F2.wireOp",EDGE,"E4.4.9.1"),sQuery(id+"F2.wireOp",EDGE,"E4.4.9.2"),sQuery(id+"F2.wireOp",EDGE,"E4.4.9.3"),sQuery(id+"F2.wireOp",EDGE,"E4.4.10.0"),sQuery(id+"F2.wireOp",EDGE,"E4.4.10.1"),sQuery(id+"F2.wireOp",EDGE,"E4.4.10.2"),sQuery(id+"F2.wireOp",EDGE,"E4.4.10.3"),sQuery(id+"F2.wireOp",EDGE,"E4.4.11.0"),sQuery(id+"F2.wireOp",EDGE,"E4.4.11.1"),sQuery(id+"F2.wireOp",EDGE,"E4.4.11.2"),sQuery(id+"F2.wireOp",EDGE,"E4.4.11.3"),sQuery(id+"F2.wireOp",EDGE,"E4.4.12.2"),sQuery(id+"F2.wireOp",EDGE,"E4.4.12.3"),sQuery(id+"F2.wireOp",EDGE,"E4.5.0.2"),sQuery(id+"F2.wireOp",EDGE,"E4.5.0.3"),sQuery(id+"F2.wireOp",EDGE,"E4.5.1.0"),sQuery(id+"F2.wireOp",EDGE,"E4.5.1.1"),sQuery(id+"F2.wireOp",EDGE,"E4.5.1.2"),sQuery(id+"F2.wireOp",EDGE,"E4.5.1.3"),sQuery(id+"F2.wireOp",EDGE,"E4.5.2.0"),sQuery(id+"F2.wireOp",EDGE,"E4.5.2.1"),sQuery(id+"F2.wireOp",EDGE,"E4.5.2.2"),sQuery(id+"F2.wireOp",EDGE,"E4.5.2.3"),sQuery(id+"F2.wireOp",EDGE,"E4.5.3.0"),sQuery(id+"F2.wireOp",EDGE,"E4.5.3.1"),sQuery(id+"F2.wireOp",EDGE,"E4.5.3.2"),sQuery(id+"F2.wireOp",EDGE,"E4.5.3.3"),sQuery(id+"F2.wireOp",EDGE,"E4.5.4.0"),sQuery(id+"F2.wireOp",EDGE,"E4.5.4.1"),sQuery(id+"F2.wireOp",EDGE,"E4.5.4.2"),sQuery(id+"F2.wireOp",EDGE,"E4.5.4.3"),sQuery(id+"F2.wireOp",EDGE,"E4.5.5.0"),sQuery(id+"F2.wireOp",EDGE,"E4.5.5.1"),sQuery(id+"F2.wireOp",EDGE,"E4.5.5.2"),sQuery(id+"F2.wireOp",EDGE,"E4.5.5.3"),sQuery(id+"F2.wireOp",EDGE,"E4.5.6.0"),sQuery(id+"F2.wireOp",EDGE,"E4.5.6.1"),sQuery(id+"F2.wireOp",EDGE,"E4.5.6.2"),sQuery(id+"F2.wireOp",EDGE,"E4.5.6.3"),sQuery(id+"F2.wireOp",EDGE,"E4.5.7.0"),sQuery(id+"F2.wireOp",EDGE,"E4.5.7.1"),sQuery(id+"F2.wireOp",EDGE,"E4.5.7.2"),sQuery(id+"F2.wireOp",EDGE,"E4.5.7.3"),sQuery(id+"F2.wireOp",EDGE,"E4.5.8.0"),sQuery(id+"F2.wireOp",EDGE,"E4.5.8.1"),sQuery(id+"F2.wireOp",EDGE,"E4.5.8.2"),sQuery(id+"F2.wireOp",EDGE,"E4.5.8.3"),sQuery(id+"F2.wireOp",EDGE,"E4.5.9.0"),sQuery(id+"F2.wireOp",EDGE,"E4.5.9.1"),sQuery(id+"F2.wireOp",EDGE,"E4.5.9.2"),sQuery(id+"F2.wireOp",EDGE,"E4.5.9.3"),sQuery(id+"F2.wireOp",EDGE,"E4.5.10.0"),sQuery(id+"F2.wireOp",EDGE,"E4.5.10.1"),sQuery(id+"F2.wireOp",EDGE,"E4.5.10.2"),sQuery(id+"F2.wireOp",EDGE,"E4.5.10.3"),sQuery(id+"F2.wireOp",EDGE,"E4.5.11.0"),sQuery(id+"F2.wireOp",EDGE,"E4.5.11.1"),sQuery(id+"F2.wireOp",EDGE,"E4.5.11.2"),sQuery(id+"F2.wireOp",EDGE,"E4.5.11.3"),sQuery(id+"F2.wireOp",EDGE,"E4.5.12.2"),sQuery(id+"F2.wireOp",EDGE,"E4.5.12.3"),sQuery(id+"F2.wireOp",EDGE,"E4.6.0.2"),sQuery(id+"F2.wireOp",EDGE,"E4.6.0.3"),sQuery(id+"F2.wireOp",EDGE,"E4.6.1.0"),sQuery(id+"F2.wireOp",EDGE,"E4.6.1.1"),sQuery(id+"F2.wireOp",EDGE,"E4.6.1.2"),sQuery(id+"F2.wireOp",EDGE,"E4.6.1.3"),sQuery(id+"F2.wireOp",EDGE,"E4.6.2.0"),sQuery(id+"F2.wireOp",EDGE,"E4.6.2.1"),sQuery(id+"F2.wireOp",EDGE,"E4.6.2.2"),sQuery(id+"F2.wireOp",EDGE,"E4.6.2.3"),sQuery(id+"F2.wireOp",EDGE,"E4.6.3.0"),sQuery(id+"F2.wireOp",EDGE,"E4.6.3.1"),sQuery(id+"F2.wireOp",EDGE,"E4.6.3.2"),sQuery(id+"F2.wireOp",EDGE,"E4.6.3.3"),sQuery(id+"F2.wireOp",EDGE,"E4.6.4.0"),sQuery(id+"F2.wireOp",EDGE,"E4.6.4.1"),sQuery(id+"F2.wireOp",EDGE,"E4.6.4.2"),sQuery(id+"F2.wireOp",EDGE,"E4.6.4.3"),sQuery(id+"F2.wireOp",EDGE,"E4.6.5.0"),sQuery(id+"F2.wireOp",EDGE,"E4.6.5.1"),sQuery(id+"F2.wireOp",EDGE,"E4.6.5.2"),sQuery(id+"F2.wireOp",EDGE,"E4.6.5.3"),sQuery(id+"F2.wireOp",EDGE,"E4.6.6.0"),sQuery(id+"F2.wireOp",EDGE,"E4.6.6.1"),sQuery(id+"F2.wireOp",EDGE,"E4.6.6.2"),sQuery(id+"F2.wireOp",EDGE,"E4.6.6.3"),sQuery(id+"F2.wireOp",EDGE,"E4.6.7.0"),sQuery(id+"F2.wireOp",EDGE,"E4.6.7.1"),sQuery(id+"F2.wireOp",EDGE,"E4.6.7.2"),sQuery(id+"F2.wireOp",EDGE,"E4.6.7.3"),sQuery(id+"F2.wireOp",EDGE,"E4.6.8.0"),sQuery(id+"F2.wireOp",EDGE,"E4.6.8.1"),sQuery(id+"F2.wireOp",EDGE,"E4.6.8.2"),sQuery(id+"F2.wireOp",EDGE,"E4.6.8.3"),sQuery(id+"F2.wireOp",EDGE,"E4.6.9.0"),sQuery(id+"F2.wireOp",EDGE,"E4.6.9.1"),sQuery(id+"F2.wireOp",EDGE,"E4.6.9.2"),sQuery(id+"F2.wireOp",EDGE,"E4.6.9.3"),sQuery(id+"F2.wireOp",EDGE,"E4.6.10.0"),sQuery(id+"F2.wireOp",EDGE,"E4.6.10.1"),sQuery(id+"F2.wireOp",EDGE,"E4.6.10.2"),sQuery(id+"F2.wireOp",EDGE,"E4.6.10.3"),sQuery(id+"F2.wireOp",EDGE,"E4.6.11.0"),sQuery(id+"F2.wireOp",EDGE,"E4.6.11.1"),sQuery(id+"F2.wireOp",EDGE,"E4.6.11.2"),sQuery(id+"F2.wireOp",EDGE,"E4.6.11.3"),sQuery(id+"F2.wireOp",EDGE,"E4.6.12.2"),sQuery(id+"F2.wireOp",EDGE,"E4.6.12.3"),sQuery(id+"F2.wireOp",EDGE,"E4.7.0.2"),sQuery(id+"F2.wireOp",EDGE,"E4.7.0.3"),sQuery(id+"F2.wireOp",EDGE,"E4.7.1.0"),sQuery(id+"F2.wireOp",EDGE,"E4.7.1.1"),sQuery(id+"F2.wireOp",EDGE,"E4.7.1.2"),sQuery(id+"F2.wireOp",EDGE,"E4.7.1.3"),sQuery(id+"F2.wireOp",EDGE,"E4.7.2.0"),sQuery(id+"F2.wireOp",EDGE,"E4.7.2.1"),sQuery(id+"F2.wireOp",EDGE,"E4.7.2.2"),sQuery(id+"F2.wireOp",EDGE,"E4.7.2.3"),sQuery(id+"F2.wireOp",EDGE,"E4.7.3.0"),sQuery(id+"F2.wireOp",EDGE,"E4.7.3.1"),sQuery(id+"F2.wireOp",EDGE,"E4.7.3.2"),sQuery(id+"F2.wireOp",EDGE,"E4.7.3.3"),sQuery(id+"F2.wireOp",EDGE,"E4.7.4.0"),sQuery(id+"F2.wireOp",EDGE,"E4.7.4.1"),sQuery(id+"F2.wireOp",EDGE,"E4.7.4.2"),sQuery(id+"F2.wireOp",EDGE,"E4.7.4.3"),sQuery(id+"F2.wireOp",EDGE,"E4.7.5.0"),sQuery(id+"F2.wireOp",EDGE,"E4.7.5.1"),sQuery(id+"F2.wireOp",EDGE,"E4.7.5.2"),sQuery(id+"F2.wireOp",EDGE,"E4.7.5.3"),sQuery(id+"F2.wireOp",EDGE,"E4.7.6.0"),sQuery(id+"F2.wireOp",EDGE,"E4.7.6.1"),sQuery(id+"F2.wireOp",EDGE,"E4.7.6.2"),sQuery(id+"F2.wireOp",EDGE,"E4.7.6.3"),sQuery(id+"F2.wireOp",EDGE,"E4.7.7.0"),sQuery(id+"F2.wireOp",EDGE,"E4.7.7.1"),sQuery(id+"F2.wireOp",EDGE,"E4.7.7.2"),sQuery(id+"F2.wireOp",EDGE,"E4.7.7.3"),sQuery(id+"F2.wireOp",EDGE,"E4.7.8.0"),sQuery(id+"F2.wireOp",EDGE,"E4.7.8.1"),sQuery(id+"F2.wireOp",EDGE,"E4.7.8.2"),sQuery(id+"F2.wireOp",EDGE,"E4.7.8.3"),sQuery(id+"F2.wireOp",EDGE,"E4.7.9.0"),sQuery(id+"F2.wireOp",EDGE,"E4.7.9.1"),sQuery(id+"F2.wireOp",EDGE,"E4.7.9.2"),sQuery(id+"F2.wireOp",EDGE,"E4.7.9.3"),sQuery(id+"F2.wireOp",EDGE,"E4.7.10.0"),sQuery(id+"F2.wireOp",EDGE,"E4.7.10.1"),sQuery(id+"F2.wireOp",EDGE,"E4.7.10.2"),sQuery(id+"F2.wireOp",EDGE,"E4.7.10.3"),sQuery(id+"F2.wireOp",EDGE,"E4.7.11.0"),sQuery(id+"F2.wireOp",EDGE,"E4.7.11.1"),sQuery(id+"F2.wireOp",EDGE,"E4.7.11.2"),sQuery(id+"F2.wireOp",EDGE,"E4.7.11.3"),sQuery(id+"F2.wireOp",EDGE,"E4.7.12.2"),sQuery(id+"F2.wireOp",EDGE,"E4.7.12.3"),sQuery(id+"F2.wireOp",EDGE,"E4.8.0.2"),sQuery(id+"F2.wireOp",EDGE,"E4.8.0.3"),sQuery(id+"F2.wireOp",EDGE,"E4.8.1.0"),sQuery(id+"F2.wireOp",EDGE,"E4.8.1.1"),sQuery(id+"F2.wireOp",EDGE,"E4.8.1.2"),sQuery(id+"F2.wireOp",EDGE,"E4.8.1.3"),sQuery(id+"F2.wireOp",EDGE,"E4.8.2.0"),sQuery(id+"F2.wireOp",EDGE,"E4.8.2.1"),sQuery(id+"F2.wireOp",EDGE,"E4.8.2.2"),sQuery(id+"F2.wireOp",EDGE,"E4.8.2.3"),sQuery(id+"F2.wireOp",EDGE,"E4.8.3.0"),sQuery(id+"F2.wireOp",EDGE,"E4.8.3.1"),sQuery(id+"F2.wireOp",EDGE,"E4.8.3.2"),sQuery(id+"F2.wireOp",EDGE,"E4.8.3.3"),sQuery(id+"F2.wireOp",EDGE,"E4.8.4.0"),sQuery(id+"F2.wireOp",EDGE,"E4.8.4.1"),sQuery(id+"F2.wireOp",EDGE,"E4.8.4.2"),sQuery(id+"F2.wireOp",EDGE,"E4.8.4.3"),sQuery(id+"F2.wireOp",EDGE,"E4.8.5.0"),sQuery(id+"F2.wireOp",EDGE,"E4.8.5.1"),sQuery(id+"F2.wireOp",EDGE,"E4.8.5.2"),sQuery(id+"F2.wireOp",EDGE,"E4.8.5.3"),sQuery(id+"F2.wireOp",EDGE,"E4.8.6.0"),sQuery(id+"F2.wireOp",EDGE,"E4.8.6.1"),sQuery(id+"F2.wireOp",EDGE,"E4.8.6.2"),sQuery(id+"F2.wireOp",EDGE,"E4.8.6.3"),sQuery(id+"F2.wireOp",EDGE,"E4.8.7.0"),sQuery(id+"F2.wireOp",EDGE,"E4.8.7.1"),sQuery(id+"F2.wireOp",EDGE,"E4.8.7.2"),sQuery(id+"F2.wireOp",EDGE,"E4.8.7.3"),sQuery(id+"F2.wireOp",EDGE,"E4.8.8.0"),sQuery(id+"F2.wireOp",EDGE,"E4.8.8.1"),sQuery(id+"F2.wireOp",EDGE,"E4.8.8.2"),sQuery(id+"F2.wireOp",EDGE,"E4.8.8.3"),sQuery(id+"F2.wireOp",EDGE,"E4.8.9.0"),sQuery(id+"F2.wireOp",EDGE,"E4.8.9.1"),sQuery(id+"F2.wireOp",EDGE,"E4.8.9.2"),sQuery(id+"F2.wireOp",EDGE,"E4.8.9.3"),sQuery(id+"F2.wireOp",EDGE,"E4.8.10.0"),sQuery(id+"F2.wireOp",EDGE,"E4.8.10.1"),sQuery(id+"F2.wireOp",EDGE,"E4.8.10.2"),sQuery(id+"F2.wireOp",EDGE,"E4.8.10.3"),sQuery(id+"F2.wireOp",EDGE,"E4.8.11.0"),sQuery(id+"F2.wireOp",EDGE,"E4.8.11.1"),sQuery(id+"F2.wireOp",EDGE,"E4.8.11.2"),sQuery(id+"F2.wireOp",EDGE,"E4.8.11.3"),sQuery(id+"F2.wireOp",EDGE,"E4.8.12.2"),sQuery(id+"F2.wireOp",EDGE,"E4.8.12.3"),sQuery(id+"F2.wireOp",EDGE,"E4.9.0.2"),sQuery(id+"F2.wireOp",EDGE,"E4.9.0.3"),sQuery(id+"F2.wireOp",EDGE,"E4.9.1.0"),sQuery(id+"F2.wireOp",EDGE,"E4.9.1.1"),sQuery(id+"F2.wireOp",EDGE,"E4.9.1.2"),sQuery(id+"F2.wireOp",EDGE,"E4.9.1.3"),sQuery(id+"F2.wireOp",EDGE,"E4.9.2.0"),sQuery(id+"F2.wireOp",EDGE,"E4.9.2.1"),sQuery(id+"F2.wireOp",EDGE,"E4.9.2.2"),sQuery(id+"F2.wireOp",EDGE,"E4.9.2.3"),sQuery(id+"F2.wireOp",EDGE,"E4.9.3.0"),sQuery(id+"F2.wireOp",EDGE,"E4.9.3.1"),sQuery(id+"F2.wireOp",EDGE,"E4.9.3.2"),sQuery(id+"F2.wireOp",EDGE,"E4.9.3.3"),sQuery(id+"F2.wireOp",EDGE,"E4.9.4.0"),sQuery(id+"F2.wireOp",EDGE,"E4.9.4.1"),sQuery(id+"F2.wireOp",EDGE,"E4.9.4.2"),sQuery(id+"F2.wireOp",EDGE,"E4.9.4.3"),sQuery(id+"F2.wireOp",EDGE,"E4.9.5.0"),sQuery(id+"F2.wireOp",EDGE,"E4.9.5.1"),sQuery(id+"F2.wireOp",EDGE,"E4.9.5.2"),sQuery(id+"F2.wireOp",EDGE,"E4.9.5.3"),sQuery(id+"F2.wireOp",EDGE,"E4.9.6.0"),sQuery(id+"F2.wireOp",EDGE,"E4.9.6.1"),sQuery(id+"F2.wireOp",EDGE,"E4.9.6.2"),sQuery(id+"F2.wireOp",EDGE,"E4.9.6.3"),sQuery(id+"F2.wireOp",EDGE,"E4.9.7.0"),sQuery(id+"F2.wireOp",EDGE,"E4.9.7.1"),sQuery(id+"F2.wireOp",EDGE,"E4.9.7.2"),sQuery(id+"F2.wireOp",EDGE,"E4.9.7.3"),sQuery(id+"F2.wireOp",EDGE,"E4.9.8.0"),sQuery(id+"F2.wireOp",EDGE,"E4.9.8.1"),sQuery(id+"F2.wireOp",EDGE,"E4.9.8.2"),sQuery(id+"F2.wireOp",EDGE,"E4.9.8.3"),sQuery(id+"F2.wireOp",EDGE,"E4.9.9.0"),sQuery(id+"F2.wireOp",EDGE,"E4.9.9.1"),sQuery(id+"F2.wireOp",EDGE,"E4.9.9.2"),sQuery(id+"F2.wireOp",EDGE,"E4.9.9.3"),sQuery(id+"F2.wireOp",EDGE,"E4.9.10.0"),sQuery(id+"F2.wireOp",EDGE,"E4.9.10.1"),sQuery(id+"F2.wireOp",EDGE,"E4.9.10.2"),sQuery(id+"F2.wireOp",EDGE,"E4.9.10.3"),sQuery(id+"F2.wireOp",EDGE,"E4.9.11.0"),sQuery(id+"F2.wireOp",EDGE,"E4.9.11.1"),sQuery(id+"F2.wireOp",EDGE,"E4.9.11.2"),sQuery(id+"F2.wireOp",EDGE,"E4.9.11.3"),sQuery(id+"F2.wireOp",EDGE,"E4.9.12.2"),sQuery(id+"F2.wireOp",EDGE,"E4.9.12.3"),sQuery(id+"F2.wireOp",EDGE,"E4.10.0.2"),sQuery(id+"F2.wireOp",EDGE,"E4.10.0.3"),sQuery(id+"F2.wireOp",EDGE,"E4.10.1.0"),sQuery(id+"F2.wireOp",EDGE,"E4.10.1.1"),sQuery(id+"F2.wireOp",EDGE,"E4.10.1.2"),sQuery(id+"F2.wireOp",EDGE,"E4.10.1.3"),sQuery(id+"F2.wireOp",EDGE,"E4.10.2.0"),sQuery(id+"F2.wireOp",EDGE,"E4.10.2.1"),sQuery(id+"F2.wireOp",EDGE,"E4.10.2.2"),sQuery(id+"F2.wireOp",EDGE,"E4.10.2.3"),sQuery(id+"F2.wireOp",EDGE,"E4.10.3.0"),sQuery(id+"F2.wireOp",EDGE,"E4.10.3.1"),sQuery(id+"F2.wireOp",EDGE,"E4.10.3.2"),sQuery(id+"F2.wireOp",EDGE,"E4.10.3.3"),sQuery(id+"F2.wireOp",EDGE,"E4.10.4.0"),sQuery(id+"F2.wireOp",EDGE,"E4.10.4.1"),sQuery(id+"F2.wireOp",EDGE,"E4.10.4.2"),sQuery(id+"F2.wireOp",EDGE,"E4.10.4.3"),sQuery(id+"F2.wireOp",EDGE,"E4.10.5.0"),sQuery(id+"F2.wireOp",EDGE,"E4.10.5.1"),sQuery(id+"F2.wireOp",EDGE,"E4.10.5.2"),sQuery(id+"F2.wireOp",EDGE,"E4.10.5.3"),sQuery(id+"F2.wireOp",EDGE,"E4.10.6.0"),sQuery(id+"F2.wireOp",EDGE,"E4.10.6.1"),sQuery(id+"F2.wireOp",EDGE,"E4.10.6.2"),sQuery(id+"F2.wireOp",EDGE,"E4.10.6.3"),sQuery(id+"F2.wireOp",EDGE,"E4.10.7.0"),sQuery(id+"F2.wireOp",EDGE,"E4.10.7.1"),sQuery(id+"F2.wireOp",EDGE,"E4.10.7.2"),sQuery(id+"F2.wireOp",EDGE,"E4.10.7.3"),sQuery(id+"F2.wireOp",EDGE,"E4.10.8.0"),sQuery(id+"F2.wireOp",EDGE,"E4.10.8.1"),sQuery(id+"F2.wireOp",EDGE,"E4.10.8.2"),sQuery(id+"F2.wireOp",EDGE,"E4.10.8.3"),sQuery(id+"F2.wireOp",EDGE,"E4.10.9.0"),sQuery(id+"F2.wireOp",EDGE,"E4.10.9.1"),sQuery(id+"F2.wireOp",EDGE,"E4.10.9.2"),sQuery(id+"F2.wireOp",EDGE,"E4.10.9.3"),sQuery(id+"F2.wireOp",EDGE,"E4.10.10.0"),sQuery(id+"F2.wireOp",EDGE,"E4.10.10.1"),sQuery(id+"F2.wireOp",EDGE,"E4.10.10.2"),sQuery(id+"F2.wireOp",EDGE,"E4.10.10.3"),sQuery(id+"F2.wireOp",EDGE,"E4.10.11.0"),sQuery(id+"F2.wireOp",EDGE,"E4.10.11.1"),sQuery(id+"F2.wireOp",EDGE,"E4.10.11.2"),sQuery(id+"F2.wireOp",EDGE,"E4.10.11.3"),sQuery(id+"F2.wireOp",EDGE,"E4.10.12.2"),sQuery(id+"F2.wireOp",EDGE,"E4.10.12.3"),sQuery(id+"F2.wireOp",EDGE,"E4.11.0.2"),sQuery(id+"F2.wireOp",EDGE,"E4.11.0.3"),sQuery(id+"F2.wireOp",EDGE,"E4.11.1.0"),sQuery(id+"F2.wireOp",EDGE,"E4.11.1.1"),sQuery(id+"F2.wireOp",EDGE,"E4.11.1.2"),sQuery(id+"F2.wireOp",EDGE,"E4.11.1.3"),sQuery(id+"F2.wireOp",EDGE,"E4.11.2.0"),sQuery(id+"F2.wireOp",EDGE,"E4.11.2.1"),sQuery(id+"F2.wireOp",EDGE,"E4.11.2.2"),sQuery(id+"F2.wireOp",EDGE,"E4.11.2.3"),sQuery(id+"F2.wireOp",EDGE,"E4.11.3.0"),sQuery(id+"F2.wireOp",EDGE,"E4.11.3.1"),sQuery(id+"F2.wireOp",EDGE,"E4.11.3.2"),sQuery(id+"F2.wireOp",EDGE,"E4.11.3.3"),sQuery(id+"F2.wireOp",EDGE,"E4.11.4.0"),sQuery(id+"F2.wireOp",EDGE,"E4.11.4.1"),sQuery(id+"F2.wireOp",EDGE,"E4.11.4.2"),sQuery(id+"F2.wireOp",EDGE,"E4.11.4.3"),sQuery(id+"F2.wireOp",EDGE,"E4.11.5.0"),sQuery(id+"F2.wireOp",EDGE,"E4.11.5.1"),sQuery(id+"F2.wireOp",EDGE,"E4.11.5.2"),sQuery(id+"F2.wireOp",EDGE,"E4.11.5.3"),sQuery(id+"F2.wireOp",EDGE,"E4.11.6.0"),sQuery(id+"F2.wireOp",EDGE,"E4.11.6.1"),sQuery(id+"F2.wireOp",EDGE,"E4.11.6.2"),sQuery(id+"F2.wireOp",EDGE,"E4.11.6.3"),sQuery(id+"F2.wireOp",EDGE,"E4.11.7.0"),sQuery(id+"F2.wireOp",EDGE,"E4.11.7.1"),sQuery(id+"F2.wireOp",EDGE,"E4.11.7.2"),sQuery(id+"F2.wireOp",EDGE,"E4.11.7.3"),sQuery(id+"F2.wireOp",EDGE,"E4.11.8.0"),sQuery(id+"F2.wireOp",EDGE,"E4.11.8.1"),sQuery(id+"F2.wireOp",EDGE,"E4.11.8.2"),sQuery(id+"F2.wireOp",EDGE,"E4.11.8.3"),sQuery(id+"F2.wireOp",EDGE,"E4.11.9.0"),sQuery(id+"F2.wireOp",EDGE,"E4.11.9.1"),sQuery(id+"F2.wireOp",EDGE,"E4.11.9.2"),sQuery(id+"F2.wireOp",EDGE,"E4.11.9.3"),sQuery(id+"F2.wireOp",EDGE,"E4.11.10.0"),sQuery(id+"F2.wireOp",EDGE,"E4.11.10.1"),sQuery(id+"F2.wireOp",EDGE,"E4.11.10.2"),sQuery(id+"F2.wireOp",EDGE,"E4.11.10.3"),sQuery(id+"F2.wireOp",EDGE,"E4.11.11.0"),sQuery(id+"F2.wireOp",EDGE,"E4.11.11.1"),sQuery(id+"F2.wireOp",EDGE,"E4.11.11.2"),sQuery(id+"F2.wireOp",EDGE,"E4.11.11.3"),sQuery(id+"F2.wireOp",EDGE,"E4.11.12.2"),sQuery(id+"F2.wireOp",EDGE,"E4.11.12.3"),sQuery(id+"F2.wireOp",EDGE,"E4.12.1.0"),sQuery(id+"F2.wireOp",EDGE,"E4.12.1.1"),sQuery(id+"F2.wireOp",EDGE,"E4.12.2.0"),sQuery(id+"F2.wireOp",EDGE,"E4.12.2.1"),sQuery(id+"F2.wireOp",EDGE,"E4.12.3.0"),sQuery(id+"F2.wireOp",EDGE,"E4.12.3.1"),sQuery(id+"F2.wireOp",EDGE,"E4.12.4.0"),sQuery(id+"F2.wireOp",EDGE,"E4.12.4.1"),sQuery(id+"F2.wireOp",EDGE,"E4.12.5.0"),sQuery(id+"F2.wireOp",EDGE,"E4.12.5.1"),sQuery(id+"F2.wireOp",EDGE,"E4.12.6.0"),sQuery(id+"F2.wireOp",EDGE,"E4.12.6.1"),sQuery(id+"F2.wireOp",EDGE,"E4.12.7.0"),sQuery(id+"F2.wireOp",EDGE,"E4.12.7.1"),sQuery(id+"F2.wireOp",EDGE,"E4.12.8.0"),sQuery(id+"F2.wireOp",EDGE,"E4.12.8.1"),sQuery(id+"F2.wireOp",EDGE,"E4.12.9.0"),sQuery(id+"F2.wireOp",EDGE,"E4.12.9.1"),sQuery(id+"F2.wireOp",EDGE,"E4.12.10.0"),sQuery(id+"F2.wireOp",EDGE,"E4.12.10.1"),sQuery(id+"F2.wireOp",EDGE,"E4.12.11.0"),sQuery(id+"F2.wireOp",EDGE,"E4.12.11.1"),sQuery(id+"F2.wireOp",EDGE,"E5.bottom"),sQuery(id+"F2.wireOp",EDGE,"E5.top"),sQuery(id+"F2.wireOp",EDGE,"E5.left"),sQuery(id+"F2.wireOp",EDGE,"E5.right"),sQuery(id+"F2.wireOp",EDGE,"E6.bottom"),sQuery(id+"F2.wireOp",EDGE,"E6.top"),sQuery(id+"F2.wireOp",EDGE,"E6.left"),sQuery(id+"F2.wireOp",EDGE,"E6.right")])]});
            transform(context, id + "F7", {"entities" : qUnion([Q0]), "transformType" : TransformType.TRANSLATION_3D, "dx" : 0 * mm, "dy" : -96 * mm, "dz" : 0 * mm, "makeCopy" : true});
        }
        {
            var Q0;
            Q0=makeQuery(id+"F1.opExtrude","SWEPT_BODY",BODY,{"disambiguationData":[OSD([sQuery(id+"F0.wireOp",EDGE,"E1.0.1.4"),sQuery(id+"F0.wireOp",EDGE,"E1.0.1.8"),sQuery(id+"F0.wireOp",EDGE,"E1.0.1.10"),sQuery(id+"F0.wireOp",EDGE,"E1.0.2.4"),sQuery(id+"F0.wireOp",EDGE,"E1.0.2.8"),sQuery(id+"F0.wireOp",EDGE,"E1.0.2.10"),sQuery(id+"F0.wireOp",EDGE,"E1.0.3.4"),sQuery(id+"F0.wireOp",EDGE,"E1.0.3.8"),sQuery(id+"F0.wireOp",EDGE,"E1.0.3.10"),sQuery(id+"F0.wireOp",EDGE,"E1.0.4.4"),sQuery(id+"F0.wireOp",EDGE,"E1.0.4.8"),sQuery(id+"F0.wireOp",EDGE,"E1.0.4.10"),sQuery(id+"F0.wireOp",EDGE,"E1.0.5.4"),sQuery(id+"F0.wireOp",EDGE,"E1.0.5.8"),sQuery(id+"F0.wireOp",EDGE,"E1.0.5.10"),sQuery(id+"F0.wireOp",EDGE,"E1.0.6.4"),sQuery(id+"F0.wireOp",EDGE,"E1.0.6.8"),sQuery(id+"F0.wireOp",EDGE,"E1.0.6.10"),sQuery(id+"F0.wireOp",EDGE,"E1.0.7.4"),sQuery(id+"F0.wireOp",EDGE,"E1.0.7.8"),sQuery(id+"F0.wireOp",EDGE,"E1.0.7.10"),sQuery(id+"F0.wireOp",EDGE,"E1.0.8.4"),sQuery(id+"F0.wireOp",EDGE,"E1.0.8.8"),sQuery(id+"F0.wireOp",EDGE,"E1.0.8.10"),sQuery(id+"F0.wireOp",EDGE,"E1.0.9.4"),sQuery(id+"F0.wireOp",EDGE,"E1.0.9.8"),sQuery(id+"F0.wireOp",EDGE,"E1.0.9.10"),sQuery(id+"F0.wireOp",EDGE,"E1.0.10.4"),sQuery(id+"F0.wireOp",EDGE,"E1.0.10.8"),sQuery(id+"F0.wireOp",EDGE,"E1.0.10.10"),sQuery(id+"F0.wireOp",EDGE,"E1.0.11.4"),sQuery(id+"F0.wireOp",EDGE,"E1.0.11.8"),sQuery(id+"F0.wireOp",EDGE,"E1.0.11.10"),sQuery(id+"F0.wireOp",EDGE,"E1.1.0.4"),sQuery(id+"F0.wireOp",EDGE,"E1.1.0.6"),sQuery(id+"F0.wireOp",EDGE,"E1.1.0.8"),sQuery(id+"F0.wireOp",EDGE,"E1.1.1.4"),sQuery(id+"F0.wireOp",EDGE,"E1.1.1.6"),sQuery(id+"F0.wireOp",EDGE,"E1.1.1.8"),sQuery(id+"F0.wireOp",EDGE,"E1.1.1.10"),sQuery(id+"F0.wireOp",EDGE,"E1.1.2.4"),sQuery(id+"F0.wireOp",EDGE,"E1.1.2.6"),sQuery(id+"F0.wireOp",EDGE,"E1.1.2.8"),sQuery(id+"F0.wireOp",EDGE,"E1.1.2.10"),sQuery(id+"F0.wireOp",EDGE,"E1.1.3.4"),sQuery(id+"F0.wireOp",EDGE,"E1.1.3.6"),sQuery(id+"F0.wireOp",EDGE,"E1.1.3.8"),sQuery(id+"F0.wireOp",EDGE,"E1.1.3.10"),sQuery(id+"F0.wireOp",EDGE,"E1.1.4.4"),sQuery(id+"F0.wireOp",EDGE,"E1.1.4.6"),sQuery(id+"F0.wireOp",EDGE,"E1.1.4.8"),sQuery(id+"F0.wireOp",EDGE,"E1.1.4.10"),sQuery(id+"F0.wireOp",EDGE,"E1.1.5.4"),sQuery(id+"F0.wireOp",EDGE,"E1.1.5.6"),sQuery(id+"F0.wireOp",EDGE,"E1.1.5.8"),sQuery(id+"F0.wireOp",EDGE,"E1.1.5.10"),sQuery(id+"F0.wireOp",EDGE,"E1.1.6.4"),sQuery(id+"F0.wireOp",EDGE,"E1.1.6.6"),sQuery(id+"F0.wireOp",EDGE,"E1.1.6.8"),sQuery(id+"F0.wireOp",EDGE,"E1.1.6.10"),sQuery(id+"F0.wireOp",EDGE,"E1.1.7.4"),sQuery(id+"F0.wireOp",EDGE,"E1.1.7.6"),sQuery(id+"F0.wireOp",EDGE,"E1.1.7.8"),sQuery(id+"F0.wireOp",EDGE,"E1.1.7.10"),sQuery(id+"F0.wireOp",EDGE,"E1.1.8.4"),sQuery(id+"F0.wireOp",EDGE,"E1.1.8.6"),sQuery(id+"F0.wireOp",EDGE,"E1.1.8.8"),sQuery(id+"F0.wireOp",EDGE,"E1.1.8.10"),sQuery(id+"F0.wireOp",EDGE,"E1.1.9.4"),sQuery(id+"F0.wireOp",EDGE,"E1.1.9.6"),sQuery(id+"F0.wireOp",EDGE,"E1.1.9.8"),sQuery(id+"F0.wireOp",EDGE,"E1.1.9.10"),sQuery(id+"F0.wireOp",EDGE,"E1.1.10.4"),sQuery(id+"F0.wireOp",EDGE,"E1.1.10.6"),sQuery(id+"F0.wireOp",EDGE,"E1.1.10.8"),sQuery(id+"F0.wireOp",EDGE,"E1.1.10.10"),sQuery(id+"F0.wireOp",EDGE,"E1.1.11.4"),sQuery(id+"F0.wireOp",EDGE,"E1.1.11.6"),sQuery(id+"F0.wireOp",EDGE,"E1.1.11.8"),sQuery(id+"F0.wireOp",EDGE,"E1.1.11.10"),sQuery(id+"F0.wireOp",EDGE,"E1.1.12.4"),sQuery(id+"F0.wireOp",EDGE,"E1.1.12.6"),sQuery(id+"F0.wireOp",EDGE,"E1.1.12.10"),sQuery(id+"F0.wireOp",EDGE,"E1.2.0.4"),sQuery(id+"F0.wireOp",EDGE,"E1.2.0.6"),sQuery(id+"F0.wireOp",EDGE,"E1.2.0.8"),sQuery(id+"F0.wireOp",EDGE,"E1.2.1.4"),sQuery(id+"F0.wireOp",EDGE,"E1.2.1.6"),sQuery(id+"F0.wireOp",EDGE,"E1.2.1.8"),sQuery(id+"F0.wireOp",EDGE,"E1.2.1.10"),sQuery(id+"F0.wireOp",EDGE,"E1.2.2.4"),sQuery(id+"F0.wireOp",EDGE,"E1.2.2.6"),sQuery(id+"F0.wireOp",EDGE,"E1.2.2.8"),sQuery(id+"F0.wireOp",EDGE,"E1.2.2.10"),sQuery(id+"F0.wireOp",EDGE,"E1.2.3.4"),sQuery(id+"F0.wireOp",EDGE,"E1.2.3.6"),sQuery(id+"F0.wireOp",EDGE,"E1.2.3.8"),sQuery(id+"F0.wireOp",EDGE,"E1.2.3.10"),sQuery(id+"F0.wireOp",EDGE,"E1.2.4.4"),sQuery(id+"F0.wireOp",EDGE,"E1.2.4.6"),sQuery(id+"F0.wireOp",EDGE,"E1.2.4.8"),sQuery(id+"F0.wireOp",EDGE,"E1.2.4.10"),sQuery(id+"F0.wireOp",EDGE,"E1.2.5.4"),sQuery(id+"F0.wireOp",EDGE,"E1.2.5.6"),sQuery(id+"F0.wireOp",EDGE,"E1.2.5.8"),sQuery(id+"F0.wireOp",EDGE,"E1.2.5.10"),sQuery(id+"F0.wireOp",EDGE,"E1.2.6.4"),sQuery(id+"F0.wireOp",EDGE,"E1.2.6.6"),sQuery(id+"F0.wireOp",EDGE,"E1.2.6.8"),sQuery(id+"F0.wireOp",EDGE,"E1.2.6.10"),sQuery(id+"F0.wireOp",EDGE,"E1.2.7.4"),sQuery(id+"F0.wireOp",EDGE,"E1.2.7.6"),sQuery(id+"F0.wireOp",EDGE,"E1.2.7.8"),sQuery(id+"F0.wireOp",EDGE,"E1.2.7.10"),sQuery(id+"F0.wireOp",EDGE,"E1.2.8.4"),sQuery(id+"F0.wireOp",EDGE,"E1.2.8.6"),sQuery(id+"F0.wireOp",EDGE,"E1.2.8.8"),sQuery(id+"F0.wireOp",EDGE,"E1.2.8.10"),sQuery(id+"F0.wireOp",EDGE,"E1.2.9.4"),sQuery(id+"F0.wireOp",EDGE,"E1.2.9.6"),sQuery(id+"F0.wireOp",EDGE,"E1.2.9.8"),sQuery(id+"F0.wireOp",EDGE,"E1.2.9.10"),sQuery(id+"F0.wireOp",EDGE,"E1.2.10.4"),sQuery(id+"F0.wireOp",EDGE,"E1.2.10.6"),sQuery(id+"F0.wireOp",EDGE,"E1.2.10.8"),sQuery(id+"F0.wireOp",EDGE,"E1.2.10.10"),sQuery(id+"F0.wireOp",EDGE,"E1.2.11.4"),sQuery(id+"F0.wireOp",EDGE,"E1.2.11.6"),sQuery(id+"F0.wireOp",EDGE,"E1.2.11.8"),sQuery(id+"F0.wireOp",EDGE,"E1.2.11.10"),sQuery(id+"F0.wireOp",EDGE,"E1.2.12.4"),sQuery(id+"F0.wireOp",EDGE,"E1.2.12.6"),sQuery(id+"F0.wireOp",EDGE,"E1.2.12.10"),sQuery(id+"F0.wireOp",EDGE,"E1.3.0.4"),sQuery(id+"F0.wireOp",EDGE,"E1.3.0.6"),sQuery(id+"F0.wireOp",EDGE,"E1.3.0.8"),sQuery(id+"F0.wireOp",EDGE,"E1.3.1.4"),sQuery(id+"F0.wireOp",EDGE,"E1.3.1.6"),sQuery(id+"F0.wireOp",EDGE,"E1.3.1.8"),sQuery(id+"F0.wireOp",EDGE,"E1.3.1.10"),sQuery(id+"F0.wireOp",EDGE,"E1.3.2.4"),sQuery(id+"F0.wireOp",EDGE,"E1.3.2.6"),sQuery(id+"F0.wireOp",EDGE,"E1.3.2.8"),sQuery(id+"F0.wireOp",EDGE,"E1.3.2.10"),sQuery(id+"F0.wireOp",EDGE,"E1.3.3.4"),sQuery(id+"F0.wireOp",EDGE,"E1.3.3.6"),sQuery(id+"F0.wireOp",EDGE,"E1.3.3.8"),sQuery(id+"F0.wireOp",EDGE,"E1.3.3.10"),sQuery(id+"F0.wireOp",EDGE,"E1.3.4.4"),sQuery(id+"F0.wireOp",EDGE,"E1.3.4.6"),sQuery(id+"F0.wireOp",EDGE,"E1.3.4.8"),sQuery(id+"F0.wireOp",EDGE,"E1.3.4.10"),sQuery(id+"F0.wireOp",EDGE,"E1.3.5.4"),sQuery(id+"F0.wireOp",EDGE,"E1.3.5.6"),sQuery(id+"F0.wireOp",EDGE,"E1.3.5.8"),sQuery(id+"F0.wireOp",EDGE,"E1.3.5.10"),sQuery(id+"F0.wireOp",EDGE,"E1.3.6.4"),sQuery(id+"F0.wireOp",EDGE,"E1.3.6.6"),sQuery(id+"F0.wireOp",EDGE,"E1.3.6.8"),sQuery(id+"F0.wireOp",EDGE,"E1.3.6.10"),sQuery(id+"F0.wireOp",EDGE,"E1.3.7.4"),sQuery(id+"F0.wireOp",EDGE,"E1.3.7.6"),sQuery(id+"F0.wireOp",EDGE,"E1.3.7.8"),sQuery(id+"F0.wireOp",EDGE,"E1.3.7.10"),sQuery(id+"F0.wireOp",EDGE,"E1.3.8.4"),sQuery(id+"F0.wireOp",EDGE,"E1.3.8.6"),sQuery(id+"F0.wireOp",EDGE,"E1.3.8.8"),sQuery(id+"F0.wireOp",EDGE,"E1.3.8.10"),sQuery(id+"F0.wireOp",EDGE,"E1.3.9.4"),sQuery(id+"F0.wireOp",EDGE,"E1.3.9.6"),sQuery(id+"F0.wireOp",EDGE,"E1.3.9.8"),sQuery(id+"F0.wireOp",EDGE,"E1.3.9.10"),sQuery(id+"F0.wireOp",EDGE,"E1.3.10.4"),sQuery(id+"F0.wireOp",EDGE,"E1.3.10.6"),sQuery(id+"F0.wireOp",EDGE,"E1.3.10.8"),sQuery(id+"F0.wireOp",EDGE,"E1.3.10.10"),sQuery(id+"F0.wireOp",EDGE,"E1.3.11.4"),sQuery(id+"F0.wireOp",EDGE,"E1.3.11.6"),sQuery(id+"F0.wireOp",EDGE,"E1.3.11.8"),sQuery(id+"F0.wireOp",EDGE,"E1.3.11.10"),sQuery(id+"F0.wireOp",EDGE,"E1.3.12.4"),sQuery(id+"F0.wireOp",EDGE,"E1.3.12.6"),sQuery(id+"F0.wireOp",EDGE,"E1.3.12.10"),sQuery(id+"F0.wireOp",EDGE,"E1.4.0.4"),sQuery(id+"F0.wireOp",EDGE,"E1.4.0.6"),sQuery(id+"F0.wireOp",EDGE,"E1.4.0.8"),sQuery(id+"F0.wireOp",EDGE,"E1.4.1.4"),sQuery(id+"F0.wireOp",EDGE,"E1.4.1.6"),sQuery(id+"F0.wireOp",EDGE,"E1.4.1.8"),sQuery(id+"F0.wireOp",EDGE,"E1.4.1.10"),sQuery(id+"F0.wireOp",EDGE,"E1.4.2.4"),sQuery(id+"F0.wireOp",EDGE,"E1.4.2.6"),sQuery(id+"F0.wireOp",EDGE,"E1.4.2.8"),sQuery(id+"F0.wireOp",EDGE,"E1.4.2.10"),sQuery(id+"F0.wireOp",EDGE,"E1.4.3.4"),sQuery(id+"F0.wireOp",EDGE,"E1.4.3.6"),sQuery(id+"F0.wireOp",EDGE,"E1.4.3.8"),sQuery(id+"F0.wireOp",EDGE,"E1.4.3.10"),sQuery(id+"F0.wireOp",EDGE,"E1.4.4.4"),sQuery(id+"F0.wireOp",EDGE,"E1.4.4.6"),sQuery(id+"F0.wireOp",EDGE,"E1.4.4.8"),sQuery(id+"F0.wireOp",EDGE,"E1.4.4.10"),sQuery(id+"F0.wireOp",EDGE,"E1.4.5.4"),sQuery(id+"F0.wireOp",EDGE,"E1.4.5.6"),sQuery(id+"F0.wireOp",EDGE,"E1.4.5.8"),sQuery(id+"F0.wireOp",EDGE,"E1.4.5.10"),sQuery(id+"F0.wireOp",EDGE,"E1.4.6.4"),sQuery(id+"F0.wireOp",EDGE,"E1.4.6.6"),sQuery(id+"F0.wireOp",EDGE,"E1.4.6.8"),sQuery(id+"F0.wireOp",EDGE,"E1.4.6.10"),sQuery(id+"F0.wireOp",EDGE,"E1.4.7.4"),sQuery(id+"F0.wireOp",EDGE,"E1.4.7.6"),sQuery(id+"F0.wireOp",EDGE,"E1.4.7.8"),sQuery(id+"F0.wireOp",EDGE,"E1.4.7.10"),sQuery(id+"F0.wireOp",EDGE,"E1.4.8.4"),sQuery(id+"F0.wireOp",EDGE,"E1.4.8.6"),sQuery(id+"F0.wireOp",EDGE,"E1.4.8.8"),sQuery(id+"F0.wireOp",EDGE,"E1.4.8.10"),sQuery(id+"F0.wireOp",EDGE,"E1.4.9.4"),sQuery(id+"F0.wireOp",EDGE,"E1.4.9.6"),sQuery(id+"F0.wireOp",EDGE,"E1.4.9.8"),sQuery(id+"F0.wireOp",EDGE,"E1.4.9.10"),sQuery(id+"F0.wireOp",EDGE,"E1.4.10.4"),sQuery(id+"F0.wireOp",EDGE,"E1.4.10.6"),sQuery(id+"F0.wireOp",EDGE,"E1.4.10.8"),sQuery(id+"F0.wireOp",EDGE,"E1.4.10.10"),sQuery(id+"F0.wireOp",EDGE,"E1.4.11.4"),sQuery(id+"F0.wireOp",EDGE,"E1.4.11.6"),sQuery(id+"F0.wireOp",EDGE,"E1.4.11.8"),sQuery(id+"F0.wireOp",EDGE,"E1.4.11.10"),sQuery(id+"F0.wireOp",EDGE,"E1.4.12.4"),sQuery(id+"F0.wireOp",EDGE,"E1.4.12.6"),sQuery(id+"F0.wireOp",EDGE,"E1.4.12.10"),sQuery(id+"F0.wireOp",EDGE,"E1.5.0.4"),sQuery(id+"F0.wireOp",EDGE,"E1.5.0.6"),sQuery(id+"F0.wireOp",EDGE,"E1.5.0.8"),sQuery(id+"F0.wireOp",EDGE,"E1.5.1.4"),sQuery(id+"F0.wireOp",EDGE,"E1.5.1.6"),sQuery(id+"F0.wireOp",EDGE,"E1.5.1.8"),sQuery(id+"F0.wireOp",EDGE,"E1.5.1.10"),sQuery(id+"F0.wireOp",EDGE,"E1.5.2.4"),sQuery(id+"F0.wireOp",EDGE,"E1.5.2.6"),sQuery(id+"F0.wireOp",EDGE,"E1.5.2.8"),sQuery(id+"F0.wireOp",EDGE,"E1.5.2.10"),sQuery(id+"F0.wireOp",EDGE,"E1.5.3.4"),sQuery(id+"F0.wireOp",EDGE,"E1.5.3.6"),sQuery(id+"F0.wireOp",EDGE,"E1.5.3.8"),sQuery(id+"F0.wireOp",EDGE,"E1.5.3.10"),sQuery(id+"F0.wireOp",EDGE,"E1.5.4.4"),sQuery(id+"F0.wireOp",EDGE,"E1.5.4.6"),sQuery(id+"F0.wireOp",EDGE,"E1.5.4.8"),sQuery(id+"F0.wireOp",EDGE,"E1.5.4.10"),sQuery(id+"F0.wireOp",EDGE,"E1.5.5.4"),sQuery(id+"F0.wireOp",EDGE,"E1.5.5.6"),sQuery(id+"F0.wireOp",EDGE,"E1.5.5.8"),sQuery(id+"F0.wireOp",EDGE,"E1.5.5.10"),sQuery(id+"F0.wireOp",EDGE,"E1.5.6.4"),sQuery(id+"F0.wireOp",EDGE,"E1.5.6.6"),sQuery(id+"F0.wireOp",EDGE,"E1.5.6.8"),sQuery(id+"F0.wireOp",EDGE,"E1.5.6.10"),sQuery(id+"F0.wireOp",EDGE,"E1.5.7.4"),sQuery(id+"F0.wireOp",EDGE,"E1.5.7.6"),sQuery(id+"F0.wireOp",EDGE,"E1.5.7.8"),sQuery(id+"F0.wireOp",EDGE,"E1.5.7.10"),sQuery(id+"F0.wireOp",EDGE,"E1.5.8.4"),sQuery(id+"F0.wireOp",EDGE,"E1.5.8.6"),sQuery(id+"F0.wireOp",EDGE,"E1.5.8.8"),sQuery(id+"F0.wireOp",EDGE,"E1.5.8.10"),sQuery(id+"F0.wireOp",EDGE,"E1.5.9.4"),sQuery(id+"F0.wireOp",EDGE,"E1.5.9.6"),sQuery(id+"F0.wireOp",EDGE,"E1.5.9.8"),sQuery(id+"F0.wireOp",EDGE,"E1.5.9.10"),sQuery(id+"F0.wireOp",EDGE,"E1.5.10.4"),sQuery(id+"F0.wireOp",EDGE,"E1.5.10.6"),sQuery(id+"F0.wireOp",EDGE,"E1.5.10.8"),sQuery(id+"F0.wireOp",EDGE,"E1.5.10.10"),sQuery(id+"F0.wireOp",EDGE,"E1.5.11.4"),sQuery(id+"F0.wireOp",EDGE,"E1.5.11.6"),sQuery(id+"F0.wireOp",EDGE,"E1.5.11.8"),sQuery(id+"F0.wireOp",EDGE,"E1.5.11.10"),sQuery(id+"F0.wireOp",EDGE,"E1.5.12.4"),sQuery(id+"F0.wireOp",EDGE,"E1.5.12.6"),sQuery(id+"F0.wireOp",EDGE,"E1.5.12.10"),sQuery(id+"F0.wireOp",EDGE,"E1.6.0.4"),sQuery(id+"F0.wireOp",EDGE,"E1.6.0.6"),sQuery(id+"F0.wireOp",EDGE,"E1.6.0.8"),sQuery(id+"F0.wireOp",EDGE,"E1.6.1.4"),sQuery(id+"F0.wireOp",EDGE,"E1.6.1.6"),sQuery(id+"F0.wireOp",EDGE,"E1.6.1.8"),sQuery(id+"F0.wireOp",EDGE,"E1.6.1.10"),sQuery(id+"F0.wireOp",EDGE,"E1.6.2.4"),sQuery(id+"F0.wireOp",EDGE,"E1.6.2.6"),sQuery(id+"F0.wireOp",EDGE,"E1.6.2.8"),sQuery(id+"F0.wireOp",EDGE,"E1.6.2.10"),sQuery(id+"F0.wireOp",EDGE,"E1.6.3.4"),sQuery(id+"F0.wireOp",EDGE,"E1.6.3.6"),sQuery(id+"F0.wireOp",EDGE,"E1.6.3.8"),sQuery(id+"F0.wireOp",EDGE,"E1.6.3.10"),sQuery(id+"F0.wireOp",EDGE,"E1.6.4.4"),sQuery(id+"F0.wireOp",EDGE,"E1.6.4.6"),sQuery(id+"F0.wireOp",EDGE,"E1.6.4.8"),sQuery(id+"F0.wireOp",EDGE,"E1.6.4.10"),sQuery(id+"F0.wireOp",EDGE,"E1.6.5.4"),sQuery(id+"F0.wireOp",EDGE,"E1.6.5.6"),sQuery(id+"F0.wireOp",EDGE,"E1.6.5.8"),sQuery(id+"F0.wireOp",EDGE,"E1.6.5.10"),sQuery(id+"F0.wireOp",EDGE,"E1.6.6.4"),sQuery(id+"F0.wireOp",EDGE,"E1.6.6.6"),sQuery(id+"F0.wireOp",EDGE,"E1.6.6.8"),sQuery(id+"F0.wireOp",EDGE,"E1.6.6.10"),sQuery(id+"F0.wireOp",EDGE,"E1.6.7.4"),sQuery(id+"F0.wireOp",EDGE,"E1.6.7.6"),sQuery(id+"F0.wireOp",EDGE,"E1.6.7.8"),sQuery(id+"F0.wireOp",EDGE,"E1.6.7.10"),sQuery(id+"F0.wireOp",EDGE,"E1.6.8.4"),sQuery(id+"F0.wireOp",EDGE,"E1.6.8.6"),sQuery(id+"F0.wireOp",EDGE,"E1.6.8.8"),sQuery(id+"F0.wireOp",EDGE,"E1.6.8.10"),sQuery(id+"F0.wireOp",EDGE,"E1.6.9.4"),sQuery(id+"F0.wireOp",EDGE,"E1.6.9.6"),sQuery(id+"F0.wireOp",EDGE,"E1.6.9.8"),sQuery(id+"F0.wireOp",EDGE,"E1.6.9.10"),sQuery(id+"F0.wireOp",EDGE,"E1.6.10.4"),sQuery(id+"F0.wireOp",EDGE,"E1.6.10.6"),sQuery(id+"F0.wireOp",EDGE,"E1.6.10.8"),sQuery(id+"F0.wireOp",EDGE,"E1.6.10.10"),sQuery(id+"F0.wireOp",EDGE,"E1.6.11.4"),sQuery(id+"F0.wireOp",EDGE,"E1.6.11.6"),sQuery(id+"F0.wireOp",EDGE,"E1.6.11.8"),sQuery(id+"F0.wireOp",EDGE,"E1.6.11.10"),sQuery(id+"F0.wireOp",EDGE,"E1.6.12.4"),sQuery(id+"F0.wireOp",EDGE,"E1.6.12.6"),sQuery(id+"F0.wireOp",EDGE,"E1.6.12.10"),sQuery(id+"F0.wireOp",EDGE,"E1.7.0.4"),sQuery(id+"F0.wireOp",EDGE,"E1.7.0.6"),sQuery(id+"F0.wireOp",EDGE,"E1.7.0.8"),sQuery(id+"F0.wireOp",EDGE,"E1.7.1.4"),sQuery(id+"F0.wireOp",EDGE,"E1.7.1.6"),sQuery(id+"F0.wireOp",EDGE,"E1.7.1.8"),sQuery(id+"F0.wireOp",EDGE,"E1.7.1.10"),sQuery(id+"F0.wireOp",EDGE,"E1.7.2.4"),sQuery(id+"F0.wireOp",EDGE,"E1.7.2.6"),sQuery(id+"F0.wireOp",EDGE,"E1.7.2.8"),sQuery(id+"F0.wireOp",EDGE,"E1.7.2.10"),sQuery(id+"F0.wireOp",EDGE,"E1.7.3.4"),sQuery(id+"F0.wireOp",EDGE,"E1.7.3.6"),sQuery(id+"F0.wireOp",EDGE,"E1.7.3.8"),sQuery(id+"F0.wireOp",EDGE,"E1.7.3.10"),sQuery(id+"F0.wireOp",EDGE,"E1.7.4.4"),sQuery(id+"F0.wireOp",EDGE,"E1.7.4.6"),sQuery(id+"F0.wireOp",EDGE,"E1.7.4.8"),sQuery(id+"F0.wireOp",EDGE,"E1.7.4.10"),sQuery(id+"F0.wireOp",EDGE,"E1.7.5.4"),sQuery(id+"F0.wireOp",EDGE,"E1.7.5.6"),sQuery(id+"F0.wireOp",EDGE,"E1.7.5.8"),sQuery(id+"F0.wireOp",EDGE,"E1.7.5.10"),sQuery(id+"F0.wireOp",EDGE,"E1.7.6.4"),sQuery(id+"F0.wireOp",EDGE,"E1.7.6.6"),sQuery(id+"F0.wireOp",EDGE,"E1.7.6.8"),sQuery(id+"F0.wireOp",EDGE,"E1.7.6.10"),sQuery(id+"F0.wireOp",EDGE,"E1.7.7.4"),sQuery(id+"F0.wireOp",EDGE,"E1.7.7.6"),sQuery(id+"F0.wireOp",EDGE,"E1.7.7.8"),sQuery(id+"F0.wireOp",EDGE,"E1.7.7.10"),sQuery(id+"F0.wireOp",EDGE,"E1.7.8.4"),sQuery(id+"F0.wireOp",EDGE,"E1.7.8.6"),sQuery(id+"F0.wireOp",EDGE,"E1.7.8.8"),sQuery(id+"F0.wireOp",EDGE,"E1.7.8.10"),sQuery(id+"F0.wireOp",EDGE,"E1.7.9.4"),sQuery(id+"F0.wireOp",EDGE,"E1.7.9.6"),sQuery(id+"F0.wireOp",EDGE,"E1.7.9.8"),sQuery(id+"F0.wireOp",EDGE,"E1.7.9.10"),sQuery(id+"F0.wireOp",EDGE,"E1.7.10.4"),sQuery(id+"F0.wireOp",EDGE,"E1.7.10.6"),sQuery(id+"F0.wireOp",EDGE,"E1.7.10.8"),sQuery(id+"F0.wireOp",EDGE,"E1.7.10.10"),sQuery(id+"F0.wireOp",EDGE,"E1.7.11.4"),sQuery(id+"F0.wireOp",EDGE,"E1.7.11.6"),sQuery(id+"F0.wireOp",EDGE,"E1.7.11.8"),sQuery(id+"F0.wireOp",EDGE,"E1.7.11.10"),sQuery(id+"F0.wireOp",EDGE,"E1.7.12.4"),sQuery(id+"F0.wireOp",EDGE,"E1.7.12.6"),sQuery(id+"F0.wireOp",EDGE,"E1.7.12.10"),sQuery(id+"F0.wireOp",EDGE,"E1.8.0.4"),sQuery(id+"F0.wireOp",EDGE,"E1.8.0.6"),sQuery(id+"F0.wireOp",EDGE,"E1.8.0.8"),sQuery(id+"F0.wireOp",EDGE,"E1.8.1.4"),sQuery(id+"F0.wireOp",EDGE,"E1.8.1.6"),sQuery(id+"F0.wireOp",EDGE,"E1.8.1.8"),sQuery(id+"F0.wireOp",EDGE,"E1.8.1.10"),sQuery(id+"F0.wireOp",EDGE,"E1.8.2.4"),sQuery(id+"F0.wireOp",EDGE,"E1.8.2.6"),sQuery(id+"F0.wireOp",EDGE,"E1.8.2.8"),sQuery(id+"F0.wireOp",EDGE,"E1.8.2.10"),sQuery(id+"F0.wireOp",EDGE,"E1.8.3.4"),sQuery(id+"F0.wireOp",EDGE,"E1.8.3.6"),sQuery(id+"F0.wireOp",EDGE,"E1.8.3.8"),sQuery(id+"F0.wireOp",EDGE,"E1.8.3.10"),sQuery(id+"F0.wireOp",EDGE,"E1.8.4.4"),sQuery(id+"F0.wireOp",EDGE,"E1.8.4.6"),sQuery(id+"F0.wireOp",EDGE,"E1.8.4.8"),sQuery(id+"F0.wireOp",EDGE,"E1.8.4.10"),sQuery(id+"F0.wireOp",EDGE,"E1.8.5.4"),sQuery(id+"F0.wireOp",EDGE,"E1.8.5.6"),sQuery(id+"F0.wireOp",EDGE,"E1.8.5.8"),sQuery(id+"F0.wireOp",EDGE,"E1.8.5.10"),sQuery(id+"F0.wireOp",EDGE,"E1.8.6.4"),sQuery(id+"F0.wireOp",EDGE,"E1.8.6.6"),sQuery(id+"F0.wireOp",EDGE,"E1.8.6.8"),sQuery(id+"F0.wireOp",EDGE,"E1.8.6.10"),sQuery(id+"F0.wireOp",EDGE,"E1.8.7.4"),sQuery(id+"F0.wireOp",EDGE,"E1.8.7.6"),sQuery(id+"F0.wireOp",EDGE,"E1.8.7.8"),sQuery(id+"F0.wireOp",EDGE,"E1.8.7.10"),sQuery(id+"F0.wireOp",EDGE,"E1.8.8.4"),sQuery(id+"F0.wireOp",EDGE,"E1.8.8.6"),sQuery(id+"F0.wireOp",EDGE,"E1.8.8.8"),sQuery(id+"F0.wireOp",EDGE,"E1.8.8.10"),sQuery(id+"F0.wireOp",EDGE,"E1.8.9.4"),sQuery(id+"F0.wireOp",EDGE,"E1.8.9.6"),sQuery(id+"F0.wireOp",EDGE,"E1.8.9.8"),sQuery(id+"F0.wireOp",EDGE,"E1.8.9.10"),sQuery(id+"F0.wireOp",EDGE,"E1.8.10.4"),sQuery(id+"F0.wireOp",EDGE,"E1.8.10.6"),sQuery(id+"F0.wireOp",EDGE,"E1.8.10.8"),sQuery(id+"F0.wireOp",EDGE,"E1.8.10.10"),sQuery(id+"F0.wireOp",EDGE,"E1.8.11.4"),sQuery(id+"F0.wireOp",EDGE,"E1.8.11.6"),sQuery(id+"F0.wireOp",EDGE,"E1.8.11.8"),sQuery(id+"F0.wireOp",EDGE,"E1.8.11.10"),sQuery(id+"F0.wireOp",EDGE,"E1.8.12.4"),sQuery(id+"F0.wireOp",EDGE,"E1.8.12.6"),sQuery(id+"F0.wireOp",EDGE,"E1.8.12.10"),sQuery(id+"F0.wireOp",EDGE,"E1.9.0.4"),sQuery(id+"F0.wireOp",EDGE,"E1.9.0.6"),sQuery(id+"F0.wireOp",EDGE,"E1.9.0.8"),sQuery(id+"F0.wireOp",EDGE,"E1.9.1.4"),sQuery(id+"F0.wireOp",EDGE,"E1.9.1.6"),sQuery(id+"F0.wireOp",EDGE,"E1.9.1.8"),sQuery(id+"F0.wireOp",EDGE,"E1.9.1.10"),sQuery(id+"F0.wireOp",EDGE,"E1.9.2.4"),sQuery(id+"F0.wireOp",EDGE,"E1.9.2.6"),sQuery(id+"F0.wireOp",EDGE,"E1.9.2.8"),sQuery(id+"F0.wireOp",EDGE,"E1.9.2.10"),sQuery(id+"F0.wireOp",EDGE,"E1.9.3.4"),sQuery(id+"F0.wireOp",EDGE,"E1.9.3.6"),sQuery(id+"F0.wireOp",EDGE,"E1.9.3.8"),sQuery(id+"F0.wireOp",EDGE,"E1.9.3.10"),sQuery(id+"F0.wireOp",EDGE,"E1.9.4.4"),sQuery(id+"F0.wireOp",EDGE,"E1.9.4.6"),sQuery(id+"F0.wireOp",EDGE,"E1.9.4.8"),sQuery(id+"F0.wireOp",EDGE,"E1.9.4.10"),sQuery(id+"F0.wireOp",EDGE,"E1.9.5.4"),sQuery(id+"F0.wireOp",EDGE,"E1.9.5.6"),sQuery(id+"F0.wireOp",EDGE,"E1.9.5.8"),sQuery(id+"F0.wireOp",EDGE,"E1.9.5.10"),sQuery(id+"F0.wireOp",EDGE,"E1.9.6.4"),sQuery(id+"F0.wireOp",EDGE,"E1.9.6.6"),sQuery(id+"F0.wireOp",EDGE,"E1.9.6.8"),sQuery(id+"F0.wireOp",EDGE,"E1.9.6.10"),sQuery(id+"F0.wireOp",EDGE,"E1.9.7.4"),sQuery(id+"F0.wireOp",EDGE,"E1.9.7.6"),sQuery(id+"F0.wireOp",EDGE,"E1.9.7.8"),sQuery(id+"F0.wireOp",EDGE,"E1.9.7.10"),sQuery(id+"F0.wireOp",EDGE,"E1.9.8.4"),sQuery(id+"F0.wireOp",EDGE,"E1.9.8.6"),sQuery(id+"F0.wireOp",EDGE,"E1.9.8.8"),sQuery(id+"F0.wireOp",EDGE,"E1.9.8.10"),sQuery(id+"F0.wireOp",EDGE,"E1.9.9.4"),sQuery(id+"F0.wireOp",EDGE,"E1.9.9.6"),sQuery(id+"F0.wireOp",EDGE,"E1.9.9.8"),sQuery(id+"F0.wireOp",EDGE,"E1.9.9.10"),sQuery(id+"F0.wireOp",EDGE,"E1.9.10.4"),sQuery(id+"F0.wireOp",EDGE,"E1.9.10.6"),sQuery(id+"F0.wireOp",EDGE,"E1.9.10.8"),sQuery(id+"F0.wireOp",EDGE,"E1.9.10.10"),sQuery(id+"F0.wireOp",EDGE,"E1.9.11.4"),sQuery(id+"F0.wireOp",EDGE,"E1.9.11.6"),sQuery(id+"F0.wireOp",EDGE,"E1.9.11.8"),sQuery(id+"F0.wireOp",EDGE,"E1.9.11.10"),sQuery(id+"F0.wireOp",EDGE,"E1.9.12.4"),sQuery(id+"F0.wireOp",EDGE,"E1.9.12.6"),sQuery(id+"F0.wireOp",EDGE,"E1.9.12.10"),sQuery(id+"F0.wireOp",EDGE,"E1.10.0.4"),sQuery(id+"F0.wireOp",EDGE,"E1.10.0.6"),sQuery(id+"F0.wireOp",EDGE,"E1.10.0.8"),sQuery(id+"F0.wireOp",EDGE,"E1.10.1.4"),sQuery(id+"F0.wireOp",EDGE,"E1.10.1.6"),sQuery(id+"F0.wireOp",EDGE,"E1.10.1.8"),sQuery(id+"F0.wireOp",EDGE,"E1.10.1.10"),sQuery(id+"F0.wireOp",EDGE,"E1.10.2.4"),sQuery(id+"F0.wireOp",EDGE,"E1.10.2.6"),sQuery(id+"F0.wireOp",EDGE,"E1.10.2.8"),sQuery(id+"F0.wireOp",EDGE,"E1.10.2.10"),sQuery(id+"F0.wireOp",EDGE,"E1.10.3.4"),sQuery(id+"F0.wireOp",EDGE,"E1.10.3.6"),sQuery(id+"F0.wireOp",EDGE,"E1.10.3.8"),sQuery(id+"F0.wireOp",EDGE,"E1.10.3.10"),sQuery(id+"F0.wireOp",EDGE,"E1.10.4.4"),sQuery(id+"F0.wireOp",EDGE,"E1.10.4.6"),sQuery(id+"F0.wireOp",EDGE,"E1.10.4.8"),sQuery(id+"F0.wireOp",EDGE,"E1.10.4.10"),sQuery(id+"F0.wireOp",EDGE,"E1.10.5.4"),sQuery(id+"F0.wireOp",EDGE,"E1.10.5.6"),sQuery(id+"F0.wireOp",EDGE,"E1.10.5.8"),sQuery(id+"F0.wireOp",EDGE,"E1.10.5.10"),sQuery(id+"F0.wireOp",EDGE,"E1.10.6.4"),sQuery(id+"F0.wireOp",EDGE,"E1.10.6.6"),sQuery(id+"F0.wireOp",EDGE,"E1.10.6.8"),sQuery(id+"F0.wireOp",EDGE,"E1.10.6.10"),sQuery(id+"F0.wireOp",EDGE,"E1.10.7.4"),sQuery(id+"F0.wireOp",EDGE,"E1.10.7.6"),sQuery(id+"F0.wireOp",EDGE,"E1.10.7.8"),sQuery(id+"F0.wireOp",EDGE,"E1.10.7.10"),sQuery(id+"F0.wireOp",EDGE,"E1.10.8.4"),sQuery(id+"F0.wireOp",EDGE,"E1.10.8.6"),sQuery(id+"F0.wireOp",EDGE,"E1.10.8.8"),sQuery(id+"F0.wireOp",EDGE,"E1.10.8.10"),sQuery(id+"F0.wireOp",EDGE,"E1.10.9.4"),sQuery(id+"F0.wireOp",EDGE,"E1.10.9.6"),sQuery(id+"F0.wireOp",EDGE,"E1.10.9.8"),sQuery(id+"F0.wireOp",EDGE,"E1.10.9.10"),sQuery(id+"F0.wireOp",EDGE,"E1.10.10.4"),sQuery(id+"F0.wireOp",EDGE,"E1.10.10.6"),sQuery(id+"F0.wireOp",EDGE,"E1.10.10.8"),sQuery(id+"F0.wireOp",EDGE,"E1.10.10.10"),sQuery(id+"F0.wireOp",EDGE,"E1.10.11.4"),sQuery(id+"F0.wireOp",EDGE,"E1.10.11.6"),sQuery(id+"F0.wireOp",EDGE,"E1.10.11.8"),sQuery(id+"F0.wireOp",EDGE,"E1.10.11.10"),sQuery(id+"F0.wireOp",EDGE,"E1.10.12.4"),sQuery(id+"F0.wireOp",EDGE,"E1.10.12.6"),sQuery(id+"F0.wireOp",EDGE,"E1.10.12.10"),sQuery(id+"F0.wireOp",EDGE,"E1.11.0.4"),sQuery(id+"F0.wireOp",EDGE,"E1.11.0.6"),sQuery(id+"F0.wireOp",EDGE,"E1.11.0.8"),sQuery(id+"F0.wireOp",EDGE,"E1.11.1.4"),sQuery(id+"F0.wireOp",EDGE,"E1.11.1.6"),sQuery(id+"F0.wireOp",EDGE,"E1.11.1.8"),sQuery(id+"F0.wireOp",EDGE,"E1.11.1.10"),sQuery(id+"F0.wireOp",EDGE,"E1.11.2.4"),sQuery(id+"F0.wireOp",EDGE,"E1.11.2.6"),sQuery(id+"F0.wireOp",EDGE,"E1.11.2.8"),sQuery(id+"F0.wireOp",EDGE,"E1.11.2.10"),sQuery(id+"F0.wireOp",EDGE,"E1.11.3.4"),sQuery(id+"F0.wireOp",EDGE,"E1.11.3.6"),sQuery(id+"F0.wireOp",EDGE,"E1.11.3.8"),sQuery(id+"F0.wireOp",EDGE,"E1.11.3.10"),sQuery(id+"F0.wireOp",EDGE,"E1.11.4.4"),sQuery(id+"F0.wireOp",EDGE,"E1.11.4.6"),sQuery(id+"F0.wireOp",EDGE,"E1.11.4.8"),sQuery(id+"F0.wireOp",EDGE,"E1.11.4.10"),sQuery(id+"F0.wireOp",EDGE,"E1.11.5.4"),sQuery(id+"F0.wireOp",EDGE,"E1.11.5.6"),sQuery(id+"F0.wireOp",EDGE,"E1.11.5.8"),sQuery(id+"F0.wireOp",EDGE,"E1.11.5.10"),sQuery(id+"F0.wireOp",EDGE,"E1.11.6.4"),sQuery(id+"F0.wireOp",EDGE,"E1.11.6.6"),sQuery(id+"F0.wireOp",EDGE,"E1.11.6.8"),sQuery(id+"F0.wireOp",EDGE,"E1.11.6.10"),sQuery(id+"F0.wireOp",EDGE,"E1.11.7.4"),sQuery(id+"F0.wireOp",EDGE,"E1.11.7.6"),sQuery(id+"F0.wireOp",EDGE,"E1.11.7.8"),sQuery(id+"F0.wireOp",EDGE,"E1.11.7.10"),sQuery(id+"F0.wireOp",EDGE,"E1.11.8.4"),sQuery(id+"F0.wireOp",EDGE,"E1.11.8.6"),sQuery(id+"F0.wireOp",EDGE,"E1.11.8.8"),sQuery(id+"F0.wireOp",EDGE,"E1.11.8.10"),sQuery(id+"F0.wireOp",EDGE,"E1.11.9.4"),sQuery(id+"F0.wireOp",EDGE,"E1.11.9.6"),sQuery(id+"F0.wireOp",EDGE,"E1.11.9.8"),sQuery(id+"F0.wireOp",EDGE,"E1.11.9.10"),sQuery(id+"F0.wireOp",EDGE,"E1.11.10.4"),sQuery(id+"F0.wireOp",EDGE,"E1.11.10.6"),sQuery(id+"F0.wireOp",EDGE,"E1.11.10.8"),sQuery(id+"F0.wireOp",EDGE,"E1.11.10.10"),sQuery(id+"F0.wireOp",EDGE,"E1.11.11.4"),sQuery(id+"F0.wireOp",EDGE,"E1.11.11.6"),sQuery(id+"F0.wireOp",EDGE,"E1.11.11.8"),sQuery(id+"F0.wireOp",EDGE,"E1.11.11.10"),sQuery(id+"F0.wireOp",EDGE,"E1.11.12.4"),sQuery(id+"F0.wireOp",EDGE,"E1.11.12.6"),sQuery(id+"F0.wireOp",EDGE,"E1.11.12.10"),sQuery(id+"F0.wireOp",EDGE,"E1.12.1.6"),sQuery(id+"F0.wireOp",EDGE,"E1.12.1.8"),sQuery(id+"F0.wireOp",EDGE,"E1.12.1.10"),sQuery(id+"F0.wireOp",EDGE,"E1.12.2.6"),sQuery(id+"F0.wireOp",EDGE,"E1.12.2.8"),sQuery(id+"F0.wireOp",EDGE,"E1.12.2.10"),sQuery(id+"F0.wireOp",EDGE,"E1.12.3.6"),sQuery(id+"F0.wireOp",EDGE,"E1.12.3.8"),sQuery(id+"F0.wireOp",EDGE,"E1.12.3.10"),sQuery(id+"F0.wireOp",EDGE,"E1.12.4.6"),sQuery(id+"F0.wireOp",EDGE,"E1.12.4.8"),sQuery(id+"F0.wireOp",EDGE,"E1.12.4.10"),sQuery(id+"F0.wireOp",EDGE,"E1.12.5.6"),sQuery(id+"F0.wireOp",EDGE,"E1.12.5.8"),sQuery(id+"F0.wireOp",EDGE,"E1.12.5.10"),sQuery(id+"F0.wireOp",EDGE,"E1.12.6.6"),sQuery(id+"F0.wireOp",EDGE,"E1.12.6.8"),sQuery(id+"F0.wireOp",EDGE,"E1.12.6.10"),sQuery(id+"F0.wireOp",EDGE,"E1.12.7.6"),sQuery(id+"F0.wireOp",EDGE,"E1.12.7.8"),sQuery(id+"F0.wireOp",EDGE,"E1.12.7.10"),sQuery(id+"F0.wireOp",EDGE,"E1.12.8.6"),sQuery(id+"F0.wireOp",EDGE,"E1.12.8.8"),sQuery(id+"F0.wireOp",EDGE,"E1.12.8.10"),sQuery(id+"F0.wireOp",EDGE,"E1.12.9.6"),sQuery(id+"F0.wireOp",EDGE,"E1.12.9.8"),sQuery(id+"F0.wireOp",EDGE,"E1.12.9.10"),sQuery(id+"F0.wireOp",EDGE,"E1.12.10.6"),sQuery(id+"F0.wireOp",EDGE,"E1.12.10.8"),sQuery(id+"F0.wireOp",EDGE,"E1.12.10.10"),sQuery(id+"F0.wireOp",EDGE,"E1.12.11.6"),sQuery(id+"F0.wireOp",EDGE,"E1.12.11.8"),sQuery(id+"F0.wireOp",EDGE,"E1.12.11.10"),sQuery(id+"F0.wireOp",EDGE,"E2.bottom"),sQuery(id+"F0.wireOp",EDGE,"E2.top"),sQuery(id+"F0.wireOp",EDGE,"E2.left"),sQuery(id+"F0.wireOp",EDGE,"E2.right")])]});
            transform(context, id + "F8", {"entities" : qUnion([Q0]), "transformType" : TransformType.TRANSLATION_3D, "dx" : 0 * mm, "dy" : 0 * mm, "dz" : 46 * mm, "makeCopy" : true});
        }
        {
            var Q0;
            Q0=makeQuery(id+"F5.opExtrude","SWEPT_BODY",BODY,{"disambiguationData":[OSD([sQuery(id+"F4.wireOp",EDGE,"E8.1.0.2"),sQuery(id+"F4.wireOp",EDGE,"E8.1.0.3"),sQuery(id+"F4.wireOp",EDGE,"E8.1.1.0"),sQuery(id+"F4.wireOp",EDGE,"E8.1.1.1"),sQuery(id+"F4.wireOp",EDGE,"E8.1.1.2"),sQuery(id+"F4.wireOp",EDGE,"E8.1.1.3"),sQuery(id+"F4.wireOp",EDGE,"E8.1.2.0"),sQuery(id+"F4.wireOp",EDGE,"E8.1.2.1"),sQuery(id+"F4.wireOp",EDGE,"E8.1.2.2"),sQuery(id+"F4.wireOp",EDGE,"E8.1.2.3"),sQuery(id+"F4.wireOp",EDGE,"E8.1.3.0"),sQuery(id+"F4.wireOp",EDGE,"E8.1.3.1"),sQuery(id+"F4.wireOp",EDGE,"E8.1.3.2"),sQuery(id+"F4.wireOp",EDGE,"E8.1.3.3"),sQuery(id+"F4.wireOp",EDGE,"E8.1.4.0"),sQuery(id+"F4.wireOp",EDGE,"E8.1.4.1"),sQuery(id+"F4.wireOp",EDGE,"E8.1.4.2"),sQuery(id+"F4.wireOp",EDGE,"E8.1.4.3"),sQuery(id+"F4.wireOp",EDGE,"E8.1.5.0"),sQuery(id+"F4.wireOp",EDGE,"E8.1.5.1"),sQuery(id+"F4.wireOp",EDGE,"E8.1.5.2"),sQuery(id+"F4.wireOp",EDGE,"E8.1.5.3"),sQuery(id+"F4.wireOp",EDGE,"E8.1.6.0"),sQuery(id+"F4.wireOp",EDGE,"E8.1.6.1"),sQuery(id+"F4.wireOp",EDGE,"E8.1.6.2"),sQuery(id+"F4.wireOp",EDGE,"E8.1.6.3"),sQuery(id+"F4.wireOp",EDGE,"E8.1.7.0"),sQuery(id+"F4.wireOp",EDGE,"E8.1.7.1"),sQuery(id+"F4.wireOp",EDGE,"E8.1.7.2"),sQuery(id+"F4.wireOp",EDGE,"E8.1.7.3"),sQuery(id+"F4.wireOp",EDGE,"E8.1.8.0"),sQuery(id+"F4.wireOp",EDGE,"E8.1.8.1"),sQuery(id+"F4.wireOp",EDGE,"E8.1.8.2"),sQuery(id+"F4.wireOp",EDGE,"E8.1.8.3"),sQuery(id+"F4.wireOp",EDGE,"E8.1.9.0"),sQuery(id+"F4.wireOp",EDGE,"E8.1.9.1"),sQuery(id+"F4.wireOp",EDGE,"E8.1.9.2"),sQuery(id+"F4.wireOp",EDGE,"E8.1.9.3"),sQuery(id+"F4.wireOp",EDGE,"E8.1.10.0"),sQuery(id+"F4.wireOp",EDGE,"E8.1.10.1"),sQuery(id+"F4.wireOp",EDGE,"E8.1.10.2"),sQuery(id+"F4.wireOp",EDGE,"E8.1.10.3"),sQuery(id+"F4.wireOp",EDGE,"E8.1.11.0"),sQuery(id+"F4.wireOp",EDGE,"E8.1.11.1"),sQuery(id+"F4.wireOp",EDGE,"E8.1.11.2"),sQuery(id+"F4.wireOp",EDGE,"E8.1.11.3"),sQuery(id+"F4.wireOp",EDGE,"E8.2.0.2"),sQuery(id+"F4.wireOp",EDGE,"E8.2.0.3"),sQuery(id+"F4.wireOp",EDGE,"E8.2.1.0"),sQuery(id+"F4.wireOp",EDGE,"E8.2.1.1"),sQuery(id+"F4.wireOp",EDGE,"E8.2.1.2"),sQuery(id+"F4.wireOp",EDGE,"E8.2.1.3"),sQuery(id+"F4.wireOp",EDGE,"E8.2.2.0"),sQuery(id+"F4.wireOp",EDGE,"E8.2.2.1"),sQuery(id+"F4.wireOp",EDGE,"E8.2.2.2"),sQuery(id+"F4.wireOp",EDGE,"E8.2.2.3"),sQuery(id+"F4.wireOp",EDGE,"E8.2.3.0"),sQuery(id+"F4.wireOp",EDGE,"E8.2.3.1"),sQuery(id+"F4.wireOp",EDGE,"E8.2.3.2"),sQuery(id+"F4.wireOp",EDGE,"E8.2.3.3"),sQuery(id+"F4.wireOp",EDGE,"E8.2.4.0"),sQuery(id+"F4.wireOp",EDGE,"E8.2.4.1"),sQuery(id+"F4.wireOp",EDGE,"E8.2.4.2"),sQuery(id+"F4.wireOp",EDGE,"E8.2.4.3"),sQuery(id+"F4.wireOp",EDGE,"E8.2.5.0"),sQuery(id+"F4.wireOp",EDGE,"E8.2.5.1"),sQuery(id+"F4.wireOp",EDGE,"E8.2.5.2"),sQuery(id+"F4.wireOp",EDGE,"E8.2.5.3"),sQuery(id+"F4.wireOp",EDGE,"E8.2.6.0"),sQuery(id+"F4.wireOp",EDGE,"E8.2.6.1"),sQuery(id+"F4.wireOp",EDGE,"E8.2.6.2"),sQuery(id+"F4.wireOp",EDGE,"E8.2.6.3"),sQuery(id+"F4.wireOp",EDGE,"E8.2.7.0"),sQuery(id+"F4.wireOp",EDGE,"E8.2.7.1"),sQuery(id+"F4.wireOp",EDGE,"E8.2.7.2"),sQuery(id+"F4.wireOp",EDGE,"E8.2.7.3"),sQuery(id+"F4.wireOp",EDGE,"E8.2.8.0"),sQuery(id+"F4.wireOp",EDGE,"E8.2.8.1"),sQuery(id+"F4.wireOp",EDGE,"E8.2.8.2"),sQuery(id+"F4.wireOp",EDGE,"E8.2.8.3"),sQuery(id+"F4.wireOp",EDGE,"E8.2.9.0"),sQuery(id+"F4.wireOp",EDGE,"E8.2.9.1"),sQuery(id+"F4.wireOp",EDGE,"E8.2.9.2"),sQuery(id+"F4.wireOp",EDGE,"E8.2.9.3"),sQuery(id+"F4.wireOp",EDGE,"E8.2.10.0"),sQuery(id+"F4.wireOp",EDGE,"E8.2.10.1"),sQuery(id+"F4.wireOp",EDGE,"E8.2.10.2"),sQuery(id+"F4.wireOp",EDGE,"E8.2.10.3"),sQuery(id+"F4.wireOp",EDGE,"E8.2.11.0"),sQuery(id+"F4.wireOp",EDGE,"E8.2.11.1"),sQuery(id+"F4.wireOp",EDGE,"E8.2.11.2"),sQuery(id+"F4.wireOp",EDGE,"E8.2.11.3"),sQuery(id+"F4.wireOp",EDGE,"E8.3.0.2"),sQuery(id+"F4.wireOp",EDGE,"E8.3.0.3"),sQuery(id+"F4.wireOp",EDGE,"E8.3.1.0"),sQuery(id+"F4.wireOp",EDGE,"E8.3.1.1"),sQuery(id+"F4.wireOp",EDGE,"E8.3.1.2"),sQuery(id+"F4.wireOp",EDGE,"E8.3.1.3"),sQuery(id+"F4.wireOp",EDGE,"E8.3.2.0"),sQuery(id+"F4.wireOp",EDGE,"E8.3.2.1"),sQuery(id+"F4.wireOp",EDGE,"E8.3.2.2"),sQuery(id+"F4.wireOp",EDGE,"E8.3.2.3"),sQuery(id+"F4.wireOp",EDGE,"E8.3.3.0"),sQuery(id+"F4.wireOp",EDGE,"E8.3.3.1"),sQuery(id+"F4.wireOp",EDGE,"E8.3.3.2"),sQuery(id+"F4.wireOp",EDGE,"E8.3.3.3"),sQuery(id+"F4.wireOp",EDGE,"E8.3.4.0"),sQuery(id+"F4.wireOp",EDGE,"E8.3.4.1"),sQuery(id+"F4.wireOp",EDGE,"E8.3.4.2"),sQuery(id+"F4.wireOp",EDGE,"E8.3.4.3"),sQuery(id+"F4.wireOp",EDGE,"E8.3.5.0"),sQuery(id+"F4.wireOp",EDGE,"E8.3.5.1"),sQuery(id+"F4.wireOp",EDGE,"E8.3.5.2"),sQuery(id+"F4.wireOp",EDGE,"E8.3.5.3"),sQuery(id+"F4.wireOp",EDGE,"E8.3.6.0"),sQuery(id+"F4.wireOp",EDGE,"E8.3.6.1"),sQuery(id+"F4.wireOp",EDGE,"E8.3.6.2"),sQuery(id+"F4.wireOp",EDGE,"E8.3.6.3"),sQuery(id+"F4.wireOp",EDGE,"E8.3.7.0"),sQuery(id+"F4.wireOp",EDGE,"E8.3.7.1"),sQuery(id+"F4.wireOp",EDGE,"E8.3.7.2"),sQuery(id+"F4.wireOp",EDGE,"E8.3.7.3"),sQuery(id+"F4.wireOp",EDGE,"E8.3.8.0"),sQuery(id+"F4.wireOp",EDGE,"E8.3.8.1"),sQuery(id+"F4.wireOp",EDGE,"E8.3.8.2"),sQuery(id+"F4.wireOp",EDGE,"E8.3.8.3"),sQuery(id+"F4.wireOp",EDGE,"E8.3.9.0"),sQuery(id+"F4.wireOp",EDGE,"E8.3.9.1"),sQuery(id+"F4.wireOp",EDGE,"E8.3.9.2"),sQuery(id+"F4.wireOp",EDGE,"E8.3.9.3"),sQuery(id+"F4.wireOp",EDGE,"E8.3.10.0"),sQuery(id+"F4.wireOp",EDGE,"E8.3.10.1"),sQuery(id+"F4.wireOp",EDGE,"E8.3.10.2"),sQuery(id+"F4.wireOp",EDGE,"E8.3.10.3"),sQuery(id+"F4.wireOp",EDGE,"E8.3.11.0"),sQuery(id+"F4.wireOp",EDGE,"E8.3.11.1"),sQuery(id+"F4.wireOp",EDGE,"E8.3.11.2"),sQuery(id+"F4.wireOp",EDGE,"E8.3.11.3"),sQuery(id+"F4.wireOp",EDGE,"E8.4.0.2"),sQuery(id+"F4.wireOp",EDGE,"E8.4.0.3"),sQuery(id+"F4.wireOp",EDGE,"E8.4.1.0"),sQuery(id+"F4.wireOp",EDGE,"E8.4.1.1"),sQuery(id+"F4.wireOp",EDGE,"E8.4.1.2"),sQuery(id+"F4.wireOp",EDGE,"E8.4.1.3"),sQuery(id+"F4.wireOp",EDGE,"E8.4.2.0"),sQuery(id+"F4.wireOp",EDGE,"E8.4.2.1"),sQuery(id+"F4.wireOp",EDGE,"E8.4.2.2"),sQuery(id+"F4.wireOp",EDGE,"E8.4.2.3"),sQuery(id+"F4.wireOp",EDGE,"E8.4.3.0"),sQuery(id+"F4.wireOp",EDGE,"E8.4.3.1"),sQuery(id+"F4.wireOp",EDGE,"E8.4.3.2"),sQuery(id+"F4.wireOp",EDGE,"E8.4.3.3"),sQuery(id+"F4.wireOp",EDGE,"E8.4.4.0"),sQuery(id+"F4.wireOp",EDGE,"E8.4.4.1"),sQuery(id+"F4.wireOp",EDGE,"E8.4.4.2"),sQuery(id+"F4.wireOp",EDGE,"E8.4.4.3"),sQuery(id+"F4.wireOp",EDGE,"E8.4.5.0"),sQuery(id+"F4.wireOp",EDGE,"E8.4.5.1"),sQuery(id+"F4.wireOp",EDGE,"E8.4.5.2"),sQuery(id+"F4.wireOp",EDGE,"E8.4.5.3"),sQuery(id+"F4.wireOp",EDGE,"E8.4.6.0"),sQuery(id+"F4.wireOp",EDGE,"E8.4.6.1"),sQuery(id+"F4.wireOp",EDGE,"E8.4.6.2"),sQuery(id+"F4.wireOp",EDGE,"E8.4.6.3"),sQuery(id+"F4.wireOp",EDGE,"E8.4.7.0"),sQuery(id+"F4.wireOp",EDGE,"E8.4.7.1"),sQuery(id+"F4.wireOp",EDGE,"E8.4.7.2"),sQuery(id+"F4.wireOp",EDGE,"E8.4.7.3"),sQuery(id+"F4.wireOp",EDGE,"E8.4.8.0"),sQuery(id+"F4.wireOp",EDGE,"E8.4.8.1"),sQuery(id+"F4.wireOp",EDGE,"E8.4.8.2"),sQuery(id+"F4.wireOp",EDGE,"E8.4.8.3"),sQuery(id+"F4.wireOp",EDGE,"E8.4.9.0"),sQuery(id+"F4.wireOp",EDGE,"E8.4.9.1"),sQuery(id+"F4.wireOp",EDGE,"E8.4.9.2"),sQuery(id+"F4.wireOp",EDGE,"E8.4.9.3"),sQuery(id+"F4.wireOp",EDGE,"E8.4.10.0"),sQuery(id+"F4.wireOp",EDGE,"E8.4.10.1"),sQuery(id+"F4.wireOp",EDGE,"E8.4.10.2"),sQuery(id+"F4.wireOp",EDGE,"E8.4.10.3"),sQuery(id+"F4.wireOp",EDGE,"E8.4.11.0"),sQuery(id+"F4.wireOp",EDGE,"E8.4.11.1"),sQuery(id+"F4.wireOp",EDGE,"E8.4.11.2"),sQuery(id+"F4.wireOp",EDGE,"E8.4.11.3"),sQuery(id+"F4.wireOp",EDGE,"E8.5.0.2"),sQuery(id+"F4.wireOp",EDGE,"E8.5.0.3"),sQuery(id+"F4.wireOp",EDGE,"E8.5.1.0"),sQuery(id+"F4.wireOp",EDGE,"E8.5.1.1"),sQuery(id+"F4.wireOp",EDGE,"E8.5.1.2"),sQuery(id+"F4.wireOp",EDGE,"E8.5.1.3"),sQuery(id+"F4.wireOp",EDGE,"E8.5.2.0"),sQuery(id+"F4.wireOp",EDGE,"E8.5.2.1"),sQuery(id+"F4.wireOp",EDGE,"E8.5.2.2"),sQuery(id+"F4.wireOp",EDGE,"E8.5.2.3"),sQuery(id+"F4.wireOp",EDGE,"E8.5.3.0"),sQuery(id+"F4.wireOp",EDGE,"E8.5.3.1"),sQuery(id+"F4.wireOp",EDGE,"E8.5.3.2"),sQuery(id+"F4.wireOp",EDGE,"E8.5.3.3"),sQuery(id+"F4.wireOp",EDGE,"E8.5.4.0"),sQuery(id+"F4.wireOp",EDGE,"E8.5.4.1"),sQuery(id+"F4.wireOp",EDGE,"E8.5.4.2"),sQuery(id+"F4.wireOp",EDGE,"E8.5.4.3"),sQuery(id+"F4.wireOp",EDGE,"E8.5.5.0"),sQuery(id+"F4.wireOp",EDGE,"E8.5.5.1"),sQuery(id+"F4.wireOp",EDGE,"E8.5.5.2"),sQuery(id+"F4.wireOp",EDGE,"E8.5.5.3"),sQuery(id+"F4.wireOp",EDGE,"E8.5.6.0"),sQuery(id+"F4.wireOp",EDGE,"E8.5.6.1"),sQuery(id+"F4.wireOp",EDGE,"E8.5.6.2"),sQuery(id+"F4.wireOp",EDGE,"E8.5.6.3"),sQuery(id+"F4.wireOp",EDGE,"E8.5.7.0"),sQuery(id+"F4.wireOp",EDGE,"E8.5.7.1"),sQuery(id+"F4.wireOp",EDGE,"E8.5.7.2"),sQuery(id+"F4.wireOp",EDGE,"E8.5.7.3"),sQuery(id+"F4.wireOp",EDGE,"E8.5.8.0"),sQuery(id+"F4.wireOp",EDGE,"E8.5.8.1"),sQuery(id+"F4.wireOp",EDGE,"E8.5.8.2"),sQuery(id+"F4.wireOp",EDGE,"E8.5.8.3"),sQuery(id+"F4.wireOp",EDGE,"E8.5.9.0"),sQuery(id+"F4.wireOp",EDGE,"E8.5.9.1"),sQuery(id+"F4.wireOp",EDGE,"E8.5.9.2"),sQuery(id+"F4.wireOp",EDGE,"E8.5.9.3"),sQuery(id+"F4.wireOp",EDGE,"E8.5.10.0"),sQuery(id+"F4.wireOp",EDGE,"E8.5.10.1"),sQuery(id+"F4.wireOp",EDGE,"E8.5.10.2"),sQuery(id+"F4.wireOp",EDGE,"E8.5.10.3"),sQuery(id+"F4.wireOp",EDGE,"E8.5.11.0"),sQuery(id+"F4.wireOp",EDGE,"E8.5.11.1"),sQuery(id+"F4.wireOp",EDGE,"E8.5.11.2"),sQuery(id+"F4.wireOp",EDGE,"E8.5.11.3"),sQuery(id+"F4.wireOp",EDGE,"E8.6.0.2"),sQuery(id+"F4.wireOp",EDGE,"E8.6.0.3"),sQuery(id+"F4.wireOp",EDGE,"E8.6.1.0"),sQuery(id+"F4.wireOp",EDGE,"E8.6.1.1"),sQuery(id+"F4.wireOp",EDGE,"E8.6.1.2"),sQuery(id+"F4.wireOp",EDGE,"E8.6.1.3"),sQuery(id+"F4.wireOp",EDGE,"E8.6.2.0"),sQuery(id+"F4.wireOp",EDGE,"E8.6.2.1"),sQuery(id+"F4.wireOp",EDGE,"E8.6.2.2"),sQuery(id+"F4.wireOp",EDGE,"E8.6.2.3"),sQuery(id+"F4.wireOp",EDGE,"E8.6.3.0"),sQuery(id+"F4.wireOp",EDGE,"E8.6.3.1"),sQuery(id+"F4.wireOp",EDGE,"E8.6.3.2"),sQuery(id+"F4.wireOp",EDGE,"E8.6.3.3"),sQuery(id+"F4.wireOp",EDGE,"E8.6.4.0"),sQuery(id+"F4.wireOp",EDGE,"E8.6.4.1"),sQuery(id+"F4.wireOp",EDGE,"E8.6.4.2"),sQuery(id+"F4.wireOp",EDGE,"E8.6.4.3"),sQuery(id+"F4.wireOp",EDGE,"E8.6.5.0"),sQuery(id+"F4.wireOp",EDGE,"E8.6.5.1"),sQuery(id+"F4.wireOp",EDGE,"E8.6.5.2"),sQuery(id+"F4.wireOp",EDGE,"E8.6.5.3"),sQuery(id+"F4.wireOp",EDGE,"E8.6.6.0"),sQuery(id+"F4.wireOp",EDGE,"E8.6.6.1"),sQuery(id+"F4.wireOp",EDGE,"E8.6.6.2"),sQuery(id+"F4.wireOp",EDGE,"E8.6.6.3"),sQuery(id+"F4.wireOp",EDGE,"E8.6.7.0"),sQuery(id+"F4.wireOp",EDGE,"E8.6.7.1"),sQuery(id+"F4.wireOp",EDGE,"E8.6.7.2"),sQuery(id+"F4.wireOp",EDGE,"E8.6.7.3"),sQuery(id+"F4.wireOp",EDGE,"E8.6.8.0"),sQuery(id+"F4.wireOp",EDGE,"E8.6.8.1"),sQuery(id+"F4.wireOp",EDGE,"E8.6.8.2"),sQuery(id+"F4.wireOp",EDGE,"E8.6.8.3"),sQuery(id+"F4.wireOp",EDGE,"E8.6.9.0"),sQuery(id+"F4.wireOp",EDGE,"E8.6.9.1"),sQuery(id+"F4.wireOp",EDGE,"E8.6.9.2"),sQuery(id+"F4.wireOp",EDGE,"E8.6.9.3"),sQuery(id+"F4.wireOp",EDGE,"E8.6.10.0"),sQuery(id+"F4.wireOp",EDGE,"E8.6.10.1"),sQuery(id+"F4.wireOp",EDGE,"E8.6.10.2"),sQuery(id+"F4.wireOp",EDGE,"E8.6.10.3"),sQuery(id+"F4.wireOp",EDGE,"E8.6.11.0"),sQuery(id+"F4.wireOp",EDGE,"E8.6.11.1"),sQuery(id+"F4.wireOp",EDGE,"E8.6.11.2"),sQuery(id+"F4.wireOp",EDGE,"E8.6.11.3"),sQuery(id+"F4.wireOp",EDGE,"E8.7.0.2"),sQuery(id+"F4.wireOp",EDGE,"E8.7.0.3"),sQuery(id+"F4.wireOp",EDGE,"E8.7.1.0"),sQuery(id+"F4.wireOp",EDGE,"E8.7.1.1"),sQuery(id+"F4.wireOp",EDGE,"E8.7.1.2"),sQuery(id+"F4.wireOp",EDGE,"E8.7.1.3"),sQuery(id+"F4.wireOp",EDGE,"E8.7.2.0"),sQuery(id+"F4.wireOp",EDGE,"E8.7.2.1"),sQuery(id+"F4.wireOp",EDGE,"E8.7.2.2"),sQuery(id+"F4.wireOp",EDGE,"E8.7.2.3"),sQuery(id+"F4.wireOp",EDGE,"E8.7.3.0"),sQuery(id+"F4.wireOp",EDGE,"E8.7.3.1"),sQuery(id+"F4.wireOp",EDGE,"E8.7.3.2"),sQuery(id+"F4.wireOp",EDGE,"E8.7.3.3"),sQuery(id+"F4.wireOp",EDGE,"E8.7.4.0"),sQuery(id+"F4.wireOp",EDGE,"E8.7.4.1"),sQuery(id+"F4.wireOp",EDGE,"E8.7.4.2"),sQuery(id+"F4.wireOp",EDGE,"E8.7.4.3"),sQuery(id+"F4.wireOp",EDGE,"E8.7.5.0"),sQuery(id+"F4.wireOp",EDGE,"E8.7.5.1"),sQuery(id+"F4.wireOp",EDGE,"E8.7.5.2"),sQuery(id+"F4.wireOp",EDGE,"E8.7.5.3"),sQuery(id+"F4.wireOp",EDGE,"E8.7.6.0"),sQuery(id+"F4.wireOp",EDGE,"E8.7.6.1"),sQuery(id+"F4.wireOp",EDGE,"E8.7.6.2"),sQuery(id+"F4.wireOp",EDGE,"E8.7.6.3"),sQuery(id+"F4.wireOp",EDGE,"E8.7.7.0"),sQuery(id+"F4.wireOp",EDGE,"E8.7.7.1"),sQuery(id+"F4.wireOp",EDGE,"E8.7.7.2"),sQuery(id+"F4.wireOp",EDGE,"E8.7.7.3"),sQuery(id+"F4.wireOp",EDGE,"E8.7.8.0"),sQuery(id+"F4.wireOp",EDGE,"E8.7.8.1"),sQuery(id+"F4.wireOp",EDGE,"E8.7.8.2"),sQuery(id+"F4.wireOp",EDGE,"E8.7.8.3"),sQuery(id+"F4.wireOp",EDGE,"E8.7.9.0"),sQuery(id+"F4.wireOp",EDGE,"E8.7.9.1"),sQuery(id+"F4.wireOp",EDGE,"E8.7.9.2"),sQuery(id+"F4.wireOp",EDGE,"E8.7.9.3"),sQuery(id+"F4.wireOp",EDGE,"E8.7.10.0"),sQuery(id+"F4.wireOp",EDGE,"E8.7.10.1"),sQuery(id+"F4.wireOp",EDGE,"E8.7.10.2"),sQuery(id+"F4.wireOp",EDGE,"E8.7.10.3"),sQuery(id+"F4.wireOp",EDGE,"E8.7.11.0"),sQuery(id+"F4.wireOp",EDGE,"E8.7.11.1"),sQuery(id+"F4.wireOp",EDGE,"E8.7.11.2"),sQuery(id+"F4.wireOp",EDGE,"E8.7.11.3"),sQuery(id+"F4.wireOp",EDGE,"E8.8.0.2"),sQuery(id+"F4.wireOp",EDGE,"E8.8.0.3"),sQuery(id+"F4.wireOp",EDGE,"E8.8.1.0"),sQuery(id+"F4.wireOp",EDGE,"E8.8.1.1"),sQuery(id+"F4.wireOp",EDGE,"E8.8.1.2"),sQuery(id+"F4.wireOp",EDGE,"E8.8.1.3"),sQuery(id+"F4.wireOp",EDGE,"E8.8.2.0"),sQuery(id+"F4.wireOp",EDGE,"E8.8.2.1"),sQuery(id+"F4.wireOp",EDGE,"E8.8.2.2"),sQuery(id+"F4.wireOp",EDGE,"E8.8.2.3"),sQuery(id+"F4.wireOp",EDGE,"E8.8.3.0"),sQuery(id+"F4.wireOp",EDGE,"E8.8.3.1"),sQuery(id+"F4.wireOp",EDGE,"E8.8.3.2"),sQuery(id+"F4.wireOp",EDGE,"E8.8.3.3"),sQuery(id+"F4.wireOp",EDGE,"E8.8.4.0"),sQuery(id+"F4.wireOp",EDGE,"E8.8.4.1"),sQuery(id+"F4.wireOp",EDGE,"E8.8.4.2"),sQuery(id+"F4.wireOp",EDGE,"E8.8.4.3"),sQuery(id+"F4.wireOp",EDGE,"E8.8.5.0"),sQuery(id+"F4.wireOp",EDGE,"E8.8.5.1"),sQuery(id+"F4.wireOp",EDGE,"E8.8.5.2"),sQuery(id+"F4.wireOp",EDGE,"E8.8.5.3"),sQuery(id+"F4.wireOp",EDGE,"E8.8.6.0"),sQuery(id+"F4.wireOp",EDGE,"E8.8.6.1"),sQuery(id+"F4.wireOp",EDGE,"E8.8.6.2"),sQuery(id+"F4.wireOp",EDGE,"E8.8.6.3"),sQuery(id+"F4.wireOp",EDGE,"E8.8.7.0"),sQuery(id+"F4.wireOp",EDGE,"E8.8.7.1"),sQuery(id+"F4.wireOp",EDGE,"E8.8.7.2"),sQuery(id+"F4.wireOp",EDGE,"E8.8.7.3"),sQuery(id+"F4.wireOp",EDGE,"E8.8.8.0"),sQuery(id+"F4.wireOp",EDGE,"E8.8.8.1"),sQuery(id+"F4.wireOp",EDGE,"E8.8.8.2"),sQuery(id+"F4.wireOp",EDGE,"E8.8.8.3"),sQuery(id+"F4.wireOp",EDGE,"E8.8.9.0"),sQuery(id+"F4.wireOp",EDGE,"E8.8.9.1"),sQuery(id+"F4.wireOp",EDGE,"E8.8.9.2"),sQuery(id+"F4.wireOp",EDGE,"E8.8.9.3"),sQuery(id+"F4.wireOp",EDGE,"E8.8.10.0"),sQuery(id+"F4.wireOp",EDGE,"E8.8.10.1"),sQuery(id+"F4.wireOp",EDGE,"E8.8.10.2"),sQuery(id+"F4.wireOp",EDGE,"E8.8.10.3"),sQuery(id+"F4.wireOp",EDGE,"E8.8.11.0"),sQuery(id+"F4.wireOp",EDGE,"E8.8.11.1"),sQuery(id+"F4.wireOp",EDGE,"E8.8.11.2"),sQuery(id+"F4.wireOp",EDGE,"E8.8.11.3"),sQuery(id+"F4.wireOp",EDGE,"E8.9.0.2"),sQuery(id+"F4.wireOp",EDGE,"E8.9.0.3"),sQuery(id+"F4.wireOp",EDGE,"E8.9.1.0"),sQuery(id+"F4.wireOp",EDGE,"E8.9.1.1"),sQuery(id+"F4.wireOp",EDGE,"E8.9.1.2"),sQuery(id+"F4.wireOp",EDGE,"E8.9.1.3"),sQuery(id+"F4.wireOp",EDGE,"E8.9.2.0"),sQuery(id+"F4.wireOp",EDGE,"E8.9.2.1"),sQuery(id+"F4.wireOp",EDGE,"E8.9.2.2"),sQuery(id+"F4.wireOp",EDGE,"E8.9.2.3"),sQuery(id+"F4.wireOp",EDGE,"E8.9.3.0"),sQuery(id+"F4.wireOp",EDGE,"E8.9.3.1"),sQuery(id+"F4.wireOp",EDGE,"E8.9.3.2"),sQuery(id+"F4.wireOp",EDGE,"E8.9.3.3"),sQuery(id+"F4.wireOp",EDGE,"E8.9.4.0"),sQuery(id+"F4.wireOp",EDGE,"E8.9.4.1"),sQuery(id+"F4.wireOp",EDGE,"E8.9.4.2"),sQuery(id+"F4.wireOp",EDGE,"E8.9.4.3"),sQuery(id+"F4.wireOp",EDGE,"E8.9.5.0"),sQuery(id+"F4.wireOp",EDGE,"E8.9.5.1"),sQuery(id+"F4.wireOp",EDGE,"E8.9.5.2"),sQuery(id+"F4.wireOp",EDGE,"E8.9.5.3"),sQuery(id+"F4.wireOp",EDGE,"E8.9.6.0"),sQuery(id+"F4.wireOp",EDGE,"E8.9.6.1"),sQuery(id+"F4.wireOp",EDGE,"E8.9.6.2"),sQuery(id+"F4.wireOp",EDGE,"E8.9.6.3"),sQuery(id+"F4.wireOp",EDGE,"E8.9.7.0"),sQuery(id+"F4.wireOp",EDGE,"E8.9.7.1"),sQuery(id+"F4.wireOp",EDGE,"E8.9.7.2"),sQuery(id+"F4.wireOp",EDGE,"E8.9.7.3"),sQuery(id+"F4.wireOp",EDGE,"E8.9.8.0"),sQuery(id+"F4.wireOp",EDGE,"E8.9.8.1"),sQuery(id+"F4.wireOp",EDGE,"E8.9.8.2"),sQuery(id+"F4.wireOp",EDGE,"E8.9.8.3"),sQuery(id+"F4.wireOp",EDGE,"E8.9.9.0"),sQuery(id+"F4.wireOp",EDGE,"E8.9.9.1"),sQuery(id+"F4.wireOp",EDGE,"E8.9.9.2"),sQuery(id+"F4.wireOp",EDGE,"E8.9.9.3"),sQuery(id+"F4.wireOp",EDGE,"E8.9.10.0"),sQuery(id+"F4.wireOp",EDGE,"E8.9.10.1"),sQuery(id+"F4.wireOp",EDGE,"E8.9.10.2"),sQuery(id+"F4.wireOp",EDGE,"E8.9.10.3"),sQuery(id+"F4.wireOp",EDGE,"E8.9.11.0"),sQuery(id+"F4.wireOp",EDGE,"E8.9.11.1"),sQuery(id+"F4.wireOp",EDGE,"E8.9.11.2"),sQuery(id+"F4.wireOp",EDGE,"E8.9.11.3"),sQuery(id+"F4.wireOp",EDGE,"E8.10.0.2"),sQuery(id+"F4.wireOp",EDGE,"E8.10.0.3"),sQuery(id+"F4.wireOp",EDGE,"E8.10.1.0"),sQuery(id+"F4.wireOp",EDGE,"E8.10.1.1"),sQuery(id+"F4.wireOp",EDGE,"E8.10.1.2"),sQuery(id+"F4.wireOp",EDGE,"E8.10.1.3"),sQuery(id+"F4.wireOp",EDGE,"E8.10.2.0"),sQuery(id+"F4.wireOp",EDGE,"E8.10.2.1"),sQuery(id+"F4.wireOp",EDGE,"E8.10.2.2"),sQuery(id+"F4.wireOp",EDGE,"E8.10.2.3"),sQuery(id+"F4.wireOp",EDGE,"E8.10.3.0"),sQuery(id+"F4.wireOp",EDGE,"E8.10.3.1"),sQuery(id+"F4.wireOp",EDGE,"E8.10.3.2"),sQuery(id+"F4.wireOp",EDGE,"E8.10.3.3"),sQuery(id+"F4.wireOp",EDGE,"E8.10.4.0"),sQuery(id+"F4.wireOp",EDGE,"E8.10.4.1"),sQuery(id+"F4.wireOp",EDGE,"E8.10.4.2"),sQuery(id+"F4.wireOp",EDGE,"E8.10.4.3"),sQuery(id+"F4.wireOp",EDGE,"E8.10.5.0"),sQuery(id+"F4.wireOp",EDGE,"E8.10.5.1"),sQuery(id+"F4.wireOp",EDGE,"E8.10.5.2"),sQuery(id+"F4.wireOp",EDGE,"E8.10.5.3"),sQuery(id+"F4.wireOp",EDGE,"E8.10.6.0"),sQuery(id+"F4.wireOp",EDGE,"E8.10.6.1"),sQuery(id+"F4.wireOp",EDGE,"E8.10.6.2"),sQuery(id+"F4.wireOp",EDGE,"E8.10.6.3"),sQuery(id+"F4.wireOp",EDGE,"E8.10.7.0"),sQuery(id+"F4.wireOp",EDGE,"E8.10.7.1"),sQuery(id+"F4.wireOp",EDGE,"E8.10.7.2"),sQuery(id+"F4.wireOp",EDGE,"E8.10.7.3"),sQuery(id+"F4.wireOp",EDGE,"E8.10.8.0"),sQuery(id+"F4.wireOp",EDGE,"E8.10.8.1"),sQuery(id+"F4.wireOp",EDGE,"E8.10.8.2"),sQuery(id+"F4.wireOp",EDGE,"E8.10.8.3"),sQuery(id+"F4.wireOp",EDGE,"E8.10.9.0"),sQuery(id+"F4.wireOp",EDGE,"E8.10.9.1"),sQuery(id+"F4.wireOp",EDGE,"E8.10.9.2"),sQuery(id+"F4.wireOp",EDGE,"E8.10.9.3"),sQuery(id+"F4.wireOp",EDGE,"E8.10.10.0"),sQuery(id+"F4.wireOp",EDGE,"E8.10.10.1"),sQuery(id+"F4.wireOp",EDGE,"E8.10.10.2"),sQuery(id+"F4.wireOp",EDGE,"E8.10.10.3"),sQuery(id+"F4.wireOp",EDGE,"E8.10.11.0"),sQuery(id+"F4.wireOp",EDGE,"E8.10.11.1"),sQuery(id+"F4.wireOp",EDGE,"E8.10.11.2"),sQuery(id+"F4.wireOp",EDGE,"E8.10.11.3"),sQuery(id+"F4.wireOp",EDGE,"E8.11.0.2"),sQuery(id+"F4.wireOp",EDGE,"E8.11.0.3"),sQuery(id+"F4.wireOp",EDGE,"E8.11.1.0"),sQuery(id+"F4.wireOp",EDGE,"E8.11.1.1"),sQuery(id+"F4.wireOp",EDGE,"E8.11.1.2"),sQuery(id+"F4.wireOp",EDGE,"E8.11.1.3"),sQuery(id+"F4.wireOp",EDGE,"E8.11.2.0"),sQuery(id+"F4.wireOp",EDGE,"E8.11.2.1"),sQuery(id+"F4.wireOp",EDGE,"E8.11.2.2"),sQuery(id+"F4.wireOp",EDGE,"E8.11.2.3"),sQuery(id+"F4.wireOp",EDGE,"E8.11.3.0"),sQuery(id+"F4.wireOp",EDGE,"E8.11.3.1"),sQuery(id+"F4.wireOp",EDGE,"E8.11.3.2"),sQuery(id+"F4.wireOp",EDGE,"E8.11.3.3"),sQuery(id+"F4.wireOp",EDGE,"E8.11.4.0"),sQuery(id+"F4.wireOp",EDGE,"E8.11.4.1"),sQuery(id+"F4.wireOp",EDGE,"E8.11.4.2"),sQuery(id+"F4.wireOp",EDGE,"E8.11.4.3"),sQuery(id+"F4.wireOp",EDGE,"E8.11.5.0"),sQuery(id+"F4.wireOp",EDGE,"E8.11.5.1"),sQuery(id+"F4.wireOp",EDGE,"E8.11.5.2"),sQuery(id+"F4.wireOp",EDGE,"E8.11.5.3"),sQuery(id+"F4.wireOp",EDGE,"E8.11.6.0"),sQuery(id+"F4.wireOp",EDGE,"E8.11.6.1"),sQuery(id+"F4.wireOp",EDGE,"E8.11.6.2"),sQuery(id+"F4.wireOp",EDGE,"E8.11.6.3"),sQuery(id+"F4.wireOp",EDGE,"E8.11.7.0"),sQuery(id+"F4.wireOp",EDGE,"E8.11.7.1"),sQuery(id+"F4.wireOp",EDGE,"E8.11.7.2"),sQuery(id+"F4.wireOp",EDGE,"E8.11.7.3"),sQuery(id+"F4.wireOp",EDGE,"E8.11.8.0"),sQuery(id+"F4.wireOp",EDGE,"E8.11.8.1"),sQuery(id+"F4.wireOp",EDGE,"E8.11.8.2"),sQuery(id+"F4.wireOp",EDGE,"E8.11.8.3"),sQuery(id+"F4.wireOp",EDGE,"E8.11.9.0"),sQuery(id+"F4.wireOp",EDGE,"E8.11.9.1"),sQuery(id+"F4.wireOp",EDGE,"E8.11.9.2"),sQuery(id+"F4.wireOp",EDGE,"E8.11.9.3"),sQuery(id+"F4.wireOp",EDGE,"E8.11.10.0"),sQuery(id+"F4.wireOp",EDGE,"E8.11.10.1"),sQuery(id+"F4.wireOp",EDGE,"E8.11.10.2"),sQuery(id+"F4.wireOp",EDGE,"E8.11.10.3"),sQuery(id+"F4.wireOp",EDGE,"E8.11.11.0"),sQuery(id+"F4.wireOp",EDGE,"E8.11.11.1"),sQuery(id+"F4.wireOp",EDGE,"E8.11.11.2"),sQuery(id+"F4.wireOp",EDGE,"E8.11.11.3"),sQuery(id+"F4.wireOp",EDGE,"E9.bottom"),sQuery(id+"F4.wireOp",EDGE,"E10.bottom"),sQuery(id+"F4.wireOp",EDGE,"E10.top"),sQuery(id+"F4.wireOp",EDGE,"E10.left"),sQuery(id+"F4.wireOp",EDGE,"E10.right")])]});
            transform(context, id + "F9", {"entities" : qUnion([Q0]), "transformType" : TransformType.TRANSLATION_3D, "dx" : -50 * mm, "dy" : 0 * mm, "dz" : -50 * mm, "makeCopy" : false});
        }
        {
            var Q0;
            Q0=makeQuery(id+"F5.opExtrude","SWEPT_BODY",BODY,{"disambiguationData":[OSD([sQuery(id+"F4.wireOp",EDGE,"E8.1.0.2"),sQuery(id+"F4.wireOp",EDGE,"E8.1.0.3"),sQuery(id+"F4.wireOp",EDGE,"E8.1.1.0"),sQuery(id+"F4.wireOp",EDGE,"E8.1.1.1"),sQuery(id+"F4.wireOp",EDGE,"E8.1.1.2"),sQuery(id+"F4.wireOp",EDGE,"E8.1.1.3"),sQuery(id+"F4.wireOp",EDGE,"E8.1.2.0"),sQuery(id+"F4.wireOp",EDGE,"E8.1.2.1"),sQuery(id+"F4.wireOp",EDGE,"E8.1.2.2"),sQuery(id+"F4.wireOp",EDGE,"E8.1.2.3"),sQuery(id+"F4.wireOp",EDGE,"E8.1.3.0"),sQuery(id+"F4.wireOp",EDGE,"E8.1.3.1"),sQuery(id+"F4.wireOp",EDGE,"E8.1.3.2"),sQuery(id+"F4.wireOp",EDGE,"E8.1.3.3"),sQuery(id+"F4.wireOp",EDGE,"E8.1.4.0"),sQuery(id+"F4.wireOp",EDGE,"E8.1.4.1"),sQuery(id+"F4.wireOp",EDGE,"E8.1.4.2"),sQuery(id+"F4.wireOp",EDGE,"E8.1.4.3"),sQuery(id+"F4.wireOp",EDGE,"E8.1.5.0"),sQuery(id+"F4.wireOp",EDGE,"E8.1.5.1"),sQuery(id+"F4.wireOp",EDGE,"E8.1.5.2"),sQuery(id+"F4.wireOp",EDGE,"E8.1.5.3"),sQuery(id+"F4.wireOp",EDGE,"E8.1.6.0"),sQuery(id+"F4.wireOp",EDGE,"E8.1.6.1"),sQuery(id+"F4.wireOp",EDGE,"E8.1.6.2"),sQuery(id+"F4.wireOp",EDGE,"E8.1.6.3"),sQuery(id+"F4.wireOp",EDGE,"E8.1.7.0"),sQuery(id+"F4.wireOp",EDGE,"E8.1.7.1"),sQuery(id+"F4.wireOp",EDGE,"E8.1.7.2"),sQuery(id+"F4.wireOp",EDGE,"E8.1.7.3"),sQuery(id+"F4.wireOp",EDGE,"E8.1.8.0"),sQuery(id+"F4.wireOp",EDGE,"E8.1.8.1"),sQuery(id+"F4.wireOp",EDGE,"E8.1.8.2"),sQuery(id+"F4.wireOp",EDGE,"E8.1.8.3"),sQuery(id+"F4.wireOp",EDGE,"E8.1.9.0"),sQuery(id+"F4.wireOp",EDGE,"E8.1.9.1"),sQuery(id+"F4.wireOp",EDGE,"E8.1.9.2"),sQuery(id+"F4.wireOp",EDGE,"E8.1.9.3"),sQuery(id+"F4.wireOp",EDGE,"E8.1.10.0"),sQuery(id+"F4.wireOp",EDGE,"E8.1.10.1"),sQuery(id+"F4.wireOp",EDGE,"E8.1.10.2"),sQuery(id+"F4.wireOp",EDGE,"E8.1.10.3"),sQuery(id+"F4.wireOp",EDGE,"E8.1.11.0"),sQuery(id+"F4.wireOp",EDGE,"E8.1.11.1"),sQuery(id+"F4.wireOp",EDGE,"E8.1.11.2"),sQuery(id+"F4.wireOp",EDGE,"E8.1.11.3"),sQuery(id+"F4.wireOp",EDGE,"E8.2.0.2"),sQuery(id+"F4.wireOp",EDGE,"E8.2.0.3"),sQuery(id+"F4.wireOp",EDGE,"E8.2.1.0"),sQuery(id+"F4.wireOp",EDGE,"E8.2.1.1"),sQuery(id+"F4.wireOp",EDGE,"E8.2.1.2"),sQuery(id+"F4.wireOp",EDGE,"E8.2.1.3"),sQuery(id+"F4.wireOp",EDGE,"E8.2.2.0"),sQuery(id+"F4.wireOp",EDGE,"E8.2.2.1"),sQuery(id+"F4.wireOp",EDGE,"E8.2.2.2"),sQuery(id+"F4.wireOp",EDGE,"E8.2.2.3"),sQuery(id+"F4.wireOp",EDGE,"E8.2.3.0"),sQuery(id+"F4.wireOp",EDGE,"E8.2.3.1"),sQuery(id+"F4.wireOp",EDGE,"E8.2.3.2"),sQuery(id+"F4.wireOp",EDGE,"E8.2.3.3"),sQuery(id+"F4.wireOp",EDGE,"E8.2.4.0"),sQuery(id+"F4.wireOp",EDGE,"E8.2.4.1"),sQuery(id+"F4.wireOp",EDGE,"E8.2.4.2"),sQuery(id+"F4.wireOp",EDGE,"E8.2.4.3"),sQuery(id+"F4.wireOp",EDGE,"E8.2.5.0"),sQuery(id+"F4.wireOp",EDGE,"E8.2.5.1"),sQuery(id+"F4.wireOp",EDGE,"E8.2.5.2"),sQuery(id+"F4.wireOp",EDGE,"E8.2.5.3"),sQuery(id+"F4.wireOp",EDGE,"E8.2.6.0"),sQuery(id+"F4.wireOp",EDGE,"E8.2.6.1"),sQuery(id+"F4.wireOp",EDGE,"E8.2.6.2"),sQuery(id+"F4.wireOp",EDGE,"E8.2.6.3"),sQuery(id+"F4.wireOp",EDGE,"E8.2.7.0"),sQuery(id+"F4.wireOp",EDGE,"E8.2.7.1"),sQuery(id+"F4.wireOp",EDGE,"E8.2.7.2"),sQuery(id+"F4.wireOp",EDGE,"E8.2.7.3"),sQuery(id+"F4.wireOp",EDGE,"E8.2.8.0"),sQuery(id+"F4.wireOp",EDGE,"E8.2.8.1"),sQuery(id+"F4.wireOp",EDGE,"E8.2.8.2"),sQuery(id+"F4.wireOp",EDGE,"E8.2.8.3"),sQuery(id+"F4.wireOp",EDGE,"E8.2.9.0"),sQuery(id+"F4.wireOp",EDGE,"E8.2.9.1"),sQuery(id+"F4.wireOp",EDGE,"E8.2.9.2"),sQuery(id+"F4.wireOp",EDGE,"E8.2.9.3"),sQuery(id+"F4.wireOp",EDGE,"E8.2.10.0"),sQuery(id+"F4.wireOp",EDGE,"E8.2.10.1"),sQuery(id+"F4.wireOp",EDGE,"E8.2.10.2"),sQuery(id+"F4.wireOp",EDGE,"E8.2.10.3"),sQuery(id+"F4.wireOp",EDGE,"E8.2.11.0"),sQuery(id+"F4.wireOp",EDGE,"E8.2.11.1"),sQuery(id+"F4.wireOp",EDGE,"E8.2.11.2"),sQuery(id+"F4.wireOp",EDGE,"E8.2.11.3"),sQuery(id+"F4.wireOp",EDGE,"E8.3.0.2"),sQuery(id+"F4.wireOp",EDGE,"E8.3.0.3"),sQuery(id+"F4.wireOp",EDGE,"E8.3.1.0"),sQuery(id+"F4.wireOp",EDGE,"E8.3.1.1"),sQuery(id+"F4.wireOp",EDGE,"E8.3.1.2"),sQuery(id+"F4.wireOp",EDGE,"E8.3.1.3"),sQuery(id+"F4.wireOp",EDGE,"E8.3.2.0"),sQuery(id+"F4.wireOp",EDGE,"E8.3.2.1"),sQuery(id+"F4.wireOp",EDGE,"E8.3.2.2"),sQuery(id+"F4.wireOp",EDGE,"E8.3.2.3"),sQuery(id+"F4.wireOp",EDGE,"E8.3.3.0"),sQuery(id+"F4.wireOp",EDGE,"E8.3.3.1"),sQuery(id+"F4.wireOp",EDGE,"E8.3.3.2"),sQuery(id+"F4.wireOp",EDGE,"E8.3.3.3"),sQuery(id+"F4.wireOp",EDGE,"E8.3.4.0"),sQuery(id+"F4.wireOp",EDGE,"E8.3.4.1"),sQuery(id+"F4.wireOp",EDGE,"E8.3.4.2"),sQuery(id+"F4.wireOp",EDGE,"E8.3.4.3"),sQuery(id+"F4.wireOp",EDGE,"E8.3.5.0"),sQuery(id+"F4.wireOp",EDGE,"E8.3.5.1"),sQuery(id+"F4.wireOp",EDGE,"E8.3.5.2"),sQuery(id+"F4.wireOp",EDGE,"E8.3.5.3"),sQuery(id+"F4.wireOp",EDGE,"E8.3.6.0"),sQuery(id+"F4.wireOp",EDGE,"E8.3.6.1"),sQuery(id+"F4.wireOp",EDGE,"E8.3.6.2"),sQuery(id+"F4.wireOp",EDGE,"E8.3.6.3"),sQuery(id+"F4.wireOp",EDGE,"E8.3.7.0"),sQuery(id+"F4.wireOp",EDGE,"E8.3.7.1"),sQuery(id+"F4.wireOp",EDGE,"E8.3.7.2"),sQuery(id+"F4.wireOp",EDGE,"E8.3.7.3"),sQuery(id+"F4.wireOp",EDGE,"E8.3.8.0"),sQuery(id+"F4.wireOp",EDGE,"E8.3.8.1"),sQuery(id+"F4.wireOp",EDGE,"E8.3.8.2"),sQuery(id+"F4.wireOp",EDGE,"E8.3.8.3"),sQuery(id+"F4.wireOp",EDGE,"E8.3.9.0"),sQuery(id+"F4.wireOp",EDGE,"E8.3.9.1"),sQuery(id+"F4.wireOp",EDGE,"E8.3.9.2"),sQuery(id+"F4.wireOp",EDGE,"E8.3.9.3"),sQuery(id+"F4.wireOp",EDGE,"E8.3.10.0"),sQuery(id+"F4.wireOp",EDGE,"E8.3.10.1"),sQuery(id+"F4.wireOp",EDGE,"E8.3.10.2"),sQuery(id+"F4.wireOp",EDGE,"E8.3.10.3"),sQuery(id+"F4.wireOp",EDGE,"E8.3.11.0"),sQuery(id+"F4.wireOp",EDGE,"E8.3.11.1"),sQuery(id+"F4.wireOp",EDGE,"E8.3.11.2"),sQuery(id+"F4.wireOp",EDGE,"E8.3.11.3"),sQuery(id+"F4.wireOp",EDGE,"E8.4.0.2"),sQuery(id+"F4.wireOp",EDGE,"E8.4.0.3"),sQuery(id+"F4.wireOp",EDGE,"E8.4.1.0"),sQuery(id+"F4.wireOp",EDGE,"E8.4.1.1"),sQuery(id+"F4.wireOp",EDGE,"E8.4.1.2"),sQuery(id+"F4.wireOp",EDGE,"E8.4.1.3"),sQuery(id+"F4.wireOp",EDGE,"E8.4.2.0"),sQuery(id+"F4.wireOp",EDGE,"E8.4.2.1"),sQuery(id+"F4.wireOp",EDGE,"E8.4.2.2"),sQuery(id+"F4.wireOp",EDGE,"E8.4.2.3"),sQuery(id+"F4.wireOp",EDGE,"E8.4.3.0"),sQuery(id+"F4.wireOp",EDGE,"E8.4.3.1"),sQuery(id+"F4.wireOp",EDGE,"E8.4.3.2"),sQuery(id+"F4.wireOp",EDGE,"E8.4.3.3"),sQuery(id+"F4.wireOp",EDGE,"E8.4.4.0"),sQuery(id+"F4.wireOp",EDGE,"E8.4.4.1"),sQuery(id+"F4.wireOp",EDGE,"E8.4.4.2"),sQuery(id+"F4.wireOp",EDGE,"E8.4.4.3"),sQuery(id+"F4.wireOp",EDGE,"E8.4.5.0"),sQuery(id+"F4.wireOp",EDGE,"E8.4.5.1"),sQuery(id+"F4.wireOp",EDGE,"E8.4.5.2"),sQuery(id+"F4.wireOp",EDGE,"E8.4.5.3"),sQuery(id+"F4.wireOp",EDGE,"E8.4.6.0"),sQuery(id+"F4.wireOp",EDGE,"E8.4.6.1"),sQuery(id+"F4.wireOp",EDGE,"E8.4.6.2"),sQuery(id+"F4.wireOp",EDGE,"E8.4.6.3"),sQuery(id+"F4.wireOp",EDGE,"E8.4.7.0"),sQuery(id+"F4.wireOp",EDGE,"E8.4.7.1"),sQuery(id+"F4.wireOp",EDGE,"E8.4.7.2"),sQuery(id+"F4.wireOp",EDGE,"E8.4.7.3"),sQuery(id+"F4.wireOp",EDGE,"E8.4.8.0"),sQuery(id+"F4.wireOp",EDGE,"E8.4.8.1"),sQuery(id+"F4.wireOp",EDGE,"E8.4.8.2"),sQuery(id+"F4.wireOp",EDGE,"E8.4.8.3"),sQuery(id+"F4.wireOp",EDGE,"E8.4.9.0"),sQuery(id+"F4.wireOp",EDGE,"E8.4.9.1"),sQuery(id+"F4.wireOp",EDGE,"E8.4.9.2"),sQuery(id+"F4.wireOp",EDGE,"E8.4.9.3"),sQuery(id+"F4.wireOp",EDGE,"E8.4.10.0"),sQuery(id+"F4.wireOp",EDGE,"E8.4.10.1"),sQuery(id+"F4.wireOp",EDGE,"E8.4.10.2"),sQuery(id+"F4.wireOp",EDGE,"E8.4.10.3"),sQuery(id+"F4.wireOp",EDGE,"E8.4.11.0"),sQuery(id+"F4.wireOp",EDGE,"E8.4.11.1"),sQuery(id+"F4.wireOp",EDGE,"E8.4.11.2"),sQuery(id+"F4.wireOp",EDGE,"E8.4.11.3"),sQuery(id+"F4.wireOp",EDGE,"E8.5.0.2"),sQuery(id+"F4.wireOp",EDGE,"E8.5.0.3"),sQuery(id+"F4.wireOp",EDGE,"E8.5.1.0"),sQuery(id+"F4.wireOp",EDGE,"E8.5.1.1"),sQuery(id+"F4.wireOp",EDGE,"E8.5.1.2"),sQuery(id+"F4.wireOp",EDGE,"E8.5.1.3"),sQuery(id+"F4.wireOp",EDGE,"E8.5.2.0"),sQuery(id+"F4.wireOp",EDGE,"E8.5.2.1"),sQuery(id+"F4.wireOp",EDGE,"E8.5.2.2"),sQuery(id+"F4.wireOp",EDGE,"E8.5.2.3"),sQuery(id+"F4.wireOp",EDGE,"E8.5.3.0"),sQuery(id+"F4.wireOp",EDGE,"E8.5.3.1"),sQuery(id+"F4.wireOp",EDGE,"E8.5.3.2"),sQuery(id+"F4.wireOp",EDGE,"E8.5.3.3"),sQuery(id+"F4.wireOp",EDGE,"E8.5.4.0"),sQuery(id+"F4.wireOp",EDGE,"E8.5.4.1"),sQuery(id+"F4.wireOp",EDGE,"E8.5.4.2"),sQuery(id+"F4.wireOp",EDGE,"E8.5.4.3"),sQuery(id+"F4.wireOp",EDGE,"E8.5.5.0"),sQuery(id+"F4.wireOp",EDGE,"E8.5.5.1"),sQuery(id+"F4.wireOp",EDGE,"E8.5.5.2"),sQuery(id+"F4.wireOp",EDGE,"E8.5.5.3"),sQuery(id+"F4.wireOp",EDGE,"E8.5.6.0"),sQuery(id+"F4.wireOp",EDGE,"E8.5.6.1"),sQuery(id+"F4.wireOp",EDGE,"E8.5.6.2"),sQuery(id+"F4.wireOp",EDGE,"E8.5.6.3"),sQuery(id+"F4.wireOp",EDGE,"E8.5.7.0"),sQuery(id+"F4.wireOp",EDGE,"E8.5.7.1"),sQuery(id+"F4.wireOp",EDGE,"E8.5.7.2"),sQuery(id+"F4.wireOp",EDGE,"E8.5.7.3"),sQuery(id+"F4.wireOp",EDGE,"E8.5.8.0"),sQuery(id+"F4.wireOp",EDGE,"E8.5.8.1"),sQuery(id+"F4.wireOp",EDGE,"E8.5.8.2"),sQuery(id+"F4.wireOp",EDGE,"E8.5.8.3"),sQuery(id+"F4.wireOp",EDGE,"E8.5.9.0"),sQuery(id+"F4.wireOp",EDGE,"E8.5.9.1"),sQuery(id+"F4.wireOp",EDGE,"E8.5.9.2"),sQuery(id+"F4.wireOp",EDGE,"E8.5.9.3"),sQuery(id+"F4.wireOp",EDGE,"E8.5.10.0"),sQuery(id+"F4.wireOp",EDGE,"E8.5.10.1"),sQuery(id+"F4.wireOp",EDGE,"E8.5.10.2"),sQuery(id+"F4.wireOp",EDGE,"E8.5.10.3"),sQuery(id+"F4.wireOp",EDGE,"E8.5.11.0"),sQuery(id+"F4.wireOp",EDGE,"E8.5.11.1"),sQuery(id+"F4.wireOp",EDGE,"E8.5.11.2"),sQuery(id+"F4.wireOp",EDGE,"E8.5.11.3"),sQuery(id+"F4.wireOp",EDGE,"E8.6.0.2"),sQuery(id+"F4.wireOp",EDGE,"E8.6.0.3"),sQuery(id+"F4.wireOp",EDGE,"E8.6.1.0"),sQuery(id+"F4.wireOp",EDGE,"E8.6.1.1"),sQuery(id+"F4.wireOp",EDGE,"E8.6.1.2"),sQuery(id+"F4.wireOp",EDGE,"E8.6.1.3"),sQuery(id+"F4.wireOp",EDGE,"E8.6.2.0"),sQuery(id+"F4.wireOp",EDGE,"E8.6.2.1"),sQuery(id+"F4.wireOp",EDGE,"E8.6.2.2"),sQuery(id+"F4.wireOp",EDGE,"E8.6.2.3"),sQuery(id+"F4.wireOp",EDGE,"E8.6.3.0"),sQuery(id+"F4.wireOp",EDGE,"E8.6.3.1"),sQuery(id+"F4.wireOp",EDGE,"E8.6.3.2"),sQuery(id+"F4.wireOp",EDGE,"E8.6.3.3"),sQuery(id+"F4.wireOp",EDGE,"E8.6.4.0"),sQuery(id+"F4.wireOp",EDGE,"E8.6.4.1"),sQuery(id+"F4.wireOp",EDGE,"E8.6.4.2"),sQuery(id+"F4.wireOp",EDGE,"E8.6.4.3"),sQuery(id+"F4.wireOp",EDGE,"E8.6.5.0"),sQuery(id+"F4.wireOp",EDGE,"E8.6.5.1"),sQuery(id+"F4.wireOp",EDGE,"E8.6.5.2"),sQuery(id+"F4.wireOp",EDGE,"E8.6.5.3"),sQuery(id+"F4.wireOp",EDGE,"E8.6.6.0"),sQuery(id+"F4.wireOp",EDGE,"E8.6.6.1"),sQuery(id+"F4.wireOp",EDGE,"E8.6.6.2"),sQuery(id+"F4.wireOp",EDGE,"E8.6.6.3"),sQuery(id+"F4.wireOp",EDGE,"E8.6.7.0"),sQuery(id+"F4.wireOp",EDGE,"E8.6.7.1"),sQuery(id+"F4.wireOp",EDGE,"E8.6.7.2"),sQuery(id+"F4.wireOp",EDGE,"E8.6.7.3"),sQuery(id+"F4.wireOp",EDGE,"E8.6.8.0"),sQuery(id+"F4.wireOp",EDGE,"E8.6.8.1"),sQuery(id+"F4.wireOp",EDGE,"E8.6.8.2"),sQuery(id+"F4.wireOp",EDGE,"E8.6.8.3"),sQuery(id+"F4.wireOp",EDGE,"E8.6.9.0"),sQuery(id+"F4.wireOp",EDGE,"E8.6.9.1"),sQuery(id+"F4.wireOp",EDGE,"E8.6.9.2"),sQuery(id+"F4.wireOp",EDGE,"E8.6.9.3"),sQuery(id+"F4.wireOp",EDGE,"E8.6.10.0"),sQuery(id+"F4.wireOp",EDGE,"E8.6.10.1"),sQuery(id+"F4.wireOp",EDGE,"E8.6.10.2"),sQuery(id+"F4.wireOp",EDGE,"E8.6.10.3"),sQuery(id+"F4.wireOp",EDGE,"E8.6.11.0"),sQuery(id+"F4.wireOp",EDGE,"E8.6.11.1"),sQuery(id+"F4.wireOp",EDGE,"E8.6.11.2"),sQuery(id+"F4.wireOp",EDGE,"E8.6.11.3"),sQuery(id+"F4.wireOp",EDGE,"E8.7.0.2"),sQuery(id+"F4.wireOp",EDGE,"E8.7.0.3"),sQuery(id+"F4.wireOp",EDGE,"E8.7.1.0"),sQuery(id+"F4.wireOp",EDGE,"E8.7.1.1"),sQuery(id+"F4.wireOp",EDGE,"E8.7.1.2"),sQuery(id+"F4.wireOp",EDGE,"E8.7.1.3"),sQuery(id+"F4.wireOp",EDGE,"E8.7.2.0"),sQuery(id+"F4.wireOp",EDGE,"E8.7.2.1"),sQuery(id+"F4.wireOp",EDGE,"E8.7.2.2"),sQuery(id+"F4.wireOp",EDGE,"E8.7.2.3"),sQuery(id+"F4.wireOp",EDGE,"E8.7.3.0"),sQuery(id+"F4.wireOp",EDGE,"E8.7.3.1"),sQuery(id+"F4.wireOp",EDGE,"E8.7.3.2"),sQuery(id+"F4.wireOp",EDGE,"E8.7.3.3"),sQuery(id+"F4.wireOp",EDGE,"E8.7.4.0"),sQuery(id+"F4.wireOp",EDGE,"E8.7.4.1"),sQuery(id+"F4.wireOp",EDGE,"E8.7.4.2"),sQuery(id+"F4.wireOp",EDGE,"E8.7.4.3"),sQuery(id+"F4.wireOp",EDGE,"E8.7.5.0"),sQuery(id+"F4.wireOp",EDGE,"E8.7.5.1"),sQuery(id+"F4.wireOp",EDGE,"E8.7.5.2"),sQuery(id+"F4.wireOp",EDGE,"E8.7.5.3"),sQuery(id+"F4.wireOp",EDGE,"E8.7.6.0"),sQuery(id+"F4.wireOp",EDGE,"E8.7.6.1"),sQuery(id+"F4.wireOp",EDGE,"E8.7.6.2"),sQuery(id+"F4.wireOp",EDGE,"E8.7.6.3"),sQuery(id+"F4.wireOp",EDGE,"E8.7.7.0"),sQuery(id+"F4.wireOp",EDGE,"E8.7.7.1"),sQuery(id+"F4.wireOp",EDGE,"E8.7.7.2"),sQuery(id+"F4.wireOp",EDGE,"E8.7.7.3"),sQuery(id+"F4.wireOp",EDGE,"E8.7.8.0"),sQuery(id+"F4.wireOp",EDGE,"E8.7.8.1"),sQuery(id+"F4.wireOp",EDGE,"E8.7.8.2"),sQuery(id+"F4.wireOp",EDGE,"E8.7.8.3"),sQuery(id+"F4.wireOp",EDGE,"E8.7.9.0"),sQuery(id+"F4.wireOp",EDGE,"E8.7.9.1"),sQuery(id+"F4.wireOp",EDGE,"E8.7.9.2"),sQuery(id+"F4.wireOp",EDGE,"E8.7.9.3"),sQuery(id+"F4.wireOp",EDGE,"E8.7.10.0"),sQuery(id+"F4.wireOp",EDGE,"E8.7.10.1"),sQuery(id+"F4.wireOp",EDGE,"E8.7.10.2"),sQuery(id+"F4.wireOp",EDGE,"E8.7.10.3"),sQuery(id+"F4.wireOp",EDGE,"E8.7.11.0"),sQuery(id+"F4.wireOp",EDGE,"E8.7.11.1"),sQuery(id+"F4.wireOp",EDGE,"E8.7.11.2"),sQuery(id+"F4.wireOp",EDGE,"E8.7.11.3"),sQuery(id+"F4.wireOp",EDGE,"E8.8.0.2"),sQuery(id+"F4.wireOp",EDGE,"E8.8.0.3"),sQuery(id+"F4.wireOp",EDGE,"E8.8.1.0"),sQuery(id+"F4.wireOp",EDGE,"E8.8.1.1"),sQuery(id+"F4.wireOp",EDGE,"E8.8.1.2"),sQuery(id+"F4.wireOp",EDGE,"E8.8.1.3"),sQuery(id+"F4.wireOp",EDGE,"E8.8.2.0"),sQuery(id+"F4.wireOp",EDGE,"E8.8.2.1"),sQuery(id+"F4.wireOp",EDGE,"E8.8.2.2"),sQuery(id+"F4.wireOp",EDGE,"E8.8.2.3"),sQuery(id+"F4.wireOp",EDGE,"E8.8.3.0"),sQuery(id+"F4.wireOp",EDGE,"E8.8.3.1"),sQuery(id+"F4.wireOp",EDGE,"E8.8.3.2"),sQuery(id+"F4.wireOp",EDGE,"E8.8.3.3"),sQuery(id+"F4.wireOp",EDGE,"E8.8.4.0"),sQuery(id+"F4.wireOp",EDGE,"E8.8.4.1"),sQuery(id+"F4.wireOp",EDGE,"E8.8.4.2"),sQuery(id+"F4.wireOp",EDGE,"E8.8.4.3"),sQuery(id+"F4.wireOp",EDGE,"E8.8.5.0"),sQuery(id+"F4.wireOp",EDGE,"E8.8.5.1"),sQuery(id+"F4.wireOp",EDGE,"E8.8.5.2"),sQuery(id+"F4.wireOp",EDGE,"E8.8.5.3"),sQuery(id+"F4.wireOp",EDGE,"E8.8.6.0"),sQuery(id+"F4.wireOp",EDGE,"E8.8.6.1"),sQuery(id+"F4.wireOp",EDGE,"E8.8.6.2"),sQuery(id+"F4.wireOp",EDGE,"E8.8.6.3"),sQuery(id+"F4.wireOp",EDGE,"E8.8.7.0"),sQuery(id+"F4.wireOp",EDGE,"E8.8.7.1"),sQuery(id+"F4.wireOp",EDGE,"E8.8.7.2"),sQuery(id+"F4.wireOp",EDGE,"E8.8.7.3"),sQuery(id+"F4.wireOp",EDGE,"E8.8.8.0"),sQuery(id+"F4.wireOp",EDGE,"E8.8.8.1"),sQuery(id+"F4.wireOp",EDGE,"E8.8.8.2"),sQuery(id+"F4.wireOp",EDGE,"E8.8.8.3"),sQuery(id+"F4.wireOp",EDGE,"E8.8.9.0"),sQuery(id+"F4.wireOp",EDGE,"E8.8.9.1"),sQuery(id+"F4.wireOp",EDGE,"E8.8.9.2"),sQuery(id+"F4.wireOp",EDGE,"E8.8.9.3"),sQuery(id+"F4.wireOp",EDGE,"E8.8.10.0"),sQuery(id+"F4.wireOp",EDGE,"E8.8.10.1"),sQuery(id+"F4.wireOp",EDGE,"E8.8.10.2"),sQuery(id+"F4.wireOp",EDGE,"E8.8.10.3"),sQuery(id+"F4.wireOp",EDGE,"E8.8.11.0"),sQuery(id+"F4.wireOp",EDGE,"E8.8.11.1"),sQuery(id+"F4.wireOp",EDGE,"E8.8.11.2"),sQuery(id+"F4.wireOp",EDGE,"E8.8.11.3"),sQuery(id+"F4.wireOp",EDGE,"E8.9.0.2"),sQuery(id+"F4.wireOp",EDGE,"E8.9.0.3"),sQuery(id+"F4.wireOp",EDGE,"E8.9.1.0"),sQuery(id+"F4.wireOp",EDGE,"E8.9.1.1"),sQuery(id+"F4.wireOp",EDGE,"E8.9.1.2"),sQuery(id+"F4.wireOp",EDGE,"E8.9.1.3"),sQuery(id+"F4.wireOp",EDGE,"E8.9.2.0"),sQuery(id+"F4.wireOp",EDGE,"E8.9.2.1"),sQuery(id+"F4.wireOp",EDGE,"E8.9.2.2"),sQuery(id+"F4.wireOp",EDGE,"E8.9.2.3"),sQuery(id+"F4.wireOp",EDGE,"E8.9.3.0"),sQuery(id+"F4.wireOp",EDGE,"E8.9.3.1"),sQuery(id+"F4.wireOp",EDGE,"E8.9.3.2"),sQuery(id+"F4.wireOp",EDGE,"E8.9.3.3"),sQuery(id+"F4.wireOp",EDGE,"E8.9.4.0"),sQuery(id+"F4.wireOp",EDGE,"E8.9.4.1"),sQuery(id+"F4.wireOp",EDGE,"E8.9.4.2"),sQuery(id+"F4.wireOp",EDGE,"E8.9.4.3"),sQuery(id+"F4.wireOp",EDGE,"E8.9.5.0"),sQuery(id+"F4.wireOp",EDGE,"E8.9.5.1"),sQuery(id+"F4.wireOp",EDGE,"E8.9.5.2"),sQuery(id+"F4.wireOp",EDGE,"E8.9.5.3"),sQuery(id+"F4.wireOp",EDGE,"E8.9.6.0"),sQuery(id+"F4.wireOp",EDGE,"E8.9.6.1"),sQuery(id+"F4.wireOp",EDGE,"E8.9.6.2"),sQuery(id+"F4.wireOp",EDGE,"E8.9.6.3"),sQuery(id+"F4.wireOp",EDGE,"E8.9.7.0"),sQuery(id+"F4.wireOp",EDGE,"E8.9.7.1"),sQuery(id+"F4.wireOp",EDGE,"E8.9.7.2"),sQuery(id+"F4.wireOp",EDGE,"E8.9.7.3"),sQuery(id+"F4.wireOp",EDGE,"E8.9.8.0"),sQuery(id+"F4.wireOp",EDGE,"E8.9.8.1"),sQuery(id+"F4.wireOp",EDGE,"E8.9.8.2"),sQuery(id+"F4.wireOp",EDGE,"E8.9.8.3"),sQuery(id+"F4.wireOp",EDGE,"E8.9.9.0"),sQuery(id+"F4.wireOp",EDGE,"E8.9.9.1"),sQuery(id+"F4.wireOp",EDGE,"E8.9.9.2"),sQuery(id+"F4.wireOp",EDGE,"E8.9.9.3"),sQuery(id+"F4.wireOp",EDGE,"E8.9.10.0"),sQuery(id+"F4.wireOp",EDGE,"E8.9.10.1"),sQuery(id+"F4.wireOp",EDGE,"E8.9.10.2"),sQuery(id+"F4.wireOp",EDGE,"E8.9.10.3"),sQuery(id+"F4.wireOp",EDGE,"E8.9.11.0"),sQuery(id+"F4.wireOp",EDGE,"E8.9.11.1"),sQuery(id+"F4.wireOp",EDGE,"E8.9.11.2"),sQuery(id+"F4.wireOp",EDGE,"E8.9.11.3"),sQuery(id+"F4.wireOp",EDGE,"E8.10.0.2"),sQuery(id+"F4.wireOp",EDGE,"E8.10.0.3"),sQuery(id+"F4.wireOp",EDGE,"E8.10.1.0"),sQuery(id+"F4.wireOp",EDGE,"E8.10.1.1"),sQuery(id+"F4.wireOp",EDGE,"E8.10.1.2"),sQuery(id+"F4.wireOp",EDGE,"E8.10.1.3"),sQuery(id+"F4.wireOp",EDGE,"E8.10.2.0"),sQuery(id+"F4.wireOp",EDGE,"E8.10.2.1"),sQuery(id+"F4.wireOp",EDGE,"E8.10.2.2"),sQuery(id+"F4.wireOp",EDGE,"E8.10.2.3"),sQuery(id+"F4.wireOp",EDGE,"E8.10.3.0"),sQuery(id+"F4.wireOp",EDGE,"E8.10.3.1"),sQuery(id+"F4.wireOp",EDGE,"E8.10.3.2"),sQuery(id+"F4.wireOp",EDGE,"E8.10.3.3"),sQuery(id+"F4.wireOp",EDGE,"E8.10.4.0"),sQuery(id+"F4.wireOp",EDGE,"E8.10.4.1"),sQuery(id+"F4.wireOp",EDGE,"E8.10.4.2"),sQuery(id+"F4.wireOp",EDGE,"E8.10.4.3"),sQuery(id+"F4.wireOp",EDGE,"E8.10.5.0"),sQuery(id+"F4.wireOp",EDGE,"E8.10.5.1"),sQuery(id+"F4.wireOp",EDGE,"E8.10.5.2"),sQuery(id+"F4.wireOp",EDGE,"E8.10.5.3"),sQuery(id+"F4.wireOp",EDGE,"E8.10.6.0"),sQuery(id+"F4.wireOp",EDGE,"E8.10.6.1"),sQuery(id+"F4.wireOp",EDGE,"E8.10.6.2"),sQuery(id+"F4.wireOp",EDGE,"E8.10.6.3"),sQuery(id+"F4.wireOp",EDGE,"E8.10.7.0"),sQuery(id+"F4.wireOp",EDGE,"E8.10.7.1"),sQuery(id+"F4.wireOp",EDGE,"E8.10.7.2"),sQuery(id+"F4.wireOp",EDGE,"E8.10.7.3"),sQuery(id+"F4.wireOp",EDGE,"E8.10.8.0"),sQuery(id+"F4.wireOp",EDGE,"E8.10.8.1"),sQuery(id+"F4.wireOp",EDGE,"E8.10.8.2"),sQuery(id+"F4.wireOp",EDGE,"E8.10.8.3"),sQuery(id+"F4.wireOp",EDGE,"E8.10.9.0"),sQuery(id+"F4.wireOp",EDGE,"E8.10.9.1"),sQuery(id+"F4.wireOp",EDGE,"E8.10.9.2"),sQuery(id+"F4.wireOp",EDGE,"E8.10.9.3"),sQuery(id+"F4.wireOp",EDGE,"E8.10.10.0"),sQuery(id+"F4.wireOp",EDGE,"E8.10.10.1"),sQuery(id+"F4.wireOp",EDGE,"E8.10.10.2"),sQuery(id+"F4.wireOp",EDGE,"E8.10.10.3"),sQuery(id+"F4.wireOp",EDGE,"E8.10.11.0"),sQuery(id+"F4.wireOp",EDGE,"E8.10.11.1"),sQuery(id+"F4.wireOp",EDGE,"E8.10.11.2"),sQuery(id+"F4.wireOp",EDGE,"E8.10.11.3"),sQuery(id+"F4.wireOp",EDGE,"E8.11.0.2"),sQuery(id+"F4.wireOp",EDGE,"E8.11.0.3"),sQuery(id+"F4.wireOp",EDGE,"E8.11.1.0"),sQuery(id+"F4.wireOp",EDGE,"E8.11.1.1"),sQuery(id+"F4.wireOp",EDGE,"E8.11.1.2"),sQuery(id+"F4.wireOp",EDGE,"E8.11.1.3"),sQuery(id+"F4.wireOp",EDGE,"E8.11.2.0"),sQuery(id+"F4.wireOp",EDGE,"E8.11.2.1"),sQuery(id+"F4.wireOp",EDGE,"E8.11.2.2"),sQuery(id+"F4.wireOp",EDGE,"E8.11.2.3"),sQuery(id+"F4.wireOp",EDGE,"E8.11.3.0"),sQuery(id+"F4.wireOp",EDGE,"E8.11.3.1"),sQuery(id+"F4.wireOp",EDGE,"E8.11.3.2"),sQuery(id+"F4.wireOp",EDGE,"E8.11.3.3"),sQuery(id+"F4.wireOp",EDGE,"E8.11.4.0"),sQuery(id+"F4.wireOp",EDGE,"E8.11.4.1"),sQuery(id+"F4.wireOp",EDGE,"E8.11.4.2"),sQuery(id+"F4.wireOp",EDGE,"E8.11.4.3"),sQuery(id+"F4.wireOp",EDGE,"E8.11.5.0"),sQuery(id+"F4.wireOp",EDGE,"E8.11.5.1"),sQuery(id+"F4.wireOp",EDGE,"E8.11.5.2"),sQuery(id+"F4.wireOp",EDGE,"E8.11.5.3"),sQuery(id+"F4.wireOp",EDGE,"E8.11.6.0"),sQuery(id+"F4.wireOp",EDGE,"E8.11.6.1"),sQuery(id+"F4.wireOp",EDGE,"E8.11.6.2"),sQuery(id+"F4.wireOp",EDGE,"E8.11.6.3"),sQuery(id+"F4.wireOp",EDGE,"E8.11.7.0"),sQuery(id+"F4.wireOp",EDGE,"E8.11.7.1"),sQuery(id+"F4.wireOp",EDGE,"E8.11.7.2"),sQuery(id+"F4.wireOp",EDGE,"E8.11.7.3"),sQuery(id+"F4.wireOp",EDGE,"E8.11.8.0"),sQuery(id+"F4.wireOp",EDGE,"E8.11.8.1"),sQuery(id+"F4.wireOp",EDGE,"E8.11.8.2"),sQuery(id+"F4.wireOp",EDGE,"E8.11.8.3"),sQuery(id+"F4.wireOp",EDGE,"E8.11.9.0"),sQuery(id+"F4.wireOp",EDGE,"E8.11.9.1"),sQuery(id+"F4.wireOp",EDGE,"E8.11.9.2"),sQuery(id+"F4.wireOp",EDGE,"E8.11.9.3"),sQuery(id+"F4.wireOp",EDGE,"E8.11.10.0"),sQuery(id+"F4.wireOp",EDGE,"E8.11.10.1"),sQuery(id+"F4.wireOp",EDGE,"E8.11.10.2"),sQuery(id+"F4.wireOp",EDGE,"E8.11.10.3"),sQuery(id+"F4.wireOp",EDGE,"E8.11.11.0"),sQuery(id+"F4.wireOp",EDGE,"E8.11.11.1"),sQuery(id+"F4.wireOp",EDGE,"E8.11.11.2"),sQuery(id+"F4.wireOp",EDGE,"E8.11.11.3"),sQuery(id+"F4.wireOp",EDGE,"E9.bottom"),sQuery(id+"F4.wireOp",EDGE,"E10.bottom"),sQuery(id+"F4.wireOp",EDGE,"E10.top"),sQuery(id+"F4.wireOp",EDGE,"E10.left"),sQuery(id+"F4.wireOp",EDGE,"E10.right")])]});
            transform(context, id + "F10", {"entities" : qUnion([Q0]), "transformType" : TransformType.TRANSLATION_3D, "dx" : 96 * mm, "dy" : 0 * mm, "dz" : 0 * mm, "makeCopy" : true});
        }
        {
            var Q0;
            Q0=makeQuery(id+"F1.opExtrude","SWEPT_BODY",BODY,{"disambiguationData":[OSD([sQuery(id+"F0.wireOp",EDGE,"E1.0.1.4"),sQuery(id+"F0.wireOp",EDGE,"E1.0.1.8"),sQuery(id+"F0.wireOp",EDGE,"E1.0.1.10"),sQuery(id+"F0.wireOp",EDGE,"E1.0.2.4"),sQuery(id+"F0.wireOp",EDGE,"E1.0.2.8"),sQuery(id+"F0.wireOp",EDGE,"E1.0.2.10"),sQuery(id+"F0.wireOp",EDGE,"E1.0.3.4"),sQuery(id+"F0.wireOp",EDGE,"E1.0.3.8"),sQuery(id+"F0.wireOp",EDGE,"E1.0.3.10"),sQuery(id+"F0.wireOp",EDGE,"E1.0.4.4"),sQuery(id+"F0.wireOp",EDGE,"E1.0.4.8"),sQuery(id+"F0.wireOp",EDGE,"E1.0.4.10"),sQuery(id+"F0.wireOp",EDGE,"E1.0.5.4"),sQuery(id+"F0.wireOp",EDGE,"E1.0.5.8"),sQuery(id+"F0.wireOp",EDGE,"E1.0.5.10"),sQuery(id+"F0.wireOp",EDGE,"E1.0.6.4"),sQuery(id+"F0.wireOp",EDGE,"E1.0.6.8"),sQuery(id+"F0.wireOp",EDGE,"E1.0.6.10"),sQuery(id+"F0.wireOp",EDGE,"E1.0.7.4"),sQuery(id+"F0.wireOp",EDGE,"E1.0.7.8"),sQuery(id+"F0.wireOp",EDGE,"E1.0.7.10"),sQuery(id+"F0.wireOp",EDGE,"E1.0.8.4"),sQuery(id+"F0.wireOp",EDGE,"E1.0.8.8"),sQuery(id+"F0.wireOp",EDGE,"E1.0.8.10"),sQuery(id+"F0.wireOp",EDGE,"E1.0.9.4"),sQuery(id+"F0.wireOp",EDGE,"E1.0.9.8"),sQuery(id+"F0.wireOp",EDGE,"E1.0.9.10"),sQuery(id+"F0.wireOp",EDGE,"E1.0.10.4"),sQuery(id+"F0.wireOp",EDGE,"E1.0.10.8"),sQuery(id+"F0.wireOp",EDGE,"E1.0.10.10"),sQuery(id+"F0.wireOp",EDGE,"E1.0.11.4"),sQuery(id+"F0.wireOp",EDGE,"E1.0.11.8"),sQuery(id+"F0.wireOp",EDGE,"E1.0.11.10"),sQuery(id+"F0.wireOp",EDGE,"E1.1.0.4"),sQuery(id+"F0.wireOp",EDGE,"E1.1.0.6"),sQuery(id+"F0.wireOp",EDGE,"E1.1.0.8"),sQuery(id+"F0.wireOp",EDGE,"E1.1.1.4"),sQuery(id+"F0.wireOp",EDGE,"E1.1.1.6"),sQuery(id+"F0.wireOp",EDGE,"E1.1.1.8"),sQuery(id+"F0.wireOp",EDGE,"E1.1.1.10"),sQuery(id+"F0.wireOp",EDGE,"E1.1.2.4"),sQuery(id+"F0.wireOp",EDGE,"E1.1.2.6"),sQuery(id+"F0.wireOp",EDGE,"E1.1.2.8"),sQuery(id+"F0.wireOp",EDGE,"E1.1.2.10"),sQuery(id+"F0.wireOp",EDGE,"E1.1.3.4"),sQuery(id+"F0.wireOp",EDGE,"E1.1.3.6"),sQuery(id+"F0.wireOp",EDGE,"E1.1.3.8"),sQuery(id+"F0.wireOp",EDGE,"E1.1.3.10"),sQuery(id+"F0.wireOp",EDGE,"E1.1.4.4"),sQuery(id+"F0.wireOp",EDGE,"E1.1.4.6"),sQuery(id+"F0.wireOp",EDGE,"E1.1.4.8"),sQuery(id+"F0.wireOp",EDGE,"E1.1.4.10"),sQuery(id+"F0.wireOp",EDGE,"E1.1.5.4"),sQuery(id+"F0.wireOp",EDGE,"E1.1.5.6"),sQuery(id+"F0.wireOp",EDGE,"E1.1.5.8"),sQuery(id+"F0.wireOp",EDGE,"E1.1.5.10"),sQuery(id+"F0.wireOp",EDGE,"E1.1.6.4"),sQuery(id+"F0.wireOp",EDGE,"E1.1.6.6"),sQuery(id+"F0.wireOp",EDGE,"E1.1.6.8"),sQuery(id+"F0.wireOp",EDGE,"E1.1.6.10"),sQuery(id+"F0.wireOp",EDGE,"E1.1.7.4"),sQuery(id+"F0.wireOp",EDGE,"E1.1.7.6"),sQuery(id+"F0.wireOp",EDGE,"E1.1.7.8"),sQuery(id+"F0.wireOp",EDGE,"E1.1.7.10"),sQuery(id+"F0.wireOp",EDGE,"E1.1.8.4"),sQuery(id+"F0.wireOp",EDGE,"E1.1.8.6"),sQuery(id+"F0.wireOp",EDGE,"E1.1.8.8"),sQuery(id+"F0.wireOp",EDGE,"E1.1.8.10"),sQuery(id+"F0.wireOp",EDGE,"E1.1.9.4"),sQuery(id+"F0.wireOp",EDGE,"E1.1.9.6"),sQuery(id+"F0.wireOp",EDGE,"E1.1.9.8"),sQuery(id+"F0.wireOp",EDGE,"E1.1.9.10"),sQuery(id+"F0.wireOp",EDGE,"E1.1.10.4"),sQuery(id+"F0.wireOp",EDGE,"E1.1.10.6"),sQuery(id+"F0.wireOp",EDGE,"E1.1.10.8"),sQuery(id+"F0.wireOp",EDGE,"E1.1.10.10"),sQuery(id+"F0.wireOp",EDGE,"E1.1.11.4"),sQuery(id+"F0.wireOp",EDGE,"E1.1.11.6"),sQuery(id+"F0.wireOp",EDGE,"E1.1.11.8"),sQuery(id+"F0.wireOp",EDGE,"E1.1.11.10"),sQuery(id+"F0.wireOp",EDGE,"E1.1.12.4"),sQuery(id+"F0.wireOp",EDGE,"E1.1.12.6"),sQuery(id+"F0.wireOp",EDGE,"E1.1.12.10"),sQuery(id+"F0.wireOp",EDGE,"E1.2.0.4"),sQuery(id+"F0.wireOp",EDGE,"E1.2.0.6"),sQuery(id+"F0.wireOp",EDGE,"E1.2.0.8"),sQuery(id+"F0.wireOp",EDGE,"E1.2.1.4"),sQuery(id+"F0.wireOp",EDGE,"E1.2.1.6"),sQuery(id+"F0.wireOp",EDGE,"E1.2.1.8"),sQuery(id+"F0.wireOp",EDGE,"E1.2.1.10"),sQuery(id+"F0.wireOp",EDGE,"E1.2.2.4"),sQuery(id+"F0.wireOp",EDGE,"E1.2.2.6"),sQuery(id+"F0.wireOp",EDGE,"E1.2.2.8"),sQuery(id+"F0.wireOp",EDGE,"E1.2.2.10"),sQuery(id+"F0.wireOp",EDGE,"E1.2.3.4"),sQuery(id+"F0.wireOp",EDGE,"E1.2.3.6"),sQuery(id+"F0.wireOp",EDGE,"E1.2.3.8"),sQuery(id+"F0.wireOp",EDGE,"E1.2.3.10"),sQuery(id+"F0.wireOp",EDGE,"E1.2.4.4"),sQuery(id+"F0.wireOp",EDGE,"E1.2.4.6"),sQuery(id+"F0.wireOp",EDGE,"E1.2.4.8"),sQuery(id+"F0.wireOp",EDGE,"E1.2.4.10"),sQuery(id+"F0.wireOp",EDGE,"E1.2.5.4"),sQuery(id+"F0.wireOp",EDGE,"E1.2.5.6"),sQuery(id+"F0.wireOp",EDGE,"E1.2.5.8"),sQuery(id+"F0.wireOp",EDGE,"E1.2.5.10"),sQuery(id+"F0.wireOp",EDGE,"E1.2.6.4"),sQuery(id+"F0.wireOp",EDGE,"E1.2.6.6"),sQuery(id+"F0.wireOp",EDGE,"E1.2.6.8"),sQuery(id+"F0.wireOp",EDGE,"E1.2.6.10"),sQuery(id+"F0.wireOp",EDGE,"E1.2.7.4"),sQuery(id+"F0.wireOp",EDGE,"E1.2.7.6"),sQuery(id+"F0.wireOp",EDGE,"E1.2.7.8"),sQuery(id+"F0.wireOp",EDGE,"E1.2.7.10"),sQuery(id+"F0.wireOp",EDGE,"E1.2.8.4"),sQuery(id+"F0.wireOp",EDGE,"E1.2.8.6"),sQuery(id+"F0.wireOp",EDGE,"E1.2.8.8"),sQuery(id+"F0.wireOp",EDGE,"E1.2.8.10"),sQuery(id+"F0.wireOp",EDGE,"E1.2.9.4"),sQuery(id+"F0.wireOp",EDGE,"E1.2.9.6"),sQuery(id+"F0.wireOp",EDGE,"E1.2.9.8"),sQuery(id+"F0.wireOp",EDGE,"E1.2.9.10"),sQuery(id+"F0.wireOp",EDGE,"E1.2.10.4"),sQuery(id+"F0.wireOp",EDGE,"E1.2.10.6"),sQuery(id+"F0.wireOp",EDGE,"E1.2.10.8"),sQuery(id+"F0.wireOp",EDGE,"E1.2.10.10"),sQuery(id+"F0.wireOp",EDGE,"E1.2.11.4"),sQuery(id+"F0.wireOp",EDGE,"E1.2.11.6"),sQuery(id+"F0.wireOp",EDGE,"E1.2.11.8"),sQuery(id+"F0.wireOp",EDGE,"E1.2.11.10"),sQuery(id+"F0.wireOp",EDGE,"E1.2.12.4"),sQuery(id+"F0.wireOp",EDGE,"E1.2.12.6"),sQuery(id+"F0.wireOp",EDGE,"E1.2.12.10"),sQuery(id+"F0.wireOp",EDGE,"E1.3.0.4"),sQuery(id+"F0.wireOp",EDGE,"E1.3.0.6"),sQuery(id+"F0.wireOp",EDGE,"E1.3.0.8"),sQuery(id+"F0.wireOp",EDGE,"E1.3.1.4"),sQuery(id+"F0.wireOp",EDGE,"E1.3.1.6"),sQuery(id+"F0.wireOp",EDGE,"E1.3.1.8"),sQuery(id+"F0.wireOp",EDGE,"E1.3.1.10"),sQuery(id+"F0.wireOp",EDGE,"E1.3.2.4"),sQuery(id+"F0.wireOp",EDGE,"E1.3.2.6"),sQuery(id+"F0.wireOp",EDGE,"E1.3.2.8"),sQuery(id+"F0.wireOp",EDGE,"E1.3.2.10"),sQuery(id+"F0.wireOp",EDGE,"E1.3.3.4"),sQuery(id+"F0.wireOp",EDGE,"E1.3.3.6"),sQuery(id+"F0.wireOp",EDGE,"E1.3.3.8"),sQuery(id+"F0.wireOp",EDGE,"E1.3.3.10"),sQuery(id+"F0.wireOp",EDGE,"E1.3.4.4"),sQuery(id+"F0.wireOp",EDGE,"E1.3.4.6"),sQuery(id+"F0.wireOp",EDGE,"E1.3.4.8"),sQuery(id+"F0.wireOp",EDGE,"E1.3.4.10"),sQuery(id+"F0.wireOp",EDGE,"E1.3.5.4"),sQuery(id+"F0.wireOp",EDGE,"E1.3.5.6"),sQuery(id+"F0.wireOp",EDGE,"E1.3.5.8"),sQuery(id+"F0.wireOp",EDGE,"E1.3.5.10"),sQuery(id+"F0.wireOp",EDGE,"E1.3.6.4"),sQuery(id+"F0.wireOp",EDGE,"E1.3.6.6"),sQuery(id+"F0.wireOp",EDGE,"E1.3.6.8"),sQuery(id+"F0.wireOp",EDGE,"E1.3.6.10"),sQuery(id+"F0.wireOp",EDGE,"E1.3.7.4"),sQuery(id+"F0.wireOp",EDGE,"E1.3.7.6"),sQuery(id+"F0.wireOp",EDGE,"E1.3.7.8"),sQuery(id+"F0.wireOp",EDGE,"E1.3.7.10"),sQuery(id+"F0.wireOp",EDGE,"E1.3.8.4"),sQuery(id+"F0.wireOp",EDGE,"E1.3.8.6"),sQuery(id+"F0.wireOp",EDGE,"E1.3.8.8"),sQuery(id+"F0.wireOp",EDGE,"E1.3.8.10"),sQuery(id+"F0.wireOp",EDGE,"E1.3.9.4"),sQuery(id+"F0.wireOp",EDGE,"E1.3.9.6"),sQuery(id+"F0.wireOp",EDGE,"E1.3.9.8"),sQuery(id+"F0.wireOp",EDGE,"E1.3.9.10"),sQuery(id+"F0.wireOp",EDGE,"E1.3.10.4"),sQuery(id+"F0.wireOp",EDGE,"E1.3.10.6"),sQuery(id+"F0.wireOp",EDGE,"E1.3.10.8"),sQuery(id+"F0.wireOp",EDGE,"E1.3.10.10"),sQuery(id+"F0.wireOp",EDGE,"E1.3.11.4"),sQuery(id+"F0.wireOp",EDGE,"E1.3.11.6"),sQuery(id+"F0.wireOp",EDGE,"E1.3.11.8"),sQuery(id+"F0.wireOp",EDGE,"E1.3.11.10"),sQuery(id+"F0.wireOp",EDGE,"E1.3.12.4"),sQuery(id+"F0.wireOp",EDGE,"E1.3.12.6"),sQuery(id+"F0.wireOp",EDGE,"E1.3.12.10"),sQuery(id+"F0.wireOp",EDGE,"E1.4.0.4"),sQuery(id+"F0.wireOp",EDGE,"E1.4.0.6"),sQuery(id+"F0.wireOp",EDGE,"E1.4.0.8"),sQuery(id+"F0.wireOp",EDGE,"E1.4.1.4"),sQuery(id+"F0.wireOp",EDGE,"E1.4.1.6"),sQuery(id+"F0.wireOp",EDGE,"E1.4.1.8"),sQuery(id+"F0.wireOp",EDGE,"E1.4.1.10"),sQuery(id+"F0.wireOp",EDGE,"E1.4.2.4"),sQuery(id+"F0.wireOp",EDGE,"E1.4.2.6"),sQuery(id+"F0.wireOp",EDGE,"E1.4.2.8"),sQuery(id+"F0.wireOp",EDGE,"E1.4.2.10"),sQuery(id+"F0.wireOp",EDGE,"E1.4.3.4"),sQuery(id+"F0.wireOp",EDGE,"E1.4.3.6"),sQuery(id+"F0.wireOp",EDGE,"E1.4.3.8"),sQuery(id+"F0.wireOp",EDGE,"E1.4.3.10"),sQuery(id+"F0.wireOp",EDGE,"E1.4.4.4"),sQuery(id+"F0.wireOp",EDGE,"E1.4.4.6"),sQuery(id+"F0.wireOp",EDGE,"E1.4.4.8"),sQuery(id+"F0.wireOp",EDGE,"E1.4.4.10"),sQuery(id+"F0.wireOp",EDGE,"E1.4.5.4"),sQuery(id+"F0.wireOp",EDGE,"E1.4.5.6"),sQuery(id+"F0.wireOp",EDGE,"E1.4.5.8"),sQuery(id+"F0.wireOp",EDGE,"E1.4.5.10"),sQuery(id+"F0.wireOp",EDGE,"E1.4.6.4"),sQuery(id+"F0.wireOp",EDGE,"E1.4.6.6"),sQuery(id+"F0.wireOp",EDGE,"E1.4.6.8"),sQuery(id+"F0.wireOp",EDGE,"E1.4.6.10"),sQuery(id+"F0.wireOp",EDGE,"E1.4.7.4"),sQuery(id+"F0.wireOp",EDGE,"E1.4.7.6"),sQuery(id+"F0.wireOp",EDGE,"E1.4.7.8"),sQuery(id+"F0.wireOp",EDGE,"E1.4.7.10"),sQuery(id+"F0.wireOp",EDGE,"E1.4.8.4"),sQuery(id+"F0.wireOp",EDGE,"E1.4.8.6"),sQuery(id+"F0.wireOp",EDGE,"E1.4.8.8"),sQuery(id+"F0.wireOp",EDGE,"E1.4.8.10"),sQuery(id+"F0.wireOp",EDGE,"E1.4.9.4"),sQuery(id+"F0.wireOp",EDGE,"E1.4.9.6"),sQuery(id+"F0.wireOp",EDGE,"E1.4.9.8"),sQuery(id+"F0.wireOp",EDGE,"E1.4.9.10"),sQuery(id+"F0.wireOp",EDGE,"E1.4.10.4"),sQuery(id+"F0.wireOp",EDGE,"E1.4.10.6"),sQuery(id+"F0.wireOp",EDGE,"E1.4.10.8"),sQuery(id+"F0.wireOp",EDGE,"E1.4.10.10"),sQuery(id+"F0.wireOp",EDGE,"E1.4.11.4"),sQuery(id+"F0.wireOp",EDGE,"E1.4.11.6"),sQuery(id+"F0.wireOp",EDGE,"E1.4.11.8"),sQuery(id+"F0.wireOp",EDGE,"E1.4.11.10"),sQuery(id+"F0.wireOp",EDGE,"E1.4.12.4"),sQuery(id+"F0.wireOp",EDGE,"E1.4.12.6"),sQuery(id+"F0.wireOp",EDGE,"E1.4.12.10"),sQuery(id+"F0.wireOp",EDGE,"E1.5.0.4"),sQuery(id+"F0.wireOp",EDGE,"E1.5.0.6"),sQuery(id+"F0.wireOp",EDGE,"E1.5.0.8"),sQuery(id+"F0.wireOp",EDGE,"E1.5.1.4"),sQuery(id+"F0.wireOp",EDGE,"E1.5.1.6"),sQuery(id+"F0.wireOp",EDGE,"E1.5.1.8"),sQuery(id+"F0.wireOp",EDGE,"E1.5.1.10"),sQuery(id+"F0.wireOp",EDGE,"E1.5.2.4"),sQuery(id+"F0.wireOp",EDGE,"E1.5.2.6"),sQuery(id+"F0.wireOp",EDGE,"E1.5.2.8"),sQuery(id+"F0.wireOp",EDGE,"E1.5.2.10"),sQuery(id+"F0.wireOp",EDGE,"E1.5.3.4"),sQuery(id+"F0.wireOp",EDGE,"E1.5.3.6"),sQuery(id+"F0.wireOp",EDGE,"E1.5.3.8"),sQuery(id+"F0.wireOp",EDGE,"E1.5.3.10"),sQuery(id+"F0.wireOp",EDGE,"E1.5.4.4"),sQuery(id+"F0.wireOp",EDGE,"E1.5.4.6"),sQuery(id+"F0.wireOp",EDGE,"E1.5.4.8"),sQuery(id+"F0.wireOp",EDGE,"E1.5.4.10"),sQuery(id+"F0.wireOp",EDGE,"E1.5.5.4"),sQuery(id+"F0.wireOp",EDGE,"E1.5.5.6"),sQuery(id+"F0.wireOp",EDGE,"E1.5.5.8"),sQuery(id+"F0.wireOp",EDGE,"E1.5.5.10"),sQuery(id+"F0.wireOp",EDGE,"E1.5.6.4"),sQuery(id+"F0.wireOp",EDGE,"E1.5.6.6"),sQuery(id+"F0.wireOp",EDGE,"E1.5.6.8"),sQuery(id+"F0.wireOp",EDGE,"E1.5.6.10"),sQuery(id+"F0.wireOp",EDGE,"E1.5.7.4"),sQuery(id+"F0.wireOp",EDGE,"E1.5.7.6"),sQuery(id+"F0.wireOp",EDGE,"E1.5.7.8"),sQuery(id+"F0.wireOp",EDGE,"E1.5.7.10"),sQuery(id+"F0.wireOp",EDGE,"E1.5.8.4"),sQuery(id+"F0.wireOp",EDGE,"E1.5.8.6"),sQuery(id+"F0.wireOp",EDGE,"E1.5.8.8"),sQuery(id+"F0.wireOp",EDGE,"E1.5.8.10"),sQuery(id+"F0.wireOp",EDGE,"E1.5.9.4"),sQuery(id+"F0.wireOp",EDGE,"E1.5.9.6"),sQuery(id+"F0.wireOp",EDGE,"E1.5.9.8"),sQuery(id+"F0.wireOp",EDGE,"E1.5.9.10"),sQuery(id+"F0.wireOp",EDGE,"E1.5.10.4"),sQuery(id+"F0.wireOp",EDGE,"E1.5.10.6"),sQuery(id+"F0.wireOp",EDGE,"E1.5.10.8"),sQuery(id+"F0.wireOp",EDGE,"E1.5.10.10"),sQuery(id+"F0.wireOp",EDGE,"E1.5.11.4"),sQuery(id+"F0.wireOp",EDGE,"E1.5.11.6"),sQuery(id+"F0.wireOp",EDGE,"E1.5.11.8"),sQuery(id+"F0.wireOp",EDGE,"E1.5.11.10"),sQuery(id+"F0.wireOp",EDGE,"E1.5.12.4"),sQuery(id+"F0.wireOp",EDGE,"E1.5.12.6"),sQuery(id+"F0.wireOp",EDGE,"E1.5.12.10"),sQuery(id+"F0.wireOp",EDGE,"E1.6.0.4"),sQuery(id+"F0.wireOp",EDGE,"E1.6.0.6"),sQuery(id+"F0.wireOp",EDGE,"E1.6.0.8"),sQuery(id+"F0.wireOp",EDGE,"E1.6.1.4"),sQuery(id+"F0.wireOp",EDGE,"E1.6.1.6"),sQuery(id+"F0.wireOp",EDGE,"E1.6.1.8"),sQuery(id+"F0.wireOp",EDGE,"E1.6.1.10"),sQuery(id+"F0.wireOp",EDGE,"E1.6.2.4"),sQuery(id+"F0.wireOp",EDGE,"E1.6.2.6"),sQuery(id+"F0.wireOp",EDGE,"E1.6.2.8"),sQuery(id+"F0.wireOp",EDGE,"E1.6.2.10"),sQuery(id+"F0.wireOp",EDGE,"E1.6.3.4"),sQuery(id+"F0.wireOp",EDGE,"E1.6.3.6"),sQuery(id+"F0.wireOp",EDGE,"E1.6.3.8"),sQuery(id+"F0.wireOp",EDGE,"E1.6.3.10"),sQuery(id+"F0.wireOp",EDGE,"E1.6.4.4"),sQuery(id+"F0.wireOp",EDGE,"E1.6.4.6"),sQuery(id+"F0.wireOp",EDGE,"E1.6.4.8"),sQuery(id+"F0.wireOp",EDGE,"E1.6.4.10"),sQuery(id+"F0.wireOp",EDGE,"E1.6.5.4"),sQuery(id+"F0.wireOp",EDGE,"E1.6.5.6"),sQuery(id+"F0.wireOp",EDGE,"E1.6.5.8"),sQuery(id+"F0.wireOp",EDGE,"E1.6.5.10"),sQuery(id+"F0.wireOp",EDGE,"E1.6.6.4"),sQuery(id+"F0.wireOp",EDGE,"E1.6.6.6"),sQuery(id+"F0.wireOp",EDGE,"E1.6.6.8"),sQuery(id+"F0.wireOp",EDGE,"E1.6.6.10"),sQuery(id+"F0.wireOp",EDGE,"E1.6.7.4"),sQuery(id+"F0.wireOp",EDGE,"E1.6.7.6"),sQuery(id+"F0.wireOp",EDGE,"E1.6.7.8"),sQuery(id+"F0.wireOp",EDGE,"E1.6.7.10"),sQuery(id+"F0.wireOp",EDGE,"E1.6.8.4"),sQuery(id+"F0.wireOp",EDGE,"E1.6.8.6"),sQuery(id+"F0.wireOp",EDGE,"E1.6.8.8"),sQuery(id+"F0.wireOp",EDGE,"E1.6.8.10"),sQuery(id+"F0.wireOp",EDGE,"E1.6.9.4"),sQuery(id+"F0.wireOp",EDGE,"E1.6.9.6"),sQuery(id+"F0.wireOp",EDGE,"E1.6.9.8"),sQuery(id+"F0.wireOp",EDGE,"E1.6.9.10"),sQuery(id+"F0.wireOp",EDGE,"E1.6.10.4"),sQuery(id+"F0.wireOp",EDGE,"E1.6.10.6"),sQuery(id+"F0.wireOp",EDGE,"E1.6.10.8"),sQuery(id+"F0.wireOp",EDGE,"E1.6.10.10"),sQuery(id+"F0.wireOp",EDGE,"E1.6.11.4"),sQuery(id+"F0.wireOp",EDGE,"E1.6.11.6"),sQuery(id+"F0.wireOp",EDGE,"E1.6.11.8"),sQuery(id+"F0.wireOp",EDGE,"E1.6.11.10"),sQuery(id+"F0.wireOp",EDGE,"E1.6.12.4"),sQuery(id+"F0.wireOp",EDGE,"E1.6.12.6"),sQuery(id+"F0.wireOp",EDGE,"E1.6.12.10"),sQuery(id+"F0.wireOp",EDGE,"E1.7.0.4"),sQuery(id+"F0.wireOp",EDGE,"E1.7.0.6"),sQuery(id+"F0.wireOp",EDGE,"E1.7.0.8"),sQuery(id+"F0.wireOp",EDGE,"E1.7.1.4"),sQuery(id+"F0.wireOp",EDGE,"E1.7.1.6"),sQuery(id+"F0.wireOp",EDGE,"E1.7.1.8"),sQuery(id+"F0.wireOp",EDGE,"E1.7.1.10"),sQuery(id+"F0.wireOp",EDGE,"E1.7.2.4"),sQuery(id+"F0.wireOp",EDGE,"E1.7.2.6"),sQuery(id+"F0.wireOp",EDGE,"E1.7.2.8"),sQuery(id+"F0.wireOp",EDGE,"E1.7.2.10"),sQuery(id+"F0.wireOp",EDGE,"E1.7.3.4"),sQuery(id+"F0.wireOp",EDGE,"E1.7.3.6"),sQuery(id+"F0.wireOp",EDGE,"E1.7.3.8"),sQuery(id+"F0.wireOp",EDGE,"E1.7.3.10"),sQuery(id+"F0.wireOp",EDGE,"E1.7.4.4"),sQuery(id+"F0.wireOp",EDGE,"E1.7.4.6"),sQuery(id+"F0.wireOp",EDGE,"E1.7.4.8"),sQuery(id+"F0.wireOp",EDGE,"E1.7.4.10"),sQuery(id+"F0.wireOp",EDGE,"E1.7.5.4"),sQuery(id+"F0.wireOp",EDGE,"E1.7.5.6"),sQuery(id+"F0.wireOp",EDGE,"E1.7.5.8"),sQuery(id+"F0.wireOp",EDGE,"E1.7.5.10"),sQuery(id+"F0.wireOp",EDGE,"E1.7.6.4"),sQuery(id+"F0.wireOp",EDGE,"E1.7.6.6"),sQuery(id+"F0.wireOp",EDGE,"E1.7.6.8"),sQuery(id+"F0.wireOp",EDGE,"E1.7.6.10"),sQuery(id+"F0.wireOp",EDGE,"E1.7.7.4"),sQuery(id+"F0.wireOp",EDGE,"E1.7.7.6"),sQuery(id+"F0.wireOp",EDGE,"E1.7.7.8"),sQuery(id+"F0.wireOp",EDGE,"E1.7.7.10"),sQuery(id+"F0.wireOp",EDGE,"E1.7.8.4"),sQuery(id+"F0.wireOp",EDGE,"E1.7.8.6"),sQuery(id+"F0.wireOp",EDGE,"E1.7.8.8"),sQuery(id+"F0.wireOp",EDGE,"E1.7.8.10"),sQuery(id+"F0.wireOp",EDGE,"E1.7.9.4"),sQuery(id+"F0.wireOp",EDGE,"E1.7.9.6"),sQuery(id+"F0.wireOp",EDGE,"E1.7.9.8"),sQuery(id+"F0.wireOp",EDGE,"E1.7.9.10"),sQuery(id+"F0.wireOp",EDGE,"E1.7.10.4"),sQuery(id+"F0.wireOp",EDGE,"E1.7.10.6"),sQuery(id+"F0.wireOp",EDGE,"E1.7.10.8"),sQuery(id+"F0.wireOp",EDGE,"E1.7.10.10"),sQuery(id+"F0.wireOp",EDGE,"E1.7.11.4"),sQuery(id+"F0.wireOp",EDGE,"E1.7.11.6"),sQuery(id+"F0.wireOp",EDGE,"E1.7.11.8"),sQuery(id+"F0.wireOp",EDGE,"E1.7.11.10"),sQuery(id+"F0.wireOp",EDGE,"E1.7.12.4"),sQuery(id+"F0.wireOp",EDGE,"E1.7.12.6"),sQuery(id+"F0.wireOp",EDGE,"E1.7.12.10"),sQuery(id+"F0.wireOp",EDGE,"E1.8.0.4"),sQuery(id+"F0.wireOp",EDGE,"E1.8.0.6"),sQuery(id+"F0.wireOp",EDGE,"E1.8.0.8"),sQuery(id+"F0.wireOp",EDGE,"E1.8.1.4"),sQuery(id+"F0.wireOp",EDGE,"E1.8.1.6"),sQuery(id+"F0.wireOp",EDGE,"E1.8.1.8"),sQuery(id+"F0.wireOp",EDGE,"E1.8.1.10"),sQuery(id+"F0.wireOp",EDGE,"E1.8.2.4"),sQuery(id+"F0.wireOp",EDGE,"E1.8.2.6"),sQuery(id+"F0.wireOp",EDGE,"E1.8.2.8"),sQuery(id+"F0.wireOp",EDGE,"E1.8.2.10"),sQuery(id+"F0.wireOp",EDGE,"E1.8.3.4"),sQuery(id+"F0.wireOp",EDGE,"E1.8.3.6"),sQuery(id+"F0.wireOp",EDGE,"E1.8.3.8"),sQuery(id+"F0.wireOp",EDGE,"E1.8.3.10"),sQuery(id+"F0.wireOp",EDGE,"E1.8.4.4"),sQuery(id+"F0.wireOp",EDGE,"E1.8.4.6"),sQuery(id+"F0.wireOp",EDGE,"E1.8.4.8"),sQuery(id+"F0.wireOp",EDGE,"E1.8.4.10"),sQuery(id+"F0.wireOp",EDGE,"E1.8.5.4"),sQuery(id+"F0.wireOp",EDGE,"E1.8.5.6"),sQuery(id+"F0.wireOp",EDGE,"E1.8.5.8"),sQuery(id+"F0.wireOp",EDGE,"E1.8.5.10"),sQuery(id+"F0.wireOp",EDGE,"E1.8.6.4"),sQuery(id+"F0.wireOp",EDGE,"E1.8.6.6"),sQuery(id+"F0.wireOp",EDGE,"E1.8.6.8"),sQuery(id+"F0.wireOp",EDGE,"E1.8.6.10"),sQuery(id+"F0.wireOp",EDGE,"E1.8.7.4"),sQuery(id+"F0.wireOp",EDGE,"E1.8.7.6"),sQuery(id+"F0.wireOp",EDGE,"E1.8.7.8"),sQuery(id+"F0.wireOp",EDGE,"E1.8.7.10"),sQuery(id+"F0.wireOp",EDGE,"E1.8.8.4"),sQuery(id+"F0.wireOp",EDGE,"E1.8.8.6"),sQuery(id+"F0.wireOp",EDGE,"E1.8.8.8"),sQuery(id+"F0.wireOp",EDGE,"E1.8.8.10"),sQuery(id+"F0.wireOp",EDGE,"E1.8.9.4"),sQuery(id+"F0.wireOp",EDGE,"E1.8.9.6"),sQuery(id+"F0.wireOp",EDGE,"E1.8.9.8"),sQuery(id+"F0.wireOp",EDGE,"E1.8.9.10"),sQuery(id+"F0.wireOp",EDGE,"E1.8.10.4"),sQuery(id+"F0.wireOp",EDGE,"E1.8.10.6"),sQuery(id+"F0.wireOp",EDGE,"E1.8.10.8"),sQuery(id+"F0.wireOp",EDGE,"E1.8.10.10"),sQuery(id+"F0.wireOp",EDGE,"E1.8.11.4"),sQuery(id+"F0.wireOp",EDGE,"E1.8.11.6"),sQuery(id+"F0.wireOp",EDGE,"E1.8.11.8"),sQuery(id+"F0.wireOp",EDGE,"E1.8.11.10"),sQuery(id+"F0.wireOp",EDGE,"E1.8.12.4"),sQuery(id+"F0.wireOp",EDGE,"E1.8.12.6"),sQuery(id+"F0.wireOp",EDGE,"E1.8.12.10"),sQuery(id+"F0.wireOp",EDGE,"E1.9.0.4"),sQuery(id+"F0.wireOp",EDGE,"E1.9.0.6"),sQuery(id+"F0.wireOp",EDGE,"E1.9.0.8"),sQuery(id+"F0.wireOp",EDGE,"E1.9.1.4"),sQuery(id+"F0.wireOp",EDGE,"E1.9.1.6"),sQuery(id+"F0.wireOp",EDGE,"E1.9.1.8"),sQuery(id+"F0.wireOp",EDGE,"E1.9.1.10"),sQuery(id+"F0.wireOp",EDGE,"E1.9.2.4"),sQuery(id+"F0.wireOp",EDGE,"E1.9.2.6"),sQuery(id+"F0.wireOp",EDGE,"E1.9.2.8"),sQuery(id+"F0.wireOp",EDGE,"E1.9.2.10"),sQuery(id+"F0.wireOp",EDGE,"E1.9.3.4"),sQuery(id+"F0.wireOp",EDGE,"E1.9.3.6"),sQuery(id+"F0.wireOp",EDGE,"E1.9.3.8"),sQuery(id+"F0.wireOp",EDGE,"E1.9.3.10"),sQuery(id+"F0.wireOp",EDGE,"E1.9.4.4"),sQuery(id+"F0.wireOp",EDGE,"E1.9.4.6"),sQuery(id+"F0.wireOp",EDGE,"E1.9.4.8"),sQuery(id+"F0.wireOp",EDGE,"E1.9.4.10"),sQuery(id+"F0.wireOp",EDGE,"E1.9.5.4"),sQuery(id+"F0.wireOp",EDGE,"E1.9.5.6"),sQuery(id+"F0.wireOp",EDGE,"E1.9.5.8"),sQuery(id+"F0.wireOp",EDGE,"E1.9.5.10"),sQuery(id+"F0.wireOp",EDGE,"E1.9.6.4"),sQuery(id+"F0.wireOp",EDGE,"E1.9.6.6"),sQuery(id+"F0.wireOp",EDGE,"E1.9.6.8"),sQuery(id+"F0.wireOp",EDGE,"E1.9.6.10"),sQuery(id+"F0.wireOp",EDGE,"E1.9.7.4"),sQuery(id+"F0.wireOp",EDGE,"E1.9.7.6"),sQuery(id+"F0.wireOp",EDGE,"E1.9.7.8"),sQuery(id+"F0.wireOp",EDGE,"E1.9.7.10"),sQuery(id+"F0.wireOp",EDGE,"E1.9.8.4"),sQuery(id+"F0.wireOp",EDGE,"E1.9.8.6"),sQuery(id+"F0.wireOp",EDGE,"E1.9.8.8"),sQuery(id+"F0.wireOp",EDGE,"E1.9.8.10"),sQuery(id+"F0.wireOp",EDGE,"E1.9.9.4"),sQuery(id+"F0.wireOp",EDGE,"E1.9.9.6"),sQuery(id+"F0.wireOp",EDGE,"E1.9.9.8"),sQuery(id+"F0.wireOp",EDGE,"E1.9.9.10"),sQuery(id+"F0.wireOp",EDGE,"E1.9.10.4"),sQuery(id+"F0.wireOp",EDGE,"E1.9.10.6"),sQuery(id+"F0.wireOp",EDGE,"E1.9.10.8"),sQuery(id+"F0.wireOp",EDGE,"E1.9.10.10"),sQuery(id+"F0.wireOp",EDGE,"E1.9.11.4"),sQuery(id+"F0.wireOp",EDGE,"E1.9.11.6"),sQuery(id+"F0.wireOp",EDGE,"E1.9.11.8"),sQuery(id+"F0.wireOp",EDGE,"E1.9.11.10"),sQuery(id+"F0.wireOp",EDGE,"E1.9.12.4"),sQuery(id+"F0.wireOp",EDGE,"E1.9.12.6"),sQuery(id+"F0.wireOp",EDGE,"E1.9.12.10"),sQuery(id+"F0.wireOp",EDGE,"E1.10.0.4"),sQuery(id+"F0.wireOp",EDGE,"E1.10.0.6"),sQuery(id+"F0.wireOp",EDGE,"E1.10.0.8"),sQuery(id+"F0.wireOp",EDGE,"E1.10.1.4"),sQuery(id+"F0.wireOp",EDGE,"E1.10.1.6"),sQuery(id+"F0.wireOp",EDGE,"E1.10.1.8"),sQuery(id+"F0.wireOp",EDGE,"E1.10.1.10"),sQuery(id+"F0.wireOp",EDGE,"E1.10.2.4"),sQuery(id+"F0.wireOp",EDGE,"E1.10.2.6"),sQuery(id+"F0.wireOp",EDGE,"E1.10.2.8"),sQuery(id+"F0.wireOp",EDGE,"E1.10.2.10"),sQuery(id+"F0.wireOp",EDGE,"E1.10.3.4"),sQuery(id+"F0.wireOp",EDGE,"E1.10.3.6"),sQuery(id+"F0.wireOp",EDGE,"E1.10.3.8"),sQuery(id+"F0.wireOp",EDGE,"E1.10.3.10"),sQuery(id+"F0.wireOp",EDGE,"E1.10.4.4"),sQuery(id+"F0.wireOp",EDGE,"E1.10.4.6"),sQuery(id+"F0.wireOp",EDGE,"E1.10.4.8"),sQuery(id+"F0.wireOp",EDGE,"E1.10.4.10"),sQuery(id+"F0.wireOp",EDGE,"E1.10.5.4"),sQuery(id+"F0.wireOp",EDGE,"E1.10.5.6"),sQuery(id+"F0.wireOp",EDGE,"E1.10.5.8"),sQuery(id+"F0.wireOp",EDGE,"E1.10.5.10"),sQuery(id+"F0.wireOp",EDGE,"E1.10.6.4"),sQuery(id+"F0.wireOp",EDGE,"E1.10.6.6"),sQuery(id+"F0.wireOp",EDGE,"E1.10.6.8"),sQuery(id+"F0.wireOp",EDGE,"E1.10.6.10"),sQuery(id+"F0.wireOp",EDGE,"E1.10.7.4"),sQuery(id+"F0.wireOp",EDGE,"E1.10.7.6"),sQuery(id+"F0.wireOp",EDGE,"E1.10.7.8"),sQuery(id+"F0.wireOp",EDGE,"E1.10.7.10"),sQuery(id+"F0.wireOp",EDGE,"E1.10.8.4"),sQuery(id+"F0.wireOp",EDGE,"E1.10.8.6"),sQuery(id+"F0.wireOp",EDGE,"E1.10.8.8"),sQuery(id+"F0.wireOp",EDGE,"E1.10.8.10"),sQuery(id+"F0.wireOp",EDGE,"E1.10.9.4"),sQuery(id+"F0.wireOp",EDGE,"E1.10.9.6"),sQuery(id+"F0.wireOp",EDGE,"E1.10.9.8"),sQuery(id+"F0.wireOp",EDGE,"E1.10.9.10"),sQuery(id+"F0.wireOp",EDGE,"E1.10.10.4"),sQuery(id+"F0.wireOp",EDGE,"E1.10.10.6"),sQuery(id+"F0.wireOp",EDGE,"E1.10.10.8"),sQuery(id+"F0.wireOp",EDGE,"E1.10.10.10"),sQuery(id+"F0.wireOp",EDGE,"E1.10.11.4"),sQuery(id+"F0.wireOp",EDGE,"E1.10.11.6"),sQuery(id+"F0.wireOp",EDGE,"E1.10.11.8"),sQuery(id+"F0.wireOp",EDGE,"E1.10.11.10"),sQuery(id+"F0.wireOp",EDGE,"E1.10.12.4"),sQuery(id+"F0.wireOp",EDGE,"E1.10.12.6"),sQuery(id+"F0.wireOp",EDGE,"E1.10.12.10"),sQuery(id+"F0.wireOp",EDGE,"E1.11.0.4"),sQuery(id+"F0.wireOp",EDGE,"E1.11.0.6"),sQuery(id+"F0.wireOp",EDGE,"E1.11.0.8"),sQuery(id+"F0.wireOp",EDGE,"E1.11.1.4"),sQuery(id+"F0.wireOp",EDGE,"E1.11.1.6"),sQuery(id+"F0.wireOp",EDGE,"E1.11.1.8"),sQuery(id+"F0.wireOp",EDGE,"E1.11.1.10"),sQuery(id+"F0.wireOp",EDGE,"E1.11.2.4"),sQuery(id+"F0.wireOp",EDGE,"E1.11.2.6"),sQuery(id+"F0.wireOp",EDGE,"E1.11.2.8"),sQuery(id+"F0.wireOp",EDGE,"E1.11.2.10"),sQuery(id+"F0.wireOp",EDGE,"E1.11.3.4"),sQuery(id+"F0.wireOp",EDGE,"E1.11.3.6"),sQuery(id+"F0.wireOp",EDGE,"E1.11.3.8"),sQuery(id+"F0.wireOp",EDGE,"E1.11.3.10"),sQuery(id+"F0.wireOp",EDGE,"E1.11.4.4"),sQuery(id+"F0.wireOp",EDGE,"E1.11.4.6"),sQuery(id+"F0.wireOp",EDGE,"E1.11.4.8"),sQuery(id+"F0.wireOp",EDGE,"E1.11.4.10"),sQuery(id+"F0.wireOp",EDGE,"E1.11.5.4"),sQuery(id+"F0.wireOp",EDGE,"E1.11.5.6"),sQuery(id+"F0.wireOp",EDGE,"E1.11.5.8"),sQuery(id+"F0.wireOp",EDGE,"E1.11.5.10"),sQuery(id+"F0.wireOp",EDGE,"E1.11.6.4"),sQuery(id+"F0.wireOp",EDGE,"E1.11.6.6"),sQuery(id+"F0.wireOp",EDGE,"E1.11.6.8"),sQuery(id+"F0.wireOp",EDGE,"E1.11.6.10"),sQuery(id+"F0.wireOp",EDGE,"E1.11.7.4"),sQuery(id+"F0.wireOp",EDGE,"E1.11.7.6"),sQuery(id+"F0.wireOp",EDGE,"E1.11.7.8"),sQuery(id+"F0.wireOp",EDGE,"E1.11.7.10"),sQuery(id+"F0.wireOp",EDGE,"E1.11.8.4"),sQuery(id+"F0.wireOp",EDGE,"E1.11.8.6"),sQuery(id+"F0.wireOp",EDGE,"E1.11.8.8"),sQuery(id+"F0.wireOp",EDGE,"E1.11.8.10"),sQuery(id+"F0.wireOp",EDGE,"E1.11.9.4"),sQuery(id+"F0.wireOp",EDGE,"E1.11.9.6"),sQuery(id+"F0.wireOp",EDGE,"E1.11.9.8"),sQuery(id+"F0.wireOp",EDGE,"E1.11.9.10"),sQuery(id+"F0.wireOp",EDGE,"E1.11.10.4"),sQuery(id+"F0.wireOp",EDGE,"E1.11.10.6"),sQuery(id+"F0.wireOp",EDGE,"E1.11.10.8"),sQuery(id+"F0.wireOp",EDGE,"E1.11.10.10"),sQuery(id+"F0.wireOp",EDGE,"E1.11.11.4"),sQuery(id+"F0.wireOp",EDGE,"E1.11.11.6"),sQuery(id+"F0.wireOp",EDGE,"E1.11.11.8"),sQuery(id+"F0.wireOp",EDGE,"E1.11.11.10"),sQuery(id+"F0.wireOp",EDGE,"E1.11.12.4"),sQuery(id+"F0.wireOp",EDGE,"E1.11.12.6"),sQuery(id+"F0.wireOp",EDGE,"E1.11.12.10"),sQuery(id+"F0.wireOp",EDGE,"E1.12.1.6"),sQuery(id+"F0.wireOp",EDGE,"E1.12.1.8"),sQuery(id+"F0.wireOp",EDGE,"E1.12.1.10"),sQuery(id+"F0.wireOp",EDGE,"E1.12.2.6"),sQuery(id+"F0.wireOp",EDGE,"E1.12.2.8"),sQuery(id+"F0.wireOp",EDGE,"E1.12.2.10"),sQuery(id+"F0.wireOp",EDGE,"E1.12.3.6"),sQuery(id+"F0.wireOp",EDGE,"E1.12.3.8"),sQuery(id+"F0.wireOp",EDGE,"E1.12.3.10"),sQuery(id+"F0.wireOp",EDGE,"E1.12.4.6"),sQuery(id+"F0.wireOp",EDGE,"E1.12.4.8"),sQuery(id+"F0.wireOp",EDGE,"E1.12.4.10"),sQuery(id+"F0.wireOp",EDGE,"E1.12.5.6"),sQuery(id+"F0.wireOp",EDGE,"E1.12.5.8"),sQuery(id+"F0.wireOp",EDGE,"E1.12.5.10"),sQuery(id+"F0.wireOp",EDGE,"E1.12.6.6"),sQuery(id+"F0.wireOp",EDGE,"E1.12.6.8"),sQuery(id+"F0.wireOp",EDGE,"E1.12.6.10"),sQuery(id+"F0.wireOp",EDGE,"E1.12.7.6"),sQuery(id+"F0.wireOp",EDGE,"E1.12.7.8"),sQuery(id+"F0.wireOp",EDGE,"E1.12.7.10"),sQuery(id+"F0.wireOp",EDGE,"E1.12.8.6"),sQuery(id+"F0.wireOp",EDGE,"E1.12.8.8"),sQuery(id+"F0.wireOp",EDGE,"E1.12.8.10"),sQuery(id+"F0.wireOp",EDGE,"E1.12.9.6"),sQuery(id+"F0.wireOp",EDGE,"E1.12.9.8"),sQuery(id+"F0.wireOp",EDGE,"E1.12.9.10"),sQuery(id+"F0.wireOp",EDGE,"E1.12.10.6"),sQuery(id+"F0.wireOp",EDGE,"E1.12.10.8"),sQuery(id+"F0.wireOp",EDGE,"E1.12.10.10"),sQuery(id+"F0.wireOp",EDGE,"E1.12.11.6"),sQuery(id+"F0.wireOp",EDGE,"E1.12.11.8"),sQuery(id+"F0.wireOp",EDGE,"E1.12.11.10"),sQuery(id+"F0.wireOp",EDGE,"E2.bottom"),sQuery(id+"F0.wireOp",EDGE,"E2.top"),sQuery(id+"F0.wireOp",EDGE,"E2.left"),sQuery(id+"F0.wireOp",EDGE,"E2.right")])]});
            transform(context, id + "F11", {"entities" : qUnion([Q0]), "transformType" : TransformType.TRANSLATION_3D, "dx" : 0 * mm, "dy" : 0 * mm, "dz" : -50 * mm, "makeCopy" : false});
        }
        {
            var Q0;
            Q0=qCreatedBy(makeId("Top.planeOp"),FACE);
            var sketch = newSketch(context, id + "F12", { "sketchPlane" : qUnion([Q0])});
            skLineSegment(sketch, "E11.rect.bottom", {"start": v(10.5, -12.5) * mm, "end": v(-10.5, -12.5) * mm});
            skLineSegment(sketch, "E11.rect.top", {"start": v(10.5, 12.5) * mm, "end": v(-10.5, 12.5) * mm});
            skLineSegment(sketch, "E11.rect.left", {"start": v(12.5, -10.5) * mm, "end": v(12.5, 10.5) * mm});
            skLineSegment(sketch, "E11.rect.right", {"start": v(-12.5, -10.5) * mm, "end": v(-12.5, 10.5) * mm});
            skPoint(sketch, "E11.rect.middle", {"position": v(0, 0) * mm});
            skPoint(sketch, "E12.visualSharp", {"position": v(-12.5, 12.5) * mm});
            skArc(sketch, "E12.filletArc", {"start": v(-10.5, 12.5) * mm, "mid": v(-11.91, 11.91) * mm, "end": v(-12.5, 10.5) * mm});
            skPoint(sketch, "E13.visualSharp", {"position": v(12.5, 12.5) * mm});
            skArc(sketch, "E13.filletArc", {"start": v(12.5, 10.5) * mm, "mid": v(11.91, 11.91) * mm, "end": v(10.5, 12.5) * mm});
            skPoint(sketch, "E14.visualSharp", {"position": v(12.5, -12.5) * mm});
            skArc(sketch, "E14.filletArc", {"start": v(10.5, -12.5) * mm, "mid": v(11.91, -11.91) * mm, "end": v(12.5, -10.5) * mm});
            skPoint(sketch, "E15.visualSharp", {"position": v(-12.5, -12.5) * mm});
            skArc(sketch, "E15.filletArc", {"start": v(-12.5, -10.5) * mm, "mid": v(-11.91, -11.91) * mm, "end": v(-10.5, -12.5) * mm});
            skSolve(sketch);
        }
        {
            var Q0;
            Q0 = qSketchRegion(id + "F12", true);
            extrude(context, id + "F13", {"entities" : qUnion([Q0]), "operationType" : NewBodyOperationType.REMOVE, "endBound" : BoundingType.THROUGH_ALL, "oppositeDirection" : true, "depth" : 25 * mm});
        }
        {
            var Q0;
            Q0 = qSketchRegion(id + "F12", true);
            extrude(context, id + "F14", {"entities" : qUnion([Q0]), "operationType" : NewBodyOperationType.REMOVE, "endBound" : BoundingType.THROUGH_ALL, "depth" : 25 * mm});
        }
    });
